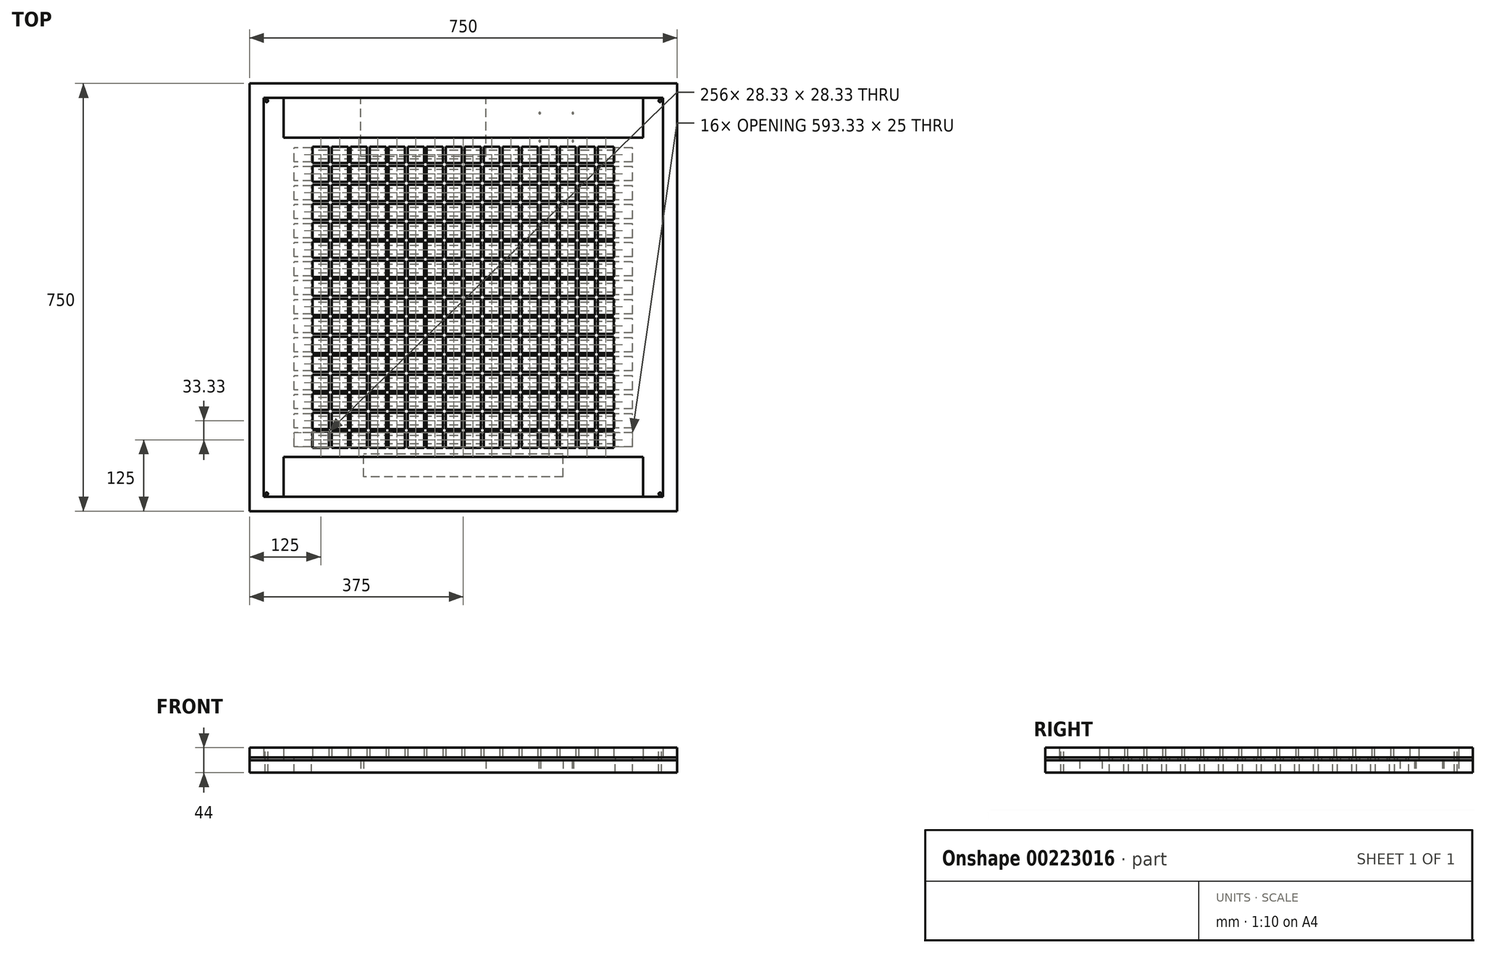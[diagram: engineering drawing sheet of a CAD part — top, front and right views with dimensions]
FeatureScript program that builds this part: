
annotation { "Feature Type Name" : "Feature", "Feature Type Description" : "" }
export const myFeature = defineFeature(function(context is Context, id is Id, definition is map)
    precondition{}
    {
        {
            var Q0;
            Q0=qCreatedBy(makeId("Top.planeOp"),FACE);
            var sketch = newSketch(context, id + "F0", { "sketchPlane" : qUnion([Q0])});
            skLineSegment(sketch, "E0.bottom", {"start": v(375, 375) * mm, "end": v(-375, 375) * mm});
            skLineSegment(sketch, "E0.top", {"start": v(375, -375) * mm, "end": v(-375, -375) * mm});
            skLineSegment(sketch, "E0.left", {"start": v(375, 375) * mm, "end": v(375, -375) * mm});
            skLineSegment(sketch, "E0.right", {"start": v(-375, 375) * mm, "end": v(-375, -375) * mm});
            skPoint(sketch, "E0.middle", {"position": v(0, 0) * mm});
            skLineSegment(sketch, "E1", {"start": v(0, 0) * mm, "end": v(0, 250) * mm});
            skLineSegment(sketch, "E2.bottom", {"start": v(266.67, 257.5) * mm, "end": v(-266.67, 257.5) * mm});
            skLineSegment(sketch, "E2.top", {"start": v(266.67, 242.5) * mm, "end": v(-266.67, 242.5) * mm});
            skLineSegment(sketch, "E2.left", {"start": v(266.67, 257.5) * mm, "end": v(266.67, 242.5) * mm});
            skLineSegment(sketch, "E2.right", {"start": v(-266.67, 257.5) * mm, "end": v(-266.67, 242.5) * mm});
            skPoint(sketch, "E2.middle", {"position": v(0, 250) * mm});
            skLineSegment(sketch, "E3.0.1.0", {"start": v(266.67, 224.17) * mm, "end": v(-266.67, 224.17) * mm});
            skLineSegment(sketch, "E3.0.1.1", {"start": v(266.67, 209.17) * mm, "end": v(-266.67, 209.17) * mm});
            skLineSegment(sketch, "E3.0.1.2", {"start": v(266.67, 224.17) * mm, "end": v(266.67, 209.17) * mm});
            skLineSegment(sketch, "E3.0.1.3", {"start": v(-266.67, 224.17) * mm, "end": v(-266.67, 209.17) * mm});
            skLineSegment(sketch, "E3.direction1", {"start": v(-266.67, 257.5) * mm, "end": v(-241.67, 257.5) * mm, "construction": true});
            skLineSegment(sketch, "E3.direction2", {"start": v(-266.67, 257.5) * mm, "end": v(-266.67, 224.17) * mm, "construction": true});
            skLineSegment(sketch, "E4.0.0.2", {"start": v(266.67, 190.83) * mm, "end": v(-266.67, 190.83) * mm});
            skLineSegment(sketch, "E4.3.0.2", {"start": v(266.67, 175.83) * mm, "end": v(-266.67, 175.83) * mm});
            skLineSegment(sketch, "E4.6.0.2", {"start": v(266.67, 190.83) * mm, "end": v(266.67, 175.83) * mm});
            skLineSegment(sketch, "E4.9.0.2", {"start": v(-266.67, 190.83) * mm, "end": v(-266.67, 175.83) * mm});
            skLineSegment(sketch, "E4.0.0.3", {"start": v(266.67, 157.5) * mm, "end": v(-266.67, 157.5) * mm});
            skLineSegment(sketch, "E4.3.0.3", {"start": v(266.67, 142.5) * mm, "end": v(-266.67, 142.5) * mm});
            skLineSegment(sketch, "E4.6.0.3", {"start": v(266.67, 157.5) * mm, "end": v(266.67, 142.5) * mm});
            skLineSegment(sketch, "E4.9.0.3", {"start": v(-266.67, 157.5) * mm, "end": v(-266.67, 142.5) * mm});
            skLineSegment(sketch, "E4.0.0.4", {"start": v(266.67, 124.17) * mm, "end": v(-266.67, 124.17) * mm});
            skLineSegment(sketch, "E4.3.0.4", {"start": v(266.67, 109.17) * mm, "end": v(-266.67, 109.17) * mm});
            skLineSegment(sketch, "E4.6.0.4", {"start": v(266.67, 124.17) * mm, "end": v(266.67, 109.17) * mm});
            skLineSegment(sketch, "E4.9.0.4", {"start": v(-266.67, 124.17) * mm, "end": v(-266.67, 109.17) * mm});
            skLineSegment(sketch, "E4.0.0.5", {"start": v(266.67, 90.83) * mm, "end": v(-266.67, 90.83) * mm});
            skLineSegment(sketch, "E4.3.0.5", {"start": v(266.67, 75.83) * mm, "end": v(-266.67, 75.83) * mm});
            skLineSegment(sketch, "E4.6.0.5", {"start": v(266.67, 90.83) * mm, "end": v(266.67, 75.83) * mm});
            skLineSegment(sketch, "E4.9.0.5", {"start": v(-266.67, 90.83) * mm, "end": v(-266.67, 75.83) * mm});
            skLineSegment(sketch, "E4.0.0.6", {"start": v(266.67, 57.5) * mm, "end": v(-266.67, 57.5) * mm});
            skLineSegment(sketch, "E4.3.0.6", {"start": v(266.67, 42.5) * mm, "end": v(-266.67, 42.5) * mm});
            skLineSegment(sketch, "E4.6.0.6", {"start": v(266.67, 57.5) * mm, "end": v(266.67, 42.5) * mm});
            skLineSegment(sketch, "E4.9.0.6", {"start": v(-266.67, 57.5) * mm, "end": v(-266.67, 42.5) * mm});
            skLineSegment(sketch, "E4.0.0.7", {"start": v(266.67, 24.17) * mm, "end": v(-266.67, 24.17) * mm});
            skLineSegment(sketch, "E4.3.0.7", {"start": v(266.67, 9.17) * mm, "end": v(-266.67, 9.17) * mm});
            skLineSegment(sketch, "E4.6.0.7", {"start": v(266.67, 24.17) * mm, "end": v(266.67, 9.17) * mm});
            skLineSegment(sketch, "E4.9.0.7", {"start": v(-266.67, 24.17) * mm, "end": v(-266.67, 9.17) * mm});
            skLineSegment(sketch, "E4.0.0.8", {"start": v(266.67, -9.17) * mm, "end": v(-266.67, -9.17) * mm});
            skLineSegment(sketch, "E4.3.0.8", {"start": v(266.67, -24.17) * mm, "end": v(-266.67, -24.17) * mm});
            skLineSegment(sketch, "E4.6.0.8", {"start": v(266.67, -9.17) * mm, "end": v(266.67, -24.17) * mm});
            skLineSegment(sketch, "E4.9.0.8", {"start": v(-266.67, -9.17) * mm, "end": v(-266.67, -24.17) * mm});
            skLineSegment(sketch, "E4.0.0.9", {"start": v(266.67, -42.5) * mm, "end": v(-266.67, -42.5) * mm});
            skLineSegment(sketch, "E4.3.0.9", {"start": v(266.67, -57.5) * mm, "end": v(-266.67, -57.5) * mm});
            skLineSegment(sketch, "E4.6.0.9", {"start": v(266.67, -42.5) * mm, "end": v(266.67, -57.5) * mm});
            skLineSegment(sketch, "E4.9.0.9", {"start": v(-266.67, -42.5) * mm, "end": v(-266.67, -57.5) * mm});
            skLineSegment(sketch, "E4.0.0.10", {"start": v(266.67, -75.83) * mm, "end": v(-266.67, -75.83) * mm});
            skLineSegment(sketch, "E4.3.0.10", {"start": v(266.67, -90.83) * mm, "end": v(-266.67, -90.83) * mm});
            skLineSegment(sketch, "E4.6.0.10", {"start": v(266.67, -75.83) * mm, "end": v(266.67, -90.83) * mm});
            skLineSegment(sketch, "E4.9.0.10", {"start": v(-266.67, -75.83) * mm, "end": v(-266.67, -90.83) * mm});
            skLineSegment(sketch, "E4.0.0.11", {"start": v(266.67, -109.17) * mm, "end": v(-266.67, -109.17) * mm});
            skLineSegment(sketch, "E4.3.0.11", {"start": v(266.67, -124.17) * mm, "end": v(-266.67, -124.17) * mm});
            skLineSegment(sketch, "E4.6.0.11", {"start": v(266.67, -109.17) * mm, "end": v(266.67, -124.17) * mm});
            skLineSegment(sketch, "E4.9.0.11", {"start": v(-266.67, -109.17) * mm, "end": v(-266.67, -124.17) * mm});
            skLineSegment(sketch, "E4.0.0.12", {"start": v(266.67, -142.5) * mm, "end": v(-266.67, -142.5) * mm});
            skLineSegment(sketch, "E4.3.0.12", {"start": v(266.67, -157.5) * mm, "end": v(-266.67, -157.5) * mm});
            skLineSegment(sketch, "E4.6.0.12", {"start": v(266.67, -142.5) * mm, "end": v(266.67, -157.5) * mm});
            skLineSegment(sketch, "E4.9.0.12", {"start": v(-266.67, -142.5) * mm, "end": v(-266.67, -157.5) * mm});
            skLineSegment(sketch, "E4.0.0.13", {"start": v(266.67, -175.83) * mm, "end": v(-266.67, -175.83) * mm});
            skLineSegment(sketch, "E4.3.0.13", {"start": v(266.67, -190.83) * mm, "end": v(-266.67, -190.83) * mm});
            skLineSegment(sketch, "E4.6.0.13", {"start": v(266.67, -175.83) * mm, "end": v(266.67, -190.83) * mm});
            skLineSegment(sketch, "E4.9.0.13", {"start": v(-266.67, -175.83) * mm, "end": v(-266.67, -190.83) * mm});
            skLineSegment(sketch, "E4.0.0.14", {"start": v(266.67, -209.17) * mm, "end": v(-266.67, -209.17) * mm});
            skLineSegment(sketch, "E4.3.0.14", {"start": v(266.67, -224.17) * mm, "end": v(-266.67, -224.17) * mm});
            skLineSegment(sketch, "E4.6.0.14", {"start": v(266.67, -209.17) * mm, "end": v(266.67, -224.17) * mm});
            skLineSegment(sketch, "E4.9.0.14", {"start": v(-266.67, -209.17) * mm, "end": v(-266.67, -224.17) * mm});
            skLineSegment(sketch, "E4.0.0.15", {"start": v(266.67, -242.5) * mm, "end": v(-266.67, -242.5) * mm});
            skLineSegment(sketch, "E4.3.0.15", {"start": v(266.67, -257.5) * mm, "end": v(-266.67, -257.5) * mm});
            skLineSegment(sketch, "E4.6.0.15", {"start": v(266.67, -242.5) * mm, "end": v(266.67, -257.5) * mm});
            skLineSegment(sketch, "E4.9.0.15", {"start": v(-266.67, -242.5) * mm, "end": v(-266.67, -257.5) * mm});
            skSolve(sketch);
        }
        {
            assignVariable(context, id + "F1", {"name" : "D1", "anyValue" : 22 * mm});
        }
        {
            assignVariable(context, id + "F2", {"name" : "D2", "anyValue" : 5 * mm});
        }
        {
            assignVariable(context, id + "F3", {"name" : "D3", "anyValue" : 22 * mm});
        }
        {
            var Q0;
            Q0=makeQuery(id+"F0.imprint","IMPRINT",FACE,{"disambiguationData":[TD([[makeQuery(id+"F0.imprint","IMPRINT",EDGE,{"derivedFrom":sQuery(id+"F0.wireOp",EDGE,"E0.bottom")}),1.0]])]});
            extrude(context, id + "F4", {"entities" : qUnion([Q0]), "depth" : getVariable(context, 'D2')});
        }
        {
            var Q0;
            Q0=qCreatedBy(makeId("Top.planeOp"),FACE);
            var sketch = newSketch(context, id + "F5", { "sketchPlane" : qUnion([Q0])});
            skLineSegment(sketch, "E5.bottom", {"start": v(375, 375) * mm, "end": v(-375, 375) * mm});
            skLineSegment(sketch, "E5.top", {"start": v(375, -375) * mm, "end": v(-375, -375) * mm});
            skLineSegment(sketch, "E5.left", {"start": v(375, 375) * mm, "end": v(375, -375) * mm});
            skLineSegment(sketch, "E5.right", {"start": v(-375, 375) * mm, "end": v(-375, -375) * mm});
            skPoint(sketch, "E5.middle", {"position": v(0, 0) * mm});
            skLineSegment(sketch, "E6", {"start": v(-375, 309.93) * mm, "end": v(375, 309.93) * mm, "construction": true});
            skLineSegment(sketch, "E7", {"start": v(-129.25, 375) * mm, "end": v(-129.25, 309.93) * mm, "construction": true});
            skLineSegment(sketch, "E8", {"start": v(106.9, 375) * mm, "end": v(106.9, 309.93) * mm, "construction": true});
            skSolve(sketch);
        }
        {
            var Q0;
            Q0 = qSketchRegion(id + "F5", true);
            extrude(context, id + "F6", {"entities" : qUnion([Q0]), "oppositeDirection" : true, "depth" : getVariable(context, 'D1')});
        }
        {
            var Q0;
            Q0=qCreatedBy(makeId("Top.planeOp"),FACE);
            var sketch = newSketch(context, id + "F7", { "sketchPlane" : qUnion([Q0])});
            skLineSegment(sketch, "E9.bottom", {"start": v(375, 375) * mm, "end": v(-375, 375) * mm});
            skLineSegment(sketch, "E9.top", {"start": v(375, -375) * mm, "end": v(-375, -375) * mm});
            skLineSegment(sketch, "E9.left", {"start": v(375, 375) * mm, "end": v(375, -375) * mm});
            skLineSegment(sketch, "E9.right", {"start": v(-375, 375) * mm, "end": v(-375, -375) * mm});
            skPoint(sketch, "E9.middle", {"position": v(0, 0) * mm});
            skLineSegment(sketch, "E10.bottom", {"start": v(0, 0) * mm, "end": v(-250, 0) * mm, "construction": true});
            skLineSegment(sketch, "E10.top", {"start": v(0, -250) * mm, "end": v(-250, -250) * mm, "construction": true});
            skLineSegment(sketch, "E10.left", {"start": v(0, 0) * mm, "end": v(0, -250) * mm, "construction": true});
            skLineSegment(sketch, "E10.right", {"start": v(-250, 0) * mm, "end": v(-250, -250) * mm, "construction": true});
            skLineSegment(sketch, "E11.bottom", {"start": v(-235.83, -235.83) * mm, "end": v(-264.17, -235.83) * mm});
            skLineSegment(sketch, "E11.top", {"start": v(-235.83, -264.17) * mm, "end": v(-264.17, -264.17) * mm});
            skLineSegment(sketch, "E11.left", {"start": v(-235.83, -235.83) * mm, "end": v(-235.83, -264.17) * mm});
            skLineSegment(sketch, "E11.right", {"start": v(-264.17, -235.83) * mm, "end": v(-264.17, -264.17) * mm});
            skPoint(sketch, "E11.middle", {"position": v(-250, -250) * mm});
            skLineSegment(sketch, "E12.0.1.0", {"start": v(-235.83, -202.5) * mm, "end": v(-264.17, -202.5) * mm});
            skLineSegment(sketch, "E12.0.1.1", {"start": v(-264.17, -202.5) * mm, "end": v(-264.17, -230.84) * mm});
            skLineSegment(sketch, "E12.0.1.2", {"start": v(-235.83, -230.84) * mm, "end": v(-264.17, -230.84) * mm});
            skLineSegment(sketch, "E12.0.1.3", {"start": v(-235.83, -202.5) * mm, "end": v(-235.83, -230.84) * mm});
            skLineSegment(sketch, "E12.0.2.0", {"start": v(-235.83, -169.17) * mm, "end": v(-264.17, -169.17) * mm});
            skLineSegment(sketch, "E12.0.2.1", {"start": v(-264.17, -169.17) * mm, "end": v(-264.17, -197.5) * mm});
            skLineSegment(sketch, "E12.0.2.2", {"start": v(-235.83, -197.5) * mm, "end": v(-264.17, -197.5) * mm});
            skLineSegment(sketch, "E12.0.2.3", {"start": v(-235.83, -169.17) * mm, "end": v(-235.83, -197.5) * mm});
            skLineSegment(sketch, "E12.0.3.0", {"start": v(-235.83, -135.84) * mm, "end": v(-264.17, -135.84) * mm});
            skLineSegment(sketch, "E12.0.3.1", {"start": v(-264.17, -135.84) * mm, "end": v(-264.17, -164.18) * mm});
            skLineSegment(sketch, "E12.0.3.2", {"start": v(-235.83, -164.18) * mm, "end": v(-264.17, -164.18) * mm});
            skLineSegment(sketch, "E12.0.3.3", {"start": v(-235.83, -135.84) * mm, "end": v(-235.83, -164.18) * mm});
            skLineSegment(sketch, "E12.0.4.0", {"start": v(-235.83, -102.51) * mm, "end": v(-264.17, -102.51) * mm});
            skLineSegment(sketch, "E12.0.4.1", {"start": v(-264.17, -102.51) * mm, "end": v(-264.17, -130.85) * mm});
            skLineSegment(sketch, "E12.0.4.2", {"start": v(-235.83, -130.85) * mm, "end": v(-264.17, -130.85) * mm});
            skLineSegment(sketch, "E12.0.4.3", {"start": v(-235.83, -102.51) * mm, "end": v(-235.83, -130.85) * mm});
            skLineSegment(sketch, "E12.0.5.0", {"start": v(-235.83, -69.18) * mm, "end": v(-264.17, -69.18) * mm});
            skLineSegment(sketch, "E12.0.5.1", {"start": v(-264.17, -69.18) * mm, "end": v(-264.17, -97.52) * mm});
            skLineSegment(sketch, "E12.0.5.2", {"start": v(-235.83, -97.52) * mm, "end": v(-264.17, -97.52) * mm});
            skLineSegment(sketch, "E12.0.5.3", {"start": v(-235.83, -69.18) * mm, "end": v(-235.83, -97.52) * mm});
            skLineSegment(sketch, "E12.0.6.0", {"start": v(-235.83, -35.85) * mm, "end": v(-264.17, -35.85) * mm});
            skLineSegment(sketch, "E12.0.6.1", {"start": v(-264.17, -35.85) * mm, "end": v(-264.17, -64.19) * mm});
            skLineSegment(sketch, "E12.0.6.2", {"start": v(-235.83, -64.19) * mm, "end": v(-264.17, -64.19) * mm});
            skLineSegment(sketch, "E12.0.6.3", {"start": v(-235.83, -35.85) * mm, "end": v(-235.83, -64.19) * mm});
            skLineSegment(sketch, "E12.0.7.0", {"start": v(-235.83, -2.52) * mm, "end": v(-264.17, -2.52) * mm});
            skLineSegment(sketch, "E12.0.7.1", {"start": v(-264.17, -2.52) * mm, "end": v(-264.17, -30.86) * mm});
            skLineSegment(sketch, "E12.0.7.2", {"start": v(-235.83, -30.86) * mm, "end": v(-264.17, -30.86) * mm});
            skLineSegment(sketch, "E12.0.7.3", {"start": v(-235.83, -2.52) * mm, "end": v(-235.83, -30.86) * mm});
            skLineSegment(sketch, "E12.0.8.0", {"start": v(-235.83, 30.8) * mm, "end": v(-264.17, 30.8) * mm});
            skLineSegment(sketch, "E12.0.8.1", {"start": v(-264.17, 30.8) * mm, "end": v(-264.17, 2.47) * mm});
            skLineSegment(sketch, "E12.0.8.2", {"start": v(-235.83, 2.47) * mm, "end": v(-264.17, 2.47) * mm});
            skLineSegment(sketch, "E12.0.8.3", {"start": v(-235.83, 30.8) * mm, "end": v(-235.83, 2.47) * mm});
            skLineSegment(sketch, "E12.0.9.0", {"start": v(-235.83, 64.14) * mm, "end": v(-264.17, 64.14) * mm});
            skLineSegment(sketch, "E12.0.9.1", {"start": v(-264.17, 64.14) * mm, "end": v(-264.17, 35.8) * mm});
            skLineSegment(sketch, "E12.0.9.2", {"start": v(-235.83, 35.8) * mm, "end": v(-264.17, 35.8) * mm});
            skLineSegment(sketch, "E12.0.9.3", {"start": v(-235.83, 64.14) * mm, "end": v(-235.83, 35.8) * mm});
            skLineSegment(sketch, "E12.0.10.0", {"start": v(-235.83, 97.47) * mm, "end": v(-264.17, 97.47) * mm});
            skLineSegment(sketch, "E12.0.10.1", {"start": v(-264.17, 97.47) * mm, "end": v(-264.17, 69.13) * mm});
            skLineSegment(sketch, "E12.0.10.2", {"start": v(-235.83, 69.13) * mm, "end": v(-264.17, 69.13) * mm});
            skLineSegment(sketch, "E12.0.10.3", {"start": v(-235.83, 97.47) * mm, "end": v(-235.83, 69.13) * mm});
            skLineSegment(sketch, "E12.0.11.0", {"start": v(-235.83, 130.8) * mm, "end": v(-264.17, 130.8) * mm});
            skLineSegment(sketch, "E12.0.11.1", {"start": v(-264.17, 130.8) * mm, "end": v(-264.17, 102.46) * mm});
            skLineSegment(sketch, "E12.0.11.2", {"start": v(-235.83, 102.46) * mm, "end": v(-264.17, 102.46) * mm});
            skLineSegment(sketch, "E12.0.11.3", {"start": v(-235.83, 130.8) * mm, "end": v(-235.83, 102.46) * mm});
            skLineSegment(sketch, "E12.0.12.0", {"start": v(-235.83, 164.13) * mm, "end": v(-264.17, 164.13) * mm});
            skLineSegment(sketch, "E12.0.12.1", {"start": v(-264.17, 164.13) * mm, "end": v(-264.17, 135.8) * mm});
            skLineSegment(sketch, "E12.0.12.2", {"start": v(-235.83, 135.8) * mm, "end": v(-264.17, 135.8) * mm});
            skLineSegment(sketch, "E12.0.12.3", {"start": v(-235.83, 164.13) * mm, "end": v(-235.83, 135.8) * mm});
            skLineSegment(sketch, "E12.0.13.0", {"start": v(-235.83, 197.46) * mm, "end": v(-264.17, 197.46) * mm});
            skLineSegment(sketch, "E12.0.13.1", {"start": v(-264.17, 197.46) * mm, "end": v(-264.17, 169.12) * mm});
            skLineSegment(sketch, "E12.0.13.2", {"start": v(-235.83, 169.12) * mm, "end": v(-264.17, 169.12) * mm});
            skLineSegment(sketch, "E12.0.13.3", {"start": v(-235.83, 197.46) * mm, "end": v(-235.83, 169.12) * mm});
            skLineSegment(sketch, "E12.0.14.0", {"start": v(-235.83, 230.79) * mm, "end": v(-264.17, 230.79) * mm});
            skLineSegment(sketch, "E12.0.14.1", {"start": v(-264.17, 230.79) * mm, "end": v(-264.17, 202.45) * mm});
            skLineSegment(sketch, "E12.0.14.2", {"start": v(-235.83, 202.45) * mm, "end": v(-264.17, 202.45) * mm});
            skLineSegment(sketch, "E12.0.14.3", {"start": v(-235.83, 230.79) * mm, "end": v(-235.83, 202.45) * mm});
            skLineSegment(sketch, "E12.0.15.0", {"start": v(-235.83, 264.12) * mm, "end": v(-264.17, 264.12) * mm});
            skLineSegment(sketch, "E12.0.15.1", {"start": v(-264.17, 264.12) * mm, "end": v(-264.17, 235.78) * mm});
            skLineSegment(sketch, "E12.0.15.2", {"start": v(-235.83, 235.78) * mm, "end": v(-264.17, 235.78) * mm});
            skLineSegment(sketch, "E12.0.15.3", {"start": v(-235.83, 264.12) * mm, "end": v(-235.83, 235.78) * mm});
            skLineSegment(sketch, "E12.1.0.0", {"start": v(-202.5, -235.83) * mm, "end": v(-230.84, -235.83) * mm});
            skLineSegment(sketch, "E12.1.0.1", {"start": v(-230.84, -235.83) * mm, "end": v(-230.84, -264.17) * mm});
            skLineSegment(sketch, "E12.1.0.2", {"start": v(-202.5, -264.17) * mm, "end": v(-230.84, -264.17) * mm});
            skLineSegment(sketch, "E12.1.0.3", {"start": v(-202.5, -235.83) * mm, "end": v(-202.5, -264.17) * mm});
            skLineSegment(sketch, "E12.1.1.0", {"start": v(-202.5, -202.5) * mm, "end": v(-230.84, -202.5) * mm});
            skLineSegment(sketch, "E12.1.1.1", {"start": v(-230.84, -202.5) * mm, "end": v(-230.84, -230.84) * mm});
            skLineSegment(sketch, "E12.1.1.2", {"start": v(-202.5, -230.84) * mm, "end": v(-230.84, -230.84) * mm});
            skLineSegment(sketch, "E12.1.1.3", {"start": v(-202.5, -202.5) * mm, "end": v(-202.5, -230.84) * mm});
            skLineSegment(sketch, "E12.1.2.0", {"start": v(-202.5, -169.17) * mm, "end": v(-230.84, -169.17) * mm});
            skLineSegment(sketch, "E12.1.2.1", {"start": v(-230.84, -169.17) * mm, "end": v(-230.84, -197.5) * mm});
            skLineSegment(sketch, "E12.1.2.2", {"start": v(-202.5, -197.5) * mm, "end": v(-230.84, -197.5) * mm});
            skLineSegment(sketch, "E12.1.2.3", {"start": v(-202.5, -169.17) * mm, "end": v(-202.5, -197.5) * mm});
            skLineSegment(sketch, "E12.1.3.0", {"start": v(-202.5, -135.84) * mm, "end": v(-230.84, -135.84) * mm});
            skLineSegment(sketch, "E12.1.3.1", {"start": v(-230.84, -135.84) * mm, "end": v(-230.84, -164.18) * mm});
            skLineSegment(sketch, "E12.1.3.2", {"start": v(-202.5, -164.18) * mm, "end": v(-230.84, -164.18) * mm});
            skLineSegment(sketch, "E12.1.3.3", {"start": v(-202.5, -135.84) * mm, "end": v(-202.5, -164.18) * mm});
            skLineSegment(sketch, "E12.1.4.0", {"start": v(-202.5, -102.51) * mm, "end": v(-230.84, -102.51) * mm});
            skLineSegment(sketch, "E12.1.4.1", {"start": v(-230.84, -102.51) * mm, "end": v(-230.84, -130.85) * mm});
            skLineSegment(sketch, "E12.1.4.2", {"start": v(-202.5, -130.85) * mm, "end": v(-230.84, -130.85) * mm});
            skLineSegment(sketch, "E12.1.4.3", {"start": v(-202.5, -102.51) * mm, "end": v(-202.5, -130.85) * mm});
            skLineSegment(sketch, "E12.1.5.0", {"start": v(-202.5, -69.18) * mm, "end": v(-230.84, -69.18) * mm});
            skLineSegment(sketch, "E12.1.5.1", {"start": v(-230.84, -69.18) * mm, "end": v(-230.84, -97.52) * mm});
            skLineSegment(sketch, "E12.1.5.2", {"start": v(-202.5, -97.52) * mm, "end": v(-230.84, -97.52) * mm});
            skLineSegment(sketch, "E12.1.5.3", {"start": v(-202.5, -69.18) * mm, "end": v(-202.5, -97.52) * mm});
            skLineSegment(sketch, "E12.1.6.0", {"start": v(-202.5, -35.85) * mm, "end": v(-230.84, -35.85) * mm});
            skLineSegment(sketch, "E12.1.6.1", {"start": v(-230.84, -35.85) * mm, "end": v(-230.84, -64.19) * mm});
            skLineSegment(sketch, "E12.1.6.2", {"start": v(-202.5, -64.19) * mm, "end": v(-230.84, -64.19) * mm});
            skLineSegment(sketch, "E12.1.6.3", {"start": v(-202.5, -35.85) * mm, "end": v(-202.5, -64.19) * mm});
            skLineSegment(sketch, "E12.1.7.0", {"start": v(-202.5, -2.52) * mm, "end": v(-230.84, -2.52) * mm});
            skLineSegment(sketch, "E12.1.7.1", {"start": v(-230.84, -2.52) * mm, "end": v(-230.84, -30.86) * mm});
            skLineSegment(sketch, "E12.1.7.2", {"start": v(-202.5, -30.86) * mm, "end": v(-230.84, -30.86) * mm});
            skLineSegment(sketch, "E12.1.7.3", {"start": v(-202.5, -2.52) * mm, "end": v(-202.5, -30.86) * mm});
            skLineSegment(sketch, "E12.1.8.0", {"start": v(-202.5, 30.8) * mm, "end": v(-230.84, 30.8) * mm});
            skLineSegment(sketch, "E12.1.8.1", {"start": v(-230.84, 30.8) * mm, "end": v(-230.84, 2.47) * mm});
            skLineSegment(sketch, "E12.1.8.2", {"start": v(-202.5, 2.47) * mm, "end": v(-230.84, 2.47) * mm});
            skLineSegment(sketch, "E12.1.8.3", {"start": v(-202.5, 30.8) * mm, "end": v(-202.5, 2.47) * mm});
            skLineSegment(sketch, "E12.1.9.0", {"start": v(-202.5, 64.14) * mm, "end": v(-230.84, 64.14) * mm});
            skLineSegment(sketch, "E12.1.9.1", {"start": v(-230.84, 64.14) * mm, "end": v(-230.84, 35.8) * mm});
            skLineSegment(sketch, "E12.1.9.2", {"start": v(-202.5, 35.8) * mm, "end": v(-230.84, 35.8) * mm});
            skLineSegment(sketch, "E12.1.9.3", {"start": v(-202.5, 64.14) * mm, "end": v(-202.5, 35.8) * mm});
            skLineSegment(sketch, "E12.1.10.0", {"start": v(-202.5, 97.47) * mm, "end": v(-230.84, 97.47) * mm});
            skLineSegment(sketch, "E12.1.10.1", {"start": v(-230.84, 97.47) * mm, "end": v(-230.84, 69.13) * mm});
            skLineSegment(sketch, "E12.1.10.2", {"start": v(-202.5, 69.13) * mm, "end": v(-230.84, 69.13) * mm});
            skLineSegment(sketch, "E12.1.10.3", {"start": v(-202.5, 97.47) * mm, "end": v(-202.5, 69.13) * mm});
            skLineSegment(sketch, "E12.1.11.0", {"start": v(-202.5, 130.8) * mm, "end": v(-230.84, 130.8) * mm});
            skLineSegment(sketch, "E12.1.11.1", {"start": v(-230.84, 130.8) * mm, "end": v(-230.84, 102.46) * mm});
            skLineSegment(sketch, "E12.1.11.2", {"start": v(-202.5, 102.46) * mm, "end": v(-230.84, 102.46) * mm});
            skLineSegment(sketch, "E12.1.11.3", {"start": v(-202.5, 130.8) * mm, "end": v(-202.5, 102.46) * mm});
            skLineSegment(sketch, "E12.1.12.0", {"start": v(-202.5, 164.13) * mm, "end": v(-230.84, 164.13) * mm});
            skLineSegment(sketch, "E12.1.12.1", {"start": v(-230.84, 164.13) * mm, "end": v(-230.84, 135.8) * mm});
            skLineSegment(sketch, "E12.1.12.2", {"start": v(-202.5, 135.8) * mm, "end": v(-230.84, 135.8) * mm});
            skLineSegment(sketch, "E12.1.12.3", {"start": v(-202.5, 164.13) * mm, "end": v(-202.5, 135.8) * mm});
            skLineSegment(sketch, "E12.1.13.0", {"start": v(-202.5, 197.46) * mm, "end": v(-230.84, 197.46) * mm});
            skLineSegment(sketch, "E12.1.13.1", {"start": v(-230.84, 197.46) * mm, "end": v(-230.84, 169.12) * mm});
            skLineSegment(sketch, "E12.1.13.2", {"start": v(-202.5, 169.12) * mm, "end": v(-230.84, 169.12) * mm});
            skLineSegment(sketch, "E12.1.13.3", {"start": v(-202.5, 197.46) * mm, "end": v(-202.5, 169.12) * mm});
            skLineSegment(sketch, "E12.1.14.0", {"start": v(-202.5, 230.79) * mm, "end": v(-230.84, 230.79) * mm});
            skLineSegment(sketch, "E12.1.14.1", {"start": v(-230.84, 230.79) * mm, "end": v(-230.84, 202.45) * mm});
            skLineSegment(sketch, "E12.1.14.2", {"start": v(-202.5, 202.45) * mm, "end": v(-230.84, 202.45) * mm});
            skLineSegment(sketch, "E12.1.14.3", {"start": v(-202.5, 230.79) * mm, "end": v(-202.5, 202.45) * mm});
            skLineSegment(sketch, "E12.1.15.0", {"start": v(-202.5, 264.12) * mm, "end": v(-230.84, 264.12) * mm});
            skLineSegment(sketch, "E12.1.15.1", {"start": v(-230.84, 264.12) * mm, "end": v(-230.84, 235.78) * mm});
            skLineSegment(sketch, "E12.1.15.2", {"start": v(-202.5, 235.78) * mm, "end": v(-230.84, 235.78) * mm});
            skLineSegment(sketch, "E12.1.15.3", {"start": v(-202.5, 264.12) * mm, "end": v(-202.5, 235.78) * mm});
            skLineSegment(sketch, "E12.2.0.0", {"start": v(-169.17, -235.83) * mm, "end": v(-197.5, -235.83) * mm});
            skLineSegment(sketch, "E12.2.0.1", {"start": v(-197.5, -235.83) * mm, "end": v(-197.5, -264.17) * mm});
            skLineSegment(sketch, "E12.2.0.2", {"start": v(-169.17, -264.17) * mm, "end": v(-197.5, -264.17) * mm});
            skLineSegment(sketch, "E12.2.0.3", {"start": v(-169.17, -235.83) * mm, "end": v(-169.17, -264.17) * mm});
            skLineSegment(sketch, "E12.2.1.0", {"start": v(-169.17, -202.5) * mm, "end": v(-197.5, -202.5) * mm});
            skLineSegment(sketch, "E12.2.1.1", {"start": v(-197.5, -202.5) * mm, "end": v(-197.5, -230.84) * mm});
            skLineSegment(sketch, "E12.2.1.2", {"start": v(-169.17, -230.84) * mm, "end": v(-197.5, -230.84) * mm});
            skLineSegment(sketch, "E12.2.1.3", {"start": v(-169.17, -202.5) * mm, "end": v(-169.17, -230.84) * mm});
            skLineSegment(sketch, "E12.2.2.0", {"start": v(-169.17, -169.17) * mm, "end": v(-197.5, -169.17) * mm});
            skLineSegment(sketch, "E12.2.2.1", {"start": v(-197.5, -169.17) * mm, "end": v(-197.5, -197.5) * mm});
            skLineSegment(sketch, "E12.2.2.2", {"start": v(-169.17, -197.5) * mm, "end": v(-197.5, -197.5) * mm});
            skLineSegment(sketch, "E12.2.2.3", {"start": v(-169.17, -169.17) * mm, "end": v(-169.17, -197.5) * mm});
            skLineSegment(sketch, "E12.2.3.0", {"start": v(-169.17, -135.84) * mm, "end": v(-197.5, -135.84) * mm});
            skLineSegment(sketch, "E12.2.3.1", {"start": v(-197.5, -135.84) * mm, "end": v(-197.5, -164.18) * mm});
            skLineSegment(sketch, "E12.2.3.2", {"start": v(-169.17, -164.18) * mm, "end": v(-197.5, -164.18) * mm});
            skLineSegment(sketch, "E12.2.3.3", {"start": v(-169.17, -135.84) * mm, "end": v(-169.17, -164.18) * mm});
            skLineSegment(sketch, "E12.2.4.0", {"start": v(-169.17, -102.51) * mm, "end": v(-197.5, -102.51) * mm});
            skLineSegment(sketch, "E12.2.4.1", {"start": v(-197.5, -102.51) * mm, "end": v(-197.5, -130.85) * mm});
            skLineSegment(sketch, "E12.2.4.2", {"start": v(-169.17, -130.85) * mm, "end": v(-197.5, -130.85) * mm});
            skLineSegment(sketch, "E12.2.4.3", {"start": v(-169.17, -102.51) * mm, "end": v(-169.17, -130.85) * mm});
            skLineSegment(sketch, "E12.2.5.0", {"start": v(-169.17, -69.18) * mm, "end": v(-197.5, -69.18) * mm});
            skLineSegment(sketch, "E12.2.5.1", {"start": v(-197.5, -69.18) * mm, "end": v(-197.5, -97.52) * mm});
            skLineSegment(sketch, "E12.2.5.2", {"start": v(-169.17, -97.52) * mm, "end": v(-197.5, -97.52) * mm});
            skLineSegment(sketch, "E12.2.5.3", {"start": v(-169.17, -69.18) * mm, "end": v(-169.17, -97.52) * mm});
            skLineSegment(sketch, "E12.2.6.0", {"start": v(-169.17, -35.85) * mm, "end": v(-197.5, -35.85) * mm});
            skLineSegment(sketch, "E12.2.6.1", {"start": v(-197.5, -35.85) * mm, "end": v(-197.5, -64.19) * mm});
            skLineSegment(sketch, "E12.2.6.2", {"start": v(-169.17, -64.19) * mm, "end": v(-197.5, -64.19) * mm});
            skLineSegment(sketch, "E12.2.6.3", {"start": v(-169.17, -35.85) * mm, "end": v(-169.17, -64.19) * mm});
            skLineSegment(sketch, "E12.2.7.0", {"start": v(-169.17, -2.52) * mm, "end": v(-197.5, -2.52) * mm});
            skLineSegment(sketch, "E12.2.7.1", {"start": v(-197.5, -2.52) * mm, "end": v(-197.5, -30.86) * mm});
            skLineSegment(sketch, "E12.2.7.2", {"start": v(-169.17, -30.86) * mm, "end": v(-197.5, -30.86) * mm});
            skLineSegment(sketch, "E12.2.7.3", {"start": v(-169.17, -2.52) * mm, "end": v(-169.17, -30.86) * mm});
            skLineSegment(sketch, "E12.2.8.0", {"start": v(-169.17, 30.8) * mm, "end": v(-197.5, 30.8) * mm});
            skLineSegment(sketch, "E12.2.8.1", {"start": v(-197.5, 30.8) * mm, "end": v(-197.5, 2.47) * mm});
            skLineSegment(sketch, "E12.2.8.2", {"start": v(-169.17, 2.47) * mm, "end": v(-197.5, 2.47) * mm});
            skLineSegment(sketch, "E12.2.8.3", {"start": v(-169.17, 30.8) * mm, "end": v(-169.17, 2.47) * mm});
            skLineSegment(sketch, "E12.2.9.0", {"start": v(-169.17, 64.14) * mm, "end": v(-197.5, 64.14) * mm});
            skLineSegment(sketch, "E12.2.9.1", {"start": v(-197.5, 64.14) * mm, "end": v(-197.5, 35.8) * mm});
            skLineSegment(sketch, "E12.2.9.2", {"start": v(-169.17, 35.8) * mm, "end": v(-197.5, 35.8) * mm});
            skLineSegment(sketch, "E12.2.9.3", {"start": v(-169.17, 64.14) * mm, "end": v(-169.17, 35.8) * mm});
            skLineSegment(sketch, "E12.2.10.0", {"start": v(-169.17, 97.47) * mm, "end": v(-197.5, 97.47) * mm});
            skLineSegment(sketch, "E12.2.10.1", {"start": v(-197.5, 97.47) * mm, "end": v(-197.5, 69.13) * mm});
            skLineSegment(sketch, "E12.2.10.2", {"start": v(-169.17, 69.13) * mm, "end": v(-197.5, 69.13) * mm});
            skLineSegment(sketch, "E12.2.10.3", {"start": v(-169.17, 97.47) * mm, "end": v(-169.17, 69.13) * mm});
            skLineSegment(sketch, "E12.2.11.0", {"start": v(-169.17, 130.8) * mm, "end": v(-197.5, 130.8) * mm});
            skLineSegment(sketch, "E12.2.11.1", {"start": v(-197.5, 130.8) * mm, "end": v(-197.5, 102.46) * mm});
            skLineSegment(sketch, "E12.2.11.2", {"start": v(-169.17, 102.46) * mm, "end": v(-197.5, 102.46) * mm});
            skLineSegment(sketch, "E12.2.11.3", {"start": v(-169.17, 130.8) * mm, "end": v(-169.17, 102.46) * mm});
            skLineSegment(sketch, "E12.2.12.0", {"start": v(-169.17, 164.13) * mm, "end": v(-197.5, 164.13) * mm});
            skLineSegment(sketch, "E12.2.12.1", {"start": v(-197.5, 164.13) * mm, "end": v(-197.5, 135.8) * mm});
            skLineSegment(sketch, "E12.2.12.2", {"start": v(-169.17, 135.8) * mm, "end": v(-197.5, 135.8) * mm});
            skLineSegment(sketch, "E12.2.12.3", {"start": v(-169.17, 164.13) * mm, "end": v(-169.17, 135.8) * mm});
            skLineSegment(sketch, "E12.2.13.0", {"start": v(-169.17, 197.46) * mm, "end": v(-197.5, 197.46) * mm});
            skLineSegment(sketch, "E12.2.13.1", {"start": v(-197.5, 197.46) * mm, "end": v(-197.5, 169.12) * mm});
            skLineSegment(sketch, "E12.2.13.2", {"start": v(-169.17, 169.12) * mm, "end": v(-197.5, 169.12) * mm});
            skLineSegment(sketch, "E12.2.13.3", {"start": v(-169.17, 197.46) * mm, "end": v(-169.17, 169.12) * mm});
            skLineSegment(sketch, "E12.2.14.0", {"start": v(-169.17, 230.79) * mm, "end": v(-197.5, 230.79) * mm});
            skLineSegment(sketch, "E12.2.14.1", {"start": v(-197.5, 230.79) * mm, "end": v(-197.5, 202.45) * mm});
            skLineSegment(sketch, "E12.2.14.2", {"start": v(-169.17, 202.45) * mm, "end": v(-197.5, 202.45) * mm});
            skLineSegment(sketch, "E12.2.14.3", {"start": v(-169.17, 230.79) * mm, "end": v(-169.17, 202.45) * mm});
            skLineSegment(sketch, "E12.2.15.0", {"start": v(-169.17, 264.12) * mm, "end": v(-197.5, 264.12) * mm});
            skLineSegment(sketch, "E12.2.15.1", {"start": v(-197.5, 264.12) * mm, "end": v(-197.5, 235.78) * mm});
            skLineSegment(sketch, "E12.2.15.2", {"start": v(-169.17, 235.78) * mm, "end": v(-197.5, 235.78) * mm});
            skLineSegment(sketch, "E12.2.15.3", {"start": v(-169.17, 264.12) * mm, "end": v(-169.17, 235.78) * mm});
            skLineSegment(sketch, "E12.3.0.0", {"start": v(-135.84, -235.83) * mm, "end": v(-164.18, -235.83) * mm});
            skLineSegment(sketch, "E12.3.0.1", {"start": v(-164.18, -235.83) * mm, "end": v(-164.18, -264.17) * mm});
            skLineSegment(sketch, "E12.3.0.2", {"start": v(-135.84, -264.17) * mm, "end": v(-164.18, -264.17) * mm});
            skLineSegment(sketch, "E12.3.0.3", {"start": v(-135.84, -235.83) * mm, "end": v(-135.84, -264.17) * mm});
            skLineSegment(sketch, "E12.3.1.0", {"start": v(-135.84, -202.5) * mm, "end": v(-164.18, -202.5) * mm});
            skLineSegment(sketch, "E12.3.1.1", {"start": v(-164.18, -202.5) * mm, "end": v(-164.18, -230.84) * mm});
            skLineSegment(sketch, "E12.3.1.2", {"start": v(-135.84, -230.84) * mm, "end": v(-164.18, -230.84) * mm});
            skLineSegment(sketch, "E12.3.1.3", {"start": v(-135.84, -202.5) * mm, "end": v(-135.84, -230.84) * mm});
            skLineSegment(sketch, "E12.3.2.0", {"start": v(-135.84, -169.17) * mm, "end": v(-164.18, -169.17) * mm});
            skLineSegment(sketch, "E12.3.2.1", {"start": v(-164.18, -169.17) * mm, "end": v(-164.18, -197.5) * mm});
            skLineSegment(sketch, "E12.3.2.2", {"start": v(-135.84, -197.5) * mm, "end": v(-164.18, -197.5) * mm});
            skLineSegment(sketch, "E12.3.2.3", {"start": v(-135.84, -169.17) * mm, "end": v(-135.84, -197.5) * mm});
            skLineSegment(sketch, "E12.3.3.0", {"start": v(-135.84, -135.84) * mm, "end": v(-164.18, -135.84) * mm});
            skLineSegment(sketch, "E12.3.3.1", {"start": v(-164.18, -135.84) * mm, "end": v(-164.18, -164.18) * mm});
            skLineSegment(sketch, "E12.3.3.2", {"start": v(-135.84, -164.18) * mm, "end": v(-164.18, -164.18) * mm});
            skLineSegment(sketch, "E12.3.3.3", {"start": v(-135.84, -135.84) * mm, "end": v(-135.84, -164.18) * mm});
            skLineSegment(sketch, "E12.3.4.0", {"start": v(-135.84, -102.51) * mm, "end": v(-164.18, -102.51) * mm});
            skLineSegment(sketch, "E12.3.4.1", {"start": v(-164.18, -102.51) * mm, "end": v(-164.18, -130.85) * mm});
            skLineSegment(sketch, "E12.3.4.2", {"start": v(-135.84, -130.85) * mm, "end": v(-164.18, -130.85) * mm});
            skLineSegment(sketch, "E12.3.4.3", {"start": v(-135.84, -102.51) * mm, "end": v(-135.84, -130.85) * mm});
            skLineSegment(sketch, "E12.3.5.0", {"start": v(-135.84, -69.18) * mm, "end": v(-164.18, -69.18) * mm});
            skLineSegment(sketch, "E12.3.5.1", {"start": v(-164.18, -69.18) * mm, "end": v(-164.18, -97.52) * mm});
            skLineSegment(sketch, "E12.3.5.2", {"start": v(-135.84, -97.52) * mm, "end": v(-164.18, -97.52) * mm});
            skLineSegment(sketch, "E12.3.5.3", {"start": v(-135.84, -69.18) * mm, "end": v(-135.84, -97.52) * mm});
            skLineSegment(sketch, "E12.3.6.0", {"start": v(-135.84, -35.85) * mm, "end": v(-164.18, -35.85) * mm});
            skLineSegment(sketch, "E12.3.6.1", {"start": v(-164.18, -35.85) * mm, "end": v(-164.18, -64.19) * mm});
            skLineSegment(sketch, "E12.3.6.2", {"start": v(-135.84, -64.19) * mm, "end": v(-164.18, -64.19) * mm});
            skLineSegment(sketch, "E12.3.6.3", {"start": v(-135.84, -35.85) * mm, "end": v(-135.84, -64.19) * mm});
            skLineSegment(sketch, "E12.3.7.0", {"start": v(-135.84, -2.52) * mm, "end": v(-164.18, -2.52) * mm});
            skLineSegment(sketch, "E12.3.7.1", {"start": v(-164.18, -2.52) * mm, "end": v(-164.18, -30.86) * mm});
            skLineSegment(sketch, "E12.3.7.2", {"start": v(-135.84, -30.86) * mm, "end": v(-164.18, -30.86) * mm});
            skLineSegment(sketch, "E12.3.7.3", {"start": v(-135.84, -2.52) * mm, "end": v(-135.84, -30.86) * mm});
            skLineSegment(sketch, "E12.3.8.0", {"start": v(-135.84, 30.8) * mm, "end": v(-164.18, 30.8) * mm});
            skLineSegment(sketch, "E12.3.8.1", {"start": v(-164.18, 30.8) * mm, "end": v(-164.18, 2.47) * mm});
            skLineSegment(sketch, "E12.3.8.2", {"start": v(-135.84, 2.47) * mm, "end": v(-164.18, 2.47) * mm});
            skLineSegment(sketch, "E12.3.8.3", {"start": v(-135.84, 30.8) * mm, "end": v(-135.84, 2.47) * mm});
            skLineSegment(sketch, "E12.3.9.0", {"start": v(-135.84, 64.14) * mm, "end": v(-164.18, 64.14) * mm});
            skLineSegment(sketch, "E12.3.9.1", {"start": v(-164.18, 64.14) * mm, "end": v(-164.18, 35.8) * mm});
            skLineSegment(sketch, "E12.3.9.2", {"start": v(-135.84, 35.8) * mm, "end": v(-164.18, 35.8) * mm});
            skLineSegment(sketch, "E12.3.9.3", {"start": v(-135.84, 64.14) * mm, "end": v(-135.84, 35.8) * mm});
            skLineSegment(sketch, "E12.3.10.0", {"start": v(-135.84, 97.47) * mm, "end": v(-164.18, 97.47) * mm});
            skLineSegment(sketch, "E12.3.10.1", {"start": v(-164.18, 97.47) * mm, "end": v(-164.18, 69.13) * mm});
            skLineSegment(sketch, "E12.3.10.2", {"start": v(-135.84, 69.13) * mm, "end": v(-164.18, 69.13) * mm});
            skLineSegment(sketch, "E12.3.10.3", {"start": v(-135.84, 97.47) * mm, "end": v(-135.84, 69.13) * mm});
            skLineSegment(sketch, "E12.3.11.0", {"start": v(-135.84, 130.8) * mm, "end": v(-164.18, 130.8) * mm});
            skLineSegment(sketch, "E12.3.11.1", {"start": v(-164.18, 130.8) * mm, "end": v(-164.18, 102.46) * mm});
            skLineSegment(sketch, "E12.3.11.2", {"start": v(-135.84, 102.46) * mm, "end": v(-164.18, 102.46) * mm});
            skLineSegment(sketch, "E12.3.11.3", {"start": v(-135.84, 130.8) * mm, "end": v(-135.84, 102.46) * mm});
            skLineSegment(sketch, "E12.3.12.0", {"start": v(-135.84, 164.13) * mm, "end": v(-164.18, 164.13) * mm});
            skLineSegment(sketch, "E12.3.12.1", {"start": v(-164.18, 164.13) * mm, "end": v(-164.18, 135.8) * mm});
            skLineSegment(sketch, "E12.3.12.2", {"start": v(-135.84, 135.8) * mm, "end": v(-164.18, 135.8) * mm});
            skLineSegment(sketch, "E12.3.12.3", {"start": v(-135.84, 164.13) * mm, "end": v(-135.84, 135.8) * mm});
            skLineSegment(sketch, "E12.3.13.0", {"start": v(-135.84, 197.46) * mm, "end": v(-164.18, 197.46) * mm});
            skLineSegment(sketch, "E12.3.13.1", {"start": v(-164.18, 197.46) * mm, "end": v(-164.18, 169.12) * mm});
            skLineSegment(sketch, "E12.3.13.2", {"start": v(-135.84, 169.12) * mm, "end": v(-164.18, 169.12) * mm});
            skLineSegment(sketch, "E12.3.13.3", {"start": v(-135.84, 197.46) * mm, "end": v(-135.84, 169.12) * mm});
            skLineSegment(sketch, "E12.3.14.0", {"start": v(-135.84, 230.79) * mm, "end": v(-164.18, 230.79) * mm});
            skLineSegment(sketch, "E12.3.14.1", {"start": v(-164.18, 230.79) * mm, "end": v(-164.18, 202.45) * mm});
            skLineSegment(sketch, "E12.3.14.2", {"start": v(-135.84, 202.45) * mm, "end": v(-164.18, 202.45) * mm});
            skLineSegment(sketch, "E12.3.14.3", {"start": v(-135.84, 230.79) * mm, "end": v(-135.84, 202.45) * mm});
            skLineSegment(sketch, "E12.3.15.0", {"start": v(-135.84, 264.12) * mm, "end": v(-164.18, 264.12) * mm});
            skLineSegment(sketch, "E12.3.15.1", {"start": v(-164.18, 264.12) * mm, "end": v(-164.18, 235.78) * mm});
            skLineSegment(sketch, "E12.3.15.2", {"start": v(-135.84, 235.78) * mm, "end": v(-164.18, 235.78) * mm});
            skLineSegment(sketch, "E12.3.15.3", {"start": v(-135.84, 264.12) * mm, "end": v(-135.84, 235.78) * mm});
            skLineSegment(sketch, "E12.4.0.0", {"start": v(-102.51, -235.83) * mm, "end": v(-130.85, -235.83) * mm});
            skLineSegment(sketch, "E12.4.0.1", {"start": v(-130.85, -235.83) * mm, "end": v(-130.85, -264.17) * mm});
            skLineSegment(sketch, "E12.4.0.2", {"start": v(-102.51, -264.17) * mm, "end": v(-130.85, -264.17) * mm});
            skLineSegment(sketch, "E12.4.0.3", {"start": v(-102.51, -235.83) * mm, "end": v(-102.51, -264.17) * mm});
            skLineSegment(sketch, "E12.4.1.0", {"start": v(-102.51, -202.5) * mm, "end": v(-130.85, -202.5) * mm});
            skLineSegment(sketch, "E12.4.1.1", {"start": v(-130.85, -202.5) * mm, "end": v(-130.85, -230.84) * mm});
            skLineSegment(sketch, "E12.4.1.2", {"start": v(-102.51, -230.84) * mm, "end": v(-130.85, -230.84) * mm});
            skLineSegment(sketch, "E12.4.1.3", {"start": v(-102.51, -202.5) * mm, "end": v(-102.51, -230.84) * mm});
            skLineSegment(sketch, "E12.4.2.0", {"start": v(-102.51, -169.17) * mm, "end": v(-130.85, -169.17) * mm});
            skLineSegment(sketch, "E12.4.2.1", {"start": v(-130.85, -169.17) * mm, "end": v(-130.85, -197.5) * mm});
            skLineSegment(sketch, "E12.4.2.2", {"start": v(-102.51, -197.5) * mm, "end": v(-130.85, -197.5) * mm});
            skLineSegment(sketch, "E12.4.2.3", {"start": v(-102.51, -169.17) * mm, "end": v(-102.51, -197.5) * mm});
            skLineSegment(sketch, "E12.4.3.0", {"start": v(-102.51, -135.84) * mm, "end": v(-130.85, -135.84) * mm});
            skLineSegment(sketch, "E12.4.3.1", {"start": v(-130.85, -135.84) * mm, "end": v(-130.85, -164.18) * mm});
            skLineSegment(sketch, "E12.4.3.2", {"start": v(-102.51, -164.18) * mm, "end": v(-130.85, -164.18) * mm});
            skLineSegment(sketch, "E12.4.3.3", {"start": v(-102.51, -135.84) * mm, "end": v(-102.51, -164.18) * mm});
            skLineSegment(sketch, "E12.4.4.0", {"start": v(-102.51, -102.51) * mm, "end": v(-130.85, -102.51) * mm});
            skLineSegment(sketch, "E12.4.4.1", {"start": v(-130.85, -102.51) * mm, "end": v(-130.85, -130.85) * mm});
            skLineSegment(sketch, "E12.4.4.2", {"start": v(-102.51, -130.85) * mm, "end": v(-130.85, -130.85) * mm});
            skLineSegment(sketch, "E12.4.4.3", {"start": v(-102.51, -102.51) * mm, "end": v(-102.51, -130.85) * mm});
            skLineSegment(sketch, "E12.4.5.0", {"start": v(-102.51, -69.18) * mm, "end": v(-130.85, -69.18) * mm});
            skLineSegment(sketch, "E12.4.5.1", {"start": v(-130.85, -69.18) * mm, "end": v(-130.85, -97.52) * mm});
            skLineSegment(sketch, "E12.4.5.2", {"start": v(-102.51, -97.52) * mm, "end": v(-130.85, -97.52) * mm});
            skLineSegment(sketch, "E12.4.5.3", {"start": v(-102.51, -69.18) * mm, "end": v(-102.51, -97.52) * mm});
            skLineSegment(sketch, "E12.4.6.0", {"start": v(-102.51, -35.85) * mm, "end": v(-130.85, -35.85) * mm});
            skLineSegment(sketch, "E12.4.6.1", {"start": v(-130.85, -35.85) * mm, "end": v(-130.85, -64.19) * mm});
            skLineSegment(sketch, "E12.4.6.2", {"start": v(-102.51, -64.19) * mm, "end": v(-130.85, -64.19) * mm});
            skLineSegment(sketch, "E12.4.6.3", {"start": v(-102.51, -35.85) * mm, "end": v(-102.51, -64.19) * mm});
            skLineSegment(sketch, "E12.4.7.0", {"start": v(-102.51, -2.52) * mm, "end": v(-130.85, -2.52) * mm});
            skLineSegment(sketch, "E12.4.7.1", {"start": v(-130.85, -2.52) * mm, "end": v(-130.85, -30.86) * mm});
            skLineSegment(sketch, "E12.4.7.2", {"start": v(-102.51, -30.86) * mm, "end": v(-130.85, -30.86) * mm});
            skLineSegment(sketch, "E12.4.7.3", {"start": v(-102.51, -2.52) * mm, "end": v(-102.51, -30.86) * mm});
            skLineSegment(sketch, "E12.4.8.0", {"start": v(-102.51, 30.8) * mm, "end": v(-130.85, 30.8) * mm});
            skLineSegment(sketch, "E12.4.8.1", {"start": v(-130.85, 30.8) * mm, "end": v(-130.85, 2.47) * mm});
            skLineSegment(sketch, "E12.4.8.2", {"start": v(-102.51, 2.47) * mm, "end": v(-130.85, 2.47) * mm});
            skLineSegment(sketch, "E12.4.8.3", {"start": v(-102.51, 30.8) * mm, "end": v(-102.51, 2.47) * mm});
            skLineSegment(sketch, "E12.4.9.0", {"start": v(-102.51, 64.14) * mm, "end": v(-130.85, 64.14) * mm});
            skLineSegment(sketch, "E12.4.9.1", {"start": v(-130.85, 64.14) * mm, "end": v(-130.85, 35.8) * mm});
            skLineSegment(sketch, "E12.4.9.2", {"start": v(-102.51, 35.8) * mm, "end": v(-130.85, 35.8) * mm});
            skLineSegment(sketch, "E12.4.9.3", {"start": v(-102.51, 64.14) * mm, "end": v(-102.51, 35.8) * mm});
            skLineSegment(sketch, "E12.4.10.0", {"start": v(-102.51, 97.47) * mm, "end": v(-130.85, 97.47) * mm});
            skLineSegment(sketch, "E12.4.10.1", {"start": v(-130.85, 97.47) * mm, "end": v(-130.85, 69.13) * mm});
            skLineSegment(sketch, "E12.4.10.2", {"start": v(-102.51, 69.13) * mm, "end": v(-130.85, 69.13) * mm});
            skLineSegment(sketch, "E12.4.10.3", {"start": v(-102.51, 97.47) * mm, "end": v(-102.51, 69.13) * mm});
            skLineSegment(sketch, "E12.4.11.0", {"start": v(-102.51, 130.8) * mm, "end": v(-130.85, 130.8) * mm});
            skLineSegment(sketch, "E12.4.11.1", {"start": v(-130.85, 130.8) * mm, "end": v(-130.85, 102.46) * mm});
            skLineSegment(sketch, "E12.4.11.2", {"start": v(-102.51, 102.46) * mm, "end": v(-130.85, 102.46) * mm});
            skLineSegment(sketch, "E12.4.11.3", {"start": v(-102.51, 130.8) * mm, "end": v(-102.51, 102.46) * mm});
            skLineSegment(sketch, "E12.4.12.0", {"start": v(-102.51, 164.13) * mm, "end": v(-130.85, 164.13) * mm});
            skLineSegment(sketch, "E12.4.12.1", {"start": v(-130.85, 164.13) * mm, "end": v(-130.85, 135.8) * mm});
            skLineSegment(sketch, "E12.4.12.2", {"start": v(-102.51, 135.8) * mm, "end": v(-130.85, 135.8) * mm});
            skLineSegment(sketch, "E12.4.12.3", {"start": v(-102.51, 164.13) * mm, "end": v(-102.51, 135.8) * mm});
            skLineSegment(sketch, "E12.4.13.0", {"start": v(-102.51, 197.46) * mm, "end": v(-130.85, 197.46) * mm});
            skLineSegment(sketch, "E12.4.13.1", {"start": v(-130.85, 197.46) * mm, "end": v(-130.85, 169.12) * mm});
            skLineSegment(sketch, "E12.4.13.2", {"start": v(-102.51, 169.12) * mm, "end": v(-130.85, 169.12) * mm});
            skLineSegment(sketch, "E12.4.13.3", {"start": v(-102.51, 197.46) * mm, "end": v(-102.51, 169.12) * mm});
            skLineSegment(sketch, "E12.4.14.0", {"start": v(-102.51, 230.79) * mm, "end": v(-130.85, 230.79) * mm});
            skLineSegment(sketch, "E12.4.14.1", {"start": v(-130.85, 230.79) * mm, "end": v(-130.85, 202.45) * mm});
            skLineSegment(sketch, "E12.4.14.2", {"start": v(-102.51, 202.45) * mm, "end": v(-130.85, 202.45) * mm});
            skLineSegment(sketch, "E12.4.14.3", {"start": v(-102.51, 230.79) * mm, "end": v(-102.51, 202.45) * mm});
            skLineSegment(sketch, "E12.4.15.0", {"start": v(-102.51, 264.12) * mm, "end": v(-130.85, 264.12) * mm});
            skLineSegment(sketch, "E12.4.15.1", {"start": v(-130.85, 264.12) * mm, "end": v(-130.85, 235.78) * mm});
            skLineSegment(sketch, "E12.4.15.2", {"start": v(-102.51, 235.78) * mm, "end": v(-130.85, 235.78) * mm});
            skLineSegment(sketch, "E12.4.15.3", {"start": v(-102.51, 264.12) * mm, "end": v(-102.51, 235.78) * mm});
            skLineSegment(sketch, "E12.5.0.0", {"start": v(-69.18, -235.83) * mm, "end": v(-97.52, -235.83) * mm});
            skLineSegment(sketch, "E12.5.0.1", {"start": v(-97.52, -235.83) * mm, "end": v(-97.52, -264.17) * mm});
            skLineSegment(sketch, "E12.5.0.2", {"start": v(-69.18, -264.17) * mm, "end": v(-97.52, -264.17) * mm});
            skLineSegment(sketch, "E12.5.0.3", {"start": v(-69.18, -235.83) * mm, "end": v(-69.18, -264.17) * mm});
            skLineSegment(sketch, "E12.5.1.0", {"start": v(-69.18, -202.5) * mm, "end": v(-97.52, -202.5) * mm});
            skLineSegment(sketch, "E12.5.1.1", {"start": v(-97.52, -202.5) * mm, "end": v(-97.52, -230.84) * mm});
            skLineSegment(sketch, "E12.5.1.2", {"start": v(-69.18, -230.84) * mm, "end": v(-97.52, -230.84) * mm});
            skLineSegment(sketch, "E12.5.1.3", {"start": v(-69.18, -202.5) * mm, "end": v(-69.18, -230.84) * mm});
            skLineSegment(sketch, "E12.5.2.0", {"start": v(-69.18, -169.17) * mm, "end": v(-97.52, -169.17) * mm});
            skLineSegment(sketch, "E12.5.2.1", {"start": v(-97.52, -169.17) * mm, "end": v(-97.52, -197.5) * mm});
            skLineSegment(sketch, "E12.5.2.2", {"start": v(-69.18, -197.5) * mm, "end": v(-97.52, -197.5) * mm});
            skLineSegment(sketch, "E12.5.2.3", {"start": v(-69.18, -169.17) * mm, "end": v(-69.18, -197.5) * mm});
            skLineSegment(sketch, "E12.5.3.0", {"start": v(-69.18, -135.84) * mm, "end": v(-97.52, -135.84) * mm});
            skLineSegment(sketch, "E12.5.3.1", {"start": v(-97.52, -135.84) * mm, "end": v(-97.52, -164.18) * mm});
            skLineSegment(sketch, "E12.5.3.2", {"start": v(-69.18, -164.18) * mm, "end": v(-97.52, -164.18) * mm});
            skLineSegment(sketch, "E12.5.3.3", {"start": v(-69.18, -135.84) * mm, "end": v(-69.18, -164.18) * mm});
            skLineSegment(sketch, "E12.5.4.0", {"start": v(-69.18, -102.51) * mm, "end": v(-97.52, -102.51) * mm});
            skLineSegment(sketch, "E12.5.4.1", {"start": v(-97.52, -102.51) * mm, "end": v(-97.52, -130.85) * mm});
            skLineSegment(sketch, "E12.5.4.2", {"start": v(-69.18, -130.85) * mm, "end": v(-97.52, -130.85) * mm});
            skLineSegment(sketch, "E12.5.4.3", {"start": v(-69.18, -102.51) * mm, "end": v(-69.18, -130.85) * mm});
            skLineSegment(sketch, "E12.5.5.0", {"start": v(-69.18, -69.18) * mm, "end": v(-97.52, -69.18) * mm});
            skLineSegment(sketch, "E12.5.5.1", {"start": v(-97.52, -69.18) * mm, "end": v(-97.52, -97.52) * mm});
            skLineSegment(sketch, "E12.5.5.2", {"start": v(-69.18, -97.52) * mm, "end": v(-97.52, -97.52) * mm});
            skLineSegment(sketch, "E12.5.5.3", {"start": v(-69.18, -69.18) * mm, "end": v(-69.18, -97.52) * mm});
            skLineSegment(sketch, "E12.5.6.0", {"start": v(-69.18, -35.85) * mm, "end": v(-97.52, -35.85) * mm});
            skLineSegment(sketch, "E12.5.6.1", {"start": v(-97.52, -35.85) * mm, "end": v(-97.52, -64.19) * mm});
            skLineSegment(sketch, "E12.5.6.2", {"start": v(-69.18, -64.19) * mm, "end": v(-97.52, -64.19) * mm});
            skLineSegment(sketch, "E12.5.6.3", {"start": v(-69.18, -35.85) * mm, "end": v(-69.18, -64.19) * mm});
            skLineSegment(sketch, "E12.5.7.0", {"start": v(-69.18, -2.52) * mm, "end": v(-97.52, -2.52) * mm});
            skLineSegment(sketch, "E12.5.7.1", {"start": v(-97.52, -2.52) * mm, "end": v(-97.52, -30.86) * mm});
            skLineSegment(sketch, "E12.5.7.2", {"start": v(-69.18, -30.86) * mm, "end": v(-97.52, -30.86) * mm});
            skLineSegment(sketch, "E12.5.7.3", {"start": v(-69.18, -2.52) * mm, "end": v(-69.18, -30.86) * mm});
            skLineSegment(sketch, "E12.5.8.0", {"start": v(-69.18, 30.8) * mm, "end": v(-97.52, 30.8) * mm});
            skLineSegment(sketch, "E12.5.8.1", {"start": v(-97.52, 30.8) * mm, "end": v(-97.52, 2.47) * mm});
            skLineSegment(sketch, "E12.5.8.2", {"start": v(-69.18, 2.47) * mm, "end": v(-97.52, 2.47) * mm});
            skLineSegment(sketch, "E12.5.8.3", {"start": v(-69.18, 30.8) * mm, "end": v(-69.18, 2.47) * mm});
            skLineSegment(sketch, "E12.5.9.0", {"start": v(-69.18, 64.14) * mm, "end": v(-97.52, 64.14) * mm});
            skLineSegment(sketch, "E12.5.9.1", {"start": v(-97.52, 64.14) * mm, "end": v(-97.52, 35.8) * mm});
            skLineSegment(sketch, "E12.5.9.2", {"start": v(-69.18, 35.8) * mm, "end": v(-97.52, 35.8) * mm});
            skLineSegment(sketch, "E12.5.9.3", {"start": v(-69.18, 64.14) * mm, "end": v(-69.18, 35.8) * mm});
            skLineSegment(sketch, "E12.5.10.0", {"start": v(-69.18, 97.47) * mm, "end": v(-97.52, 97.47) * mm});
            skLineSegment(sketch, "E12.5.10.1", {"start": v(-97.52, 97.47) * mm, "end": v(-97.52, 69.13) * mm});
            skLineSegment(sketch, "E12.5.10.2", {"start": v(-69.18, 69.13) * mm, "end": v(-97.52, 69.13) * mm});
            skLineSegment(sketch, "E12.5.10.3", {"start": v(-69.18, 97.47) * mm, "end": v(-69.18, 69.13) * mm});
            skLineSegment(sketch, "E12.5.11.0", {"start": v(-69.18, 130.8) * mm, "end": v(-97.52, 130.8) * mm});
            skLineSegment(sketch, "E12.5.11.1", {"start": v(-97.52, 130.8) * mm, "end": v(-97.52, 102.46) * mm});
            skLineSegment(sketch, "E12.5.11.2", {"start": v(-69.18, 102.46) * mm, "end": v(-97.52, 102.46) * mm});
            skLineSegment(sketch, "E12.5.11.3", {"start": v(-69.18, 130.8) * mm, "end": v(-69.18, 102.46) * mm});
            skLineSegment(sketch, "E12.5.12.0", {"start": v(-69.18, 164.13) * mm, "end": v(-97.52, 164.13) * mm});
            skLineSegment(sketch, "E12.5.12.1", {"start": v(-97.52, 164.13) * mm, "end": v(-97.52, 135.8) * mm});
            skLineSegment(sketch, "E12.5.12.2", {"start": v(-69.18, 135.8) * mm, "end": v(-97.52, 135.8) * mm});
            skLineSegment(sketch, "E12.5.12.3", {"start": v(-69.18, 164.13) * mm, "end": v(-69.18, 135.8) * mm});
            skLineSegment(sketch, "E12.5.13.0", {"start": v(-69.18, 197.46) * mm, "end": v(-97.52, 197.46) * mm});
            skLineSegment(sketch, "E12.5.13.1", {"start": v(-97.52, 197.46) * mm, "end": v(-97.52, 169.12) * mm});
            skLineSegment(sketch, "E12.5.13.2", {"start": v(-69.18, 169.12) * mm, "end": v(-97.52, 169.12) * mm});
            skLineSegment(sketch, "E12.5.13.3", {"start": v(-69.18, 197.46) * mm, "end": v(-69.18, 169.12) * mm});
            skLineSegment(sketch, "E12.5.14.0", {"start": v(-69.18, 230.79) * mm, "end": v(-97.52, 230.79) * mm});
            skLineSegment(sketch, "E12.5.14.1", {"start": v(-97.52, 230.79) * mm, "end": v(-97.52, 202.45) * mm});
            skLineSegment(sketch, "E12.5.14.2", {"start": v(-69.18, 202.45) * mm, "end": v(-97.52, 202.45) * mm});
            skLineSegment(sketch, "E12.5.14.3", {"start": v(-69.18, 230.79) * mm, "end": v(-69.18, 202.45) * mm});
            skLineSegment(sketch, "E12.5.15.0", {"start": v(-69.18, 264.12) * mm, "end": v(-97.52, 264.12) * mm});
            skLineSegment(sketch, "E12.5.15.1", {"start": v(-97.52, 264.12) * mm, "end": v(-97.52, 235.78) * mm});
            skLineSegment(sketch, "E12.5.15.2", {"start": v(-69.18, 235.78) * mm, "end": v(-97.52, 235.78) * mm});
            skLineSegment(sketch, "E12.5.15.3", {"start": v(-69.18, 264.12) * mm, "end": v(-69.18, 235.78) * mm});
            skLineSegment(sketch, "E12.6.0.0", {"start": v(-35.85, -235.83) * mm, "end": v(-64.19, -235.83) * mm});
            skLineSegment(sketch, "E12.6.0.1", {"start": v(-64.19, -235.83) * mm, "end": v(-64.19, -264.17) * mm});
            skLineSegment(sketch, "E12.6.0.2", {"start": v(-35.85, -264.17) * mm, "end": v(-64.19, -264.17) * mm});
            skLineSegment(sketch, "E12.6.0.3", {"start": v(-35.85, -235.83) * mm, "end": v(-35.85, -264.17) * mm});
            skLineSegment(sketch, "E12.6.1.0", {"start": v(-35.85, -202.5) * mm, "end": v(-64.19, -202.5) * mm});
            skLineSegment(sketch, "E12.6.1.1", {"start": v(-64.19, -202.5) * mm, "end": v(-64.19, -230.84) * mm});
            skLineSegment(sketch, "E12.6.1.2", {"start": v(-35.85, -230.84) * mm, "end": v(-64.19, -230.84) * mm});
            skLineSegment(sketch, "E12.6.1.3", {"start": v(-35.85, -202.5) * mm, "end": v(-35.85, -230.84) * mm});
            skLineSegment(sketch, "E12.6.2.0", {"start": v(-35.85, -169.17) * mm, "end": v(-64.19, -169.17) * mm});
            skLineSegment(sketch, "E12.6.2.1", {"start": v(-64.19, -169.17) * mm, "end": v(-64.19, -197.5) * mm});
            skLineSegment(sketch, "E12.6.2.2", {"start": v(-35.85, -197.5) * mm, "end": v(-64.19, -197.5) * mm});
            skLineSegment(sketch, "E12.6.2.3", {"start": v(-35.85, -169.17) * mm, "end": v(-35.85, -197.5) * mm});
            skLineSegment(sketch, "E12.6.3.0", {"start": v(-35.85, -135.84) * mm, "end": v(-64.19, -135.84) * mm});
            skLineSegment(sketch, "E12.6.3.1", {"start": v(-64.19, -135.84) * mm, "end": v(-64.19, -164.18) * mm});
            skLineSegment(sketch, "E12.6.3.2", {"start": v(-35.85, -164.18) * mm, "end": v(-64.19, -164.18) * mm});
            skLineSegment(sketch, "E12.6.3.3", {"start": v(-35.85, -135.84) * mm, "end": v(-35.85, -164.18) * mm});
            skLineSegment(sketch, "E12.6.4.0", {"start": v(-35.85, -102.51) * mm, "end": v(-64.19, -102.51) * mm});
            skLineSegment(sketch, "E12.6.4.1", {"start": v(-64.19, -102.51) * mm, "end": v(-64.19, -130.85) * mm});
            skLineSegment(sketch, "E12.6.4.2", {"start": v(-35.85, -130.85) * mm, "end": v(-64.19, -130.85) * mm});
            skLineSegment(sketch, "E12.6.4.3", {"start": v(-35.85, -102.51) * mm, "end": v(-35.85, -130.85) * mm});
            skLineSegment(sketch, "E12.6.5.0", {"start": v(-35.85, -69.18) * mm, "end": v(-64.19, -69.18) * mm});
            skLineSegment(sketch, "E12.6.5.1", {"start": v(-64.19, -69.18) * mm, "end": v(-64.19, -97.52) * mm});
            skLineSegment(sketch, "E12.6.5.2", {"start": v(-35.85, -97.52) * mm, "end": v(-64.19, -97.52) * mm});
            skLineSegment(sketch, "E12.6.5.3", {"start": v(-35.85, -69.18) * mm, "end": v(-35.85, -97.52) * mm});
            skLineSegment(sketch, "E12.6.6.0", {"start": v(-35.85, -35.85) * mm, "end": v(-64.19, -35.85) * mm});
            skLineSegment(sketch, "E12.6.6.1", {"start": v(-64.19, -35.85) * mm, "end": v(-64.19, -64.19) * mm});
            skLineSegment(sketch, "E12.6.6.2", {"start": v(-35.85, -64.19) * mm, "end": v(-64.19, -64.19) * mm});
            skLineSegment(sketch, "E12.6.6.3", {"start": v(-35.85, -35.85) * mm, "end": v(-35.85, -64.19) * mm});
            skLineSegment(sketch, "E12.6.7.0", {"start": v(-35.85, -2.52) * mm, "end": v(-64.19, -2.52) * mm});
            skLineSegment(sketch, "E12.6.7.1", {"start": v(-64.19, -2.52) * mm, "end": v(-64.19, -30.86) * mm});
            skLineSegment(sketch, "E12.6.7.2", {"start": v(-35.85, -30.86) * mm, "end": v(-64.19, -30.86) * mm});
            skLineSegment(sketch, "E12.6.7.3", {"start": v(-35.85, -2.52) * mm, "end": v(-35.85, -30.86) * mm});
            skLineSegment(sketch, "E12.6.8.0", {"start": v(-35.85, 30.8) * mm, "end": v(-64.19, 30.8) * mm});
            skLineSegment(sketch, "E12.6.8.1", {"start": v(-64.19, 30.8) * mm, "end": v(-64.19, 2.47) * mm});
            skLineSegment(sketch, "E12.6.8.2", {"start": v(-35.85, 2.47) * mm, "end": v(-64.19, 2.47) * mm});
            skLineSegment(sketch, "E12.6.8.3", {"start": v(-35.85, 30.8) * mm, "end": v(-35.85, 2.47) * mm});
            skLineSegment(sketch, "E12.6.9.0", {"start": v(-35.85, 64.14) * mm, "end": v(-64.19, 64.14) * mm});
            skLineSegment(sketch, "E12.6.9.1", {"start": v(-64.19, 64.14) * mm, "end": v(-64.19, 35.8) * mm});
            skLineSegment(sketch, "E12.6.9.2", {"start": v(-35.85, 35.8) * mm, "end": v(-64.19, 35.8) * mm});
            skLineSegment(sketch, "E12.6.9.3", {"start": v(-35.85, 64.14) * mm, "end": v(-35.85, 35.8) * mm});
            skLineSegment(sketch, "E12.6.10.0", {"start": v(-35.85, 97.47) * mm, "end": v(-64.19, 97.47) * mm});
            skLineSegment(sketch, "E12.6.10.1", {"start": v(-64.19, 97.47) * mm, "end": v(-64.19, 69.13) * mm});
            skLineSegment(sketch, "E12.6.10.2", {"start": v(-35.85, 69.13) * mm, "end": v(-64.19, 69.13) * mm});
            skLineSegment(sketch, "E12.6.10.3", {"start": v(-35.85, 97.47) * mm, "end": v(-35.85, 69.13) * mm});
            skLineSegment(sketch, "E12.6.11.0", {"start": v(-35.85, 130.8) * mm, "end": v(-64.19, 130.8) * mm});
            skLineSegment(sketch, "E12.6.11.1", {"start": v(-64.19, 130.8) * mm, "end": v(-64.19, 102.46) * mm});
            skLineSegment(sketch, "E12.6.11.2", {"start": v(-35.85, 102.46) * mm, "end": v(-64.19, 102.46) * mm});
            skLineSegment(sketch, "E12.6.11.3", {"start": v(-35.85, 130.8) * mm, "end": v(-35.85, 102.46) * mm});
            skLineSegment(sketch, "E12.6.12.0", {"start": v(-35.85, 164.13) * mm, "end": v(-64.19, 164.13) * mm});
            skLineSegment(sketch, "E12.6.12.1", {"start": v(-64.19, 164.13) * mm, "end": v(-64.19, 135.8) * mm});
            skLineSegment(sketch, "E12.6.12.2", {"start": v(-35.85, 135.8) * mm, "end": v(-64.19, 135.8) * mm});
            skLineSegment(sketch, "E12.6.12.3", {"start": v(-35.85, 164.13) * mm, "end": v(-35.85, 135.8) * mm});
            skLineSegment(sketch, "E12.6.13.0", {"start": v(-35.85, 197.46) * mm, "end": v(-64.19, 197.46) * mm});
            skLineSegment(sketch, "E12.6.13.1", {"start": v(-64.19, 197.46) * mm, "end": v(-64.19, 169.12) * mm});
            skLineSegment(sketch, "E12.6.13.2", {"start": v(-35.85, 169.12) * mm, "end": v(-64.19, 169.12) * mm});
            skLineSegment(sketch, "E12.6.13.3", {"start": v(-35.85, 197.46) * mm, "end": v(-35.85, 169.12) * mm});
            skLineSegment(sketch, "E12.6.14.0", {"start": v(-35.85, 230.79) * mm, "end": v(-64.19, 230.79) * mm});
            skLineSegment(sketch, "E12.6.14.1", {"start": v(-64.19, 230.79) * mm, "end": v(-64.19, 202.45) * mm});
            skLineSegment(sketch, "E12.6.14.2", {"start": v(-35.85, 202.45) * mm, "end": v(-64.19, 202.45) * mm});
            skLineSegment(sketch, "E12.6.14.3", {"start": v(-35.85, 230.79) * mm, "end": v(-35.85, 202.45) * mm});
            skLineSegment(sketch, "E12.6.15.0", {"start": v(-35.85, 264.12) * mm, "end": v(-64.19, 264.12) * mm});
            skLineSegment(sketch, "E12.6.15.1", {"start": v(-64.19, 264.12) * mm, "end": v(-64.19, 235.78) * mm});
            skLineSegment(sketch, "E12.6.15.2", {"start": v(-35.85, 235.78) * mm, "end": v(-64.19, 235.78) * mm});
            skLineSegment(sketch, "E12.6.15.3", {"start": v(-35.85, 264.12) * mm, "end": v(-35.85, 235.78) * mm});
            skLineSegment(sketch, "E12.7.0.0", {"start": v(-2.52, -235.83) * mm, "end": v(-30.86, -235.83) * mm});
            skLineSegment(sketch, "E12.7.0.1", {"start": v(-30.86, -235.83) * mm, "end": v(-30.86, -264.17) * mm});
            skLineSegment(sketch, "E12.7.0.2", {"start": v(-2.52, -264.17) * mm, "end": v(-30.86, -264.17) * mm});
            skLineSegment(sketch, "E12.7.0.3", {"start": v(-2.52, -235.83) * mm, "end": v(-2.52, -264.17) * mm});
            skLineSegment(sketch, "E12.7.1.0", {"start": v(-2.52, -202.5) * mm, "end": v(-30.86, -202.5) * mm});
            skLineSegment(sketch, "E12.7.1.1", {"start": v(-30.86, -202.5) * mm, "end": v(-30.86, -230.84) * mm});
            skLineSegment(sketch, "E12.7.1.2", {"start": v(-2.52, -230.84) * mm, "end": v(-30.86, -230.84) * mm});
            skLineSegment(sketch, "E12.7.1.3", {"start": v(-2.52, -202.5) * mm, "end": v(-2.52, -230.84) * mm});
            skLineSegment(sketch, "E12.7.2.0", {"start": v(-2.52, -169.17) * mm, "end": v(-30.86, -169.17) * mm});
            skLineSegment(sketch, "E12.7.2.1", {"start": v(-30.86, -169.17) * mm, "end": v(-30.86, -197.5) * mm});
            skLineSegment(sketch, "E12.7.2.2", {"start": v(-2.52, -197.5) * mm, "end": v(-30.86, -197.5) * mm});
            skLineSegment(sketch, "E12.7.2.3", {"start": v(-2.52, -169.17) * mm, "end": v(-2.52, -197.5) * mm});
            skLineSegment(sketch, "E12.7.3.0", {"start": v(-2.52, -135.84) * mm, "end": v(-30.86, -135.84) * mm});
            skLineSegment(sketch, "E12.7.3.1", {"start": v(-30.86, -135.84) * mm, "end": v(-30.86, -164.18) * mm});
            skLineSegment(sketch, "E12.7.3.2", {"start": v(-2.52, -164.18) * mm, "end": v(-30.86, -164.18) * mm});
            skLineSegment(sketch, "E12.7.3.3", {"start": v(-2.52, -135.84) * mm, "end": v(-2.52, -164.18) * mm});
            skLineSegment(sketch, "E12.7.4.0", {"start": v(-2.52, -102.51) * mm, "end": v(-30.86, -102.51) * mm});
            skLineSegment(sketch, "E12.7.4.1", {"start": v(-30.86, -102.51) * mm, "end": v(-30.86, -130.85) * mm});
            skLineSegment(sketch, "E12.7.4.2", {"start": v(-2.52, -130.85) * mm, "end": v(-30.86, -130.85) * mm});
            skLineSegment(sketch, "E12.7.4.3", {"start": v(-2.52, -102.51) * mm, "end": v(-2.52, -130.85) * mm});
            skLineSegment(sketch, "E12.7.5.0", {"start": v(-2.52, -69.18) * mm, "end": v(-30.86, -69.18) * mm});
            skLineSegment(sketch, "E12.7.5.1", {"start": v(-30.86, -69.18) * mm, "end": v(-30.86, -97.52) * mm});
            skLineSegment(sketch, "E12.7.5.2", {"start": v(-2.52, -97.52) * mm, "end": v(-30.86, -97.52) * mm});
            skLineSegment(sketch, "E12.7.5.3", {"start": v(-2.52, -69.18) * mm, "end": v(-2.52, -97.52) * mm});
            skLineSegment(sketch, "E12.7.6.0", {"start": v(-2.52, -35.85) * mm, "end": v(-30.86, -35.85) * mm});
            skLineSegment(sketch, "E12.7.6.1", {"start": v(-30.86, -35.85) * mm, "end": v(-30.86, -64.19) * mm});
            skLineSegment(sketch, "E12.7.6.2", {"start": v(-2.52, -64.19) * mm, "end": v(-30.86, -64.19) * mm});
            skLineSegment(sketch, "E12.7.6.3", {"start": v(-2.52, -35.85) * mm, "end": v(-2.52, -64.19) * mm});
            skLineSegment(sketch, "E12.7.7.0", {"start": v(-2.52, -2.52) * mm, "end": v(-30.86, -2.52) * mm});
            skLineSegment(sketch, "E12.7.7.1", {"start": v(-30.86, -2.52) * mm, "end": v(-30.86, -30.86) * mm});
            skLineSegment(sketch, "E12.7.7.2", {"start": v(-2.52, -30.86) * mm, "end": v(-30.86, -30.86) * mm});
            skLineSegment(sketch, "E12.7.7.3", {"start": v(-2.52, -2.52) * mm, "end": v(-2.52, -30.86) * mm});
            skLineSegment(sketch, "E12.7.8.0", {"start": v(-2.52, 30.8) * mm, "end": v(-30.86, 30.8) * mm});
            skLineSegment(sketch, "E12.7.8.1", {"start": v(-30.86, 30.8) * mm, "end": v(-30.86, 2.47) * mm});
            skLineSegment(sketch, "E12.7.8.2", {"start": v(-2.52, 2.47) * mm, "end": v(-30.86, 2.47) * mm});
            skLineSegment(sketch, "E12.7.8.3", {"start": v(-2.52, 30.8) * mm, "end": v(-2.52, 2.47) * mm});
            skLineSegment(sketch, "E12.7.9.0", {"start": v(-2.52, 64.14) * mm, "end": v(-30.86, 64.14) * mm});
            skLineSegment(sketch, "E12.7.9.1", {"start": v(-30.86, 64.14) * mm, "end": v(-30.86, 35.8) * mm});
            skLineSegment(sketch, "E12.7.9.2", {"start": v(-2.52, 35.8) * mm, "end": v(-30.86, 35.8) * mm});
            skLineSegment(sketch, "E12.7.9.3", {"start": v(-2.52, 64.14) * mm, "end": v(-2.52, 35.8) * mm});
            skLineSegment(sketch, "E12.7.10.0", {"start": v(-2.52, 97.47) * mm, "end": v(-30.86, 97.47) * mm});
            skLineSegment(sketch, "E12.7.10.1", {"start": v(-30.86, 97.47) * mm, "end": v(-30.86, 69.13) * mm});
            skLineSegment(sketch, "E12.7.10.2", {"start": v(-2.52, 69.13) * mm, "end": v(-30.86, 69.13) * mm});
            skLineSegment(sketch, "E12.7.10.3", {"start": v(-2.52, 97.47) * mm, "end": v(-2.52, 69.13) * mm});
            skLineSegment(sketch, "E12.7.11.0", {"start": v(-2.52, 130.8) * mm, "end": v(-30.86, 130.8) * mm});
            skLineSegment(sketch, "E12.7.11.1", {"start": v(-30.86, 130.8) * mm, "end": v(-30.86, 102.46) * mm});
            skLineSegment(sketch, "E12.7.11.2", {"start": v(-2.52, 102.46) * mm, "end": v(-30.86, 102.46) * mm});
            skLineSegment(sketch, "E12.7.11.3", {"start": v(-2.52, 130.8) * mm, "end": v(-2.52, 102.46) * mm});
            skLineSegment(sketch, "E12.7.12.0", {"start": v(-2.52, 164.13) * mm, "end": v(-30.86, 164.13) * mm});
            skLineSegment(sketch, "E12.7.12.1", {"start": v(-30.86, 164.13) * mm, "end": v(-30.86, 135.8) * mm});
            skLineSegment(sketch, "E12.7.12.2", {"start": v(-2.52, 135.8) * mm, "end": v(-30.86, 135.8) * mm});
            skLineSegment(sketch, "E12.7.12.3", {"start": v(-2.52, 164.13) * mm, "end": v(-2.52, 135.8) * mm});
            skLineSegment(sketch, "E12.7.13.0", {"start": v(-2.52, 197.46) * mm, "end": v(-30.86, 197.46) * mm});
            skLineSegment(sketch, "E12.7.13.1", {"start": v(-30.86, 197.46) * mm, "end": v(-30.86, 169.12) * mm});
            skLineSegment(sketch, "E12.7.13.2", {"start": v(-2.52, 169.12) * mm, "end": v(-30.86, 169.12) * mm});
            skLineSegment(sketch, "E12.7.13.3", {"start": v(-2.52, 197.46) * mm, "end": v(-2.52, 169.12) * mm});
            skLineSegment(sketch, "E12.7.14.0", {"start": v(-2.52, 230.79) * mm, "end": v(-30.86, 230.79) * mm});
            skLineSegment(sketch, "E12.7.14.1", {"start": v(-30.86, 230.79) * mm, "end": v(-30.86, 202.45) * mm});
            skLineSegment(sketch, "E12.7.14.2", {"start": v(-2.52, 202.45) * mm, "end": v(-30.86, 202.45) * mm});
            skLineSegment(sketch, "E12.7.14.3", {"start": v(-2.52, 230.79) * mm, "end": v(-2.52, 202.45) * mm});
            skLineSegment(sketch, "E12.7.15.0", {"start": v(-2.52, 264.12) * mm, "end": v(-30.86, 264.12) * mm});
            skLineSegment(sketch, "E12.7.15.1", {"start": v(-30.86, 264.12) * mm, "end": v(-30.86, 235.78) * mm});
            skLineSegment(sketch, "E12.7.15.2", {"start": v(-2.52, 235.78) * mm, "end": v(-30.86, 235.78) * mm});
            skLineSegment(sketch, "E12.7.15.3", {"start": v(-2.52, 264.12) * mm, "end": v(-2.52, 235.78) * mm});
            skLineSegment(sketch, "E12.8.0.0", {"start": v(30.8, -235.83) * mm, "end": v(2.47, -235.83) * mm});
            skLineSegment(sketch, "E12.8.0.1", {"start": v(2.47, -235.83) * mm, "end": v(2.47, -264.17) * mm});
            skLineSegment(sketch, "E12.8.0.2", {"start": v(30.8, -264.17) * mm, "end": v(2.47, -264.17) * mm});
            skLineSegment(sketch, "E12.8.0.3", {"start": v(30.8, -235.83) * mm, "end": v(30.8, -264.17) * mm});
            skLineSegment(sketch, "E12.8.1.0", {"start": v(30.8, -202.5) * mm, "end": v(2.47, -202.5) * mm});
            skLineSegment(sketch, "E12.8.1.1", {"start": v(2.47, -202.5) * mm, "end": v(2.47, -230.84) * mm});
            skLineSegment(sketch, "E12.8.1.2", {"start": v(30.8, -230.84) * mm, "end": v(2.47, -230.84) * mm});
            skLineSegment(sketch, "E12.8.1.3", {"start": v(30.8, -202.5) * mm, "end": v(30.8, -230.84) * mm});
            skLineSegment(sketch, "E12.8.2.0", {"start": v(30.8, -169.17) * mm, "end": v(2.47, -169.17) * mm});
            skLineSegment(sketch, "E12.8.2.1", {"start": v(2.47, -169.17) * mm, "end": v(2.47, -197.5) * mm});
            skLineSegment(sketch, "E12.8.2.2", {"start": v(30.8, -197.5) * mm, "end": v(2.47, -197.5) * mm});
            skLineSegment(sketch, "E12.8.2.3", {"start": v(30.8, -169.17) * mm, "end": v(30.8, -197.5) * mm});
            skLineSegment(sketch, "E12.8.3.0", {"start": v(30.8, -135.84) * mm, "end": v(2.47, -135.84) * mm});
            skLineSegment(sketch, "E12.8.3.1", {"start": v(2.47, -135.84) * mm, "end": v(2.47, -164.18) * mm});
            skLineSegment(sketch, "E12.8.3.2", {"start": v(30.8, -164.18) * mm, "end": v(2.47, -164.18) * mm});
            skLineSegment(sketch, "E12.8.3.3", {"start": v(30.8, -135.84) * mm, "end": v(30.8, -164.18) * mm});
            skLineSegment(sketch, "E12.8.4.0", {"start": v(30.8, -102.51) * mm, "end": v(2.47, -102.51) * mm});
            skLineSegment(sketch, "E12.8.4.1", {"start": v(2.47, -102.51) * mm, "end": v(2.47, -130.85) * mm});
            skLineSegment(sketch, "E12.8.4.2", {"start": v(30.8, -130.85) * mm, "end": v(2.47, -130.85) * mm});
            skLineSegment(sketch, "E12.8.4.3", {"start": v(30.8, -102.51) * mm, "end": v(30.8, -130.85) * mm});
            skLineSegment(sketch, "E12.8.5.0", {"start": v(30.8, -69.18) * mm, "end": v(2.47, -69.18) * mm});
            skLineSegment(sketch, "E12.8.5.1", {"start": v(2.47, -69.18) * mm, "end": v(2.47, -97.52) * mm});
            skLineSegment(sketch, "E12.8.5.2", {"start": v(30.8, -97.52) * mm, "end": v(2.47, -97.52) * mm});
            skLineSegment(sketch, "E12.8.5.3", {"start": v(30.8, -69.18) * mm, "end": v(30.8, -97.52) * mm});
            skLineSegment(sketch, "E12.8.6.0", {"start": v(30.8, -35.85) * mm, "end": v(2.47, -35.85) * mm});
            skLineSegment(sketch, "E12.8.6.1", {"start": v(2.47, -35.85) * mm, "end": v(2.47, -64.19) * mm});
            skLineSegment(sketch, "E12.8.6.2", {"start": v(30.8, -64.19) * mm, "end": v(2.47, -64.19) * mm});
            skLineSegment(sketch, "E12.8.6.3", {"start": v(30.8, -35.85) * mm, "end": v(30.8, -64.19) * mm});
            skLineSegment(sketch, "E12.8.7.0", {"start": v(30.8, -2.52) * mm, "end": v(2.47, -2.52) * mm});
            skLineSegment(sketch, "E12.8.7.1", {"start": v(2.47, -2.52) * mm, "end": v(2.47, -30.86) * mm});
            skLineSegment(sketch, "E12.8.7.2", {"start": v(30.8, -30.86) * mm, "end": v(2.47, -30.86) * mm});
            skLineSegment(sketch, "E12.8.7.3", {"start": v(30.8, -2.52) * mm, "end": v(30.8, -30.86) * mm});
            skLineSegment(sketch, "E12.8.8.0", {"start": v(30.8, 30.8) * mm, "end": v(2.47, 30.8) * mm});
            skLineSegment(sketch, "E12.8.8.1", {"start": v(2.47, 30.8) * mm, "end": v(2.47, 2.47) * mm});
            skLineSegment(sketch, "E12.8.8.2", {"start": v(30.8, 2.47) * mm, "end": v(2.47, 2.47) * mm});
            skLineSegment(sketch, "E12.8.8.3", {"start": v(30.8, 30.8) * mm, "end": v(30.8, 2.47) * mm});
            skLineSegment(sketch, "E12.8.9.0", {"start": v(30.8, 64.14) * mm, "end": v(2.47, 64.14) * mm});
            skLineSegment(sketch, "E12.8.9.1", {"start": v(2.47, 64.14) * mm, "end": v(2.47, 35.8) * mm});
            skLineSegment(sketch, "E12.8.9.2", {"start": v(30.8, 35.8) * mm, "end": v(2.47, 35.8) * mm});
            skLineSegment(sketch, "E12.8.9.3", {"start": v(30.8, 64.14) * mm, "end": v(30.8, 35.8) * mm});
            skLineSegment(sketch, "E12.8.10.0", {"start": v(30.8, 97.47) * mm, "end": v(2.47, 97.47) * mm});
            skLineSegment(sketch, "E12.8.10.1", {"start": v(2.47, 97.47) * mm, "end": v(2.47, 69.13) * mm});
            skLineSegment(sketch, "E12.8.10.2", {"start": v(30.8, 69.13) * mm, "end": v(2.47, 69.13) * mm});
            skLineSegment(sketch, "E12.8.10.3", {"start": v(30.8, 97.47) * mm, "end": v(30.8, 69.13) * mm});
            skLineSegment(sketch, "E12.8.11.0", {"start": v(30.8, 130.8) * mm, "end": v(2.47, 130.8) * mm});
            skLineSegment(sketch, "E12.8.11.1", {"start": v(2.47, 130.8) * mm, "end": v(2.47, 102.46) * mm});
            skLineSegment(sketch, "E12.8.11.2", {"start": v(30.8, 102.46) * mm, "end": v(2.47, 102.46) * mm});
            skLineSegment(sketch, "E12.8.11.3", {"start": v(30.8, 130.8) * mm, "end": v(30.8, 102.46) * mm});
            skLineSegment(sketch, "E12.8.12.0", {"start": v(30.8, 164.13) * mm, "end": v(2.47, 164.13) * mm});
            skLineSegment(sketch, "E12.8.12.1", {"start": v(2.47, 164.13) * mm, "end": v(2.47, 135.8) * mm});
            skLineSegment(sketch, "E12.8.12.2", {"start": v(30.8, 135.8) * mm, "end": v(2.47, 135.8) * mm});
            skLineSegment(sketch, "E12.8.12.3", {"start": v(30.8, 164.13) * mm, "end": v(30.8, 135.8) * mm});
            skLineSegment(sketch, "E12.8.13.0", {"start": v(30.8, 197.46) * mm, "end": v(2.47, 197.46) * mm});
            skLineSegment(sketch, "E12.8.13.1", {"start": v(2.47, 197.46) * mm, "end": v(2.47, 169.12) * mm});
            skLineSegment(sketch, "E12.8.13.2", {"start": v(30.8, 169.12) * mm, "end": v(2.47, 169.12) * mm});
            skLineSegment(sketch, "E12.8.13.3", {"start": v(30.8, 197.46) * mm, "end": v(30.8, 169.12) * mm});
            skLineSegment(sketch, "E12.8.14.0", {"start": v(30.8, 230.79) * mm, "end": v(2.47, 230.79) * mm});
            skLineSegment(sketch, "E12.8.14.1", {"start": v(2.47, 230.79) * mm, "end": v(2.47, 202.45) * mm});
            skLineSegment(sketch, "E12.8.14.2", {"start": v(30.8, 202.45) * mm, "end": v(2.47, 202.45) * mm});
            skLineSegment(sketch, "E12.8.14.3", {"start": v(30.8, 230.79) * mm, "end": v(30.8, 202.45) * mm});
            skLineSegment(sketch, "E12.8.15.0", {"start": v(30.8, 264.12) * mm, "end": v(2.47, 264.12) * mm});
            skLineSegment(sketch, "E12.8.15.1", {"start": v(2.47, 264.12) * mm, "end": v(2.47, 235.78) * mm});
            skLineSegment(sketch, "E12.8.15.2", {"start": v(30.8, 235.78) * mm, "end": v(2.47, 235.78) * mm});
            skLineSegment(sketch, "E12.8.15.3", {"start": v(30.8, 264.12) * mm, "end": v(30.8, 235.78) * mm});
            skLineSegment(sketch, "E12.9.0.0", {"start": v(64.14, -235.83) * mm, "end": v(35.8, -235.83) * mm});
            skLineSegment(sketch, "E12.9.0.1", {"start": v(35.8, -235.83) * mm, "end": v(35.8, -264.17) * mm});
            skLineSegment(sketch, "E12.9.0.2", {"start": v(64.14, -264.17) * mm, "end": v(35.8, -264.17) * mm});
            skLineSegment(sketch, "E12.9.0.3", {"start": v(64.14, -235.83) * mm, "end": v(64.14, -264.17) * mm});
            skLineSegment(sketch, "E12.9.1.0", {"start": v(64.14, -202.5) * mm, "end": v(35.8, -202.5) * mm});
            skLineSegment(sketch, "E12.9.1.1", {"start": v(35.8, -202.5) * mm, "end": v(35.8, -230.84) * mm});
            skLineSegment(sketch, "E12.9.1.2", {"start": v(64.14, -230.84) * mm, "end": v(35.8, -230.84) * mm});
            skLineSegment(sketch, "E12.9.1.3", {"start": v(64.14, -202.5) * mm, "end": v(64.14, -230.84) * mm});
            skLineSegment(sketch, "E12.9.2.0", {"start": v(64.14, -169.17) * mm, "end": v(35.8, -169.17) * mm});
            skLineSegment(sketch, "E12.9.2.1", {"start": v(35.8, -169.17) * mm, "end": v(35.8, -197.5) * mm});
            skLineSegment(sketch, "E12.9.2.2", {"start": v(64.14, -197.5) * mm, "end": v(35.8, -197.5) * mm});
            skLineSegment(sketch, "E12.9.2.3", {"start": v(64.14, -169.17) * mm, "end": v(64.14, -197.5) * mm});
            skLineSegment(sketch, "E12.9.3.0", {"start": v(64.14, -135.84) * mm, "end": v(35.8, -135.84) * mm});
            skLineSegment(sketch, "E12.9.3.1", {"start": v(35.8, -135.84) * mm, "end": v(35.8, -164.18) * mm});
            skLineSegment(sketch, "E12.9.3.2", {"start": v(64.14, -164.18) * mm, "end": v(35.8, -164.18) * mm});
            skLineSegment(sketch, "E12.9.3.3", {"start": v(64.14, -135.84) * mm, "end": v(64.14, -164.18) * mm});
            skLineSegment(sketch, "E12.9.4.0", {"start": v(64.14, -102.51) * mm, "end": v(35.8, -102.51) * mm});
            skLineSegment(sketch, "E12.9.4.1", {"start": v(35.8, -102.51) * mm, "end": v(35.8, -130.85) * mm});
            skLineSegment(sketch, "E12.9.4.2", {"start": v(64.14, -130.85) * mm, "end": v(35.8, -130.85) * mm});
            skLineSegment(sketch, "E12.9.4.3", {"start": v(64.14, -102.51) * mm, "end": v(64.14, -130.85) * mm});
            skLineSegment(sketch, "E12.9.5.0", {"start": v(64.14, -69.18) * mm, "end": v(35.8, -69.18) * mm});
            skLineSegment(sketch, "E12.9.5.1", {"start": v(35.8, -69.18) * mm, "end": v(35.8, -97.52) * mm});
            skLineSegment(sketch, "E12.9.5.2", {"start": v(64.14, -97.52) * mm, "end": v(35.8, -97.52) * mm});
            skLineSegment(sketch, "E12.9.5.3", {"start": v(64.14, -69.18) * mm, "end": v(64.14, -97.52) * mm});
            skLineSegment(sketch, "E12.9.6.0", {"start": v(64.14, -35.85) * mm, "end": v(35.8, -35.85) * mm});
            skLineSegment(sketch, "E12.9.6.1", {"start": v(35.8, -35.85) * mm, "end": v(35.8, -64.19) * mm});
            skLineSegment(sketch, "E12.9.6.2", {"start": v(64.14, -64.19) * mm, "end": v(35.8, -64.19) * mm});
            skLineSegment(sketch, "E12.9.6.3", {"start": v(64.14, -35.85) * mm, "end": v(64.14, -64.19) * mm});
            skLineSegment(sketch, "E12.9.7.0", {"start": v(64.14, -2.52) * mm, "end": v(35.8, -2.52) * mm});
            skLineSegment(sketch, "E12.9.7.1", {"start": v(35.8, -2.52) * mm, "end": v(35.8, -30.86) * mm});
            skLineSegment(sketch, "E12.9.7.2", {"start": v(64.14, -30.86) * mm, "end": v(35.8, -30.86) * mm});
            skLineSegment(sketch, "E12.9.7.3", {"start": v(64.14, -2.52) * mm, "end": v(64.14, -30.86) * mm});
            skLineSegment(sketch, "E12.9.8.0", {"start": v(64.14, 30.8) * mm, "end": v(35.8, 30.8) * mm});
            skLineSegment(sketch, "E12.9.8.1", {"start": v(35.8, 30.8) * mm, "end": v(35.8, 2.47) * mm});
            skLineSegment(sketch, "E12.9.8.2", {"start": v(64.14, 2.47) * mm, "end": v(35.8, 2.47) * mm});
            skLineSegment(sketch, "E12.9.8.3", {"start": v(64.14, 30.8) * mm, "end": v(64.14, 2.47) * mm});
            skLineSegment(sketch, "E12.9.9.0", {"start": v(64.14, 64.14) * mm, "end": v(35.8, 64.14) * mm});
            skLineSegment(sketch, "E12.9.9.1", {"start": v(35.8, 64.14) * mm, "end": v(35.8, 35.8) * mm});
            skLineSegment(sketch, "E12.9.9.2", {"start": v(64.14, 35.8) * mm, "end": v(35.8, 35.8) * mm});
            skLineSegment(sketch, "E12.9.9.3", {"start": v(64.14, 64.14) * mm, "end": v(64.14, 35.8) * mm});
            skLineSegment(sketch, "E12.9.10.0", {"start": v(64.14, 97.47) * mm, "end": v(35.8, 97.47) * mm});
            skLineSegment(sketch, "E12.9.10.1", {"start": v(35.8, 97.47) * mm, "end": v(35.8, 69.13) * mm});
            skLineSegment(sketch, "E12.9.10.2", {"start": v(64.14, 69.13) * mm, "end": v(35.8, 69.13) * mm});
            skLineSegment(sketch, "E12.9.10.3", {"start": v(64.14, 97.47) * mm, "end": v(64.14, 69.13) * mm});
            skLineSegment(sketch, "E12.9.11.0", {"start": v(64.14, 130.8) * mm, "end": v(35.8, 130.8) * mm});
            skLineSegment(sketch, "E12.9.11.1", {"start": v(35.8, 130.8) * mm, "end": v(35.8, 102.46) * mm});
            skLineSegment(sketch, "E12.9.11.2", {"start": v(64.14, 102.46) * mm, "end": v(35.8, 102.46) * mm});
            skLineSegment(sketch, "E12.9.11.3", {"start": v(64.14, 130.8) * mm, "end": v(64.14, 102.46) * mm});
            skLineSegment(sketch, "E12.9.12.0", {"start": v(64.14, 164.13) * mm, "end": v(35.8, 164.13) * mm});
            skLineSegment(sketch, "E12.9.12.1", {"start": v(35.8, 164.13) * mm, "end": v(35.8, 135.8) * mm});
            skLineSegment(sketch, "E12.9.12.2", {"start": v(64.14, 135.8) * mm, "end": v(35.8, 135.8) * mm});
            skLineSegment(sketch, "E12.9.12.3", {"start": v(64.14, 164.13) * mm, "end": v(64.14, 135.8) * mm});
            skLineSegment(sketch, "E12.9.13.0", {"start": v(64.14, 197.46) * mm, "end": v(35.8, 197.46) * mm});
            skLineSegment(sketch, "E12.9.13.1", {"start": v(35.8, 197.46) * mm, "end": v(35.8, 169.12) * mm});
            skLineSegment(sketch, "E12.9.13.2", {"start": v(64.14, 169.12) * mm, "end": v(35.8, 169.12) * mm});
            skLineSegment(sketch, "E12.9.13.3", {"start": v(64.14, 197.46) * mm, "end": v(64.14, 169.12) * mm});
            skLineSegment(sketch, "E12.9.14.0", {"start": v(64.14, 230.79) * mm, "end": v(35.8, 230.79) * mm});
            skLineSegment(sketch, "E12.9.14.1", {"start": v(35.8, 230.79) * mm, "end": v(35.8, 202.45) * mm});
            skLineSegment(sketch, "E12.9.14.2", {"start": v(64.14, 202.45) * mm, "end": v(35.8, 202.45) * mm});
            skLineSegment(sketch, "E12.9.14.3", {"start": v(64.14, 230.79) * mm, "end": v(64.14, 202.45) * mm});
            skLineSegment(sketch, "E12.9.15.0", {"start": v(64.14, 264.12) * mm, "end": v(35.8, 264.12) * mm});
            skLineSegment(sketch, "E12.9.15.1", {"start": v(35.8, 264.12) * mm, "end": v(35.8, 235.78) * mm});
            skLineSegment(sketch, "E12.9.15.2", {"start": v(64.14, 235.78) * mm, "end": v(35.8, 235.78) * mm});
            skLineSegment(sketch, "E12.9.15.3", {"start": v(64.14, 264.12) * mm, "end": v(64.14, 235.78) * mm});
            skLineSegment(sketch, "E12.10.0.0", {"start": v(97.47, -235.83) * mm, "end": v(69.13, -235.83) * mm});
            skLineSegment(sketch, "E12.10.0.1", {"start": v(69.13, -235.83) * mm, "end": v(69.13, -264.17) * mm});
            skLineSegment(sketch, "E12.10.0.2", {"start": v(97.47, -264.17) * mm, "end": v(69.13, -264.17) * mm});
            skLineSegment(sketch, "E12.10.0.3", {"start": v(97.47, -235.83) * mm, "end": v(97.47, -264.17) * mm});
            skLineSegment(sketch, "E12.10.1.0", {"start": v(97.47, -202.5) * mm, "end": v(69.13, -202.5) * mm});
            skLineSegment(sketch, "E12.10.1.1", {"start": v(69.13, -202.5) * mm, "end": v(69.13, -230.84) * mm});
            skLineSegment(sketch, "E12.10.1.2", {"start": v(97.47, -230.84) * mm, "end": v(69.13, -230.84) * mm});
            skLineSegment(sketch, "E12.10.1.3", {"start": v(97.47, -202.5) * mm, "end": v(97.47, -230.84) * mm});
            skLineSegment(sketch, "E12.10.2.0", {"start": v(97.47, -169.17) * mm, "end": v(69.13, -169.17) * mm});
            skLineSegment(sketch, "E12.10.2.1", {"start": v(69.13, -169.17) * mm, "end": v(69.13, -197.5) * mm});
            skLineSegment(sketch, "E12.10.2.2", {"start": v(97.47, -197.5) * mm, "end": v(69.13, -197.5) * mm});
            skLineSegment(sketch, "E12.10.2.3", {"start": v(97.47, -169.17) * mm, "end": v(97.47, -197.5) * mm});
            skLineSegment(sketch, "E12.10.3.0", {"start": v(97.47, -135.84) * mm, "end": v(69.13, -135.84) * mm});
            skLineSegment(sketch, "E12.10.3.1", {"start": v(69.13, -135.84) * mm, "end": v(69.13, -164.18) * mm});
            skLineSegment(sketch, "E12.10.3.2", {"start": v(97.47, -164.18) * mm, "end": v(69.13, -164.18) * mm});
            skLineSegment(sketch, "E12.10.3.3", {"start": v(97.47, -135.84) * mm, "end": v(97.47, -164.18) * mm});
            skLineSegment(sketch, "E12.10.4.0", {"start": v(97.47, -102.51) * mm, "end": v(69.13, -102.51) * mm});
            skLineSegment(sketch, "E12.10.4.1", {"start": v(69.13, -102.51) * mm, "end": v(69.13, -130.85) * mm});
            skLineSegment(sketch, "E12.10.4.2", {"start": v(97.47, -130.85) * mm, "end": v(69.13, -130.85) * mm});
            skLineSegment(sketch, "E12.10.4.3", {"start": v(97.47, -102.51) * mm, "end": v(97.47, -130.85) * mm});
            skLineSegment(sketch, "E12.10.5.0", {"start": v(97.47, -69.18) * mm, "end": v(69.13, -69.18) * mm});
            skLineSegment(sketch, "E12.10.5.1", {"start": v(69.13, -69.18) * mm, "end": v(69.13, -97.52) * mm});
            skLineSegment(sketch, "E12.10.5.2", {"start": v(97.47, -97.52) * mm, "end": v(69.13, -97.52) * mm});
            skLineSegment(sketch, "E12.10.5.3", {"start": v(97.47, -69.18) * mm, "end": v(97.47, -97.52) * mm});
            skLineSegment(sketch, "E12.10.6.0", {"start": v(97.47, -35.85) * mm, "end": v(69.13, -35.85) * mm});
            skLineSegment(sketch, "E12.10.6.1", {"start": v(69.13, -35.85) * mm, "end": v(69.13, -64.19) * mm});
            skLineSegment(sketch, "E12.10.6.2", {"start": v(97.47, -64.19) * mm, "end": v(69.13, -64.19) * mm});
            skLineSegment(sketch, "E12.10.6.3", {"start": v(97.47, -35.85) * mm, "end": v(97.47, -64.19) * mm});
            skLineSegment(sketch, "E12.10.7.0", {"start": v(97.47, -2.52) * mm, "end": v(69.13, -2.52) * mm});
            skLineSegment(sketch, "E12.10.7.1", {"start": v(69.13, -2.52) * mm, "end": v(69.13, -30.86) * mm});
            skLineSegment(sketch, "E12.10.7.2", {"start": v(97.47, -30.86) * mm, "end": v(69.13, -30.86) * mm});
            skLineSegment(sketch, "E12.10.7.3", {"start": v(97.47, -2.52) * mm, "end": v(97.47, -30.86) * mm});
            skLineSegment(sketch, "E12.10.8.0", {"start": v(97.47, 30.8) * mm, "end": v(69.13, 30.8) * mm});
            skLineSegment(sketch, "E12.10.8.1", {"start": v(69.13, 30.8) * mm, "end": v(69.13, 2.47) * mm});
            skLineSegment(sketch, "E12.10.8.2", {"start": v(97.47, 2.47) * mm, "end": v(69.13, 2.47) * mm});
            skLineSegment(sketch, "E12.10.8.3", {"start": v(97.47, 30.8) * mm, "end": v(97.47, 2.47) * mm});
            skLineSegment(sketch, "E12.10.9.0", {"start": v(97.47, 64.14) * mm, "end": v(69.13, 64.14) * mm});
            skLineSegment(sketch, "E12.10.9.1", {"start": v(69.13, 64.14) * mm, "end": v(69.13, 35.8) * mm});
            skLineSegment(sketch, "E12.10.9.2", {"start": v(97.47, 35.8) * mm, "end": v(69.13, 35.8) * mm});
            skLineSegment(sketch, "E12.10.9.3", {"start": v(97.47, 64.14) * mm, "end": v(97.47, 35.8) * mm});
            skLineSegment(sketch, "E12.10.10.0", {"start": v(97.47, 97.47) * mm, "end": v(69.13, 97.47) * mm});
            skLineSegment(sketch, "E12.10.10.1", {"start": v(69.13, 97.47) * mm, "end": v(69.13, 69.13) * mm});
            skLineSegment(sketch, "E12.10.10.2", {"start": v(97.47, 69.13) * mm, "end": v(69.13, 69.13) * mm});
            skLineSegment(sketch, "E12.10.10.3", {"start": v(97.47, 97.47) * mm, "end": v(97.47, 69.13) * mm});
            skLineSegment(sketch, "E12.10.11.0", {"start": v(97.47, 130.8) * mm, "end": v(69.13, 130.8) * mm});
            skLineSegment(sketch, "E12.10.11.1", {"start": v(69.13, 130.8) * mm, "end": v(69.13, 102.46) * mm});
            skLineSegment(sketch, "E12.10.11.2", {"start": v(97.47, 102.46) * mm, "end": v(69.13, 102.46) * mm});
            skLineSegment(sketch, "E12.10.11.3", {"start": v(97.47, 130.8) * mm, "end": v(97.47, 102.46) * mm});
            skLineSegment(sketch, "E12.10.12.0", {"start": v(97.47, 164.13) * mm, "end": v(69.13, 164.13) * mm});
            skLineSegment(sketch, "E12.10.12.1", {"start": v(69.13, 164.13) * mm, "end": v(69.13, 135.8) * mm});
            skLineSegment(sketch, "E12.10.12.2", {"start": v(97.47, 135.8) * mm, "end": v(69.13, 135.8) * mm});
            skLineSegment(sketch, "E12.10.12.3", {"start": v(97.47, 164.13) * mm, "end": v(97.47, 135.8) * mm});
            skLineSegment(sketch, "E12.10.13.0", {"start": v(97.47, 197.46) * mm, "end": v(69.13, 197.46) * mm});
            skLineSegment(sketch, "E12.10.13.1", {"start": v(69.13, 197.46) * mm, "end": v(69.13, 169.12) * mm});
            skLineSegment(sketch, "E12.10.13.2", {"start": v(97.47, 169.12) * mm, "end": v(69.13, 169.12) * mm});
            skLineSegment(sketch, "E12.10.13.3", {"start": v(97.47, 197.46) * mm, "end": v(97.47, 169.12) * mm});
            skLineSegment(sketch, "E12.10.14.0", {"start": v(97.47, 230.79) * mm, "end": v(69.13, 230.79) * mm});
            skLineSegment(sketch, "E12.10.14.1", {"start": v(69.13, 230.79) * mm, "end": v(69.13, 202.45) * mm});
            skLineSegment(sketch, "E12.10.14.2", {"start": v(97.47, 202.45) * mm, "end": v(69.13, 202.45) * mm});
            skLineSegment(sketch, "E12.10.14.3", {"start": v(97.47, 230.79) * mm, "end": v(97.47, 202.45) * mm});
            skLineSegment(sketch, "E12.10.15.0", {"start": v(97.47, 264.12) * mm, "end": v(69.13, 264.12) * mm});
            skLineSegment(sketch, "E12.10.15.1", {"start": v(69.13, 264.12) * mm, "end": v(69.13, 235.78) * mm});
            skLineSegment(sketch, "E12.10.15.2", {"start": v(97.47, 235.78) * mm, "end": v(69.13, 235.78) * mm});
            skLineSegment(sketch, "E12.10.15.3", {"start": v(97.47, 264.12) * mm, "end": v(97.47, 235.78) * mm});
            skLineSegment(sketch, "E12.11.0.0", {"start": v(130.8, -235.83) * mm, "end": v(102.46, -235.83) * mm});
            skLineSegment(sketch, "E12.11.0.1", {"start": v(102.46, -235.83) * mm, "end": v(102.46, -264.17) * mm});
            skLineSegment(sketch, "E12.11.0.2", {"start": v(130.8, -264.17) * mm, "end": v(102.46, -264.17) * mm});
            skLineSegment(sketch, "E12.11.0.3", {"start": v(130.8, -235.83) * mm, "end": v(130.8, -264.17) * mm});
            skLineSegment(sketch, "E12.11.1.0", {"start": v(130.8, -202.5) * mm, "end": v(102.46, -202.5) * mm});
            skLineSegment(sketch, "E12.11.1.1", {"start": v(102.46, -202.5) * mm, "end": v(102.46, -230.84) * mm});
            skLineSegment(sketch, "E12.11.1.2", {"start": v(130.8, -230.84) * mm, "end": v(102.46, -230.84) * mm});
            skLineSegment(sketch, "E12.11.1.3", {"start": v(130.8, -202.5) * mm, "end": v(130.8, -230.84) * mm});
            skLineSegment(sketch, "E12.11.2.0", {"start": v(130.8, -169.17) * mm, "end": v(102.46, -169.17) * mm});
            skLineSegment(sketch, "E12.11.2.1", {"start": v(102.46, -169.17) * mm, "end": v(102.46, -197.5) * mm});
            skLineSegment(sketch, "E12.11.2.2", {"start": v(130.8, -197.5) * mm, "end": v(102.46, -197.5) * mm});
            skLineSegment(sketch, "E12.11.2.3", {"start": v(130.8, -169.17) * mm, "end": v(130.8, -197.5) * mm});
            skLineSegment(sketch, "E12.11.3.0", {"start": v(130.8, -135.84) * mm, "end": v(102.46, -135.84) * mm});
            skLineSegment(sketch, "E12.11.3.1", {"start": v(102.46, -135.84) * mm, "end": v(102.46, -164.18) * mm});
            skLineSegment(sketch, "E12.11.3.2", {"start": v(130.8, -164.18) * mm, "end": v(102.46, -164.18) * mm});
            skLineSegment(sketch, "E12.11.3.3", {"start": v(130.8, -135.84) * mm, "end": v(130.8, -164.18) * mm});
            skLineSegment(sketch, "E12.11.4.0", {"start": v(130.8, -102.51) * mm, "end": v(102.46, -102.51) * mm});
            skLineSegment(sketch, "E12.11.4.1", {"start": v(102.46, -102.51) * mm, "end": v(102.46, -130.85) * mm});
            skLineSegment(sketch, "E12.11.4.2", {"start": v(130.8, -130.85) * mm, "end": v(102.46, -130.85) * mm});
            skLineSegment(sketch, "E12.11.4.3", {"start": v(130.8, -102.51) * mm, "end": v(130.8, -130.85) * mm});
            skLineSegment(sketch, "E12.11.5.0", {"start": v(130.8, -69.18) * mm, "end": v(102.46, -69.18) * mm});
            skLineSegment(sketch, "E12.11.5.1", {"start": v(102.46, -69.18) * mm, "end": v(102.46, -97.52) * mm});
            skLineSegment(sketch, "E12.11.5.2", {"start": v(130.8, -97.52) * mm, "end": v(102.46, -97.52) * mm});
            skLineSegment(sketch, "E12.11.5.3", {"start": v(130.8, -69.18) * mm, "end": v(130.8, -97.52) * mm});
            skLineSegment(sketch, "E12.11.6.0", {"start": v(130.8, -35.85) * mm, "end": v(102.46, -35.85) * mm});
            skLineSegment(sketch, "E12.11.6.1", {"start": v(102.46, -35.85) * mm, "end": v(102.46, -64.19) * mm});
            skLineSegment(sketch, "E12.11.6.2", {"start": v(130.8, -64.19) * mm, "end": v(102.46, -64.19) * mm});
            skLineSegment(sketch, "E12.11.6.3", {"start": v(130.8, -35.85) * mm, "end": v(130.8, -64.19) * mm});
            skLineSegment(sketch, "E12.11.7.0", {"start": v(130.8, -2.52) * mm, "end": v(102.46, -2.52) * mm});
            skLineSegment(sketch, "E12.11.7.1", {"start": v(102.46, -2.52) * mm, "end": v(102.46, -30.86) * mm});
            skLineSegment(sketch, "E12.11.7.2", {"start": v(130.8, -30.86) * mm, "end": v(102.46, -30.86) * mm});
            skLineSegment(sketch, "E12.11.7.3", {"start": v(130.8, -2.52) * mm, "end": v(130.8, -30.86) * mm});
            skLineSegment(sketch, "E12.11.8.0", {"start": v(130.8, 30.8) * mm, "end": v(102.46, 30.8) * mm});
            skLineSegment(sketch, "E12.11.8.1", {"start": v(102.46, 30.8) * mm, "end": v(102.46, 2.47) * mm});
            skLineSegment(sketch, "E12.11.8.2", {"start": v(130.8, 2.47) * mm, "end": v(102.46, 2.47) * mm});
            skLineSegment(sketch, "E12.11.8.3", {"start": v(130.8, 30.8) * mm, "end": v(130.8, 2.47) * mm});
            skLineSegment(sketch, "E12.11.9.0", {"start": v(130.8, 64.14) * mm, "end": v(102.46, 64.14) * mm});
            skLineSegment(sketch, "E12.11.9.1", {"start": v(102.46, 64.14) * mm, "end": v(102.46, 35.8) * mm});
            skLineSegment(sketch, "E12.11.9.2", {"start": v(130.8, 35.8) * mm, "end": v(102.46, 35.8) * mm});
            skLineSegment(sketch, "E12.11.9.3", {"start": v(130.8, 64.14) * mm, "end": v(130.8, 35.8) * mm});
            skLineSegment(sketch, "E12.11.10.0", {"start": v(130.8, 97.47) * mm, "end": v(102.46, 97.47) * mm});
            skLineSegment(sketch, "E12.11.10.1", {"start": v(102.46, 97.47) * mm, "end": v(102.46, 69.13) * mm});
            skLineSegment(sketch, "E12.11.10.2", {"start": v(130.8, 69.13) * mm, "end": v(102.46, 69.13) * mm});
            skLineSegment(sketch, "E12.11.10.3", {"start": v(130.8, 97.47) * mm, "end": v(130.8, 69.13) * mm});
            skLineSegment(sketch, "E12.11.11.0", {"start": v(130.8, 130.8) * mm, "end": v(102.46, 130.8) * mm});
            skLineSegment(sketch, "E12.11.11.1", {"start": v(102.46, 130.8) * mm, "end": v(102.46, 102.46) * mm});
            skLineSegment(sketch, "E12.11.11.2", {"start": v(130.8, 102.46) * mm, "end": v(102.46, 102.46) * mm});
            skLineSegment(sketch, "E12.11.11.3", {"start": v(130.8, 130.8) * mm, "end": v(130.8, 102.46) * mm});
            skLineSegment(sketch, "E12.11.12.0", {"start": v(130.8, 164.13) * mm, "end": v(102.46, 164.13) * mm});
            skLineSegment(sketch, "E12.11.12.1", {"start": v(102.46, 164.13) * mm, "end": v(102.46, 135.8) * mm});
            skLineSegment(sketch, "E12.11.12.2", {"start": v(130.8, 135.8) * mm, "end": v(102.46, 135.8) * mm});
            skLineSegment(sketch, "E12.11.12.3", {"start": v(130.8, 164.13) * mm, "end": v(130.8, 135.8) * mm});
            skLineSegment(sketch, "E12.11.13.0", {"start": v(130.8, 197.46) * mm, "end": v(102.46, 197.46) * mm});
            skLineSegment(sketch, "E12.11.13.1", {"start": v(102.46, 197.46) * mm, "end": v(102.46, 169.12) * mm});
            skLineSegment(sketch, "E12.11.13.2", {"start": v(130.8, 169.12) * mm, "end": v(102.46, 169.12) * mm});
            skLineSegment(sketch, "E12.11.13.3", {"start": v(130.8, 197.46) * mm, "end": v(130.8, 169.12) * mm});
            skLineSegment(sketch, "E12.11.14.0", {"start": v(130.8, 230.79) * mm, "end": v(102.46, 230.79) * mm});
            skLineSegment(sketch, "E12.11.14.1", {"start": v(102.46, 230.79) * mm, "end": v(102.46, 202.45) * mm});
            skLineSegment(sketch, "E12.11.14.2", {"start": v(130.8, 202.45) * mm, "end": v(102.46, 202.45) * mm});
            skLineSegment(sketch, "E12.11.14.3", {"start": v(130.8, 230.79) * mm, "end": v(130.8, 202.45) * mm});
            skLineSegment(sketch, "E12.11.15.0", {"start": v(130.8, 264.12) * mm, "end": v(102.46, 264.12) * mm});
            skLineSegment(sketch, "E12.11.15.1", {"start": v(102.46, 264.12) * mm, "end": v(102.46, 235.78) * mm});
            skLineSegment(sketch, "E12.11.15.2", {"start": v(130.8, 235.78) * mm, "end": v(102.46, 235.78) * mm});
            skLineSegment(sketch, "E12.11.15.3", {"start": v(130.8, 264.12) * mm, "end": v(130.8, 235.78) * mm});
            skLineSegment(sketch, "E12.12.0.0", {"start": v(164.13, -235.83) * mm, "end": v(135.8, -235.83) * mm});
            skLineSegment(sketch, "E12.12.0.1", {"start": v(135.8, -235.83) * mm, "end": v(135.8, -264.17) * mm});
            skLineSegment(sketch, "E12.12.0.2", {"start": v(164.13, -264.17) * mm, "end": v(135.8, -264.17) * mm});
            skLineSegment(sketch, "E12.12.0.3", {"start": v(164.13, -235.83) * mm, "end": v(164.13, -264.17) * mm});
            skLineSegment(sketch, "E12.12.1.0", {"start": v(164.13, -202.5) * mm, "end": v(135.8, -202.5) * mm});
            skLineSegment(sketch, "E12.12.1.1", {"start": v(135.8, -202.5) * mm, "end": v(135.8, -230.84) * mm});
            skLineSegment(sketch, "E12.12.1.2", {"start": v(164.13, -230.84) * mm, "end": v(135.8, -230.84) * mm});
            skLineSegment(sketch, "E12.12.1.3", {"start": v(164.13, -202.5) * mm, "end": v(164.13, -230.84) * mm});
            skLineSegment(sketch, "E12.12.2.0", {"start": v(164.13, -169.17) * mm, "end": v(135.8, -169.17) * mm});
            skLineSegment(sketch, "E12.12.2.1", {"start": v(135.8, -169.17) * mm, "end": v(135.8, -197.5) * mm});
            skLineSegment(sketch, "E12.12.2.2", {"start": v(164.13, -197.5) * mm, "end": v(135.8, -197.5) * mm});
            skLineSegment(sketch, "E12.12.2.3", {"start": v(164.13, -169.17) * mm, "end": v(164.13, -197.5) * mm});
            skLineSegment(sketch, "E12.12.3.0", {"start": v(164.13, -135.84) * mm, "end": v(135.8, -135.84) * mm});
            skLineSegment(sketch, "E12.12.3.1", {"start": v(135.8, -135.84) * mm, "end": v(135.8, -164.18) * mm});
            skLineSegment(sketch, "E12.12.3.2", {"start": v(164.13, -164.18) * mm, "end": v(135.8, -164.18) * mm});
            skLineSegment(sketch, "E12.12.3.3", {"start": v(164.13, -135.84) * mm, "end": v(164.13, -164.18) * mm});
            skLineSegment(sketch, "E12.12.4.0", {"start": v(164.13, -102.51) * mm, "end": v(135.8, -102.51) * mm});
            skLineSegment(sketch, "E12.12.4.1", {"start": v(135.8, -102.51) * mm, "end": v(135.8, -130.85) * mm});
            skLineSegment(sketch, "E12.12.4.2", {"start": v(164.13, -130.85) * mm, "end": v(135.8, -130.85) * mm});
            skLineSegment(sketch, "E12.12.4.3", {"start": v(164.13, -102.51) * mm, "end": v(164.13, -130.85) * mm});
            skLineSegment(sketch, "E12.12.5.0", {"start": v(164.13, -69.18) * mm, "end": v(135.8, -69.18) * mm});
            skLineSegment(sketch, "E12.12.5.1", {"start": v(135.8, -69.18) * mm, "end": v(135.8, -97.52) * mm});
            skLineSegment(sketch, "E12.12.5.2", {"start": v(164.13, -97.52) * mm, "end": v(135.8, -97.52) * mm});
            skLineSegment(sketch, "E12.12.5.3", {"start": v(164.13, -69.18) * mm, "end": v(164.13, -97.52) * mm});
            skLineSegment(sketch, "E12.12.6.0", {"start": v(164.13, -35.85) * mm, "end": v(135.8, -35.85) * mm});
            skLineSegment(sketch, "E12.12.6.1", {"start": v(135.8, -35.85) * mm, "end": v(135.8, -64.19) * mm});
            skLineSegment(sketch, "E12.12.6.2", {"start": v(164.13, -64.19) * mm, "end": v(135.8, -64.19) * mm});
            skLineSegment(sketch, "E12.12.6.3", {"start": v(164.13, -35.85) * mm, "end": v(164.13, -64.19) * mm});
            skLineSegment(sketch, "E12.12.7.0", {"start": v(164.13, -2.52) * mm, "end": v(135.8, -2.52) * mm});
            skLineSegment(sketch, "E12.12.7.1", {"start": v(135.8, -2.52) * mm, "end": v(135.8, -30.86) * mm});
            skLineSegment(sketch, "E12.12.7.2", {"start": v(164.13, -30.86) * mm, "end": v(135.8, -30.86) * mm});
            skLineSegment(sketch, "E12.12.7.3", {"start": v(164.13, -2.52) * mm, "end": v(164.13, -30.86) * mm});
            skLineSegment(sketch, "E12.12.8.0", {"start": v(164.13, 30.8) * mm, "end": v(135.8, 30.8) * mm});
            skLineSegment(sketch, "E12.12.8.1", {"start": v(135.8, 30.8) * mm, "end": v(135.8, 2.47) * mm});
            skLineSegment(sketch, "E12.12.8.2", {"start": v(164.13, 2.47) * mm, "end": v(135.8, 2.47) * mm});
            skLineSegment(sketch, "E12.12.8.3", {"start": v(164.13, 30.8) * mm, "end": v(164.13, 2.47) * mm});
            skLineSegment(sketch, "E12.12.9.0", {"start": v(164.13, 64.14) * mm, "end": v(135.8, 64.14) * mm});
            skLineSegment(sketch, "E12.12.9.1", {"start": v(135.8, 64.14) * mm, "end": v(135.8, 35.8) * mm});
            skLineSegment(sketch, "E12.12.9.2", {"start": v(164.13, 35.8) * mm, "end": v(135.8, 35.8) * mm});
            skLineSegment(sketch, "E12.12.9.3", {"start": v(164.13, 64.14) * mm, "end": v(164.13, 35.8) * mm});
            skLineSegment(sketch, "E12.12.10.0", {"start": v(164.13, 97.47) * mm, "end": v(135.8, 97.47) * mm});
            skLineSegment(sketch, "E12.12.10.1", {"start": v(135.8, 97.47) * mm, "end": v(135.8, 69.13) * mm});
            skLineSegment(sketch, "E12.12.10.2", {"start": v(164.13, 69.13) * mm, "end": v(135.8, 69.13) * mm});
            skLineSegment(sketch, "E12.12.10.3", {"start": v(164.13, 97.47) * mm, "end": v(164.13, 69.13) * mm});
            skLineSegment(sketch, "E12.12.11.0", {"start": v(164.13, 130.8) * mm, "end": v(135.8, 130.8) * mm});
            skLineSegment(sketch, "E12.12.11.1", {"start": v(135.8, 130.8) * mm, "end": v(135.8, 102.46) * mm});
            skLineSegment(sketch, "E12.12.11.2", {"start": v(164.13, 102.46) * mm, "end": v(135.8, 102.46) * mm});
            skLineSegment(sketch, "E12.12.11.3", {"start": v(164.13, 130.8) * mm, "end": v(164.13, 102.46) * mm});
            skLineSegment(sketch, "E12.12.12.0", {"start": v(164.13, 164.13) * mm, "end": v(135.8, 164.13) * mm});
            skLineSegment(sketch, "E12.12.12.1", {"start": v(135.8, 164.13) * mm, "end": v(135.8, 135.8) * mm});
            skLineSegment(sketch, "E12.12.12.2", {"start": v(164.13, 135.8) * mm, "end": v(135.8, 135.8) * mm});
            skLineSegment(sketch, "E12.12.12.3", {"start": v(164.13, 164.13) * mm, "end": v(164.13, 135.8) * mm});
            skLineSegment(sketch, "E12.12.13.0", {"start": v(164.13, 197.46) * mm, "end": v(135.8, 197.46) * mm});
            skLineSegment(sketch, "E12.12.13.1", {"start": v(135.8, 197.46) * mm, "end": v(135.8, 169.12) * mm});
            skLineSegment(sketch, "E12.12.13.2", {"start": v(164.13, 169.12) * mm, "end": v(135.8, 169.12) * mm});
            skLineSegment(sketch, "E12.12.13.3", {"start": v(164.13, 197.46) * mm, "end": v(164.13, 169.12) * mm});
            skLineSegment(sketch, "E12.12.14.0", {"start": v(164.13, 230.79) * mm, "end": v(135.8, 230.79) * mm});
            skLineSegment(sketch, "E12.12.14.1", {"start": v(135.8, 230.79) * mm, "end": v(135.8, 202.45) * mm});
            skLineSegment(sketch, "E12.12.14.2", {"start": v(164.13, 202.45) * mm, "end": v(135.8, 202.45) * mm});
            skLineSegment(sketch, "E12.12.14.3", {"start": v(164.13, 230.79) * mm, "end": v(164.13, 202.45) * mm});
            skLineSegment(sketch, "E12.12.15.0", {"start": v(164.13, 264.12) * mm, "end": v(135.8, 264.12) * mm});
            skLineSegment(sketch, "E12.12.15.1", {"start": v(135.8, 264.12) * mm, "end": v(135.8, 235.78) * mm});
            skLineSegment(sketch, "E12.12.15.2", {"start": v(164.13, 235.78) * mm, "end": v(135.8, 235.78) * mm});
            skLineSegment(sketch, "E12.12.15.3", {"start": v(164.13, 264.12) * mm, "end": v(164.13, 235.78) * mm});
            skLineSegment(sketch, "E12.13.0.0", {"start": v(197.46, -235.83) * mm, "end": v(169.12, -235.83) * mm});
            skLineSegment(sketch, "E12.13.0.1", {"start": v(169.12, -235.83) * mm, "end": v(169.12, -264.17) * mm});
            skLineSegment(sketch, "E12.13.0.2", {"start": v(197.46, -264.17) * mm, "end": v(169.12, -264.17) * mm});
            skLineSegment(sketch, "E12.13.0.3", {"start": v(197.46, -235.83) * mm, "end": v(197.46, -264.17) * mm});
            skLineSegment(sketch, "E12.13.1.0", {"start": v(197.46, -202.5) * mm, "end": v(169.12, -202.5) * mm});
            skLineSegment(sketch, "E12.13.1.1", {"start": v(169.12, -202.5) * mm, "end": v(169.12, -230.84) * mm});
            skLineSegment(sketch, "E12.13.1.2", {"start": v(197.46, -230.84) * mm, "end": v(169.12, -230.84) * mm});
            skLineSegment(sketch, "E12.13.1.3", {"start": v(197.46, -202.5) * mm, "end": v(197.46, -230.84) * mm});
            skLineSegment(sketch, "E12.13.2.0", {"start": v(197.46, -169.17) * mm, "end": v(169.12, -169.17) * mm});
            skLineSegment(sketch, "E12.13.2.1", {"start": v(169.12, -169.17) * mm, "end": v(169.12, -197.5) * mm});
            skLineSegment(sketch, "E12.13.2.2", {"start": v(197.46, -197.5) * mm, "end": v(169.12, -197.5) * mm});
            skLineSegment(sketch, "E12.13.2.3", {"start": v(197.46, -169.17) * mm, "end": v(197.46, -197.5) * mm});
            skLineSegment(sketch, "E12.13.3.0", {"start": v(197.46, -135.84) * mm, "end": v(169.12, -135.84) * mm});
            skLineSegment(sketch, "E12.13.3.1", {"start": v(169.12, -135.84) * mm, "end": v(169.12, -164.18) * mm});
            skLineSegment(sketch, "E12.13.3.2", {"start": v(197.46, -164.18) * mm, "end": v(169.12, -164.18) * mm});
            skLineSegment(sketch, "E12.13.3.3", {"start": v(197.46, -135.84) * mm, "end": v(197.46, -164.18) * mm});
            skLineSegment(sketch, "E12.13.4.0", {"start": v(197.46, -102.51) * mm, "end": v(169.12, -102.51) * mm});
            skLineSegment(sketch, "E12.13.4.1", {"start": v(169.12, -102.51) * mm, "end": v(169.12, -130.85) * mm});
            skLineSegment(sketch, "E12.13.4.2", {"start": v(197.46, -130.85) * mm, "end": v(169.12, -130.85) * mm});
            skLineSegment(sketch, "E12.13.4.3", {"start": v(197.46, -102.51) * mm, "end": v(197.46, -130.85) * mm});
            skLineSegment(sketch, "E12.13.5.0", {"start": v(197.46, -69.18) * mm, "end": v(169.12, -69.18) * mm});
            skLineSegment(sketch, "E12.13.5.1", {"start": v(169.12, -69.18) * mm, "end": v(169.12, -97.52) * mm});
            skLineSegment(sketch, "E12.13.5.2", {"start": v(197.46, -97.52) * mm, "end": v(169.12, -97.52) * mm});
            skLineSegment(sketch, "E12.13.5.3", {"start": v(197.46, -69.18) * mm, "end": v(197.46, -97.52) * mm});
            skLineSegment(sketch, "E12.13.6.0", {"start": v(197.46, -35.85) * mm, "end": v(169.12, -35.85) * mm});
            skLineSegment(sketch, "E12.13.6.1", {"start": v(169.12, -35.85) * mm, "end": v(169.12, -64.19) * mm});
            skLineSegment(sketch, "E12.13.6.2", {"start": v(197.46, -64.19) * mm, "end": v(169.12, -64.19) * mm});
            skLineSegment(sketch, "E12.13.6.3", {"start": v(197.46, -35.85) * mm, "end": v(197.46, -64.19) * mm});
            skLineSegment(sketch, "E12.13.7.0", {"start": v(197.46, -2.52) * mm, "end": v(169.12, -2.52) * mm});
            skLineSegment(sketch, "E12.13.7.1", {"start": v(169.12, -2.52) * mm, "end": v(169.12, -30.86) * mm});
            skLineSegment(sketch, "E12.13.7.2", {"start": v(197.46, -30.86) * mm, "end": v(169.12, -30.86) * mm});
            skLineSegment(sketch, "E12.13.7.3", {"start": v(197.46, -2.52) * mm, "end": v(197.46, -30.86) * mm});
            skLineSegment(sketch, "E12.13.8.0", {"start": v(197.46, 30.8) * mm, "end": v(169.12, 30.8) * mm});
            skLineSegment(sketch, "E12.13.8.1", {"start": v(169.12, 30.8) * mm, "end": v(169.12, 2.47) * mm});
            skLineSegment(sketch, "E12.13.8.2", {"start": v(197.46, 2.47) * mm, "end": v(169.12, 2.47) * mm});
            skLineSegment(sketch, "E12.13.8.3", {"start": v(197.46, 30.8) * mm, "end": v(197.46, 2.47) * mm});
            skLineSegment(sketch, "E12.13.9.0", {"start": v(197.46, 64.14) * mm, "end": v(169.12, 64.14) * mm});
            skLineSegment(sketch, "E12.13.9.1", {"start": v(169.12, 64.14) * mm, "end": v(169.12, 35.8) * mm});
            skLineSegment(sketch, "E12.13.9.2", {"start": v(197.46, 35.8) * mm, "end": v(169.12, 35.8) * mm});
            skLineSegment(sketch, "E12.13.9.3", {"start": v(197.46, 64.14) * mm, "end": v(197.46, 35.8) * mm});
            skLineSegment(sketch, "E12.13.10.0", {"start": v(197.46, 97.47) * mm, "end": v(169.12, 97.47) * mm});
            skLineSegment(sketch, "E12.13.10.1", {"start": v(169.12, 97.47) * mm, "end": v(169.12, 69.13) * mm});
            skLineSegment(sketch, "E12.13.10.2", {"start": v(197.46, 69.13) * mm, "end": v(169.12, 69.13) * mm});
            skLineSegment(sketch, "E12.13.10.3", {"start": v(197.46, 97.47) * mm, "end": v(197.46, 69.13) * mm});
            skLineSegment(sketch, "E12.13.11.0", {"start": v(197.46, 130.8) * mm, "end": v(169.12, 130.8) * mm});
            skLineSegment(sketch, "E12.13.11.1", {"start": v(169.12, 130.8) * mm, "end": v(169.12, 102.46) * mm});
            skLineSegment(sketch, "E12.13.11.2", {"start": v(197.46, 102.46) * mm, "end": v(169.12, 102.46) * mm});
            skLineSegment(sketch, "E12.13.11.3", {"start": v(197.46, 130.8) * mm, "end": v(197.46, 102.46) * mm});
            skLineSegment(sketch, "E12.13.12.0", {"start": v(197.46, 164.13) * mm, "end": v(169.12, 164.13) * mm});
            skLineSegment(sketch, "E12.13.12.1", {"start": v(169.12, 164.13) * mm, "end": v(169.12, 135.8) * mm});
            skLineSegment(sketch, "E12.13.12.2", {"start": v(197.46, 135.8) * mm, "end": v(169.12, 135.8) * mm});
            skLineSegment(sketch, "E12.13.12.3", {"start": v(197.46, 164.13) * mm, "end": v(197.46, 135.8) * mm});
            skLineSegment(sketch, "E12.13.13.0", {"start": v(197.46, 197.46) * mm, "end": v(169.12, 197.46) * mm});
            skLineSegment(sketch, "E12.13.13.1", {"start": v(169.12, 197.46) * mm, "end": v(169.12, 169.12) * mm});
            skLineSegment(sketch, "E12.13.13.2", {"start": v(197.46, 169.12) * mm, "end": v(169.12, 169.12) * mm});
            skLineSegment(sketch, "E12.13.13.3", {"start": v(197.46, 197.46) * mm, "end": v(197.46, 169.12) * mm});
            skLineSegment(sketch, "E12.13.14.0", {"start": v(197.46, 230.79) * mm, "end": v(169.12, 230.79) * mm});
            skLineSegment(sketch, "E12.13.14.1", {"start": v(169.12, 230.79) * mm, "end": v(169.12, 202.45) * mm});
            skLineSegment(sketch, "E12.13.14.2", {"start": v(197.46, 202.45) * mm, "end": v(169.12, 202.45) * mm});
            skLineSegment(sketch, "E12.13.14.3", {"start": v(197.46, 230.79) * mm, "end": v(197.46, 202.45) * mm});
            skLineSegment(sketch, "E12.13.15.0", {"start": v(197.46, 264.12) * mm, "end": v(169.12, 264.12) * mm});
            skLineSegment(sketch, "E12.13.15.1", {"start": v(169.12, 264.12) * mm, "end": v(169.12, 235.78) * mm});
            skLineSegment(sketch, "E12.13.15.2", {"start": v(197.46, 235.78) * mm, "end": v(169.12, 235.78) * mm});
            skLineSegment(sketch, "E12.13.15.3", {"start": v(197.46, 264.12) * mm, "end": v(197.46, 235.78) * mm});
            skLineSegment(sketch, "E12.14.0.0", {"start": v(230.79, -235.83) * mm, "end": v(202.45, -235.83) * mm});
            skLineSegment(sketch, "E12.14.0.1", {"start": v(202.45, -235.83) * mm, "end": v(202.45, -264.17) * mm});
            skLineSegment(sketch, "E12.14.0.2", {"start": v(230.79, -264.17) * mm, "end": v(202.45, -264.17) * mm});
            skLineSegment(sketch, "E12.14.0.3", {"start": v(230.79, -235.83) * mm, "end": v(230.79, -264.17) * mm});
            skLineSegment(sketch, "E12.14.1.0", {"start": v(230.79, -202.5) * mm, "end": v(202.45, -202.5) * mm});
            skLineSegment(sketch, "E12.14.1.1", {"start": v(202.45, -202.5) * mm, "end": v(202.45, -230.84) * mm});
            skLineSegment(sketch, "E12.14.1.2", {"start": v(230.79, -230.84) * mm, "end": v(202.45, -230.84) * mm});
            skLineSegment(sketch, "E12.14.1.3", {"start": v(230.79, -202.5) * mm, "end": v(230.79, -230.84) * mm});
            skLineSegment(sketch, "E12.14.2.0", {"start": v(230.79, -169.17) * mm, "end": v(202.45, -169.17) * mm});
            skLineSegment(sketch, "E12.14.2.1", {"start": v(202.45, -169.17) * mm, "end": v(202.45, -197.5) * mm});
            skLineSegment(sketch, "E12.14.2.2", {"start": v(230.79, -197.5) * mm, "end": v(202.45, -197.5) * mm});
            skLineSegment(sketch, "E12.14.2.3", {"start": v(230.79, -169.17) * mm, "end": v(230.79, -197.5) * mm});
            skLineSegment(sketch, "E12.14.3.0", {"start": v(230.79, -135.84) * mm, "end": v(202.45, -135.84) * mm});
            skLineSegment(sketch, "E12.14.3.1", {"start": v(202.45, -135.84) * mm, "end": v(202.45, -164.18) * mm});
            skLineSegment(sketch, "E12.14.3.2", {"start": v(230.79, -164.18) * mm, "end": v(202.45, -164.18) * mm});
            skLineSegment(sketch, "E12.14.3.3", {"start": v(230.79, -135.84) * mm, "end": v(230.79, -164.18) * mm});
            skLineSegment(sketch, "E12.14.4.0", {"start": v(230.79, -102.51) * mm, "end": v(202.45, -102.51) * mm});
            skLineSegment(sketch, "E12.14.4.1", {"start": v(202.45, -102.51) * mm, "end": v(202.45, -130.85) * mm});
            skLineSegment(sketch, "E12.14.4.2", {"start": v(230.79, -130.85) * mm, "end": v(202.45, -130.85) * mm});
            skLineSegment(sketch, "E12.14.4.3", {"start": v(230.79, -102.51) * mm, "end": v(230.79, -130.85) * mm});
            skLineSegment(sketch, "E12.14.5.0", {"start": v(230.79, -69.18) * mm, "end": v(202.45, -69.18) * mm});
            skLineSegment(sketch, "E12.14.5.1", {"start": v(202.45, -69.18) * mm, "end": v(202.45, -97.52) * mm});
            skLineSegment(sketch, "E12.14.5.2", {"start": v(230.79, -97.52) * mm, "end": v(202.45, -97.52) * mm});
            skLineSegment(sketch, "E12.14.5.3", {"start": v(230.79, -69.18) * mm, "end": v(230.79, -97.52) * mm});
            skLineSegment(sketch, "E12.14.6.0", {"start": v(230.79, -35.85) * mm, "end": v(202.45, -35.85) * mm});
            skLineSegment(sketch, "E12.14.6.1", {"start": v(202.45, -35.85) * mm, "end": v(202.45, -64.19) * mm});
            skLineSegment(sketch, "E12.14.6.2", {"start": v(230.79, -64.19) * mm, "end": v(202.45, -64.19) * mm});
            skLineSegment(sketch, "E12.14.6.3", {"start": v(230.79, -35.85) * mm, "end": v(230.79, -64.19) * mm});
            skLineSegment(sketch, "E12.14.7.0", {"start": v(230.79, -2.52) * mm, "end": v(202.45, -2.52) * mm});
            skLineSegment(sketch, "E12.14.7.1", {"start": v(202.45, -2.52) * mm, "end": v(202.45, -30.86) * mm});
            skLineSegment(sketch, "E12.14.7.2", {"start": v(230.79, -30.86) * mm, "end": v(202.45, -30.86) * mm});
            skLineSegment(sketch, "E12.14.7.3", {"start": v(230.79, -2.52) * mm, "end": v(230.79, -30.86) * mm});
            skLineSegment(sketch, "E12.14.8.0", {"start": v(230.79, 30.8) * mm, "end": v(202.45, 30.8) * mm});
            skLineSegment(sketch, "E12.14.8.1", {"start": v(202.45, 30.8) * mm, "end": v(202.45, 2.47) * mm});
            skLineSegment(sketch, "E12.14.8.2", {"start": v(230.79, 2.47) * mm, "end": v(202.45, 2.47) * mm});
            skLineSegment(sketch, "E12.14.8.3", {"start": v(230.79, 30.8) * mm, "end": v(230.79, 2.47) * mm});
            skLineSegment(sketch, "E12.14.9.0", {"start": v(230.79, 64.14) * mm, "end": v(202.45, 64.14) * mm});
            skLineSegment(sketch, "E12.14.9.1", {"start": v(202.45, 64.14) * mm, "end": v(202.45, 35.8) * mm});
            skLineSegment(sketch, "E12.14.9.2", {"start": v(230.79, 35.8) * mm, "end": v(202.45, 35.8) * mm});
            skLineSegment(sketch, "E12.14.9.3", {"start": v(230.79, 64.14) * mm, "end": v(230.79, 35.8) * mm});
            skLineSegment(sketch, "E12.14.10.0", {"start": v(230.79, 97.47) * mm, "end": v(202.45, 97.47) * mm});
            skLineSegment(sketch, "E12.14.10.1", {"start": v(202.45, 97.47) * mm, "end": v(202.45, 69.13) * mm});
            skLineSegment(sketch, "E12.14.10.2", {"start": v(230.79, 69.13) * mm, "end": v(202.45, 69.13) * mm});
            skLineSegment(sketch, "E12.14.10.3", {"start": v(230.79, 97.47) * mm, "end": v(230.79, 69.13) * mm});
            skLineSegment(sketch, "E12.14.11.0", {"start": v(230.79, 130.8) * mm, "end": v(202.45, 130.8) * mm});
            skLineSegment(sketch, "E12.14.11.1", {"start": v(202.45, 130.8) * mm, "end": v(202.45, 102.46) * mm});
            skLineSegment(sketch, "E12.14.11.2", {"start": v(230.79, 102.46) * mm, "end": v(202.45, 102.46) * mm});
            skLineSegment(sketch, "E12.14.11.3", {"start": v(230.79, 130.8) * mm, "end": v(230.79, 102.46) * mm});
            skLineSegment(sketch, "E12.14.12.0", {"start": v(230.79, 164.13) * mm, "end": v(202.45, 164.13) * mm});
            skLineSegment(sketch, "E12.14.12.1", {"start": v(202.45, 164.13) * mm, "end": v(202.45, 135.8) * mm});
            skLineSegment(sketch, "E12.14.12.2", {"start": v(230.79, 135.8) * mm, "end": v(202.45, 135.8) * mm});
            skLineSegment(sketch, "E12.14.12.3", {"start": v(230.79, 164.13) * mm, "end": v(230.79, 135.8) * mm});
            skLineSegment(sketch, "E12.14.13.0", {"start": v(230.79, 197.46) * mm, "end": v(202.45, 197.46) * mm});
            skLineSegment(sketch, "E12.14.13.1", {"start": v(202.45, 197.46) * mm, "end": v(202.45, 169.12) * mm});
            skLineSegment(sketch, "E12.14.13.2", {"start": v(230.79, 169.12) * mm, "end": v(202.45, 169.12) * mm});
            skLineSegment(sketch, "E12.14.13.3", {"start": v(230.79, 197.46) * mm, "end": v(230.79, 169.12) * mm});
            skLineSegment(sketch, "E12.14.14.0", {"start": v(230.79, 230.79) * mm, "end": v(202.45, 230.79) * mm});
            skLineSegment(sketch, "E12.14.14.1", {"start": v(202.45, 230.79) * mm, "end": v(202.45, 202.45) * mm});
            skLineSegment(sketch, "E12.14.14.2", {"start": v(230.79, 202.45) * mm, "end": v(202.45, 202.45) * mm});
            skLineSegment(sketch, "E12.14.14.3", {"start": v(230.79, 230.79) * mm, "end": v(230.79, 202.45) * mm});
            skLineSegment(sketch, "E12.14.15.0", {"start": v(230.79, 264.12) * mm, "end": v(202.45, 264.12) * mm});
            skLineSegment(sketch, "E12.14.15.1", {"start": v(202.45, 264.12) * mm, "end": v(202.45, 235.78) * mm});
            skLineSegment(sketch, "E12.14.15.2", {"start": v(230.79, 235.78) * mm, "end": v(202.45, 235.78) * mm});
            skLineSegment(sketch, "E12.14.15.3", {"start": v(230.79, 264.12) * mm, "end": v(230.79, 235.78) * mm});
            skLineSegment(sketch, "E12.15.0.0", {"start": v(264.12, -235.83) * mm, "end": v(235.78, -235.83) * mm});
            skLineSegment(sketch, "E12.15.0.1", {"start": v(235.78, -235.83) * mm, "end": v(235.78, -264.17) * mm});
            skLineSegment(sketch, "E12.15.0.2", {"start": v(264.12, -264.17) * mm, "end": v(235.78, -264.17) * mm});
            skLineSegment(sketch, "E12.15.0.3", {"start": v(264.12, -235.83) * mm, "end": v(264.12, -264.17) * mm});
            skLineSegment(sketch, "E12.15.1.0", {"start": v(264.12, -202.5) * mm, "end": v(235.78, -202.5) * mm});
            skLineSegment(sketch, "E12.15.1.1", {"start": v(235.78, -202.5) * mm, "end": v(235.78, -230.84) * mm});
            skLineSegment(sketch, "E12.15.1.2", {"start": v(264.12, -230.84) * mm, "end": v(235.78, -230.84) * mm});
            skLineSegment(sketch, "E12.15.1.3", {"start": v(264.12, -202.5) * mm, "end": v(264.12, -230.84) * mm});
            skLineSegment(sketch, "E12.15.2.0", {"start": v(264.12, -169.17) * mm, "end": v(235.78, -169.17) * mm});
            skLineSegment(sketch, "E12.15.2.1", {"start": v(235.78, -169.17) * mm, "end": v(235.78, -197.5) * mm});
            skLineSegment(sketch, "E12.15.2.2", {"start": v(264.12, -197.5) * mm, "end": v(235.78, -197.5) * mm});
            skLineSegment(sketch, "E12.15.2.3", {"start": v(264.12, -169.17) * mm, "end": v(264.12, -197.5) * mm});
            skLineSegment(sketch, "E12.15.3.0", {"start": v(264.12, -135.84) * mm, "end": v(235.78, -135.84) * mm});
            skLineSegment(sketch, "E12.15.3.1", {"start": v(235.78, -135.84) * mm, "end": v(235.78, -164.18) * mm});
            skLineSegment(sketch, "E12.15.3.2", {"start": v(264.12, -164.18) * mm, "end": v(235.78, -164.18) * mm});
            skLineSegment(sketch, "E12.15.3.3", {"start": v(264.12, -135.84) * mm, "end": v(264.12, -164.18) * mm});
            skLineSegment(sketch, "E12.15.4.0", {"start": v(264.12, -102.51) * mm, "end": v(235.78, -102.51) * mm});
            skLineSegment(sketch, "E12.15.4.1", {"start": v(235.78, -102.51) * mm, "end": v(235.78, -130.85) * mm});
            skLineSegment(sketch, "E12.15.4.2", {"start": v(264.12, -130.85) * mm, "end": v(235.78, -130.85) * mm});
            skLineSegment(sketch, "E12.15.4.3", {"start": v(264.12, -102.51) * mm, "end": v(264.12, -130.85) * mm});
            skLineSegment(sketch, "E12.15.5.0", {"start": v(264.12, -69.18) * mm, "end": v(235.78, -69.18) * mm});
            skLineSegment(sketch, "E12.15.5.1", {"start": v(235.78, -69.18) * mm, "end": v(235.78, -97.52) * mm});
            skLineSegment(sketch, "E12.15.5.2", {"start": v(264.12, -97.52) * mm, "end": v(235.78, -97.52) * mm});
            skLineSegment(sketch, "E12.15.5.3", {"start": v(264.12, -69.18) * mm, "end": v(264.12, -97.52) * mm});
            skLineSegment(sketch, "E12.15.6.0", {"start": v(264.12, -35.85) * mm, "end": v(235.78, -35.85) * mm});
            skLineSegment(sketch, "E12.15.6.1", {"start": v(235.78, -35.85) * mm, "end": v(235.78, -64.19) * mm});
            skLineSegment(sketch, "E12.15.6.2", {"start": v(264.12, -64.19) * mm, "end": v(235.78, -64.19) * mm});
            skLineSegment(sketch, "E12.15.6.3", {"start": v(264.12, -35.85) * mm, "end": v(264.12, -64.19) * mm});
            skLineSegment(sketch, "E12.15.7.0", {"start": v(264.12, -2.52) * mm, "end": v(235.78, -2.52) * mm});
            skLineSegment(sketch, "E12.15.7.1", {"start": v(235.78, -2.52) * mm, "end": v(235.78, -30.86) * mm});
            skLineSegment(sketch, "E12.15.7.2", {"start": v(264.12, -30.86) * mm, "end": v(235.78, -30.86) * mm});
            skLineSegment(sketch, "E12.15.7.3", {"start": v(264.12, -2.52) * mm, "end": v(264.12, -30.86) * mm});
            skLineSegment(sketch, "E12.15.8.0", {"start": v(264.12, 30.8) * mm, "end": v(235.78, 30.8) * mm});
            skLineSegment(sketch, "E12.15.8.1", {"start": v(235.78, 30.8) * mm, "end": v(235.78, 2.47) * mm});
            skLineSegment(sketch, "E12.15.8.2", {"start": v(264.12, 2.47) * mm, "end": v(235.78, 2.47) * mm});
            skLineSegment(sketch, "E12.15.8.3", {"start": v(264.12, 30.8) * mm, "end": v(264.12, 2.47) * mm});
            skLineSegment(sketch, "E12.15.9.0", {"start": v(264.12, 64.14) * mm, "end": v(235.78, 64.14) * mm});
            skLineSegment(sketch, "E12.15.9.1", {"start": v(235.78, 64.14) * mm, "end": v(235.78, 35.8) * mm});
            skLineSegment(sketch, "E12.15.9.2", {"start": v(264.12, 35.8) * mm, "end": v(235.78, 35.8) * mm});
            skLineSegment(sketch, "E12.15.9.3", {"start": v(264.12, 64.14) * mm, "end": v(264.12, 35.8) * mm});
            skLineSegment(sketch, "E12.15.10.0", {"start": v(264.12, 97.47) * mm, "end": v(235.78, 97.47) * mm});
            skLineSegment(sketch, "E12.15.10.1", {"start": v(235.78, 97.47) * mm, "end": v(235.78, 69.13) * mm});
            skLineSegment(sketch, "E12.15.10.2", {"start": v(264.12, 69.13) * mm, "end": v(235.78, 69.13) * mm});
            skLineSegment(sketch, "E12.15.10.3", {"start": v(264.12, 97.47) * mm, "end": v(264.12, 69.13) * mm});
            skLineSegment(sketch, "E12.15.11.0", {"start": v(264.12, 130.8) * mm, "end": v(235.78, 130.8) * mm});
            skLineSegment(sketch, "E12.15.11.1", {"start": v(235.78, 130.8) * mm, "end": v(235.78, 102.46) * mm});
            skLineSegment(sketch, "E12.15.11.2", {"start": v(264.12, 102.46) * mm, "end": v(235.78, 102.46) * mm});
            skLineSegment(sketch, "E12.15.11.3", {"start": v(264.12, 130.8) * mm, "end": v(264.12, 102.46) * mm});
            skLineSegment(sketch, "E12.15.12.0", {"start": v(264.12, 164.13) * mm, "end": v(235.78, 164.13) * mm});
            skLineSegment(sketch, "E12.15.12.1", {"start": v(235.78, 164.13) * mm, "end": v(235.78, 135.8) * mm});
            skLineSegment(sketch, "E12.15.12.2", {"start": v(264.12, 135.8) * mm, "end": v(235.78, 135.8) * mm});
            skLineSegment(sketch, "E12.15.12.3", {"start": v(264.12, 164.13) * mm, "end": v(264.12, 135.8) * mm});
            skLineSegment(sketch, "E12.15.13.0", {"start": v(264.12, 197.46) * mm, "end": v(235.78, 197.46) * mm});
            skLineSegment(sketch, "E12.15.13.1", {"start": v(235.78, 197.46) * mm, "end": v(235.78, 169.12) * mm});
            skLineSegment(sketch, "E12.15.13.2", {"start": v(264.12, 169.12) * mm, "end": v(235.78, 169.12) * mm});
            skLineSegment(sketch, "E12.15.13.3", {"start": v(264.12, 197.46) * mm, "end": v(264.12, 169.12) * mm});
            skLineSegment(sketch, "E12.15.14.0", {"start": v(264.12, 230.79) * mm, "end": v(235.78, 230.79) * mm});
            skLineSegment(sketch, "E12.15.14.1", {"start": v(235.78, 230.79) * mm, "end": v(235.78, 202.45) * mm});
            skLineSegment(sketch, "E12.15.14.2", {"start": v(264.12, 202.45) * mm, "end": v(235.78, 202.45) * mm});
            skLineSegment(sketch, "E12.15.14.3", {"start": v(264.12, 230.79) * mm, "end": v(264.12, 202.45) * mm});
            skLineSegment(sketch, "E12.15.15.0", {"start": v(264.12, 264.12) * mm, "end": v(235.78, 264.12) * mm});
            skLineSegment(sketch, "E12.15.15.1", {"start": v(235.78, 264.12) * mm, "end": v(235.78, 235.78) * mm});
            skLineSegment(sketch, "E12.15.15.2", {"start": v(264.12, 235.78) * mm, "end": v(235.78, 235.78) * mm});
            skLineSegment(sketch, "E12.15.15.3", {"start": v(264.12, 264.12) * mm, "end": v(264.12, 235.78) * mm});
            skLineSegment(sketch, "E12.direction1", {"start": v(-264.17, -235.83) * mm, "end": v(-230.84, -235.83) * mm, "construction": true});
            skLineSegment(sketch, "E12.direction2", {"start": v(-264.17, -235.83) * mm, "end": v(-264.17, -202.5) * mm, "construction": true});
            skSolve(sketch);
        }
        {
            var Q0;
            Q0 = qSketchRegion(id + "F7", true);
            extrude(context, id + "F8", {"entities" : qUnion([Q0]), "depth" : getVariable(context, 'D3')});
        }
        {
            var Q0;
            Q0=makeQuery(id+"F5.imprint","IMPRINT",FACE,{"disambiguationData":[TD([[makeQuery(id+"F5.imprint","IMPRINT",EDGE,{"derivedFrom":sQuery(id+"F5.wireOp",EDGE,"E5.bottom")}),1.0]])]});
            var sketch = newSketch(context, id + "F9", { "sketchPlane" : qUnion([Q0])});
            skLineSegment(sketch, "E13", {"start": v(-404.4, 0) * mm, "end": v(414.1, 0) * mm, "construction": true});
            skLineSegment(sketch, "E14", {"start": v(0, 325.81) * mm, "end": v(0, -333.76) * mm, "construction": true});
            skLineSegment(sketch, "E15.bottom", {"start": v(-180, 350) * mm, "end": v(40, 350) * mm});
            skLineSegment(sketch, "E15.top", {"start": v(-180, 247) * mm, "end": v(40, 247) * mm});
            skLineSegment(sketch, "E15.left", {"start": v(-180, 350) * mm, "end": v(-180, 247) * mm});
            skLineSegment(sketch, "E15.right", {"start": v(40, 350) * mm, "end": v(40, 247) * mm});
            skCircle(sketch, "E16", {"center": v(133.97, 274) * mm, "radius": 1.37 * mm});
            skCircle(sketch, "E17.0.1.0", {"center": v(133.97, 323) * mm, "radius": 1.37 * mm});
            skCircle(sketch, "E17.1.0.0", {"center": v(191.97, 274) * mm, "radius": 1.37 * mm});
            skCircle(sketch, "E17.1.1.0", {"center": v(191.97, 323) * mm, "radius": 1.37 * mm});
            skLineSegment(sketch, "E17.direction1", {"start": v(133.97, 274) * mm, "end": v(191.97, 274) * mm, "construction": true});
            skLineSegment(sketch, "E17.direction2", {"start": v(133.97, 274) * mm, "end": v(133.97, 323) * mm, "construction": true});
            skPoint(sketch, "E18", {"position": v(133.97, 298.5) * mm});
            skLineSegment(sketch, "E19.bottom", {"start": v(-175, -275) * mm, "end": v(175, -275) * mm});
            skLineSegment(sketch, "E19.top", {"start": v(-175, -315) * mm, "end": v(175, -315) * mm});
            skLineSegment(sketch, "E19.left", {"start": v(-175, -275) * mm, "end": v(-175, -315) * mm});
            skLineSegment(sketch, "E19.right", {"start": v(175, -275) * mm, "end": v(175, -315) * mm});
            skSolve(sketch);
        }
        {
            var Q0;
            Q0 = qSketchRegion(id + "F9", true);
            extrude(context, id + "F10", {"entities" : qUnion([Q0]), "endBound" : BoundingType.SYMMETRIC, "depth" : 100 * mm, "offsetDistance" : 25 * mm});
        }
        {
            var Q0;
            Q0=makeQuery(id+"F10.opExtrude","SWEPT_BODY",BODY,{"disambiguationData":[OSD([sQuery(id+"F9.wireOp",EDGE,"uxuEBIeV-0xVb-TPub-oXEo-MvxfBFeGTrLM.bottom"),sQuery(id+"F9.wireOp",EDGE,"uxuEBIeV-0xVb-TPub-oXEo-MvxfBFeGTrLM.top"),sQuery(id+"F9.wireOp",EDGE,"uxuEBIeV-0xVb-TPub-oXEo-MvxfBFeGTrLM.left"),sQuery(id+"F9.wireOp",EDGE,"uxuEBIeV-0xVb-TPub-oXEo-MvxfBFeGTrLM.right")])]});
            var Q1;
            Q1=makeQuery(id+"F10.opExtrude","SWEPT_BODY",BODY,{"disambiguationData":[OSD([sQuery(id+"F9.wireOp",EDGE,"e7507a01-ba6c-4bb6-a28b-4927f63d707e0.MirrorCS"),sQuery(id+"F9.wireOp",EDGE,"56642bb9-9ec8-4155-a1c9-89c43985ba1c0.MirrorCS"),sQuery(id+"F9.wireOp",EDGE,"c723e08c-2ddf-4861-af5f-36fcd062a6b60.MirrorCS"),sQuery(id+"F9.wireOp",EDGE,"c0e9a162-dabb-429c-a051-153cd77148f50.MirrorCS")])]});
            var Q2;
            Q2=makeQuery(id+"F10.opExtrude","SWEPT_BODY",BODY,{"disambiguationData":[OSD([sQuery(id+"F9.wireOp",EDGE,"E15.bottom"),sQuery(id+"F9.wireOp",EDGE,"E15.top"),sQuery(id+"F9.wireOp",EDGE,"E15.left"),sQuery(id+"F9.wireOp",EDGE,"E15.right")])]});
            var Q3;
            Q3=makeQuery(id+"F10.opExtrude","SWEPT_BODY",BODY,{"disambiguationData":[OSD([sQuery(id+"F9.wireOp",EDGE,"E17.0.1.0")])]});
            var Q4;
            Q4=makeQuery(id+"F10.opExtrude","SWEPT_BODY",BODY,{"disambiguationData":[OSD([sQuery(id+"F9.wireOp",EDGE,"E17.1.1.0")])]});
            var Q5;
            Q5=makeQuery(id+"F10.opExtrude","SWEPT_BODY",BODY,{"disambiguationData":[OSD([sQuery(id+"F9.wireOp",EDGE,"E17.1.0.0")])]});
            var Q6;
            Q6=makeQuery(id+"F10.opExtrude","SWEPT_BODY",BODY,{"disambiguationData":[OSD([sQuery(id+"F9.wireOp",EDGE,"E16")])]});
            var Q7;
            Q7=makeQuery(id+"F10.opExtrude","SWEPT_BODY",BODY,{"disambiguationData":[OSD([sQuery(id+"F9.wireOp",EDGE,"E19.bottom"),sQuery(id+"F9.wireOp",EDGE,"E19.top"),sQuery(id+"F9.wireOp",EDGE,"E19.left"),sQuery(id+"F9.wireOp",EDGE,"E19.right")])]});
            var Q8;
            Q8=makeQuery(id+"F6.opExtrude","SWEPT_BODY",BODY,{"disambiguationData":[OSD([sQuery(id+"F5.wireOp",EDGE,"E5.bottom"),sQuery(id+"F5.wireOp",EDGE,"E5.top"),sQuery(id+"F5.wireOp",EDGE,"E5.left"),sQuery(id+"F5.wireOp",EDGE,"E5.right")])]});
            booleanBodies(context, id + "F11", {"operationType" : BooleanOperationType.SUBTRACTION, "tools" : qUnion([Q0, Q1, Q2, Q3, Q4, Q5, Q6, Q7]), "targets" : qUnion([Q8])});
        }
        {
            var Q0;
            Q0=qCreatedBy(makeId("Top.planeOp"),FACE);
            var sketch = newSketch(context, id + "F12", { "sketchPlane" : qUnion([Q0])});
            skLineSegment(sketch, "E20.bottom", {"start": v(375, 375) * mm, "end": v(-375, 375) * mm});
            skLineSegment(sketch, "E20.top", {"start": v(375, -375) * mm, "end": v(-375, -375) * mm});
            skLineSegment(sketch, "E20.left", {"start": v(375, 375) * mm, "end": v(375, -375) * mm});
            skLineSegment(sketch, "E20.right", {"start": v(-375, 375) * mm, "end": v(-375, -375) * mm});
            skPoint(sketch, "E20.middle", {"position": v(0, 0) * mm});
            skLineSegment(sketch, "E21", {"start": v(0, 0) * mm, "end": v(0, 250) * mm, "construction": true});
            skLineSegment(sketch, "E22.bottom", {"start": v(266.67, 257.5) * mm, "end": v(-266.67, 257.5) * mm, "construction": true});
            skLineSegment(sketch, "E22.top", {"start": v(266.67, 242.5) * mm, "end": v(-266.67, 242.5) * mm, "construction": true});
            skLineSegment(sketch, "E22.left", {"start": v(266.67, 257.5) * mm, "end": v(266.67, 242.5) * mm, "construction": true});
            skLineSegment(sketch, "E22.right", {"start": v(-266.67, 257.5) * mm, "end": v(-266.67, 242.5) * mm, "construction": true});
            skPoint(sketch, "E22.middle", {"position": v(0, 250) * mm});
            skLineSegment(sketch, "E23.0.1.0", {"start": v(266.67, 224.17) * mm, "end": v(-266.67, 224.17) * mm, "construction": true});
            skLineSegment(sketch, "E23.0.1.1", {"start": v(266.67, 209.17) * mm, "end": v(-266.67, 209.17) * mm, "construction": true});
            skLineSegment(sketch, "E23.0.1.2", {"start": v(266.67, 224.17) * mm, "end": v(266.67, 209.17) * mm, "construction": true});
            skLineSegment(sketch, "E23.0.1.3", {"start": v(-266.67, 224.17) * mm, "end": v(-266.67, 209.17) * mm, "construction": true});
            skLineSegment(sketch, "E23.direction1", {"start": v(-266.67, 257.5) * mm, "end": v(-241.67, 257.5) * mm, "construction": true});
            skLineSegment(sketch, "E23.direction2", {"start": v(-266.67, 257.5) * mm, "end": v(-266.67, 224.17) * mm, "construction": true});
            skLineSegment(sketch, "E24.0.0.2", {"start": v(266.67, 190.83) * mm, "end": v(-266.67, 190.83) * mm, "construction": true});
            skLineSegment(sketch, "E24.3.0.2", {"start": v(266.67, 175.83) * mm, "end": v(-266.67, 175.83) * mm, "construction": true});
            skLineSegment(sketch, "E24.6.0.2", {"start": v(266.67, 190.83) * mm, "end": v(266.67, 175.83) * mm, "construction": true});
            skLineSegment(sketch, "E24.9.0.2", {"start": v(-266.67, 190.83) * mm, "end": v(-266.67, 175.83) * mm, "construction": true});
            skLineSegment(sketch, "E24.0.0.3", {"start": v(266.67, 157.5) * mm, "end": v(-266.67, 157.5) * mm, "construction": true});
            skLineSegment(sketch, "E24.3.0.3", {"start": v(266.67, 142.5) * mm, "end": v(-266.67, 142.5) * mm, "construction": true});
            skLineSegment(sketch, "E24.6.0.3", {"start": v(266.67, 157.5) * mm, "end": v(266.67, 142.5) * mm, "construction": true});
            skLineSegment(sketch, "E24.9.0.3", {"start": v(-266.67, 157.5) * mm, "end": v(-266.67, 142.5) * mm, "construction": true});
            skLineSegment(sketch, "E24.0.0.4", {"start": v(266.67, 124.17) * mm, "end": v(-266.67, 124.17) * mm, "construction": true});
            skLineSegment(sketch, "E24.3.0.4", {"start": v(266.67, 109.17) * mm, "end": v(-266.67, 109.17) * mm, "construction": true});
            skLineSegment(sketch, "E24.6.0.4", {"start": v(266.67, 124.17) * mm, "end": v(266.67, 109.17) * mm, "construction": true});
            skLineSegment(sketch, "E24.9.0.4", {"start": v(-266.67, 124.17) * mm, "end": v(-266.67, 109.17) * mm, "construction": true});
            skLineSegment(sketch, "E24.0.0.5", {"start": v(266.67, 90.83) * mm, "end": v(-266.67, 90.83) * mm, "construction": true});
            skLineSegment(sketch, "E24.3.0.5", {"start": v(266.67, 75.83) * mm, "end": v(-266.67, 75.83) * mm, "construction": true});
            skLineSegment(sketch, "E24.6.0.5", {"start": v(266.67, 90.83) * mm, "end": v(266.67, 75.83) * mm, "construction": true});
            skLineSegment(sketch, "E24.9.0.5", {"start": v(-266.67, 90.83) * mm, "end": v(-266.67, 75.83) * mm, "construction": true});
            skLineSegment(sketch, "E24.0.0.6", {"start": v(266.67, 57.5) * mm, "end": v(-266.67, 57.5) * mm, "construction": true});
            skLineSegment(sketch, "E24.3.0.6", {"start": v(266.67, 42.5) * mm, "end": v(-266.67, 42.5) * mm, "construction": true});
            skLineSegment(sketch, "E24.6.0.6", {"start": v(266.67, 57.5) * mm, "end": v(266.67, 42.5) * mm, "construction": true});
            skLineSegment(sketch, "E24.9.0.6", {"start": v(-266.67, 57.5) * mm, "end": v(-266.67, 42.5) * mm, "construction": true});
            skLineSegment(sketch, "E24.0.0.7", {"start": v(266.67, 24.17) * mm, "end": v(-266.67, 24.17) * mm, "construction": true});
            skLineSegment(sketch, "E24.3.0.7", {"start": v(266.67, 9.17) * mm, "end": v(-266.67, 9.17) * mm, "construction": true});
            skLineSegment(sketch, "E24.6.0.7", {"start": v(266.67, 24.17) * mm, "end": v(266.67, 9.17) * mm, "construction": true});
            skLineSegment(sketch, "E24.9.0.7", {"start": v(-266.67, 24.17) * mm, "end": v(-266.67, 9.17) * mm, "construction": true});
            skLineSegment(sketch, "E24.0.0.8", {"start": v(266.67, -9.17) * mm, "end": v(-266.67, -9.17) * mm, "construction": true});
            skLineSegment(sketch, "E24.3.0.8", {"start": v(266.67, -24.17) * mm, "end": v(-266.67, -24.17) * mm, "construction": true});
            skLineSegment(sketch, "E24.6.0.8", {"start": v(266.67, -9.17) * mm, "end": v(266.67, -24.17) * mm, "construction": true});
            skLineSegment(sketch, "E24.9.0.8", {"start": v(-266.67, -9.17) * mm, "end": v(-266.67, -24.17) * mm, "construction": true});
            skLineSegment(sketch, "E24.0.0.9", {"start": v(266.67, -42.5) * mm, "end": v(-266.67, -42.5) * mm, "construction": true});
            skLineSegment(sketch, "E24.3.0.9", {"start": v(266.67, -57.5) * mm, "end": v(-266.67, -57.5) * mm, "construction": true});
            skLineSegment(sketch, "E24.6.0.9", {"start": v(266.67, -42.5) * mm, "end": v(266.67, -57.5) * mm, "construction": true});
            skLineSegment(sketch, "E24.9.0.9", {"start": v(-266.67, -42.5) * mm, "end": v(-266.67, -57.5) * mm, "construction": true});
            skLineSegment(sketch, "E24.0.0.10", {"start": v(266.67, -75.83) * mm, "end": v(-266.67, -75.83) * mm, "construction": true});
            skLineSegment(sketch, "E24.3.0.10", {"start": v(266.67, -90.83) * mm, "end": v(-266.67, -90.83) * mm, "construction": true});
            skLineSegment(sketch, "E24.6.0.10", {"start": v(266.67, -75.83) * mm, "end": v(266.67, -90.83) * mm, "construction": true});
            skLineSegment(sketch, "E24.9.0.10", {"start": v(-266.67, -75.83) * mm, "end": v(-266.67, -90.83) * mm, "construction": true});
            skLineSegment(sketch, "E24.0.0.11", {"start": v(266.67, -109.17) * mm, "end": v(-266.67, -109.17) * mm, "construction": true});
            skLineSegment(sketch, "E24.3.0.11", {"start": v(266.67, -124.17) * mm, "end": v(-266.67, -124.17) * mm, "construction": true});
            skLineSegment(sketch, "E24.6.0.11", {"start": v(266.67, -109.17) * mm, "end": v(266.67, -124.17) * mm, "construction": true});
            skLineSegment(sketch, "E24.9.0.11", {"start": v(-266.67, -109.17) * mm, "end": v(-266.67, -124.17) * mm, "construction": true});
            skLineSegment(sketch, "E24.0.0.12", {"start": v(266.67, -142.5) * mm, "end": v(-266.67, -142.5) * mm, "construction": true});
            skLineSegment(sketch, "E24.3.0.12", {"start": v(266.67, -157.5) * mm, "end": v(-266.67, -157.5) * mm, "construction": true});
            skLineSegment(sketch, "E24.6.0.12", {"start": v(266.67, -142.5) * mm, "end": v(266.67, -157.5) * mm, "construction": true});
            skLineSegment(sketch, "E24.9.0.12", {"start": v(-266.67, -142.5) * mm, "end": v(-266.67, -157.5) * mm, "construction": true});
            skLineSegment(sketch, "E24.0.0.13", {"start": v(266.67, -175.83) * mm, "end": v(-266.67, -175.83) * mm, "construction": true});
            skLineSegment(sketch, "E24.3.0.13", {"start": v(266.67, -190.83) * mm, "end": v(-266.67, -190.83) * mm, "construction": true});
            skLineSegment(sketch, "E24.6.0.13", {"start": v(266.67, -175.83) * mm, "end": v(266.67, -190.83) * mm, "construction": true});
            skLineSegment(sketch, "E24.9.0.13", {"start": v(-266.67, -175.83) * mm, "end": v(-266.67, -190.83) * mm, "construction": true});
            skLineSegment(sketch, "E24.0.0.14", {"start": v(266.67, -209.17) * mm, "end": v(-266.67, -209.17) * mm, "construction": true});
            skLineSegment(sketch, "E24.3.0.14", {"start": v(266.67, -224.17) * mm, "end": v(-266.67, -224.17) * mm, "construction": true});
            skLineSegment(sketch, "E24.6.0.14", {"start": v(266.67, -209.17) * mm, "end": v(266.67, -224.17) * mm, "construction": true});
            skLineSegment(sketch, "E24.9.0.14", {"start": v(-266.67, -209.17) * mm, "end": v(-266.67, -224.17) * mm, "construction": true});
            skLineSegment(sketch, "E24.0.0.15", {"start": v(266.67, -242.5) * mm, "end": v(-266.67, -242.5) * mm, "construction": true});
            skLineSegment(sketch, "E24.3.0.15", {"start": v(266.67, -257.5) * mm, "end": v(-266.67, -257.5) * mm, "construction": true});
            skLineSegment(sketch, "E24.6.0.15", {"start": v(266.67, -242.5) * mm, "end": v(266.67, -257.5) * mm, "construction": true});
            skLineSegment(sketch, "E24.9.0.15", {"start": v(-266.67, -242.5) * mm, "end": v(-266.67, -257.5) * mm, "construction": true});
            skSolve(sketch);
        }
        {
            var Q0;
            Q0 = qSketchRegion(id + "F12", true);
            extrude(context, id + "F13", {"entities" : qUnion([Q0]), "depth" : getVariable(context, 'D3'), "offsetDistance" : 25 * mm});
        }
        {
            var Q0;
            Q0=qCreatedBy(makeId("Top.planeOp"),FACE);
            var sketch = newSketch(context, id + "F14", { "sketchPlane" : qUnion([Q0])});
            skLineSegment(sketch, "E25.bottom", {"start": v(375, 375) * mm, "end": v(-375, 375) * mm});
            skLineSegment(sketch, "E25.top", {"start": v(375, -375) * mm, "end": v(-375, -375) * mm});
            skLineSegment(sketch, "E25.left", {"start": v(375, 375) * mm, "end": v(375, -375) * mm});
            skLineSegment(sketch, "E25.right", {"start": v(-375, 375) * mm, "end": v(-375, -375) * mm});
            skPoint(sketch, "E25.middle", {"position": v(0, 0) * mm});
            skLineSegment(sketch, "E26.bottom", {"start": v(350, 350) * mm, "end": v(-350, 350) * mm});
            skLineSegment(sketch, "E26.top", {"start": v(350, -350) * mm, "end": v(-350, -350) * mm});
            skLineSegment(sketch, "E26.left", {"start": v(350, 350) * mm, "end": v(350, -350) * mm});
            skLineSegment(sketch, "E26.right", {"start": v(-350, 350) * mm, "end": v(-350, -350) * mm});
            skSolve(sketch);
        }
        {
            var Q0;
            Q0 = qSketchRegion(id + "F14", true);
            extrude(context, id + "F15", {"entities" : qUnion([Q0]), "depth" : getVariable(context, 'D3'), "offsetDistance" : 25 * mm});
        }
        {
            var Q0;
            Q0=makeQuery(id+"F6.opExtrude","CAP_FACE",FACE,{"disambiguationData":[OSD([sQuery(id+"F5.wireOp",EDGE,"E5.bottom"),sQuery(id+"F5.wireOp",EDGE,"E5.top"),sQuery(id+"F5.wireOp",EDGE,"E5.left"),sQuery(id+"F5.wireOp",EDGE,"E5.right")])],"isStart":true});
            var sketch = newSketch(context, id + "F16", { "sketchPlane" : qUnion([Q0])});
            skLineSegment(sketch, "E27.bottom", {"start": v(-266.67, -262.5) * mm, "end": v(-296.67, -262.5) * mm});
            skLineSegment(sketch, "E27.top", {"start": v(-266.67, -237.5) * mm, "end": v(-296.67, -237.5) * mm});
            skLineSegment(sketch, "E27.left", {"start": v(-266.67, -262.5) * mm, "end": v(-266.67, -237.5) * mm});
            skLineSegment(sketch, "E27.right", {"start": v(-296.67, -262.5) * mm, "end": v(-296.67, -237.5) * mm});
            skPoint(sketch, "E27.middle", {"position": v(-281.67, -250) * mm});
            skLineSegment(sketch, "E28.0.1.0", {"start": v(-266.67, -204.17) * mm, "end": v(-296.67, -204.17) * mm});
            skLineSegment(sketch, "E28.0.1.1", {"start": v(-266.67, -229.17) * mm, "end": v(-266.67, -204.17) * mm});
            skLineSegment(sketch, "E28.0.1.2", {"start": v(-266.67, -229.17) * mm, "end": v(-296.67, -229.17) * mm});
            skLineSegment(sketch, "E28.0.1.3", {"start": v(-296.67, -229.17) * mm, "end": v(-296.67, -204.17) * mm});
            skLineSegment(sketch, "E28.0.2.0", {"start": v(-266.67, -170.83) * mm, "end": v(-296.67, -170.83) * mm});
            skLineSegment(sketch, "E28.0.2.1", {"start": v(-266.67, -195.83) * mm, "end": v(-266.67, -170.83) * mm});
            skLineSegment(sketch, "E28.0.2.2", {"start": v(-266.67, -195.83) * mm, "end": v(-296.67, -195.83) * mm});
            skLineSegment(sketch, "E28.0.2.3", {"start": v(-296.67, -195.83) * mm, "end": v(-296.67, -170.83) * mm});
            skLineSegment(sketch, "E28.0.3.0", {"start": v(-266.67, -137.5) * mm, "end": v(-296.67, -137.5) * mm});
            skLineSegment(sketch, "E28.0.3.1", {"start": v(-266.67, -162.5) * mm, "end": v(-266.67, -137.5) * mm});
            skLineSegment(sketch, "E28.0.3.2", {"start": v(-266.67, -162.5) * mm, "end": v(-296.67, -162.5) * mm});
            skLineSegment(sketch, "E28.0.3.3", {"start": v(-296.67, -162.5) * mm, "end": v(-296.67, -137.5) * mm});
            skLineSegment(sketch, "E28.0.4.0", {"start": v(-266.67, -104.17) * mm, "end": v(-296.67, -104.17) * mm});
            skLineSegment(sketch, "E28.0.4.1", {"start": v(-266.67, -129.17) * mm, "end": v(-266.67, -104.17) * mm});
            skLineSegment(sketch, "E28.0.4.2", {"start": v(-266.67, -129.17) * mm, "end": v(-296.67, -129.17) * mm});
            skLineSegment(sketch, "E28.0.4.3", {"start": v(-296.67, -129.17) * mm, "end": v(-296.67, -104.17) * mm});
            skLineSegment(sketch, "E28.0.5.0", {"start": v(-266.67, -70.83) * mm, "end": v(-296.67, -70.83) * mm});
            skLineSegment(sketch, "E28.0.5.1", {"start": v(-266.67, -95.83) * mm, "end": v(-266.67, -70.83) * mm});
            skLineSegment(sketch, "E28.0.5.2", {"start": v(-266.67, -95.83) * mm, "end": v(-296.67, -95.83) * mm});
            skLineSegment(sketch, "E28.0.5.3", {"start": v(-296.67, -95.83) * mm, "end": v(-296.67, -70.83) * mm});
            skLineSegment(sketch, "E28.0.6.0", {"start": v(-266.67, -37.5) * mm, "end": v(-296.67, -37.5) * mm});
            skLineSegment(sketch, "E28.0.6.1", {"start": v(-266.67, -62.5) * mm, "end": v(-266.67, -37.5) * mm});
            skLineSegment(sketch, "E28.0.6.2", {"start": v(-266.67, -62.5) * mm, "end": v(-296.67, -62.5) * mm});
            skLineSegment(sketch, "E28.0.6.3", {"start": v(-296.67, -62.5) * mm, "end": v(-296.67, -37.5) * mm});
            skLineSegment(sketch, "E28.0.7.0", {"start": v(-266.67, -4.17) * mm, "end": v(-296.67, -4.17) * mm});
            skLineSegment(sketch, "E28.0.7.1", {"start": v(-266.67, -29.17) * mm, "end": v(-266.67, -4.17) * mm});
            skLineSegment(sketch, "E28.0.7.2", {"start": v(-266.67, -29.17) * mm, "end": v(-296.67, -29.17) * mm});
            skLineSegment(sketch, "E28.0.7.3", {"start": v(-296.67, -29.17) * mm, "end": v(-296.67, -4.17) * mm});
            skLineSegment(sketch, "E28.0.8.0", {"start": v(-266.67, 29.17) * mm, "end": v(-296.67, 29.17) * mm});
            skLineSegment(sketch, "E28.0.8.1", {"start": v(-266.67, 4.17) * mm, "end": v(-266.67, 29.17) * mm});
            skLineSegment(sketch, "E28.0.8.2", {"start": v(-266.67, 4.17) * mm, "end": v(-296.67, 4.17) * mm});
            skLineSegment(sketch, "E28.0.8.3", {"start": v(-296.67, 4.17) * mm, "end": v(-296.67, 29.17) * mm});
            skLineSegment(sketch, "E28.0.9.0", {"start": v(-266.67, 62.5) * mm, "end": v(-296.67, 62.5) * mm});
            skLineSegment(sketch, "E28.0.9.1", {"start": v(-266.67, 37.5) * mm, "end": v(-266.67, 62.5) * mm});
            skLineSegment(sketch, "E28.0.9.2", {"start": v(-266.67, 37.5) * mm, "end": v(-296.67, 37.5) * mm});
            skLineSegment(sketch, "E28.0.9.3", {"start": v(-296.67, 37.5) * mm, "end": v(-296.67, 62.5) * mm});
            skLineSegment(sketch, "E28.0.10.0", {"start": v(-266.67, 95.83) * mm, "end": v(-296.67, 95.83) * mm});
            skLineSegment(sketch, "E28.0.10.1", {"start": v(-266.67, 70.83) * mm, "end": v(-266.67, 95.83) * mm});
            skLineSegment(sketch, "E28.0.10.2", {"start": v(-266.67, 70.83) * mm, "end": v(-296.67, 70.83) * mm});
            skLineSegment(sketch, "E28.0.10.3", {"start": v(-296.67, 70.83) * mm, "end": v(-296.67, 95.83) * mm});
            skLineSegment(sketch, "E28.0.11.0", {"start": v(-266.67, 129.17) * mm, "end": v(-296.67, 129.17) * mm});
            skLineSegment(sketch, "E28.0.11.1", {"start": v(-266.67, 104.17) * mm, "end": v(-266.67, 129.17) * mm});
            skLineSegment(sketch, "E28.0.11.2", {"start": v(-266.67, 104.17) * mm, "end": v(-296.67, 104.17) * mm});
            skLineSegment(sketch, "E28.0.11.3", {"start": v(-296.67, 104.17) * mm, "end": v(-296.67, 129.17) * mm});
            skLineSegment(sketch, "E28.0.12.0", {"start": v(-266.67, 162.5) * mm, "end": v(-296.67, 162.5) * mm});
            skLineSegment(sketch, "E28.0.12.1", {"start": v(-266.67, 137.5) * mm, "end": v(-266.67, 162.5) * mm});
            skLineSegment(sketch, "E28.0.12.2", {"start": v(-266.67, 137.5) * mm, "end": v(-296.67, 137.5) * mm});
            skLineSegment(sketch, "E28.0.12.3", {"start": v(-296.67, 137.5) * mm, "end": v(-296.67, 162.5) * mm});
            skLineSegment(sketch, "E28.0.13.0", {"start": v(-266.67, 195.83) * mm, "end": v(-296.67, 195.83) * mm});
            skLineSegment(sketch, "E28.0.13.1", {"start": v(-266.67, 170.83) * mm, "end": v(-266.67, 195.83) * mm});
            skLineSegment(sketch, "E28.0.13.2", {"start": v(-266.67, 170.83) * mm, "end": v(-296.67, 170.83) * mm});
            skLineSegment(sketch, "E28.0.13.3", {"start": v(-296.67, 170.83) * mm, "end": v(-296.67, 195.83) * mm});
            skLineSegment(sketch, "E28.0.14.0", {"start": v(-266.67, 229.17) * mm, "end": v(-296.67, 229.17) * mm});
            skLineSegment(sketch, "E28.0.14.1", {"start": v(-266.67, 204.17) * mm, "end": v(-266.67, 229.17) * mm});
            skLineSegment(sketch, "E28.0.14.2", {"start": v(-266.67, 204.17) * mm, "end": v(-296.67, 204.17) * mm});
            skLineSegment(sketch, "E28.0.14.3", {"start": v(-296.67, 204.17) * mm, "end": v(-296.67, 229.17) * mm});
            skLineSegment(sketch, "E28.0.15.0", {"start": v(-266.67, 262.5) * mm, "end": v(-296.67, 262.5) * mm});
            skLineSegment(sketch, "E28.0.15.1", {"start": v(-266.67, 237.5) * mm, "end": v(-266.67, 262.5) * mm});
            skLineSegment(sketch, "E28.0.15.2", {"start": v(-266.67, 237.5) * mm, "end": v(-296.67, 237.5) * mm});
            skLineSegment(sketch, "E28.0.15.3", {"start": v(-296.67, 237.5) * mm, "end": v(-296.67, 262.5) * mm});
            skLineSegment(sketch, "E28.1.0.0", {"start": v(296.67, -237.5) * mm, "end": v(266.67, -237.5) * mm});
            skLineSegment(sketch, "E28.1.0.1", {"start": v(296.67, -262.5) * mm, "end": v(296.67, -237.5) * mm});
            skLineSegment(sketch, "E28.1.0.2", {"start": v(296.67, -262.5) * mm, "end": v(266.67, -262.5) * mm});
            skLineSegment(sketch, "E28.1.0.3", {"start": v(266.67, -262.5) * mm, "end": v(266.67, -237.5) * mm});
            skLineSegment(sketch, "E28.1.1.0", {"start": v(296.67, -204.17) * mm, "end": v(266.67, -204.17) * mm});
            skLineSegment(sketch, "E28.1.1.1", {"start": v(296.67, -229.17) * mm, "end": v(296.67, -204.17) * mm});
            skLineSegment(sketch, "E28.1.1.2", {"start": v(296.67, -229.17) * mm, "end": v(266.67, -229.17) * mm});
            skLineSegment(sketch, "E28.1.1.3", {"start": v(266.67, -229.17) * mm, "end": v(266.67, -204.17) * mm});
            skLineSegment(sketch, "E28.1.2.0", {"start": v(296.67, -170.83) * mm, "end": v(266.67, -170.83) * mm});
            skLineSegment(sketch, "E28.1.2.1", {"start": v(296.67, -195.83) * mm, "end": v(296.67, -170.83) * mm});
            skLineSegment(sketch, "E28.1.2.2", {"start": v(296.67, -195.83) * mm, "end": v(266.67, -195.83) * mm});
            skLineSegment(sketch, "E28.1.2.3", {"start": v(266.67, -195.83) * mm, "end": v(266.67, -170.83) * mm});
            skLineSegment(sketch, "E28.1.3.0", {"start": v(296.67, -137.5) * mm, "end": v(266.67, -137.5) * mm});
            skLineSegment(sketch, "E28.1.3.1", {"start": v(296.67, -162.5) * mm, "end": v(296.67, -137.5) * mm});
            skLineSegment(sketch, "E28.1.3.2", {"start": v(296.67, -162.5) * mm, "end": v(266.67, -162.5) * mm});
            skLineSegment(sketch, "E28.1.3.3", {"start": v(266.67, -162.5) * mm, "end": v(266.67, -137.5) * mm});
            skLineSegment(sketch, "E28.1.4.0", {"start": v(296.67, -104.17) * mm, "end": v(266.67, -104.17) * mm});
            skLineSegment(sketch, "E28.1.4.1", {"start": v(296.67, -129.17) * mm, "end": v(296.67, -104.17) * mm});
            skLineSegment(sketch, "E28.1.4.2", {"start": v(296.67, -129.17) * mm, "end": v(266.67, -129.17) * mm});
            skLineSegment(sketch, "E28.1.4.3", {"start": v(266.67, -129.17) * mm, "end": v(266.67, -104.17) * mm});
            skLineSegment(sketch, "E28.1.5.0", {"start": v(296.67, -70.83) * mm, "end": v(266.67, -70.83) * mm});
            skLineSegment(sketch, "E28.1.5.1", {"start": v(296.67, -95.83) * mm, "end": v(296.67, -70.83) * mm});
            skLineSegment(sketch, "E28.1.5.2", {"start": v(296.67, -95.83) * mm, "end": v(266.67, -95.83) * mm});
            skLineSegment(sketch, "E28.1.5.3", {"start": v(266.67, -95.83) * mm, "end": v(266.67, -70.83) * mm});
            skLineSegment(sketch, "E28.1.6.0", {"start": v(296.67, -37.5) * mm, "end": v(266.67, -37.5) * mm});
            skLineSegment(sketch, "E28.1.6.1", {"start": v(296.67, -62.5) * mm, "end": v(296.67, -37.5) * mm});
            skLineSegment(sketch, "E28.1.6.2", {"start": v(296.67, -62.5) * mm, "end": v(266.67, -62.5) * mm});
            skLineSegment(sketch, "E28.1.6.3", {"start": v(266.67, -62.5) * mm, "end": v(266.67, -37.5) * mm});
            skLineSegment(sketch, "E28.1.7.0", {"start": v(296.67, -4.17) * mm, "end": v(266.67, -4.17) * mm});
            skLineSegment(sketch, "E28.1.7.1", {"start": v(296.67, -29.17) * mm, "end": v(296.67, -4.17) * mm});
            skLineSegment(sketch, "E28.1.7.2", {"start": v(296.67, -29.17) * mm, "end": v(266.67, -29.17) * mm});
            skLineSegment(sketch, "E28.1.7.3", {"start": v(266.67, -29.17) * mm, "end": v(266.67, -4.17) * mm});
            skLineSegment(sketch, "E28.1.8.0", {"start": v(296.67, 29.17) * mm, "end": v(266.67, 29.17) * mm});
            skLineSegment(sketch, "E28.1.8.1", {"start": v(296.67, 4.17) * mm, "end": v(296.67, 29.17) * mm});
            skLineSegment(sketch, "E28.1.8.2", {"start": v(296.67, 4.17) * mm, "end": v(266.67, 4.17) * mm});
            skLineSegment(sketch, "E28.1.8.3", {"start": v(266.67, 4.17) * mm, "end": v(266.67, 29.17) * mm});
            skLineSegment(sketch, "E28.1.9.0", {"start": v(296.67, 62.5) * mm, "end": v(266.67, 62.5) * mm});
            skLineSegment(sketch, "E28.1.9.1", {"start": v(296.67, 37.5) * mm, "end": v(296.67, 62.5) * mm});
            skLineSegment(sketch, "E28.1.9.2", {"start": v(296.67, 37.5) * mm, "end": v(266.67, 37.5) * mm});
            skLineSegment(sketch, "E28.1.9.3", {"start": v(266.67, 37.5) * mm, "end": v(266.67, 62.5) * mm});
            skLineSegment(sketch, "E28.1.10.0", {"start": v(296.67, 95.83) * mm, "end": v(266.67, 95.83) * mm});
            skLineSegment(sketch, "E28.1.10.1", {"start": v(296.67, 70.83) * mm, "end": v(296.67, 95.83) * mm});
            skLineSegment(sketch, "E28.1.10.2", {"start": v(296.67, 70.83) * mm, "end": v(266.67, 70.83) * mm});
            skLineSegment(sketch, "E28.1.10.3", {"start": v(266.67, 70.83) * mm, "end": v(266.67, 95.83) * mm});
            skLineSegment(sketch, "E28.1.11.0", {"start": v(296.67, 129.17) * mm, "end": v(266.67, 129.17) * mm});
            skLineSegment(sketch, "E28.1.11.1", {"start": v(296.67, 104.17) * mm, "end": v(296.67, 129.17) * mm});
            skLineSegment(sketch, "E28.1.11.2", {"start": v(296.67, 104.17) * mm, "end": v(266.67, 104.17) * mm});
            skLineSegment(sketch, "E28.1.11.3", {"start": v(266.67, 104.17) * mm, "end": v(266.67, 129.17) * mm});
            skLineSegment(sketch, "E28.1.12.0", {"start": v(296.67, 162.5) * mm, "end": v(266.67, 162.5) * mm});
            skLineSegment(sketch, "E28.1.12.1", {"start": v(296.67, 137.5) * mm, "end": v(296.67, 162.5) * mm});
            skLineSegment(sketch, "E28.1.12.2", {"start": v(296.67, 137.5) * mm, "end": v(266.67, 137.5) * mm});
            skLineSegment(sketch, "E28.1.12.3", {"start": v(266.67, 137.5) * mm, "end": v(266.67, 162.5) * mm});
            skLineSegment(sketch, "E28.1.13.0", {"start": v(296.67, 195.83) * mm, "end": v(266.67, 195.83) * mm});
            skLineSegment(sketch, "E28.1.13.1", {"start": v(296.67, 170.83) * mm, "end": v(296.67, 195.83) * mm});
            skLineSegment(sketch, "E28.1.13.2", {"start": v(296.67, 170.83) * mm, "end": v(266.67, 170.83) * mm});
            skLineSegment(sketch, "E28.1.13.3", {"start": v(266.67, 170.83) * mm, "end": v(266.67, 195.83) * mm});
            skLineSegment(sketch, "E28.1.14.0", {"start": v(296.67, 229.17) * mm, "end": v(266.67, 229.17) * mm});
            skLineSegment(sketch, "E28.1.14.1", {"start": v(296.67, 204.17) * mm, "end": v(296.67, 229.17) * mm});
            skLineSegment(sketch, "E28.1.14.2", {"start": v(296.67, 204.17) * mm, "end": v(266.67, 204.17) * mm});
            skLineSegment(sketch, "E28.1.14.3", {"start": v(266.67, 204.17) * mm, "end": v(266.67, 229.17) * mm});
            skLineSegment(sketch, "E28.1.15.0", {"start": v(296.67, 262.5) * mm, "end": v(266.67, 262.5) * mm});
            skLineSegment(sketch, "E28.1.15.1", {"start": v(296.67, 237.5) * mm, "end": v(296.67, 262.5) * mm});
            skLineSegment(sketch, "E28.1.15.2", {"start": v(296.67, 237.5) * mm, "end": v(266.67, 237.5) * mm});
            skLineSegment(sketch, "E28.1.15.3", {"start": v(266.67, 237.5) * mm, "end": v(266.67, 262.5) * mm});
            skLineSegment(sketch, "E28.direction1", {"start": v(-296.67, -237.5) * mm, "end": v(266.67, -237.5) * mm, "construction": true});
            skLineSegment(sketch, "E28.direction2", {"start": v(-296.67, -237.5) * mm, "end": v(-296.67, -204.17) * mm, "construction": true});
            skSolve(sketch);
        }
        {
            var Q0;
            Q0 = qSketchRegion(id + "F16", true);
            var Q1;
            Q1 = qSketchRegion(id + "F16", true);
            var Q2;
            Q2 = qSketchRegion(id + "F16", true);
            var Q3;
            Q3 = qSketchRegion(id + "F16", true);
            var Q4;
            Q4 = qSketchRegion(id + "F16", true);
            var Q5;
            Q5 = qSketchRegion(id + "F16", true);
            var Q6;
            Q6 = qSketchRegion(id + "F16", true);
            var Q7;
            Q7 = qSketchRegion(id + "F16", true);
            var Q8;
            Q8 = qSketchRegion(id + "F16", true);
            var Q9;
            Q9 = qSketchRegion(id + "F16", true);
            var Q10;
            Q10 = qSketchRegion(id + "F16", true);
            var Q11;
            Q11 = qSketchRegion(id + "F16", true);
            extrude(context, id + "F17", {"entities" : qUnion([Q0, Q1, Q2, Q3, Q4, Q5, Q6, Q7, Q8, Q9, Q10, Q11]), "endBound" : BoundingType.SYMMETRIC, "oppositeDirection" : true, "depth" : 100 * mm, "offsetDistance" : 25 * mm});
        }
        {
            var Q0;
            Q0=makeQuery(id+"F17.opExtrude","SWEPT_BODY",BODY,{"disambiguationData":[OSD([sQuery(id+"F16.wireOp",EDGE,"E27.bottom"),sQuery(id+"F16.wireOp",EDGE,"E27.top"),sQuery(id+"F16.wireOp",EDGE,"E27.left"),sQuery(id+"F16.wireOp",EDGE,"E27.right")])]});
            var Q1;
            Q1=makeQuery(id+"F17.opExtrude","SWEPT_BODY",BODY,{"disambiguationData":[OSD([sQuery(id+"F16.wireOp",EDGE,"E28.0.3.0"),sQuery(id+"F16.wireOp",EDGE,"E28.0.3.1"),sQuery(id+"F16.wireOp",EDGE,"E28.0.3.2"),sQuery(id+"F16.wireOp",EDGE,"E28.0.3.3")])]});
            var Q2;
            Q2=makeQuery(id+"F17.opExtrude","SWEPT_BODY",BODY,{"disambiguationData":[OSD([sQuery(id+"F16.wireOp",EDGE,"E28.0.4.0"),sQuery(id+"F16.wireOp",EDGE,"E28.0.4.1"),sQuery(id+"F16.wireOp",EDGE,"E28.0.4.2"),sQuery(id+"F16.wireOp",EDGE,"E28.0.4.3")])]});
            var Q3;
            Q3=makeQuery(id+"F17.opExtrude","SWEPT_BODY",BODY,{"disambiguationData":[OSD([sQuery(id+"F16.wireOp",EDGE,"E28.0.5.0"),sQuery(id+"F16.wireOp",EDGE,"E28.0.5.1"),sQuery(id+"F16.wireOp",EDGE,"E28.0.5.2"),sQuery(id+"F16.wireOp",EDGE,"E28.0.5.3")])]});
            var Q4;
            Q4=makeQuery(id+"F17.opExtrude","SWEPT_BODY",BODY,{"disambiguationData":[OSD([sQuery(id+"F16.wireOp",EDGE,"E28.0.6.0"),sQuery(id+"F16.wireOp",EDGE,"E28.0.6.1"),sQuery(id+"F16.wireOp",EDGE,"E28.0.6.2"),sQuery(id+"F16.wireOp",EDGE,"E28.0.6.3")])]});
            var Q5;
            Q5=makeQuery(id+"F17.opExtrude","SWEPT_BODY",BODY,{"disambiguationData":[OSD([sQuery(id+"F16.wireOp",EDGE,"E28.0.8.0"),sQuery(id+"F16.wireOp",EDGE,"E28.0.8.1"),sQuery(id+"F16.wireOp",EDGE,"E28.0.8.2"),sQuery(id+"F16.wireOp",EDGE,"E28.0.8.3")])]});
            var Q6;
            Q6=makeQuery(id+"F17.opExtrude","SWEPT_BODY",BODY,{"disambiguationData":[OSD([sQuery(id+"F16.wireOp",EDGE,"E28.0.11.0"),sQuery(id+"F16.wireOp",EDGE,"E28.0.11.1"),sQuery(id+"F16.wireOp",EDGE,"E28.0.11.2"),sQuery(id+"F16.wireOp",EDGE,"E28.0.11.3")])]});
            var Q7;
            Q7=makeQuery(id+"F17.opExtrude","SWEPT_BODY",BODY,{"disambiguationData":[OSD([sQuery(id+"F16.wireOp",EDGE,"E28.0.9.0"),sQuery(id+"F16.wireOp",EDGE,"E28.0.9.1"),sQuery(id+"F16.wireOp",EDGE,"E28.0.9.2"),sQuery(id+"F16.wireOp",EDGE,"E28.0.9.3")])]});
            var Q8;
            Q8=makeQuery(id+"F17.opExtrude","SWEPT_BODY",BODY,{"disambiguationData":[OSD([sQuery(id+"F16.wireOp",EDGE,"E28.0.12.0"),sQuery(id+"F16.wireOp",EDGE,"E28.0.12.1"),sQuery(id+"F16.wireOp",EDGE,"E28.0.12.2"),sQuery(id+"F16.wireOp",EDGE,"E28.0.12.3")])]});
            var Q9;
            Q9=makeQuery(id+"F17.opExtrude","SWEPT_BODY",BODY,{"disambiguationData":[OSD([sQuery(id+"F16.wireOp",EDGE,"E28.0.1.0"),sQuery(id+"F16.wireOp",EDGE,"E28.0.1.1"),sQuery(id+"F16.wireOp",EDGE,"E28.0.1.2"),sQuery(id+"F16.wireOp",EDGE,"E28.0.1.3")])]});
            var Q10;
            Q10=makeQuery(id+"F17.opExtrude","SWEPT_BODY",BODY,{"disambiguationData":[OSD([sQuery(id+"F16.wireOp",EDGE,"E28.0.14.0"),sQuery(id+"F16.wireOp",EDGE,"E28.0.14.1"),sQuery(id+"F16.wireOp",EDGE,"E28.0.14.2"),sQuery(id+"F16.wireOp",EDGE,"E28.0.14.3")])]});
            var Q11;
            Q11=makeQuery(id+"F17.opExtrude","SWEPT_BODY",BODY,{"disambiguationData":[OSD([sQuery(id+"F16.wireOp",EDGE,"E28.0.10.0"),sQuery(id+"F16.wireOp",EDGE,"E28.0.10.1"),sQuery(id+"F16.wireOp",EDGE,"E28.0.10.2"),sQuery(id+"F16.wireOp",EDGE,"E28.0.10.3")])]});
            var Q12;
            Q12=makeQuery(id+"F17.opExtrude","SWEPT_BODY",BODY,{"disambiguationData":[OSD([sQuery(id+"F16.wireOp",EDGE,"E28.0.7.0"),sQuery(id+"F16.wireOp",EDGE,"E28.0.7.1"),sQuery(id+"F16.wireOp",EDGE,"E28.0.7.2"),sQuery(id+"F16.wireOp",EDGE,"E28.0.7.3")])]});
            var Q13;
            Q13=makeQuery(id+"F17.opExtrude","SWEPT_BODY",BODY,{"disambiguationData":[OSD([sQuery(id+"F16.wireOp",EDGE,"E28.0.2.0"),sQuery(id+"F16.wireOp",EDGE,"E28.0.2.1"),sQuery(id+"F16.wireOp",EDGE,"E28.0.2.2"),sQuery(id+"F16.wireOp",EDGE,"E28.0.2.3")])]});
            var Q14;
            Q14=makeQuery(id+"F17.opExtrude","SWEPT_BODY",BODY,{"disambiguationData":[OSD([sQuery(id+"F16.wireOp",EDGE,"E28.0.13.0"),sQuery(id+"F16.wireOp",EDGE,"E28.0.13.1"),sQuery(id+"F16.wireOp",EDGE,"E28.0.13.2"),sQuery(id+"F16.wireOp",EDGE,"E28.0.13.3")])]});
            var Q15;
            Q15=makeQuery(id+"F17.opExtrude","SWEPT_BODY",BODY,{"disambiguationData":[OSD([sQuery(id+"F16.wireOp",EDGE,"E28.0.15.0"),sQuery(id+"F16.wireOp",EDGE,"E28.0.15.1"),sQuery(id+"F16.wireOp",EDGE,"E28.0.15.2"),sQuery(id+"F16.wireOp",EDGE,"E28.0.15.3")])]});
            var Q16;
            Q16=makeQuery(id+"F17.opExtrude","SWEPT_BODY",BODY,{"disambiguationData":[OSD([sQuery(id+"F16.wireOp",EDGE,"E28.1.9.0"),sQuery(id+"F16.wireOp",EDGE,"E28.1.9.1"),sQuery(id+"F16.wireOp",EDGE,"E28.1.9.2"),sQuery(id+"F16.wireOp",EDGE,"E28.1.9.3")])]});
            var Q17;
            Q17=makeQuery(id+"F17.opExtrude","SWEPT_BODY",BODY,{"disambiguationData":[OSD([sQuery(id+"F16.wireOp",EDGE,"E28.1.1.0"),sQuery(id+"F16.wireOp",EDGE,"E28.1.1.1"),sQuery(id+"F16.wireOp",EDGE,"E28.1.1.2"),sQuery(id+"F16.wireOp",EDGE,"E28.1.1.3")])]});
            var Q18;
            Q18=makeQuery(id+"F17.opExtrude","SWEPT_BODY",BODY,{"disambiguationData":[OSD([sQuery(id+"F16.wireOp",EDGE,"E28.1.11.0"),sQuery(id+"F16.wireOp",EDGE,"E28.1.11.1"),sQuery(id+"F16.wireOp",EDGE,"E28.1.11.2"),sQuery(id+"F16.wireOp",EDGE,"E28.1.11.3")])]});
            var Q19;
            Q19=makeQuery(id+"F17.opExtrude","SWEPT_BODY",BODY,{"disambiguationData":[OSD([sQuery(id+"F16.wireOp",EDGE,"E28.1.12.0"),sQuery(id+"F16.wireOp",EDGE,"E28.1.12.1"),sQuery(id+"F16.wireOp",EDGE,"E28.1.12.2"),sQuery(id+"F16.wireOp",EDGE,"E28.1.12.3")])]});
            var Q20;
            Q20=makeQuery(id+"F17.opExtrude","SWEPT_BODY",BODY,{"disambiguationData":[OSD([sQuery(id+"F16.wireOp",EDGE,"E28.1.14.0"),sQuery(id+"F16.wireOp",EDGE,"E28.1.14.1"),sQuery(id+"F16.wireOp",EDGE,"E28.1.14.2"),sQuery(id+"F16.wireOp",EDGE,"E28.1.14.3")])]});
            var Q21;
            Q21=makeQuery(id+"F17.opExtrude","SWEPT_BODY",BODY,{"disambiguationData":[OSD([sQuery(id+"F16.wireOp",EDGE,"E28.1.13.0"),sQuery(id+"F16.wireOp",EDGE,"E28.1.13.1"),sQuery(id+"F16.wireOp",EDGE,"E28.1.13.2"),sQuery(id+"F16.wireOp",EDGE,"E28.1.13.3")])]});
            var Q22;
            Q22=makeQuery(id+"F17.opExtrude","SWEPT_BODY",BODY,{"disambiguationData":[OSD([sQuery(id+"F16.wireOp",EDGE,"E28.1.2.0"),sQuery(id+"F16.wireOp",EDGE,"E28.1.2.1"),sQuery(id+"F16.wireOp",EDGE,"E28.1.2.2"),sQuery(id+"F16.wireOp",EDGE,"E28.1.2.3")])]});
            var Q23;
            Q23=makeQuery(id+"F17.opExtrude","SWEPT_BODY",BODY,{"disambiguationData":[OSD([sQuery(id+"F16.wireOp",EDGE,"E28.1.10.0"),sQuery(id+"F16.wireOp",EDGE,"E28.1.10.1"),sQuery(id+"F16.wireOp",EDGE,"E28.1.10.2"),sQuery(id+"F16.wireOp",EDGE,"E28.1.10.3")])]});
            var Q24;
            Q24=makeQuery(id+"F17.opExtrude","SWEPT_BODY",BODY,{"disambiguationData":[OSD([sQuery(id+"F16.wireOp",EDGE,"E28.1.15.0"),sQuery(id+"F16.wireOp",EDGE,"E28.1.15.1"),sQuery(id+"F16.wireOp",EDGE,"E28.1.15.2"),sQuery(id+"F16.wireOp",EDGE,"E28.1.15.3")])]});
            var Q25;
            Q25=makeQuery(id+"F17.opExtrude","SWEPT_BODY",BODY,{"disambiguationData":[OSD([sQuery(id+"F16.wireOp",EDGE,"E28.1.6.0"),sQuery(id+"F16.wireOp",EDGE,"E28.1.6.1"),sQuery(id+"F16.wireOp",EDGE,"E28.1.6.2"),sQuery(id+"F16.wireOp",EDGE,"E28.1.6.3")])]});
            var Q26;
            Q26=makeQuery(id+"F17.opExtrude","SWEPT_BODY",BODY,{"disambiguationData":[OSD([sQuery(id+"F16.wireOp",EDGE,"E28.1.4.0"),sQuery(id+"F16.wireOp",EDGE,"E28.1.4.1"),sQuery(id+"F16.wireOp",EDGE,"E28.1.4.2"),sQuery(id+"F16.wireOp",EDGE,"E28.1.4.3")])]});
            var Q27;
            Q27=makeQuery(id+"F17.opExtrude","SWEPT_BODY",BODY,{"disambiguationData":[OSD([sQuery(id+"F16.wireOp",EDGE,"E28.1.7.0"),sQuery(id+"F16.wireOp",EDGE,"E28.1.7.1"),sQuery(id+"F16.wireOp",EDGE,"E28.1.7.2"),sQuery(id+"F16.wireOp",EDGE,"E28.1.7.3")])]});
            var Q28;
            Q28=makeQuery(id+"F17.opExtrude","SWEPT_BODY",BODY,{"disambiguationData":[OSD([sQuery(id+"F16.wireOp",EDGE,"E28.1.5.0"),sQuery(id+"F16.wireOp",EDGE,"E28.1.5.1"),sQuery(id+"F16.wireOp",EDGE,"E28.1.5.2"),sQuery(id+"F16.wireOp",EDGE,"E28.1.5.3")])]});
            var Q29;
            Q29=makeQuery(id+"F17.opExtrude","SWEPT_BODY",BODY,{"disambiguationData":[OSD([sQuery(id+"F16.wireOp",EDGE,"E28.1.3.0"),sQuery(id+"F16.wireOp",EDGE,"E28.1.3.1"),sQuery(id+"F16.wireOp",EDGE,"E28.1.3.2"),sQuery(id+"F16.wireOp",EDGE,"E28.1.3.3")])]});
            var Q30;
            Q30=makeQuery(id+"F17.opExtrude","SWEPT_BODY",BODY,{"disambiguationData":[OSD([sQuery(id+"F16.wireOp",EDGE,"E28.1.8.0"),sQuery(id+"F16.wireOp",EDGE,"E28.1.8.1"),sQuery(id+"F16.wireOp",EDGE,"E28.1.8.2"),sQuery(id+"F16.wireOp",EDGE,"E28.1.8.3")])]});
            var Q31;
            Q31=makeQuery(id+"F17.opExtrude","SWEPT_BODY",BODY,{"disambiguationData":[OSD([sQuery(id+"F16.wireOp",EDGE,"E28.1.0.0"),sQuery(id+"F16.wireOp",EDGE,"E28.1.0.1"),sQuery(id+"F16.wireOp",EDGE,"E28.1.0.2"),sQuery(id+"F16.wireOp",EDGE,"E28.1.0.3")])]});
            var Q32;
            Q32=makeQuery(id+"F4.opExtrude","SWEPT_BODY",BODY,{"disambiguationData":[OSD([sQuery(id+"F0.wireOp",EDGE,"E0.bottom"),sQuery(id+"F0.wireOp",EDGE,"E0.top"),sQuery(id+"F0.wireOp",EDGE,"E0.left"),sQuery(id+"F0.wireOp",EDGE,"E0.right"),sQuery(id+"F0.wireOp",EDGE,"E2.bottom"),sQuery(id+"F0.wireOp",EDGE,"E2.top"),sQuery(id+"F0.wireOp",EDGE,"E2.left"),sQuery(id+"F0.wireOp",EDGE,"E2.right"),sQuery(id+"F0.wireOp",EDGE,"E3.0.1.0"),sQuery(id+"F0.wireOp",EDGE,"E3.0.1.1"),sQuery(id+"F0.wireOp",EDGE,"E3.0.1.2"),sQuery(id+"F0.wireOp",EDGE,"E3.0.1.3"),sQuery(id+"F0.wireOp",EDGE,"E4.0.0.2"),sQuery(id+"F0.wireOp",EDGE,"E4.3.0.2"),sQuery(id+"F0.wireOp",EDGE,"E4.6.0.2"),sQuery(id+"F0.wireOp",EDGE,"E4.9.0.2"),sQuery(id+"F0.wireOp",EDGE,"E4.0.0.3"),sQuery(id+"F0.wireOp",EDGE,"E4.3.0.3"),sQuery(id+"F0.wireOp",EDGE,"E4.6.0.3"),sQuery(id+"F0.wireOp",EDGE,"E4.9.0.3"),sQuery(id+"F0.wireOp",EDGE,"E4.0.0.4"),sQuery(id+"F0.wireOp",EDGE,"E4.3.0.4"),sQuery(id+"F0.wireOp",EDGE,"E4.6.0.4"),sQuery(id+"F0.wireOp",EDGE,"E4.9.0.4"),sQuery(id+"F0.wireOp",EDGE,"E4.0.0.5"),sQuery(id+"F0.wireOp",EDGE,"E4.3.0.5"),sQuery(id+"F0.wireOp",EDGE,"E4.6.0.5"),sQuery(id+"F0.wireOp",EDGE,"E4.9.0.5"),sQuery(id+"F0.wireOp",EDGE,"E4.0.0.6"),sQuery(id+"F0.wireOp",EDGE,"E4.3.0.6"),sQuery(id+"F0.wireOp",EDGE,"E4.6.0.6"),sQuery(id+"F0.wireOp",EDGE,"E4.9.0.6"),sQuery(id+"F0.wireOp",EDGE,"E4.0.0.7"),sQuery(id+"F0.wireOp",EDGE,"E4.3.0.7"),sQuery(id+"F0.wireOp",EDGE,"E4.6.0.7"),sQuery(id+"F0.wireOp",EDGE,"E4.9.0.7"),sQuery(id+"F0.wireOp",EDGE,"E4.0.0.8"),sQuery(id+"F0.wireOp",EDGE,"E4.3.0.8"),sQuery(id+"F0.wireOp",EDGE,"E4.6.0.8"),sQuery(id+"F0.wireOp",EDGE,"E4.9.0.8"),sQuery(id+"F0.wireOp",EDGE,"E4.0.0.9"),sQuery(id+"F0.wireOp",EDGE,"E4.3.0.9"),sQuery(id+"F0.wireOp",EDGE,"E4.6.0.9"),sQuery(id+"F0.wireOp",EDGE,"E4.9.0.9"),sQuery(id+"F0.wireOp",EDGE,"E4.0.0.10"),sQuery(id+"F0.wireOp",EDGE,"E4.3.0.10"),sQuery(id+"F0.wireOp",EDGE,"E4.6.0.10"),sQuery(id+"F0.wireOp",EDGE,"E4.9.0.10"),sQuery(id+"F0.wireOp",EDGE,"E4.0.0.11"),sQuery(id+"F0.wireOp",EDGE,"E4.3.0.11"),sQuery(id+"F0.wireOp",EDGE,"E4.6.0.11"),sQuery(id+"F0.wireOp",EDGE,"E4.9.0.11"),sQuery(id+"F0.wireOp",EDGE,"E4.0.0.12"),sQuery(id+"F0.wireOp",EDGE,"E4.3.0.12"),sQuery(id+"F0.wireOp",EDGE,"E4.6.0.12"),sQuery(id+"F0.wireOp",EDGE,"E4.9.0.12"),sQuery(id+"F0.wireOp",EDGE,"E4.0.0.13"),sQuery(id+"F0.wireOp",EDGE,"E4.3.0.13"),sQuery(id+"F0.wireOp",EDGE,"E4.6.0.13"),sQuery(id+"F0.wireOp",EDGE,"E4.9.0.13"),sQuery(id+"F0.wireOp",EDGE,"E4.0.0.14"),sQuery(id+"F0.wireOp",EDGE,"E4.3.0.14"),sQuery(id+"F0.wireOp",EDGE,"E4.6.0.14"),sQuery(id+"F0.wireOp",EDGE,"E4.9.0.14"),sQuery(id+"F0.wireOp",EDGE,"E4.0.0.15"),sQuery(id+"F0.wireOp",EDGE,"E4.3.0.15"),sQuery(id+"F0.wireOp",EDGE,"E4.6.0.15"),sQuery(id+"F0.wireOp",EDGE,"E4.9.0.15")])]});
            var Q33;
            Q33=makeQuery(id+"F6.opExtrude","SWEPT_BODY",BODY,{"disambiguationData":[OSD([sQuery(id+"F5.wireOp",EDGE,"E5.bottom"),sQuery(id+"F5.wireOp",EDGE,"E5.top"),sQuery(id+"F5.wireOp",EDGE,"E5.left"),sQuery(id+"F5.wireOp",EDGE,"E5.right")])]});
            var Q34;
            Q34=makeQuery(id+"F4.opExtrude","SWEPT_BODY",BODY,{"disambiguationData":[OSD([sQuery(id+"F0.wireOp",EDGE,"E0.bottom"),sQuery(id+"F0.wireOp",EDGE,"E0.top"),sQuery(id+"F0.wireOp",EDGE,"E0.left"),sQuery(id+"F0.wireOp",EDGE,"E0.right"),sQuery(id+"F0.wireOp",EDGE,"E2.bottom"),sQuery(id+"F0.wireOp",EDGE,"E2.top"),sQuery(id+"F0.wireOp",EDGE,"E2.left"),sQuery(id+"F0.wireOp",EDGE,"E2.right"),sQuery(id+"F0.wireOp",EDGE,"E3.0.1.0"),sQuery(id+"F0.wireOp",EDGE,"E3.0.1.1"),sQuery(id+"F0.wireOp",EDGE,"E3.0.1.2"),sQuery(id+"F0.wireOp",EDGE,"E3.0.1.3"),sQuery(id+"F0.wireOp",EDGE,"E4.0.0.2"),sQuery(id+"F0.wireOp",EDGE,"E4.3.0.2"),sQuery(id+"F0.wireOp",EDGE,"E4.6.0.2"),sQuery(id+"F0.wireOp",EDGE,"E4.9.0.2"),sQuery(id+"F0.wireOp",EDGE,"E4.0.0.3"),sQuery(id+"F0.wireOp",EDGE,"E4.3.0.3"),sQuery(id+"F0.wireOp",EDGE,"E4.6.0.3"),sQuery(id+"F0.wireOp",EDGE,"E4.9.0.3"),sQuery(id+"F0.wireOp",EDGE,"E4.0.0.4"),sQuery(id+"F0.wireOp",EDGE,"E4.3.0.4"),sQuery(id+"F0.wireOp",EDGE,"E4.6.0.4"),sQuery(id+"F0.wireOp",EDGE,"E4.9.0.4"),sQuery(id+"F0.wireOp",EDGE,"E4.0.0.5"),sQuery(id+"F0.wireOp",EDGE,"E4.3.0.5"),sQuery(id+"F0.wireOp",EDGE,"E4.6.0.5"),sQuery(id+"F0.wireOp",EDGE,"E4.9.0.5"),sQuery(id+"F0.wireOp",EDGE,"E4.0.0.6"),sQuery(id+"F0.wireOp",EDGE,"E4.3.0.6"),sQuery(id+"F0.wireOp",EDGE,"E4.6.0.6"),sQuery(id+"F0.wireOp",EDGE,"E4.9.0.6"),sQuery(id+"F0.wireOp",EDGE,"E4.0.0.7"),sQuery(id+"F0.wireOp",EDGE,"E4.3.0.7"),sQuery(id+"F0.wireOp",EDGE,"E4.6.0.7"),sQuery(id+"F0.wireOp",EDGE,"E4.9.0.7"),sQuery(id+"F0.wireOp",EDGE,"E4.0.0.8"),sQuery(id+"F0.wireOp",EDGE,"E4.3.0.8"),sQuery(id+"F0.wireOp",EDGE,"E4.6.0.8"),sQuery(id+"F0.wireOp",EDGE,"E4.9.0.8"),sQuery(id+"F0.wireOp",EDGE,"E4.0.0.9"),sQuery(id+"F0.wireOp",EDGE,"E4.3.0.9"),sQuery(id+"F0.wireOp",EDGE,"E4.6.0.9"),sQuery(id+"F0.wireOp",EDGE,"E4.9.0.9"),sQuery(id+"F0.wireOp",EDGE,"E4.0.0.10"),sQuery(id+"F0.wireOp",EDGE,"E4.3.0.10"),sQuery(id+"F0.wireOp",EDGE,"E4.6.0.10"),sQuery(id+"F0.wireOp",EDGE,"E4.9.0.10"),sQuery(id+"F0.wireOp",EDGE,"E4.0.0.11"),sQuery(id+"F0.wireOp",EDGE,"E4.3.0.11"),sQuery(id+"F0.wireOp",EDGE,"E4.6.0.11"),sQuery(id+"F0.wireOp",EDGE,"E4.9.0.11"),sQuery(id+"F0.wireOp",EDGE,"E4.0.0.12"),sQuery(id+"F0.wireOp",EDGE,"E4.3.0.12"),sQuery(id+"F0.wireOp",EDGE,"E4.6.0.12"),sQuery(id+"F0.wireOp",EDGE,"E4.9.0.12"),sQuery(id+"F0.wireOp",EDGE,"E4.0.0.13"),sQuery(id+"F0.wireOp",EDGE,"E4.3.0.13"),sQuery(id+"F0.wireOp",EDGE,"E4.6.0.13"),sQuery(id+"F0.wireOp",EDGE,"E4.9.0.13"),sQuery(id+"F0.wireOp",EDGE,"E4.0.0.14"),sQuery(id+"F0.wireOp",EDGE,"E4.3.0.14"),sQuery(id+"F0.wireOp",EDGE,"E4.6.0.14"),sQuery(id+"F0.wireOp",EDGE,"E4.9.0.14"),sQuery(id+"F0.wireOp",EDGE,"E4.0.0.15"),sQuery(id+"F0.wireOp",EDGE,"E4.3.0.15"),sQuery(id+"F0.wireOp",EDGE,"E4.6.0.15"),sQuery(id+"F0.wireOp",EDGE,"E4.9.0.15")])]});
            var Q35;
            Q35=makeQuery(id+"F6.opExtrude","SWEPT_BODY",BODY,{"disambiguationData":[OSD([sQuery(id+"F5.wireOp",EDGE,"E5.bottom"),sQuery(id+"F5.wireOp",EDGE,"E5.top"),sQuery(id+"F5.wireOp",EDGE,"E5.left"),sQuery(id+"F5.wireOp",EDGE,"E5.right")])]});
            booleanBodies(context, id + "F18", {"operationType" : BooleanOperationType.SUBTRACTION, "tools" : qUnion([Q0, Q1, Q2, Q3, Q4, Q5, Q6, Q7, Q8, Q9, Q10, Q11, Q12, Q13, Q14, Q15, Q16, Q17, Q18, Q19, Q20, Q21, Q22, Q23, Q24, Q25, Q26, Q27, Q28, Q29, Q30, Q31]), "targets" : qUnion([Q32, Q33, Q34, Q35])});
        }
        {
            var Q0;
            Q0=makeQuery(id+"F8.opExtrude","CAP_FACE",FACE,{"disambiguationData":[OSD([sQuery(id+"F7.wireOp",EDGE,"E9.bottom"),sQuery(id+"F7.wireOp",EDGE,"E9.top"),sQuery(id+"F7.wireOp",EDGE,"E9.left"),sQuery(id+"F7.wireOp",EDGE,"E9.right"),sQuery(id+"F7.wireOp",EDGE,"E11.bottom"),sQuery(id+"F7.wireOp",EDGE,"E11.top"),sQuery(id+"F7.wireOp",EDGE,"E11.left"),sQuery(id+"F7.wireOp",EDGE,"E11.right"),sQuery(id+"F7.wireOp",EDGE,"E12.0.1.0"),sQuery(id+"F7.wireOp",EDGE,"E12.0.1.1"),sQuery(id+"F7.wireOp",EDGE,"E12.0.1.2"),sQuery(id+"F7.wireOp",EDGE,"E12.0.1.3"),sQuery(id+"F7.wireOp",EDGE,"E12.0.2.0"),sQuery(id+"F7.wireOp",EDGE,"E12.0.2.1"),sQuery(id+"F7.wireOp",EDGE,"E12.0.2.2"),sQuery(id+"F7.wireOp",EDGE,"E12.0.2.3"),sQuery(id+"F7.wireOp",EDGE,"E12.0.3.0"),sQuery(id+"F7.wireOp",EDGE,"E12.0.3.1"),sQuery(id+"F7.wireOp",EDGE,"E12.0.3.2"),sQuery(id+"F7.wireOp",EDGE,"E12.0.3.3"),sQuery(id+"F7.wireOp",EDGE,"E12.0.4.0"),sQuery(id+"F7.wireOp",EDGE,"E12.0.4.1"),sQuery(id+"F7.wireOp",EDGE,"E12.0.4.2"),sQuery(id+"F7.wireOp",EDGE,"E12.0.4.3"),sQuery(id+"F7.wireOp",EDGE,"E12.0.5.0"),sQuery(id+"F7.wireOp",EDGE,"E12.0.5.1"),sQuery(id+"F7.wireOp",EDGE,"E12.0.5.2"),sQuery(id+"F7.wireOp",EDGE,"E12.0.5.3"),sQuery(id+"F7.wireOp",EDGE,"E12.0.6.0"),sQuery(id+"F7.wireOp",EDGE,"E12.0.6.1"),sQuery(id+"F7.wireOp",EDGE,"E12.0.6.2"),sQuery(id+"F7.wireOp",EDGE,"E12.0.6.3"),sQuery(id+"F7.wireOp",EDGE,"E12.0.7.0"),sQuery(id+"F7.wireOp",EDGE,"E12.0.7.1"),sQuery(id+"F7.wireOp",EDGE,"E12.0.7.2"),sQuery(id+"F7.wireOp",EDGE,"E12.0.7.3"),sQuery(id+"F7.wireOp",EDGE,"E12.0.8.0"),sQuery(id+"F7.wireOp",EDGE,"E12.0.8.1"),sQuery(id+"F7.wireOp",EDGE,"E12.0.8.2"),sQuery(id+"F7.wireOp",EDGE,"E12.0.8.3"),sQuery(id+"F7.wireOp",EDGE,"E12.0.9.0"),sQuery(id+"F7.wireOp",EDGE,"E12.0.9.1"),sQuery(id+"F7.wireOp",EDGE,"E12.0.9.2"),sQuery(id+"F7.wireOp",EDGE,"E12.0.9.3"),sQuery(id+"F7.wireOp",EDGE,"E12.0.10.0"),sQuery(id+"F7.wireOp",EDGE,"E12.0.10.1"),sQuery(id+"F7.wireOp",EDGE,"E12.0.10.2"),sQuery(id+"F7.wireOp",EDGE,"E12.0.10.3"),sQuery(id+"F7.wireOp",EDGE,"E12.0.11.0"),sQuery(id+"F7.wireOp",EDGE,"E12.0.11.1"),sQuery(id+"F7.wireOp",EDGE,"E12.0.11.2"),sQuery(id+"F7.wireOp",EDGE,"E12.0.11.3"),sQuery(id+"F7.wireOp",EDGE,"E12.0.12.0"),sQuery(id+"F7.wireOp",EDGE,"E12.0.12.1"),sQuery(id+"F7.wireOp",EDGE,"E12.0.12.2"),sQuery(id+"F7.wireOp",EDGE,"E12.0.12.3"),sQuery(id+"F7.wireOp",EDGE,"E12.0.13.0"),sQuery(id+"F7.wireOp",EDGE,"E12.0.13.1"),sQuery(id+"F7.wireOp",EDGE,"E12.0.13.2"),sQuery(id+"F7.wireOp",EDGE,"E12.0.13.3"),sQuery(id+"F7.wireOp",EDGE,"E12.0.14.0"),sQuery(id+"F7.wireOp",EDGE,"E12.0.14.1"),sQuery(id+"F7.wireOp",EDGE,"E12.0.14.2"),sQuery(id+"F7.wireOp",EDGE,"E12.0.14.3"),sQuery(id+"F7.wireOp",EDGE,"E12.0.15.0"),sQuery(id+"F7.wireOp",EDGE,"E12.0.15.1"),sQuery(id+"F7.wireOp",EDGE,"E12.0.15.2"),sQuery(id+"F7.wireOp",EDGE,"E12.0.15.3"),sQuery(id+"F7.wireOp",EDGE,"E12.1.0.0"),sQuery(id+"F7.wireOp",EDGE,"E12.1.0.1"),sQuery(id+"F7.wireOp",EDGE,"E12.1.0.2"),sQuery(id+"F7.wireOp",EDGE,"E12.1.0.3"),sQuery(id+"F7.wireOp",EDGE,"E12.1.1.0"),sQuery(id+"F7.wireOp",EDGE,"E12.1.1.1"),sQuery(id+"F7.wireOp",EDGE,"E12.1.1.2"),sQuery(id+"F7.wireOp",EDGE,"E12.1.1.3"),sQuery(id+"F7.wireOp",EDGE,"E12.1.2.0"),sQuery(id+"F7.wireOp",EDGE,"E12.1.2.1"),sQuery(id+"F7.wireOp",EDGE,"E12.1.2.2"),sQuery(id+"F7.wireOp",EDGE,"E12.1.2.3"),sQuery(id+"F7.wireOp",EDGE,"E12.1.3.0"),sQuery(id+"F7.wireOp",EDGE,"E12.1.3.1"),sQuery(id+"F7.wireOp",EDGE,"E12.1.3.2"),sQuery(id+"F7.wireOp",EDGE,"E12.1.3.3"),sQuery(id+"F7.wireOp",EDGE,"E12.1.4.0"),sQuery(id+"F7.wireOp",EDGE,"E12.1.4.1"),sQuery(id+"F7.wireOp",EDGE,"E12.1.4.2"),sQuery(id+"F7.wireOp",EDGE,"E12.1.4.3"),sQuery(id+"F7.wireOp",EDGE,"E12.1.5.0"),sQuery(id+"F7.wireOp",EDGE,"E12.1.5.1"),sQuery(id+"F7.wireOp",EDGE,"E12.1.5.2"),sQuery(id+"F7.wireOp",EDGE,"E12.1.5.3"),sQuery(id+"F7.wireOp",EDGE,"E12.1.6.0"),sQuery(id+"F7.wireOp",EDGE,"E12.1.6.1"),sQuery(id+"F7.wireOp",EDGE,"E12.1.6.2"),sQuery(id+"F7.wireOp",EDGE,"E12.1.6.3"),sQuery(id+"F7.wireOp",EDGE,"E12.1.7.0"),sQuery(id+"F7.wireOp",EDGE,"E12.1.7.1"),sQuery(id+"F7.wireOp",EDGE,"E12.1.7.2"),sQuery(id+"F7.wireOp",EDGE,"E12.1.7.3"),sQuery(id+"F7.wireOp",EDGE,"E12.1.8.0"),sQuery(id+"F7.wireOp",EDGE,"E12.1.8.1"),sQuery(id+"F7.wireOp",EDGE,"E12.1.8.2"),sQuery(id+"F7.wireOp",EDGE,"E12.1.8.3"),sQuery(id+"F7.wireOp",EDGE,"E12.1.9.0"),sQuery(id+"F7.wireOp",EDGE,"E12.1.9.1"),sQuery(id+"F7.wireOp",EDGE,"E12.1.9.2"),sQuery(id+"F7.wireOp",EDGE,"E12.1.9.3"),sQuery(id+"F7.wireOp",EDGE,"E12.1.10.0"),sQuery(id+"F7.wireOp",EDGE,"E12.1.10.1"),sQuery(id+"F7.wireOp",EDGE,"E12.1.10.2"),sQuery(id+"F7.wireOp",EDGE,"E12.1.10.3"),sQuery(id+"F7.wireOp",EDGE,"E12.1.11.0"),sQuery(id+"F7.wireOp",EDGE,"E12.1.11.1"),sQuery(id+"F7.wireOp",EDGE,"E12.1.11.2"),sQuery(id+"F7.wireOp",EDGE,"E12.1.11.3"),sQuery(id+"F7.wireOp",EDGE,"E12.1.12.0"),sQuery(id+"F7.wireOp",EDGE,"E12.1.12.1"),sQuery(id+"F7.wireOp",EDGE,"E12.1.12.2"),sQuery(id+"F7.wireOp",EDGE,"E12.1.12.3"),sQuery(id+"F7.wireOp",EDGE,"E12.1.13.0"),sQuery(id+"F7.wireOp",EDGE,"E12.1.13.1"),sQuery(id+"F7.wireOp",EDGE,"E12.1.13.2"),sQuery(id+"F7.wireOp",EDGE,"E12.1.13.3"),sQuery(id+"F7.wireOp",EDGE,"E12.1.14.0"),sQuery(id+"F7.wireOp",EDGE,"E12.1.14.1"),sQuery(id+"F7.wireOp",EDGE,"E12.1.14.2"),sQuery(id+"F7.wireOp",EDGE,"E12.1.14.3"),sQuery(id+"F7.wireOp",EDGE,"E12.1.15.0"),sQuery(id+"F7.wireOp",EDGE,"E12.1.15.1"),sQuery(id+"F7.wireOp",EDGE,"E12.1.15.2"),sQuery(id+"F7.wireOp",EDGE,"E12.1.15.3"),sQuery(id+"F7.wireOp",EDGE,"E12.2.0.0"),sQuery(id+"F7.wireOp",EDGE,"E12.2.0.1"),sQuery(id+"F7.wireOp",EDGE,"E12.2.0.2"),sQuery(id+"F7.wireOp",EDGE,"E12.2.0.3"),sQuery(id+"F7.wireOp",EDGE,"E12.2.1.0"),sQuery(id+"F7.wireOp",EDGE,"E12.2.1.1"),sQuery(id+"F7.wireOp",EDGE,"E12.2.1.2"),sQuery(id+"F7.wireOp",EDGE,"E12.2.1.3"),sQuery(id+"F7.wireOp",EDGE,"E12.2.2.0"),sQuery(id+"F7.wireOp",EDGE,"E12.2.2.1"),sQuery(id+"F7.wireOp",EDGE,"E12.2.2.2"),sQuery(id+"F7.wireOp",EDGE,"E12.2.2.3"),sQuery(id+"F7.wireOp",EDGE,"E12.2.3.0"),sQuery(id+"F7.wireOp",EDGE,"E12.2.3.1"),sQuery(id+"F7.wireOp",EDGE,"E12.2.3.2"),sQuery(id+"F7.wireOp",EDGE,"E12.2.3.3"),sQuery(id+"F7.wireOp",EDGE,"E12.2.4.0"),sQuery(id+"F7.wireOp",EDGE,"E12.2.4.1"),sQuery(id+"F7.wireOp",EDGE,"E12.2.4.2"),sQuery(id+"F7.wireOp",EDGE,"E12.2.4.3"),sQuery(id+"F7.wireOp",EDGE,"E12.2.5.0"),sQuery(id+"F7.wireOp",EDGE,"E12.2.5.1"),sQuery(id+"F7.wireOp",EDGE,"E12.2.5.2"),sQuery(id+"F7.wireOp",EDGE,"E12.2.5.3"),sQuery(id+"F7.wireOp",EDGE,"E12.2.6.0"),sQuery(id+"F7.wireOp",EDGE,"E12.2.6.1"),sQuery(id+"F7.wireOp",EDGE,"E12.2.6.2"),sQuery(id+"F7.wireOp",EDGE,"E12.2.6.3"),sQuery(id+"F7.wireOp",EDGE,"E12.2.7.0"),sQuery(id+"F7.wireOp",EDGE,"E12.2.7.1"),sQuery(id+"F7.wireOp",EDGE,"E12.2.7.2"),sQuery(id+"F7.wireOp",EDGE,"E12.2.7.3"),sQuery(id+"F7.wireOp",EDGE,"E12.2.8.0"),sQuery(id+"F7.wireOp",EDGE,"E12.2.8.1"),sQuery(id+"F7.wireOp",EDGE,"E12.2.8.2"),sQuery(id+"F7.wireOp",EDGE,"E12.2.8.3"),sQuery(id+"F7.wireOp",EDGE,"E12.2.9.0"),sQuery(id+"F7.wireOp",EDGE,"E12.2.9.1"),sQuery(id+"F7.wireOp",EDGE,"E12.2.9.2"),sQuery(id+"F7.wireOp",EDGE,"E12.2.9.3"),sQuery(id+"F7.wireOp",EDGE,"E12.2.10.0"),sQuery(id+"F7.wireOp",EDGE,"E12.2.10.1"),sQuery(id+"F7.wireOp",EDGE,"E12.2.10.2"),sQuery(id+"F7.wireOp",EDGE,"E12.2.10.3"),sQuery(id+"F7.wireOp",EDGE,"E12.2.11.0"),sQuery(id+"F7.wireOp",EDGE,"E12.2.11.1"),sQuery(id+"F7.wireOp",EDGE,"E12.2.11.2"),sQuery(id+"F7.wireOp",EDGE,"E12.2.11.3"),sQuery(id+"F7.wireOp",EDGE,"E12.2.12.0"),sQuery(id+"F7.wireOp",EDGE,"E12.2.12.1"),sQuery(id+"F7.wireOp",EDGE,"E12.2.12.2"),sQuery(id+"F7.wireOp",EDGE,"E12.2.12.3"),sQuery(id+"F7.wireOp",EDGE,"E12.2.13.0"),sQuery(id+"F7.wireOp",EDGE,"E12.2.13.1"),sQuery(id+"F7.wireOp",EDGE,"E12.2.13.2"),sQuery(id+"F7.wireOp",EDGE,"E12.2.13.3"),sQuery(id+"F7.wireOp",EDGE,"E12.2.14.0"),sQuery(id+"F7.wireOp",EDGE,"E12.2.14.1"),sQuery(id+"F7.wireOp",EDGE,"E12.2.14.2"),sQuery(id+"F7.wireOp",EDGE,"E12.2.14.3"),sQuery(id+"F7.wireOp",EDGE,"E12.2.15.0"),sQuery(id+"F7.wireOp",EDGE,"E12.2.15.1"),sQuery(id+"F7.wireOp",EDGE,"E12.2.15.2"),sQuery(id+"F7.wireOp",EDGE,"E12.2.15.3"),sQuery(id+"F7.wireOp",EDGE,"E12.3.0.0"),sQuery(id+"F7.wireOp",EDGE,"E12.3.0.1"),sQuery(id+"F7.wireOp",EDGE,"E12.3.0.2"),sQuery(id+"F7.wireOp",EDGE,"E12.3.0.3"),sQuery(id+"F7.wireOp",EDGE,"E12.3.1.0"),sQuery(id+"F7.wireOp",EDGE,"E12.3.1.1"),sQuery(id+"F7.wireOp",EDGE,"E12.3.1.2"),sQuery(id+"F7.wireOp",EDGE,"E12.3.1.3"),sQuery(id+"F7.wireOp",EDGE,"E12.3.2.0"),sQuery(id+"F7.wireOp",EDGE,"E12.3.2.1"),sQuery(id+"F7.wireOp",EDGE,"E12.3.2.2"),sQuery(id+"F7.wireOp",EDGE,"E12.3.2.3"),sQuery(id+"F7.wireOp",EDGE,"E12.3.3.0"),sQuery(id+"F7.wireOp",EDGE,"E12.3.3.1"),sQuery(id+"F7.wireOp",EDGE,"E12.3.3.2"),sQuery(id+"F7.wireOp",EDGE,"E12.3.3.3"),sQuery(id+"F7.wireOp",EDGE,"E12.3.4.0"),sQuery(id+"F7.wireOp",EDGE,"E12.3.4.1"),sQuery(id+"F7.wireOp",EDGE,"E12.3.4.2"),sQuery(id+"F7.wireOp",EDGE,"E12.3.4.3"),sQuery(id+"F7.wireOp",EDGE,"E12.3.5.0"),sQuery(id+"F7.wireOp",EDGE,"E12.3.5.1"),sQuery(id+"F7.wireOp",EDGE,"E12.3.5.2"),sQuery(id+"F7.wireOp",EDGE,"E12.3.5.3"),sQuery(id+"F7.wireOp",EDGE,"E12.3.6.0"),sQuery(id+"F7.wireOp",EDGE,"E12.3.6.1"),sQuery(id+"F7.wireOp",EDGE,"E12.3.6.2"),sQuery(id+"F7.wireOp",EDGE,"E12.3.6.3"),sQuery(id+"F7.wireOp",EDGE,"E12.3.7.0"),sQuery(id+"F7.wireOp",EDGE,"E12.3.7.1"),sQuery(id+"F7.wireOp",EDGE,"E12.3.7.2"),sQuery(id+"F7.wireOp",EDGE,"E12.3.7.3"),sQuery(id+"F7.wireOp",EDGE,"E12.3.8.0"),sQuery(id+"F7.wireOp",EDGE,"E12.3.8.1"),sQuery(id+"F7.wireOp",EDGE,"E12.3.8.2"),sQuery(id+"F7.wireOp",EDGE,"E12.3.8.3"),sQuery(id+"F7.wireOp",EDGE,"E12.3.9.0"),sQuery(id+"F7.wireOp",EDGE,"E12.3.9.1"),sQuery(id+"F7.wireOp",EDGE,"E12.3.9.2"),sQuery(id+"F7.wireOp",EDGE,"E12.3.9.3"),sQuery(id+"F7.wireOp",EDGE,"E12.3.10.0"),sQuery(id+"F7.wireOp",EDGE,"E12.3.10.1"),sQuery(id+"F7.wireOp",EDGE,"E12.3.10.2"),sQuery(id+"F7.wireOp",EDGE,"E12.3.10.3"),sQuery(id+"F7.wireOp",EDGE,"E12.3.11.0"),sQuery(id+"F7.wireOp",EDGE,"E12.3.11.1"),sQuery(id+"F7.wireOp",EDGE,"E12.3.11.2"),sQuery(id+"F7.wireOp",EDGE,"E12.3.11.3"),sQuery(id+"F7.wireOp",EDGE,"E12.3.12.0"),sQuery(id+"F7.wireOp",EDGE,"E12.3.12.1"),sQuery(id+"F7.wireOp",EDGE,"E12.3.12.2"),sQuery(id+"F7.wireOp",EDGE,"E12.3.12.3"),sQuery(id+"F7.wireOp",EDGE,"E12.3.13.0"),sQuery(id+"F7.wireOp",EDGE,"E12.3.13.1"),sQuery(id+"F7.wireOp",EDGE,"E12.3.13.2"),sQuery(id+"F7.wireOp",EDGE,"E12.3.13.3"),sQuery(id+"F7.wireOp",EDGE,"E12.3.14.0"),sQuery(id+"F7.wireOp",EDGE,"E12.3.14.1"),sQuery(id+"F7.wireOp",EDGE,"E12.3.14.2"),sQuery(id+"F7.wireOp",EDGE,"E12.3.14.3"),sQuery(id+"F7.wireOp",EDGE,"E12.3.15.0"),sQuery(id+"F7.wireOp",EDGE,"E12.3.15.1"),sQuery(id+"F7.wireOp",EDGE,"E12.3.15.2"),sQuery(id+"F7.wireOp",EDGE,"E12.3.15.3"),sQuery(id+"F7.wireOp",EDGE,"E12.4.0.0"),sQuery(id+"F7.wireOp",EDGE,"E12.4.0.1"),sQuery(id+"F7.wireOp",EDGE,"E12.4.0.2"),sQuery(id+"F7.wireOp",EDGE,"E12.4.0.3"),sQuery(id+"F7.wireOp",EDGE,"E12.4.1.0"),sQuery(id+"F7.wireOp",EDGE,"E12.4.1.1"),sQuery(id+"F7.wireOp",EDGE,"E12.4.1.2"),sQuery(id+"F7.wireOp",EDGE,"E12.4.1.3"),sQuery(id+"F7.wireOp",EDGE,"E12.4.2.0"),sQuery(id+"F7.wireOp",EDGE,"E12.4.2.1"),sQuery(id+"F7.wireOp",EDGE,"E12.4.2.2"),sQuery(id+"F7.wireOp",EDGE,"E12.4.2.3"),sQuery(id+"F7.wireOp",EDGE,"E12.4.3.0"),sQuery(id+"F7.wireOp",EDGE,"E12.4.3.1"),sQuery(id+"F7.wireOp",EDGE,"E12.4.3.2"),sQuery(id+"F7.wireOp",EDGE,"E12.4.3.3"),sQuery(id+"F7.wireOp",EDGE,"E12.4.4.0"),sQuery(id+"F7.wireOp",EDGE,"E12.4.4.1"),sQuery(id+"F7.wireOp",EDGE,"E12.4.4.2"),sQuery(id+"F7.wireOp",EDGE,"E12.4.4.3"),sQuery(id+"F7.wireOp",EDGE,"E12.4.5.0"),sQuery(id+"F7.wireOp",EDGE,"E12.4.5.1"),sQuery(id+"F7.wireOp",EDGE,"E12.4.5.2"),sQuery(id+"F7.wireOp",EDGE,"E12.4.5.3"),sQuery(id+"F7.wireOp",EDGE,"E12.4.6.0"),sQuery(id+"F7.wireOp",EDGE,"E12.4.6.1"),sQuery(id+"F7.wireOp",EDGE,"E12.4.6.2"),sQuery(id+"F7.wireOp",EDGE,"E12.4.6.3"),sQuery(id+"F7.wireOp",EDGE,"E12.4.7.0"),sQuery(id+"F7.wireOp",EDGE,"E12.4.7.1"),sQuery(id+"F7.wireOp",EDGE,"E12.4.7.2"),sQuery(id+"F7.wireOp",EDGE,"E12.4.7.3"),sQuery(id+"F7.wireOp",EDGE,"E12.4.8.0"),sQuery(id+"F7.wireOp",EDGE,"E12.4.8.1"),sQuery(id+"F7.wireOp",EDGE,"E12.4.8.2"),sQuery(id+"F7.wireOp",EDGE,"E12.4.8.3"),sQuery(id+"F7.wireOp",EDGE,"E12.4.9.0"),sQuery(id+"F7.wireOp",EDGE,"E12.4.9.1"),sQuery(id+"F7.wireOp",EDGE,"E12.4.9.2"),sQuery(id+"F7.wireOp",EDGE,"E12.4.9.3"),sQuery(id+"F7.wireOp",EDGE,"E12.4.10.0"),sQuery(id+"F7.wireOp",EDGE,"E12.4.10.1"),sQuery(id+"F7.wireOp",EDGE,"E12.4.10.2"),sQuery(id+"F7.wireOp",EDGE,"E12.4.10.3"),sQuery(id+"F7.wireOp",EDGE,"E12.4.11.0"),sQuery(id+"F7.wireOp",EDGE,"E12.4.11.1"),sQuery(id+"F7.wireOp",EDGE,"E12.4.11.2"),sQuery(id+"F7.wireOp",EDGE,"E12.4.11.3"),sQuery(id+"F7.wireOp",EDGE,"E12.4.12.0"),sQuery(id+"F7.wireOp",EDGE,"E12.4.12.1"),sQuery(id+"F7.wireOp",EDGE,"E12.4.12.2"),sQuery(id+"F7.wireOp",EDGE,"E12.4.12.3"),sQuery(id+"F7.wireOp",EDGE,"E12.4.13.0"),sQuery(id+"F7.wireOp",EDGE,"E12.4.13.1"),sQuery(id+"F7.wireOp",EDGE,"E12.4.13.2"),sQuery(id+"F7.wireOp",EDGE,"E12.4.13.3"),sQuery(id+"F7.wireOp",EDGE,"E12.4.14.0"),sQuery(id+"F7.wireOp",EDGE,"E12.4.14.1"),sQuery(id+"F7.wireOp",EDGE,"E12.4.14.2"),sQuery(id+"F7.wireOp",EDGE,"E12.4.14.3"),sQuery(id+"F7.wireOp",EDGE,"E12.4.15.0"),sQuery(id+"F7.wireOp",EDGE,"E12.4.15.1"),sQuery(id+"F7.wireOp",EDGE,"E12.4.15.2"),sQuery(id+"F7.wireOp",EDGE,"E12.4.15.3"),sQuery(id+"F7.wireOp",EDGE,"E12.5.0.0"),sQuery(id+"F7.wireOp",EDGE,"E12.5.0.1"),sQuery(id+"F7.wireOp",EDGE,"E12.5.0.2"),sQuery(id+"F7.wireOp",EDGE,"E12.5.0.3"),sQuery(id+"F7.wireOp",EDGE,"E12.5.1.0"),sQuery(id+"F7.wireOp",EDGE,"E12.5.1.1"),sQuery(id+"F7.wireOp",EDGE,"E12.5.1.2"),sQuery(id+"F7.wireOp",EDGE,"E12.5.1.3"),sQuery(id+"F7.wireOp",EDGE,"E12.5.2.0"),sQuery(id+"F7.wireOp",EDGE,"E12.5.2.1"),sQuery(id+"F7.wireOp",EDGE,"E12.5.2.2"),sQuery(id+"F7.wireOp",EDGE,"E12.5.2.3"),sQuery(id+"F7.wireOp",EDGE,"E12.5.3.0"),sQuery(id+"F7.wireOp",EDGE,"E12.5.3.1"),sQuery(id+"F7.wireOp",EDGE,"E12.5.3.2"),sQuery(id+"F7.wireOp",EDGE,"E12.5.3.3"),sQuery(id+"F7.wireOp",EDGE,"E12.5.4.0"),sQuery(id+"F7.wireOp",EDGE,"E12.5.4.1"),sQuery(id+"F7.wireOp",EDGE,"E12.5.4.2"),sQuery(id+"F7.wireOp",EDGE,"E12.5.4.3"),sQuery(id+"F7.wireOp",EDGE,"E12.5.5.0"),sQuery(id+"F7.wireOp",EDGE,"E12.5.5.1"),sQuery(id+"F7.wireOp",EDGE,"E12.5.5.2"),sQuery(id+"F7.wireOp",EDGE,"E12.5.5.3"),sQuery(id+"F7.wireOp",EDGE,"E12.5.6.0"),sQuery(id+"F7.wireOp",EDGE,"E12.5.6.1"),sQuery(id+"F7.wireOp",EDGE,"E12.5.6.2"),sQuery(id+"F7.wireOp",EDGE,"E12.5.6.3"),sQuery(id+"F7.wireOp",EDGE,"E12.5.7.0"),sQuery(id+"F7.wireOp",EDGE,"E12.5.7.1"),sQuery(id+"F7.wireOp",EDGE,"E12.5.7.2"),sQuery(id+"F7.wireOp",EDGE,"E12.5.7.3"),sQuery(id+"F7.wireOp",EDGE,"E12.5.8.0"),sQuery(id+"F7.wireOp",EDGE,"E12.5.8.1"),sQuery(id+"F7.wireOp",EDGE,"E12.5.8.2"),sQuery(id+"F7.wireOp",EDGE,"E12.5.8.3"),sQuery(id+"F7.wireOp",EDGE,"E12.5.9.0"),sQuery(id+"F7.wireOp",EDGE,"E12.5.9.1"),sQuery(id+"F7.wireOp",EDGE,"E12.5.9.2"),sQuery(id+"F7.wireOp",EDGE,"E12.5.9.3"),sQuery(id+"F7.wireOp",EDGE,"E12.5.10.0"),sQuery(id+"F7.wireOp",EDGE,"E12.5.10.1"),sQuery(id+"F7.wireOp",EDGE,"E12.5.10.2"),sQuery(id+"F7.wireOp",EDGE,"E12.5.10.3"),sQuery(id+"F7.wireOp",EDGE,"E12.5.11.0"),sQuery(id+"F7.wireOp",EDGE,"E12.5.11.1"),sQuery(id+"F7.wireOp",EDGE,"E12.5.11.2"),sQuery(id+"F7.wireOp",EDGE,"E12.5.11.3"),sQuery(id+"F7.wireOp",EDGE,"E12.5.12.0"),sQuery(id+"F7.wireOp",EDGE,"E12.5.12.1"),sQuery(id+"F7.wireOp",EDGE,"E12.5.12.2"),sQuery(id+"F7.wireOp",EDGE,"E12.5.12.3"),sQuery(id+"F7.wireOp",EDGE,"E12.5.13.0"),sQuery(id+"F7.wireOp",EDGE,"E12.5.13.1"),sQuery(id+"F7.wireOp",EDGE,"E12.5.13.2"),sQuery(id+"F7.wireOp",EDGE,"E12.5.13.3"),sQuery(id+"F7.wireOp",EDGE,"E12.5.14.0"),sQuery(id+"F7.wireOp",EDGE,"E12.5.14.1"),sQuery(id+"F7.wireOp",EDGE,"E12.5.14.2"),sQuery(id+"F7.wireOp",EDGE,"E12.5.14.3"),sQuery(id+"F7.wireOp",EDGE,"E12.5.15.0"),sQuery(id+"F7.wireOp",EDGE,"E12.5.15.1"),sQuery(id+"F7.wireOp",EDGE,"E12.5.15.2"),sQuery(id+"F7.wireOp",EDGE,"E12.5.15.3"),sQuery(id+"F7.wireOp",EDGE,"E12.6.0.0"),sQuery(id+"F7.wireOp",EDGE,"E12.6.0.1"),sQuery(id+"F7.wireOp",EDGE,"E12.6.0.2"),sQuery(id+"F7.wireOp",EDGE,"E12.6.0.3"),sQuery(id+"F7.wireOp",EDGE,"E12.6.1.0"),sQuery(id+"F7.wireOp",EDGE,"E12.6.1.1"),sQuery(id+"F7.wireOp",EDGE,"E12.6.1.2"),sQuery(id+"F7.wireOp",EDGE,"E12.6.1.3"),sQuery(id+"F7.wireOp",EDGE,"E12.6.2.0"),sQuery(id+"F7.wireOp",EDGE,"E12.6.2.1"),sQuery(id+"F7.wireOp",EDGE,"E12.6.2.2"),sQuery(id+"F7.wireOp",EDGE,"E12.6.2.3"),sQuery(id+"F7.wireOp",EDGE,"E12.6.3.0"),sQuery(id+"F7.wireOp",EDGE,"E12.6.3.1"),sQuery(id+"F7.wireOp",EDGE,"E12.6.3.2"),sQuery(id+"F7.wireOp",EDGE,"E12.6.3.3"),sQuery(id+"F7.wireOp",EDGE,"E12.6.4.0"),sQuery(id+"F7.wireOp",EDGE,"E12.6.4.1"),sQuery(id+"F7.wireOp",EDGE,"E12.6.4.2"),sQuery(id+"F7.wireOp",EDGE,"E12.6.4.3"),sQuery(id+"F7.wireOp",EDGE,"E12.6.5.0"),sQuery(id+"F7.wireOp",EDGE,"E12.6.5.1"),sQuery(id+"F7.wireOp",EDGE,"E12.6.5.2"),sQuery(id+"F7.wireOp",EDGE,"E12.6.5.3"),sQuery(id+"F7.wireOp",EDGE,"E12.6.6.0"),sQuery(id+"F7.wireOp",EDGE,"E12.6.6.1"),sQuery(id+"F7.wireOp",EDGE,"E12.6.6.2"),sQuery(id+"F7.wireOp",EDGE,"E12.6.6.3"),sQuery(id+"F7.wireOp",EDGE,"E12.6.7.0"),sQuery(id+"F7.wireOp",EDGE,"E12.6.7.1"),sQuery(id+"F7.wireOp",EDGE,"E12.6.7.2"),sQuery(id+"F7.wireOp",EDGE,"E12.6.7.3"),sQuery(id+"F7.wireOp",EDGE,"E12.6.8.0"),sQuery(id+"F7.wireOp",EDGE,"E12.6.8.1"),sQuery(id+"F7.wireOp",EDGE,"E12.6.8.2"),sQuery(id+"F7.wireOp",EDGE,"E12.6.8.3"),sQuery(id+"F7.wireOp",EDGE,"E12.6.9.0"),sQuery(id+"F7.wireOp",EDGE,"E12.6.9.1"),sQuery(id+"F7.wireOp",EDGE,"E12.6.9.2"),sQuery(id+"F7.wireOp",EDGE,"E12.6.9.3"),sQuery(id+"F7.wireOp",EDGE,"E12.6.10.0"),sQuery(id+"F7.wireOp",EDGE,"E12.6.10.1"),sQuery(id+"F7.wireOp",EDGE,"E12.6.10.2"),sQuery(id+"F7.wireOp",EDGE,"E12.6.10.3"),sQuery(id+"F7.wireOp",EDGE,"E12.6.11.0"),sQuery(id+"F7.wireOp",EDGE,"E12.6.11.1"),sQuery(id+"F7.wireOp",EDGE,"E12.6.11.2"),sQuery(id+"F7.wireOp",EDGE,"E12.6.11.3"),sQuery(id+"F7.wireOp",EDGE,"E12.6.12.0"),sQuery(id+"F7.wireOp",EDGE,"E12.6.12.1"),sQuery(id+"F7.wireOp",EDGE,"E12.6.12.2"),sQuery(id+"F7.wireOp",EDGE,"E12.6.12.3"),sQuery(id+"F7.wireOp",EDGE,"E12.6.13.0"),sQuery(id+"F7.wireOp",EDGE,"E12.6.13.1"),sQuery(id+"F7.wireOp",EDGE,"E12.6.13.2"),sQuery(id+"F7.wireOp",EDGE,"E12.6.13.3"),sQuery(id+"F7.wireOp",EDGE,"E12.6.14.0"),sQuery(id+"F7.wireOp",EDGE,"E12.6.14.1"),sQuery(id+"F7.wireOp",EDGE,"E12.6.14.2"),sQuery(id+"F7.wireOp",EDGE,"E12.6.14.3"),sQuery(id+"F7.wireOp",EDGE,"E12.6.15.0"),sQuery(id+"F7.wireOp",EDGE,"E12.6.15.1"),sQuery(id+"F7.wireOp",EDGE,"E12.6.15.2"),sQuery(id+"F7.wireOp",EDGE,"E12.6.15.3"),sQuery(id+"F7.wireOp",EDGE,"E12.7.0.0"),sQuery(id+"F7.wireOp",EDGE,"E12.7.0.1"),sQuery(id+"F7.wireOp",EDGE,"E12.7.0.2"),sQuery(id+"F7.wireOp",EDGE,"E12.7.0.3"),sQuery(id+"F7.wireOp",EDGE,"E12.7.1.0"),sQuery(id+"F7.wireOp",EDGE,"E12.7.1.1"),sQuery(id+"F7.wireOp",EDGE,"E12.7.1.2"),sQuery(id+"F7.wireOp",EDGE,"E12.7.1.3"),sQuery(id+"F7.wireOp",EDGE,"E12.7.2.0"),sQuery(id+"F7.wireOp",EDGE,"E12.7.2.1"),sQuery(id+"F7.wireOp",EDGE,"E12.7.2.2"),sQuery(id+"F7.wireOp",EDGE,"E12.7.2.3"),sQuery(id+"F7.wireOp",EDGE,"E12.7.3.0"),sQuery(id+"F7.wireOp",EDGE,"E12.7.3.1"),sQuery(id+"F7.wireOp",EDGE,"E12.7.3.2"),sQuery(id+"F7.wireOp",EDGE,"E12.7.3.3"),sQuery(id+"F7.wireOp",EDGE,"E12.7.4.0"),sQuery(id+"F7.wireOp",EDGE,"E12.7.4.1"),sQuery(id+"F7.wireOp",EDGE,"E12.7.4.2"),sQuery(id+"F7.wireOp",EDGE,"E12.7.4.3"),sQuery(id+"F7.wireOp",EDGE,"E12.7.5.0"),sQuery(id+"F7.wireOp",EDGE,"E12.7.5.1"),sQuery(id+"F7.wireOp",EDGE,"E12.7.5.2"),sQuery(id+"F7.wireOp",EDGE,"E12.7.5.3"),sQuery(id+"F7.wireOp",EDGE,"E12.7.6.0"),sQuery(id+"F7.wireOp",EDGE,"E12.7.6.1"),sQuery(id+"F7.wireOp",EDGE,"E12.7.6.2"),sQuery(id+"F7.wireOp",EDGE,"E12.7.6.3"),sQuery(id+"F7.wireOp",EDGE,"E12.7.7.0"),sQuery(id+"F7.wireOp",EDGE,"E12.7.7.1"),sQuery(id+"F7.wireOp",EDGE,"E12.7.7.2"),sQuery(id+"F7.wireOp",EDGE,"E12.7.7.3"),sQuery(id+"F7.wireOp",EDGE,"E12.7.8.0"),sQuery(id+"F7.wireOp",EDGE,"E12.7.8.1"),sQuery(id+"F7.wireOp",EDGE,"E12.7.8.2"),sQuery(id+"F7.wireOp",EDGE,"E12.7.8.3"),sQuery(id+"F7.wireOp",EDGE,"E12.7.9.0"),sQuery(id+"F7.wireOp",EDGE,"E12.7.9.1"),sQuery(id+"F7.wireOp",EDGE,"E12.7.9.2"),sQuery(id+"F7.wireOp",EDGE,"E12.7.9.3"),sQuery(id+"F7.wireOp",EDGE,"E12.7.10.0"),sQuery(id+"F7.wireOp",EDGE,"E12.7.10.1"),sQuery(id+"F7.wireOp",EDGE,"E12.7.10.2"),sQuery(id+"F7.wireOp",EDGE,"E12.7.10.3"),sQuery(id+"F7.wireOp",EDGE,"E12.7.11.0"),sQuery(id+"F7.wireOp",EDGE,"E12.7.11.1"),sQuery(id+"F7.wireOp",EDGE,"E12.7.11.2"),sQuery(id+"F7.wireOp",EDGE,"E12.7.11.3"),sQuery(id+"F7.wireOp",EDGE,"E12.7.12.0"),sQuery(id+"F7.wireOp",EDGE,"E12.7.12.1"),sQuery(id+"F7.wireOp",EDGE,"E12.7.12.2"),sQuery(id+"F7.wireOp",EDGE,"E12.7.12.3"),sQuery(id+"F7.wireOp",EDGE,"E12.7.13.0"),sQuery(id+"F7.wireOp",EDGE,"E12.7.13.1"),sQuery(id+"F7.wireOp",EDGE,"E12.7.13.2"),sQuery(id+"F7.wireOp",EDGE,"E12.7.13.3"),sQuery(id+"F7.wireOp",EDGE,"E12.7.14.0"),sQuery(id+"F7.wireOp",EDGE,"E12.7.14.1"),sQuery(id+"F7.wireOp",EDGE,"E12.7.14.2"),sQuery(id+"F7.wireOp",EDGE,"E12.7.14.3"),sQuery(id+"F7.wireOp",EDGE,"E12.7.15.0"),sQuery(id+"F7.wireOp",EDGE,"E12.7.15.1"),sQuery(id+"F7.wireOp",EDGE,"E12.7.15.2"),sQuery(id+"F7.wireOp",EDGE,"E12.7.15.3"),sQuery(id+"F7.wireOp",EDGE,"E12.8.0.0"),sQuery(id+"F7.wireOp",EDGE,"E12.8.0.1"),sQuery(id+"F7.wireOp",EDGE,"E12.8.0.2"),sQuery(id+"F7.wireOp",EDGE,"E12.8.0.3"),sQuery(id+"F7.wireOp",EDGE,"E12.8.1.0"),sQuery(id+"F7.wireOp",EDGE,"E12.8.1.1"),sQuery(id+"F7.wireOp",EDGE,"E12.8.1.2"),sQuery(id+"F7.wireOp",EDGE,"E12.8.1.3"),sQuery(id+"F7.wireOp",EDGE,"E12.8.2.0"),sQuery(id+"F7.wireOp",EDGE,"E12.8.2.1"),sQuery(id+"F7.wireOp",EDGE,"E12.8.2.2"),sQuery(id+"F7.wireOp",EDGE,"E12.8.2.3"),sQuery(id+"F7.wireOp",EDGE,"E12.8.3.0"),sQuery(id+"F7.wireOp",EDGE,"E12.8.3.1"),sQuery(id+"F7.wireOp",EDGE,"E12.8.3.2"),sQuery(id+"F7.wireOp",EDGE,"E12.8.3.3"),sQuery(id+"F7.wireOp",EDGE,"E12.8.4.0"),sQuery(id+"F7.wireOp",EDGE,"E12.8.4.1"),sQuery(id+"F7.wireOp",EDGE,"E12.8.4.2"),sQuery(id+"F7.wireOp",EDGE,"E12.8.4.3"),sQuery(id+"F7.wireOp",EDGE,"E12.8.5.0"),sQuery(id+"F7.wireOp",EDGE,"E12.8.5.1"),sQuery(id+"F7.wireOp",EDGE,"E12.8.5.2"),sQuery(id+"F7.wireOp",EDGE,"E12.8.5.3"),sQuery(id+"F7.wireOp",EDGE,"E12.8.6.0"),sQuery(id+"F7.wireOp",EDGE,"E12.8.6.1"),sQuery(id+"F7.wireOp",EDGE,"E12.8.6.2"),sQuery(id+"F7.wireOp",EDGE,"E12.8.6.3"),sQuery(id+"F7.wireOp",EDGE,"E12.8.7.0"),sQuery(id+"F7.wireOp",EDGE,"E12.8.7.1"),sQuery(id+"F7.wireOp",EDGE,"E12.8.7.2"),sQuery(id+"F7.wireOp",EDGE,"E12.8.7.3"),sQuery(id+"F7.wireOp",EDGE,"E12.8.8.0"),sQuery(id+"F7.wireOp",EDGE,"E12.8.8.1"),sQuery(id+"F7.wireOp",EDGE,"E12.8.8.2"),sQuery(id+"F7.wireOp",EDGE,"E12.8.8.3"),sQuery(id+"F7.wireOp",EDGE,"E12.8.9.0"),sQuery(id+"F7.wireOp",EDGE,"E12.8.9.1"),sQuery(id+"F7.wireOp",EDGE,"E12.8.9.2"),sQuery(id+"F7.wireOp",EDGE,"E12.8.9.3"),sQuery(id+"F7.wireOp",EDGE,"E12.8.10.0"),sQuery(id+"F7.wireOp",EDGE,"E12.8.10.1"),sQuery(id+"F7.wireOp",EDGE,"E12.8.10.2"),sQuery(id+"F7.wireOp",EDGE,"E12.8.10.3"),sQuery(id+"F7.wireOp",EDGE,"E12.8.11.0"),sQuery(id+"F7.wireOp",EDGE,"E12.8.11.1"),sQuery(id+"F7.wireOp",EDGE,"E12.8.11.2"),sQuery(id+"F7.wireOp",EDGE,"E12.8.11.3"),sQuery(id+"F7.wireOp",EDGE,"E12.8.12.0"),sQuery(id+"F7.wireOp",EDGE,"E12.8.12.1"),sQuery(id+"F7.wireOp",EDGE,"E12.8.12.2"),sQuery(id+"F7.wireOp",EDGE,"E12.8.12.3"),sQuery(id+"F7.wireOp",EDGE,"E12.8.13.0"),sQuery(id+"F7.wireOp",EDGE,"E12.8.13.1"),sQuery(id+"F7.wireOp",EDGE,"E12.8.13.2"),sQuery(id+"F7.wireOp",EDGE,"E12.8.13.3"),sQuery(id+"F7.wireOp",EDGE,"E12.8.14.0"),sQuery(id+"F7.wireOp",EDGE,"E12.8.14.1"),sQuery(id+"F7.wireOp",EDGE,"E12.8.14.2"),sQuery(id+"F7.wireOp",EDGE,"E12.8.14.3"),sQuery(id+"F7.wireOp",EDGE,"E12.8.15.0"),sQuery(id+"F7.wireOp",EDGE,"E12.8.15.1"),sQuery(id+"F7.wireOp",EDGE,"E12.8.15.2"),sQuery(id+"F7.wireOp",EDGE,"E12.8.15.3"),sQuery(id+"F7.wireOp",EDGE,"E12.9.0.0"),sQuery(id+"F7.wireOp",EDGE,"E12.9.0.1"),sQuery(id+"F7.wireOp",EDGE,"E12.9.0.2"),sQuery(id+"F7.wireOp",EDGE,"E12.9.0.3"),sQuery(id+"F7.wireOp",EDGE,"E12.9.1.0"),sQuery(id+"F7.wireOp",EDGE,"E12.9.1.1"),sQuery(id+"F7.wireOp",EDGE,"E12.9.1.2"),sQuery(id+"F7.wireOp",EDGE,"E12.9.1.3"),sQuery(id+"F7.wireOp",EDGE,"E12.9.2.0"),sQuery(id+"F7.wireOp",EDGE,"E12.9.2.1"),sQuery(id+"F7.wireOp",EDGE,"E12.9.2.2"),sQuery(id+"F7.wireOp",EDGE,"E12.9.2.3"),sQuery(id+"F7.wireOp",EDGE,"E12.9.3.0"),sQuery(id+"F7.wireOp",EDGE,"E12.9.3.1"),sQuery(id+"F7.wireOp",EDGE,"E12.9.3.2"),sQuery(id+"F7.wireOp",EDGE,"E12.9.3.3"),sQuery(id+"F7.wireOp",EDGE,"E12.9.4.0"),sQuery(id+"F7.wireOp",EDGE,"E12.9.4.1"),sQuery(id+"F7.wireOp",EDGE,"E12.9.4.2"),sQuery(id+"F7.wireOp",EDGE,"E12.9.4.3"),sQuery(id+"F7.wireOp",EDGE,"E12.9.5.0"),sQuery(id+"F7.wireOp",EDGE,"E12.9.5.1"),sQuery(id+"F7.wireOp",EDGE,"E12.9.5.2"),sQuery(id+"F7.wireOp",EDGE,"E12.9.5.3"),sQuery(id+"F7.wireOp",EDGE,"E12.9.6.0"),sQuery(id+"F7.wireOp",EDGE,"E12.9.6.1"),sQuery(id+"F7.wireOp",EDGE,"E12.9.6.2"),sQuery(id+"F7.wireOp",EDGE,"E12.9.6.3"),sQuery(id+"F7.wireOp",EDGE,"E12.9.7.0"),sQuery(id+"F7.wireOp",EDGE,"E12.9.7.1"),sQuery(id+"F7.wireOp",EDGE,"E12.9.7.2"),sQuery(id+"F7.wireOp",EDGE,"E12.9.7.3"),sQuery(id+"F7.wireOp",EDGE,"E12.9.8.0"),sQuery(id+"F7.wireOp",EDGE,"E12.9.8.1"),sQuery(id+"F7.wireOp",EDGE,"E12.9.8.2"),sQuery(id+"F7.wireOp",EDGE,"E12.9.8.3"),sQuery(id+"F7.wireOp",EDGE,"E12.9.9.0"),sQuery(id+"F7.wireOp",EDGE,"E12.9.9.1"),sQuery(id+"F7.wireOp",EDGE,"E12.9.9.2"),sQuery(id+"F7.wireOp",EDGE,"E12.9.9.3"),sQuery(id+"F7.wireOp",EDGE,"E12.9.10.0"),sQuery(id+"F7.wireOp",EDGE,"E12.9.10.1"),sQuery(id+"F7.wireOp",EDGE,"E12.9.10.2"),sQuery(id+"F7.wireOp",EDGE,"E12.9.10.3"),sQuery(id+"F7.wireOp",EDGE,"E12.9.11.0"),sQuery(id+"F7.wireOp",EDGE,"E12.9.11.1"),sQuery(id+"F7.wireOp",EDGE,"E12.9.11.2"),sQuery(id+"F7.wireOp",EDGE,"E12.9.11.3"),sQuery(id+"F7.wireOp",EDGE,"E12.9.12.0"),sQuery(id+"F7.wireOp",EDGE,"E12.9.12.1"),sQuery(id+"F7.wireOp",EDGE,"E12.9.12.2"),sQuery(id+"F7.wireOp",EDGE,"E12.9.12.3"),sQuery(id+"F7.wireOp",EDGE,"E12.9.13.0"),sQuery(id+"F7.wireOp",EDGE,"E12.9.13.1"),sQuery(id+"F7.wireOp",EDGE,"E12.9.13.2"),sQuery(id+"F7.wireOp",EDGE,"E12.9.13.3"),sQuery(id+"F7.wireOp",EDGE,"E12.9.14.0"),sQuery(id+"F7.wireOp",EDGE,"E12.9.14.1"),sQuery(id+"F7.wireOp",EDGE,"E12.9.14.2"),sQuery(id+"F7.wireOp",EDGE,"E12.9.14.3"),sQuery(id+"F7.wireOp",EDGE,"E12.9.15.0"),sQuery(id+"F7.wireOp",EDGE,"E12.9.15.1"),sQuery(id+"F7.wireOp",EDGE,"E12.9.15.2"),sQuery(id+"F7.wireOp",EDGE,"E12.9.15.3"),sQuery(id+"F7.wireOp",EDGE,"E12.10.0.0"),sQuery(id+"F7.wireOp",EDGE,"E12.10.0.1"),sQuery(id+"F7.wireOp",EDGE,"E12.10.0.2"),sQuery(id+"F7.wireOp",EDGE,"E12.10.0.3"),sQuery(id+"F7.wireOp",EDGE,"E12.10.1.0"),sQuery(id+"F7.wireOp",EDGE,"E12.10.1.1"),sQuery(id+"F7.wireOp",EDGE,"E12.10.1.2"),sQuery(id+"F7.wireOp",EDGE,"E12.10.1.3"),sQuery(id+"F7.wireOp",EDGE,"E12.10.2.0"),sQuery(id+"F7.wireOp",EDGE,"E12.10.2.1"),sQuery(id+"F7.wireOp",EDGE,"E12.10.2.2"),sQuery(id+"F7.wireOp",EDGE,"E12.10.2.3"),sQuery(id+"F7.wireOp",EDGE,"E12.10.3.0"),sQuery(id+"F7.wireOp",EDGE,"E12.10.3.1"),sQuery(id+"F7.wireOp",EDGE,"E12.10.3.2"),sQuery(id+"F7.wireOp",EDGE,"E12.10.3.3"),sQuery(id+"F7.wireOp",EDGE,"E12.10.4.0"),sQuery(id+"F7.wireOp",EDGE,"E12.10.4.1"),sQuery(id+"F7.wireOp",EDGE,"E12.10.4.2"),sQuery(id+"F7.wireOp",EDGE,"E12.10.4.3"),sQuery(id+"F7.wireOp",EDGE,"E12.10.5.0"),sQuery(id+"F7.wireOp",EDGE,"E12.10.5.1"),sQuery(id+"F7.wireOp",EDGE,"E12.10.5.2"),sQuery(id+"F7.wireOp",EDGE,"E12.10.5.3"),sQuery(id+"F7.wireOp",EDGE,"E12.10.6.0"),sQuery(id+"F7.wireOp",EDGE,"E12.10.6.1"),sQuery(id+"F7.wireOp",EDGE,"E12.10.6.2"),sQuery(id+"F7.wireOp",EDGE,"E12.10.6.3"),sQuery(id+"F7.wireOp",EDGE,"E12.10.7.0"),sQuery(id+"F7.wireOp",EDGE,"E12.10.7.1"),sQuery(id+"F7.wireOp",EDGE,"E12.10.7.2"),sQuery(id+"F7.wireOp",EDGE,"E12.10.7.3"),sQuery(id+"F7.wireOp",EDGE,"E12.10.8.0"),sQuery(id+"F7.wireOp",EDGE,"E12.10.8.1"),sQuery(id+"F7.wireOp",EDGE,"E12.10.8.2"),sQuery(id+"F7.wireOp",EDGE,"E12.10.8.3"),sQuery(id+"F7.wireOp",EDGE,"E12.10.9.0"),sQuery(id+"F7.wireOp",EDGE,"E12.10.9.1"),sQuery(id+"F7.wireOp",EDGE,"E12.10.9.2"),sQuery(id+"F7.wireOp",EDGE,"E12.10.9.3"),sQuery(id+"F7.wireOp",EDGE,"E12.10.10.0"),sQuery(id+"F7.wireOp",EDGE,"E12.10.10.1"),sQuery(id+"F7.wireOp",EDGE,"E12.10.10.2"),sQuery(id+"F7.wireOp",EDGE,"E12.10.10.3"),sQuery(id+"F7.wireOp",EDGE,"E12.10.11.0"),sQuery(id+"F7.wireOp",EDGE,"E12.10.11.1"),sQuery(id+"F7.wireOp",EDGE,"E12.10.11.2"),sQuery(id+"F7.wireOp",EDGE,"E12.10.11.3"),sQuery(id+"F7.wireOp",EDGE,"E12.10.12.0"),sQuery(id+"F7.wireOp",EDGE,"E12.10.12.1"),sQuery(id+"F7.wireOp",EDGE,"E12.10.12.2"),sQuery(id+"F7.wireOp",EDGE,"E12.10.12.3"),sQuery(id+"F7.wireOp",EDGE,"E12.10.13.0"),sQuery(id+"F7.wireOp",EDGE,"E12.10.13.1"),sQuery(id+"F7.wireOp",EDGE,"E12.10.13.2"),sQuery(id+"F7.wireOp",EDGE,"E12.10.13.3"),sQuery(id+"F7.wireOp",EDGE,"E12.10.14.0"),sQuery(id+"F7.wireOp",EDGE,"E12.10.14.1"),sQuery(id+"F7.wireOp",EDGE,"E12.10.14.2"),sQuery(id+"F7.wireOp",EDGE,"E12.10.14.3"),sQuery(id+"F7.wireOp",EDGE,"E12.10.15.0"),sQuery(id+"F7.wireOp",EDGE,"E12.10.15.1"),sQuery(id+"F7.wireOp",EDGE,"E12.10.15.2"),sQuery(id+"F7.wireOp",EDGE,"E12.10.15.3"),sQuery(id+"F7.wireOp",EDGE,"E12.11.0.0"),sQuery(id+"F7.wireOp",EDGE,"E12.11.0.1"),sQuery(id+"F7.wireOp",EDGE,"E12.11.0.2"),sQuery(id+"F7.wireOp",EDGE,"E12.11.0.3"),sQuery(id+"F7.wireOp",EDGE,"E12.11.1.0"),sQuery(id+"F7.wireOp",EDGE,"E12.11.1.1"),sQuery(id+"F7.wireOp",EDGE,"E12.11.1.2"),sQuery(id+"F7.wireOp",EDGE,"E12.11.1.3"),sQuery(id+"F7.wireOp",EDGE,"E12.11.2.0"),sQuery(id+"F7.wireOp",EDGE,"E12.11.2.1"),sQuery(id+"F7.wireOp",EDGE,"E12.11.2.2"),sQuery(id+"F7.wireOp",EDGE,"E12.11.2.3"),sQuery(id+"F7.wireOp",EDGE,"E12.11.3.0"),sQuery(id+"F7.wireOp",EDGE,"E12.11.3.1"),sQuery(id+"F7.wireOp",EDGE,"E12.11.3.2"),sQuery(id+"F7.wireOp",EDGE,"E12.11.3.3"),sQuery(id+"F7.wireOp",EDGE,"E12.11.4.0"),sQuery(id+"F7.wireOp",EDGE,"E12.11.4.1"),sQuery(id+"F7.wireOp",EDGE,"E12.11.4.2"),sQuery(id+"F7.wireOp",EDGE,"E12.11.4.3"),sQuery(id+"F7.wireOp",EDGE,"E12.11.5.0"),sQuery(id+"F7.wireOp",EDGE,"E12.11.5.1"),sQuery(id+"F7.wireOp",EDGE,"E12.11.5.2"),sQuery(id+"F7.wireOp",EDGE,"E12.11.5.3"),sQuery(id+"F7.wireOp",EDGE,"E12.11.6.0"),sQuery(id+"F7.wireOp",EDGE,"E12.11.6.1"),sQuery(id+"F7.wireOp",EDGE,"E12.11.6.2"),sQuery(id+"F7.wireOp",EDGE,"E12.11.6.3"),sQuery(id+"F7.wireOp",EDGE,"E12.11.7.0"),sQuery(id+"F7.wireOp",EDGE,"E12.11.7.1"),sQuery(id+"F7.wireOp",EDGE,"E12.11.7.2"),sQuery(id+"F7.wireOp",EDGE,"E12.11.7.3"),sQuery(id+"F7.wireOp",EDGE,"E12.11.8.0"),sQuery(id+"F7.wireOp",EDGE,"E12.11.8.1"),sQuery(id+"F7.wireOp",EDGE,"E12.11.8.2"),sQuery(id+"F7.wireOp",EDGE,"E12.11.8.3"),sQuery(id+"F7.wireOp",EDGE,"E12.11.9.0"),sQuery(id+"F7.wireOp",EDGE,"E12.11.9.1"),sQuery(id+"F7.wireOp",EDGE,"E12.11.9.2"),sQuery(id+"F7.wireOp",EDGE,"E12.11.9.3"),sQuery(id+"F7.wireOp",EDGE,"E12.11.10.0"),sQuery(id+"F7.wireOp",EDGE,"E12.11.10.1"),sQuery(id+"F7.wireOp",EDGE,"E12.11.10.2"),sQuery(id+"F7.wireOp",EDGE,"E12.11.10.3"),sQuery(id+"F7.wireOp",EDGE,"E12.11.11.0"),sQuery(id+"F7.wireOp",EDGE,"E12.11.11.1"),sQuery(id+"F7.wireOp",EDGE,"E12.11.11.2"),sQuery(id+"F7.wireOp",EDGE,"E12.11.11.3"),sQuery(id+"F7.wireOp",EDGE,"E12.11.12.0"),sQuery(id+"F7.wireOp",EDGE,"E12.11.12.1"),sQuery(id+"F7.wireOp",EDGE,"E12.11.12.2"),sQuery(id+"F7.wireOp",EDGE,"E12.11.12.3"),sQuery(id+"F7.wireOp",EDGE,"E12.11.13.0"),sQuery(id+"F7.wireOp",EDGE,"E12.11.13.1"),sQuery(id+"F7.wireOp",EDGE,"E12.11.13.2"),sQuery(id+"F7.wireOp",EDGE,"E12.11.13.3"),sQuery(id+"F7.wireOp",EDGE,"E12.11.14.0"),sQuery(id+"F7.wireOp",EDGE,"E12.11.14.1"),sQuery(id+"F7.wireOp",EDGE,"E12.11.14.2"),sQuery(id+"F7.wireOp",EDGE,"E12.11.14.3"),sQuery(id+"F7.wireOp",EDGE,"E12.11.15.0"),sQuery(id+"F7.wireOp",EDGE,"E12.11.15.1"),sQuery(id+"F7.wireOp",EDGE,"E12.11.15.2"),sQuery(id+"F7.wireOp",EDGE,"E12.11.15.3"),sQuery(id+"F7.wireOp",EDGE,"E12.12.0.0"),sQuery(id+"F7.wireOp",EDGE,"E12.12.0.1"),sQuery(id+"F7.wireOp",EDGE,"E12.12.0.2"),sQuery(id+"F7.wireOp",EDGE,"E12.12.0.3"),sQuery(id+"F7.wireOp",EDGE,"E12.12.1.0"),sQuery(id+"F7.wireOp",EDGE,"E12.12.1.1"),sQuery(id+"F7.wireOp",EDGE,"E12.12.1.2"),sQuery(id+"F7.wireOp",EDGE,"E12.12.1.3"),sQuery(id+"F7.wireOp",EDGE,"E12.12.2.0"),sQuery(id+"F7.wireOp",EDGE,"E12.12.2.1"),sQuery(id+"F7.wireOp",EDGE,"E12.12.2.2"),sQuery(id+"F7.wireOp",EDGE,"E12.12.2.3"),sQuery(id+"F7.wireOp",EDGE,"E12.12.3.0"),sQuery(id+"F7.wireOp",EDGE,"E12.12.3.1"),sQuery(id+"F7.wireOp",EDGE,"E12.12.3.2"),sQuery(id+"F7.wireOp",EDGE,"E12.12.3.3"),sQuery(id+"F7.wireOp",EDGE,"E12.12.4.0"),sQuery(id+"F7.wireOp",EDGE,"E12.12.4.1"),sQuery(id+"F7.wireOp",EDGE,"E12.12.4.2"),sQuery(id+"F7.wireOp",EDGE,"E12.12.4.3"),sQuery(id+"F7.wireOp",EDGE,"E12.12.5.0"),sQuery(id+"F7.wireOp",EDGE,"E12.12.5.1"),sQuery(id+"F7.wireOp",EDGE,"E12.12.5.2"),sQuery(id+"F7.wireOp",EDGE,"E12.12.5.3"),sQuery(id+"F7.wireOp",EDGE,"E12.12.6.0"),sQuery(id+"F7.wireOp",EDGE,"E12.12.6.1"),sQuery(id+"F7.wireOp",EDGE,"E12.12.6.2"),sQuery(id+"F7.wireOp",EDGE,"E12.12.6.3"),sQuery(id+"F7.wireOp",EDGE,"E12.12.7.0"),sQuery(id+"F7.wireOp",EDGE,"E12.12.7.1"),sQuery(id+"F7.wireOp",EDGE,"E12.12.7.2"),sQuery(id+"F7.wireOp",EDGE,"E12.12.7.3"),sQuery(id+"F7.wireOp",EDGE,"E12.12.8.0"),sQuery(id+"F7.wireOp",EDGE,"E12.12.8.1"),sQuery(id+"F7.wireOp",EDGE,"E12.12.8.2"),sQuery(id+"F7.wireOp",EDGE,"E12.12.8.3"),sQuery(id+"F7.wireOp",EDGE,"E12.12.9.0"),sQuery(id+"F7.wireOp",EDGE,"E12.12.9.1"),sQuery(id+"F7.wireOp",EDGE,"E12.12.9.2"),sQuery(id+"F7.wireOp",EDGE,"E12.12.9.3"),sQuery(id+"F7.wireOp",EDGE,"E12.12.10.0"),sQuery(id+"F7.wireOp",EDGE,"E12.12.10.1"),sQuery(id+"F7.wireOp",EDGE,"E12.12.10.2"),sQuery(id+"F7.wireOp",EDGE,"E12.12.10.3"),sQuery(id+"F7.wireOp",EDGE,"E12.12.11.0"),sQuery(id+"F7.wireOp",EDGE,"E12.12.11.1"),sQuery(id+"F7.wireOp",EDGE,"E12.12.11.2"),sQuery(id+"F7.wireOp",EDGE,"E12.12.11.3"),sQuery(id+"F7.wireOp",EDGE,"E12.12.12.0"),sQuery(id+"F7.wireOp",EDGE,"E12.12.12.1"),sQuery(id+"F7.wireOp",EDGE,"E12.12.12.2"),sQuery(id+"F7.wireOp",EDGE,"E12.12.12.3"),sQuery(id+"F7.wireOp",EDGE,"E12.12.13.0"),sQuery(id+"F7.wireOp",EDGE,"E12.12.13.1"),sQuery(id+"F7.wireOp",EDGE,"E12.12.13.2"),sQuery(id+"F7.wireOp",EDGE,"E12.12.13.3"),sQuery(id+"F7.wireOp",EDGE,"E12.12.14.0"),sQuery(id+"F7.wireOp",EDGE,"E12.12.14.1"),sQuery(id+"F7.wireOp",EDGE,"E12.12.14.2"),sQuery(id+"F7.wireOp",EDGE,"E12.12.14.3"),sQuery(id+"F7.wireOp",EDGE,"E12.12.15.0"),sQuery(id+"F7.wireOp",EDGE,"E12.12.15.1"),sQuery(id+"F7.wireOp",EDGE,"E12.12.15.2"),sQuery(id+"F7.wireOp",EDGE,"E12.12.15.3"),sQuery(id+"F7.wireOp",EDGE,"E12.13.0.0"),sQuery(id+"F7.wireOp",EDGE,"E12.13.0.1"),sQuery(id+"F7.wireOp",EDGE,"E12.13.0.2"),sQuery(id+"F7.wireOp",EDGE,"E12.13.0.3"),sQuery(id+"F7.wireOp",EDGE,"E12.13.1.0"),sQuery(id+"F7.wireOp",EDGE,"E12.13.1.1"),sQuery(id+"F7.wireOp",EDGE,"E12.13.1.2"),sQuery(id+"F7.wireOp",EDGE,"E12.13.1.3"),sQuery(id+"F7.wireOp",EDGE,"E12.13.2.0"),sQuery(id+"F7.wireOp",EDGE,"E12.13.2.1"),sQuery(id+"F7.wireOp",EDGE,"E12.13.2.2"),sQuery(id+"F7.wireOp",EDGE,"E12.13.2.3"),sQuery(id+"F7.wireOp",EDGE,"E12.13.3.0"),sQuery(id+"F7.wireOp",EDGE,"E12.13.3.1"),sQuery(id+"F7.wireOp",EDGE,"E12.13.3.2"),sQuery(id+"F7.wireOp",EDGE,"E12.13.3.3"),sQuery(id+"F7.wireOp",EDGE,"E12.13.4.0"),sQuery(id+"F7.wireOp",EDGE,"E12.13.4.1"),sQuery(id+"F7.wireOp",EDGE,"E12.13.4.2"),sQuery(id+"F7.wireOp",EDGE,"E12.13.4.3"),sQuery(id+"F7.wireOp",EDGE,"E12.13.5.0"),sQuery(id+"F7.wireOp",EDGE,"E12.13.5.1"),sQuery(id+"F7.wireOp",EDGE,"E12.13.5.2"),sQuery(id+"F7.wireOp",EDGE,"E12.13.5.3"),sQuery(id+"F7.wireOp",EDGE,"E12.13.6.0"),sQuery(id+"F7.wireOp",EDGE,"E12.13.6.1"),sQuery(id+"F7.wireOp",EDGE,"E12.13.6.2"),sQuery(id+"F7.wireOp",EDGE,"E12.13.6.3"),sQuery(id+"F7.wireOp",EDGE,"E12.13.7.0"),sQuery(id+"F7.wireOp",EDGE,"E12.13.7.1"),sQuery(id+"F7.wireOp",EDGE,"E12.13.7.2"),sQuery(id+"F7.wireOp",EDGE,"E12.13.7.3"),sQuery(id+"F7.wireOp",EDGE,"E12.13.8.0"),sQuery(id+"F7.wireOp",EDGE,"E12.13.8.1"),sQuery(id+"F7.wireOp",EDGE,"E12.13.8.2"),sQuery(id+"F7.wireOp",EDGE,"E12.13.8.3"),sQuery(id+"F7.wireOp",EDGE,"E12.13.9.0"),sQuery(id+"F7.wireOp",EDGE,"E12.13.9.1"),sQuery(id+"F7.wireOp",EDGE,"E12.13.9.2"),sQuery(id+"F7.wireOp",EDGE,"E12.13.9.3"),sQuery(id+"F7.wireOp",EDGE,"E12.13.10.0"),sQuery(id+"F7.wireOp",EDGE,"E12.13.10.1"),sQuery(id+"F7.wireOp",EDGE,"E12.13.10.2"),sQuery(id+"F7.wireOp",EDGE,"E12.13.10.3"),sQuery(id+"F7.wireOp",EDGE,"E12.13.11.0"),sQuery(id+"F7.wireOp",EDGE,"E12.13.11.1"),sQuery(id+"F7.wireOp",EDGE,"E12.13.11.2"),sQuery(id+"F7.wireOp",EDGE,"E12.13.11.3"),sQuery(id+"F7.wireOp",EDGE,"E12.13.12.0"),sQuery(id+"F7.wireOp",EDGE,"E12.13.12.1"),sQuery(id+"F7.wireOp",EDGE,"E12.13.12.2"),sQuery(id+"F7.wireOp",EDGE,"E12.13.12.3"),sQuery(id+"F7.wireOp",EDGE,"E12.13.13.0"),sQuery(id+"F7.wireOp",EDGE,"E12.13.13.1"),sQuery(id+"F7.wireOp",EDGE,"E12.13.13.2"),sQuery(id+"F7.wireOp",EDGE,"E12.13.13.3"),sQuery(id+"F7.wireOp",EDGE,"E12.13.14.0"),sQuery(id+"F7.wireOp",EDGE,"E12.13.14.1"),sQuery(id+"F7.wireOp",EDGE,"E12.13.14.2"),sQuery(id+"F7.wireOp",EDGE,"E12.13.14.3"),sQuery(id+"F7.wireOp",EDGE,"E12.13.15.0"),sQuery(id+"F7.wireOp",EDGE,"E12.13.15.1"),sQuery(id+"F7.wireOp",EDGE,"E12.13.15.2"),sQuery(id+"F7.wireOp",EDGE,"E12.13.15.3"),sQuery(id+"F7.wireOp",EDGE,"E12.14.0.0"),sQuery(id+"F7.wireOp",EDGE,"E12.14.0.1"),sQuery(id+"F7.wireOp",EDGE,"E12.14.0.2"),sQuery(id+"F7.wireOp",EDGE,"E12.14.0.3"),sQuery(id+"F7.wireOp",EDGE,"E12.14.1.0"),sQuery(id+"F7.wireOp",EDGE,"E12.14.1.1"),sQuery(id+"F7.wireOp",EDGE,"E12.14.1.2"),sQuery(id+"F7.wireOp",EDGE,"E12.14.1.3"),sQuery(id+"F7.wireOp",EDGE,"E12.14.2.0"),sQuery(id+"F7.wireOp",EDGE,"E12.14.2.1"),sQuery(id+"F7.wireOp",EDGE,"E12.14.2.2"),sQuery(id+"F7.wireOp",EDGE,"E12.14.2.3"),sQuery(id+"F7.wireOp",EDGE,"E12.14.3.0"),sQuery(id+"F7.wireOp",EDGE,"E12.14.3.1"),sQuery(id+"F7.wireOp",EDGE,"E12.14.3.2"),sQuery(id+"F7.wireOp",EDGE,"E12.14.3.3"),sQuery(id+"F7.wireOp",EDGE,"E12.14.4.0"),sQuery(id+"F7.wireOp",EDGE,"E12.14.4.1"),sQuery(id+"F7.wireOp",EDGE,"E12.14.4.2"),sQuery(id+"F7.wireOp",EDGE,"E12.14.4.3"),sQuery(id+"F7.wireOp",EDGE,"E12.14.5.0"),sQuery(id+"F7.wireOp",EDGE,"E12.14.5.1"),sQuery(id+"F7.wireOp",EDGE,"E12.14.5.2"),sQuery(id+"F7.wireOp",EDGE,"E12.14.5.3"),sQuery(id+"F7.wireOp",EDGE,"E12.14.6.0"),sQuery(id+"F7.wireOp",EDGE,"E12.14.6.1"),sQuery(id+"F7.wireOp",EDGE,"E12.14.6.2"),sQuery(id+"F7.wireOp",EDGE,"E12.14.6.3"),sQuery(id+"F7.wireOp",EDGE,"E12.14.7.0"),sQuery(id+"F7.wireOp",EDGE,"E12.14.7.1"),sQuery(id+"F7.wireOp",EDGE,"E12.14.7.2"),sQuery(id+"F7.wireOp",EDGE,"E12.14.7.3"),sQuery(id+"F7.wireOp",EDGE,"E12.14.8.0"),sQuery(id+"F7.wireOp",EDGE,"E12.14.8.1"),sQuery(id+"F7.wireOp",EDGE,"E12.14.8.2"),sQuery(id+"F7.wireOp",EDGE,"E12.14.8.3"),sQuery(id+"F7.wireOp",EDGE,"E12.14.9.0"),sQuery(id+"F7.wireOp",EDGE,"E12.14.9.1"),sQuery(id+"F7.wireOp",EDGE,"E12.14.9.2"),sQuery(id+"F7.wireOp",EDGE,"E12.14.9.3"),sQuery(id+"F7.wireOp",EDGE,"E12.14.10.0"),sQuery(id+"F7.wireOp",EDGE,"E12.14.10.1"),sQuery(id+"F7.wireOp",EDGE,"E12.14.10.2"),sQuery(id+"F7.wireOp",EDGE,"E12.14.10.3"),sQuery(id+"F7.wireOp",EDGE,"E12.14.11.0"),sQuery(id+"F7.wireOp",EDGE,"E12.14.11.1"),sQuery(id+"F7.wireOp",EDGE,"E12.14.11.2"),sQuery(id+"F7.wireOp",EDGE,"E12.14.11.3"),sQuery(id+"F7.wireOp",EDGE,"E12.14.12.0"),sQuery(id+"F7.wireOp",EDGE,"E12.14.12.1"),sQuery(id+"F7.wireOp",EDGE,"E12.14.12.2"),sQuery(id+"F7.wireOp",EDGE,"E12.14.12.3"),sQuery(id+"F7.wireOp",EDGE,"E12.14.13.0"),sQuery(id+"F7.wireOp",EDGE,"E12.14.13.1"),sQuery(id+"F7.wireOp",EDGE,"E12.14.13.2"),sQuery(id+"F7.wireOp",EDGE,"E12.14.13.3"),sQuery(id+"F7.wireOp",EDGE,"E12.14.14.0"),sQuery(id+"F7.wireOp",EDGE,"E12.14.14.1"),sQuery(id+"F7.wireOp",EDGE,"E12.14.14.2"),sQuery(id+"F7.wireOp",EDGE,"E12.14.14.3"),sQuery(id+"F7.wireOp",EDGE,"E12.14.15.0"),sQuery(id+"F7.wireOp",EDGE,"E12.14.15.1"),sQuery(id+"F7.wireOp",EDGE,"E12.14.15.2"),sQuery(id+"F7.wireOp",EDGE,"E12.14.15.3"),sQuery(id+"F7.wireOp",EDGE,"E12.15.0.0"),sQuery(id+"F7.wireOp",EDGE,"E12.15.0.1"),sQuery(id+"F7.wireOp",EDGE,"E12.15.0.2"),sQuery(id+"F7.wireOp",EDGE,"E12.15.0.3"),sQuery(id+"F7.wireOp",EDGE,"E12.15.1.0"),sQuery(id+"F7.wireOp",EDGE,"E12.15.1.1"),sQuery(id+"F7.wireOp",EDGE,"E12.15.1.2"),sQuery(id+"F7.wireOp",EDGE,"E12.15.1.3"),sQuery(id+"F7.wireOp",EDGE,"E12.15.2.0"),sQuery(id+"F7.wireOp",EDGE,"E12.15.2.1"),sQuery(id+"F7.wireOp",EDGE,"E12.15.2.2"),sQuery(id+"F7.wireOp",EDGE,"E12.15.2.3"),sQuery(id+"F7.wireOp",EDGE,"E12.15.3.0"),sQuery(id+"F7.wireOp",EDGE,"E12.15.3.1"),sQuery(id+"F7.wireOp",EDGE,"E12.15.3.2"),sQuery(id+"F7.wireOp",EDGE,"E12.15.3.3"),sQuery(id+"F7.wireOp",EDGE,"E12.15.4.0"),sQuery(id+"F7.wireOp",EDGE,"E12.15.4.1"),sQuery(id+"F7.wireOp",EDGE,"E12.15.4.2"),sQuery(id+"F7.wireOp",EDGE,"E12.15.4.3"),sQuery(id+"F7.wireOp",EDGE,"E12.15.5.0"),sQuery(id+"F7.wireOp",EDGE,"E12.15.5.1"),sQuery(id+"F7.wireOp",EDGE,"E12.15.5.2"),sQuery(id+"F7.wireOp",EDGE,"E12.15.5.3"),sQuery(id+"F7.wireOp",EDGE,"E12.15.6.0"),sQuery(id+"F7.wireOp",EDGE,"E12.15.6.1"),sQuery(id+"F7.wireOp",EDGE,"E12.15.6.2"),sQuery(id+"F7.wireOp",EDGE,"E12.15.6.3"),sQuery(id+"F7.wireOp",EDGE,"E12.15.7.0"),sQuery(id+"F7.wireOp",EDGE,"E12.15.7.1"),sQuery(id+"F7.wireOp",EDGE,"E12.15.7.2"),sQuery(id+"F7.wireOp",EDGE,"E12.15.7.3"),sQuery(id+"F7.wireOp",EDGE,"E12.15.8.0"),sQuery(id+"F7.wireOp",EDGE,"E12.15.8.1"),sQuery(id+"F7.wireOp",EDGE,"E12.15.8.2"),sQuery(id+"F7.wireOp",EDGE,"E12.15.8.3"),sQuery(id+"F7.wireOp",EDGE,"E12.15.9.0"),sQuery(id+"F7.wireOp",EDGE,"E12.15.9.1"),sQuery(id+"F7.wireOp",EDGE,"E12.15.9.2"),sQuery(id+"F7.wireOp",EDGE,"E12.15.9.3"),sQuery(id+"F7.wireOp",EDGE,"E12.15.10.0"),sQuery(id+"F7.wireOp",EDGE,"E12.15.10.1"),sQuery(id+"F7.wireOp",EDGE,"E12.15.10.2"),sQuery(id+"F7.wireOp",EDGE,"E12.15.10.3"),sQuery(id+"F7.wireOp",EDGE,"E12.15.11.0"),sQuery(id+"F7.wireOp",EDGE,"E12.15.11.1"),sQuery(id+"F7.wireOp",EDGE,"E12.15.11.2"),sQuery(id+"F7.wireOp",EDGE,"E12.15.11.3"),sQuery(id+"F7.wireOp",EDGE,"E12.15.12.0"),sQuery(id+"F7.wireOp",EDGE,"E12.15.12.1"),sQuery(id+"F7.wireOp",EDGE,"E12.15.12.2"),sQuery(id+"F7.wireOp",EDGE,"E12.15.12.3"),sQuery(id+"F7.wireOp",EDGE,"E12.15.13.0"),sQuery(id+"F7.wireOp",EDGE,"E12.15.13.1"),sQuery(id+"F7.wireOp",EDGE,"E12.15.13.2"),sQuery(id+"F7.wireOp",EDGE,"E12.15.13.3"),sQuery(id+"F7.wireOp",EDGE,"E12.15.14.0"),sQuery(id+"F7.wireOp",EDGE,"E12.15.14.1"),sQuery(id+"F7.wireOp",EDGE,"E12.15.14.2"),sQuery(id+"F7.wireOp",EDGE,"E12.15.14.3"),sQuery(id+"F7.wireOp",EDGE,"E12.15.15.0"),sQuery(id+"F7.wireOp",EDGE,"E12.15.15.1"),sQuery(id+"F7.wireOp",EDGE,"E12.15.15.2"),sQuery(id+"F7.wireOp",EDGE,"E12.15.15.3")])],"isStart":false});
            var sketch = newSketch(context, id + "F19", { "sketchPlane" : qUnion([Q0])});
            skLineSegment(sketch, "E29.bottom", {"start": v(-315, 350) * mm, "end": v(315, 350) * mm});
            skLineSegment(sketch, "E29.top", {"start": v(-315, 280) * mm, "end": v(315, 280) * mm});
            skLineSegment(sketch, "E29.left", {"start": v(-315, 350) * mm, "end": v(-315, 280) * mm});
            skLineSegment(sketch, "E29.right", {"start": v(315, 350) * mm, "end": v(315, 280) * mm});
            skLineSegment(sketch, "E30", {"start": v(375, 0) * mm, "end": v(-375, 0) * mm, "construction": true});
            skLineSegment(sketch, "E31.MirrorCS", {"start": v(315, -350) * mm, "end": v(315, -280) * mm});
            skLineSegment(sketch, "E32.MirrorCS", {"start": v(-315, -280) * mm, "end": v(315, -280) * mm});
            skLineSegment(sketch, "E33.MirrorCS", {"start": v(-315, -350) * mm, "end": v(315, -350) * mm});
            skLineSegment(sketch, "E34.MirrorCS", {"start": v(-315, -350) * mm, "end": v(-315, -280) * mm});
            skSolve(sketch);
        }
        {
            var Q0;
            Q0=makeQuery(id+"F19.imprint","IMPRINT",FACE,{"disambiguationData":[TD([[makeQuery(id+"F19.imprint","IMPRINT",EDGE,{"derivedFrom":sQuery(id+"F19.wireOp",EDGE,"E29.bottom")}),-1.0]])]});
            var Q1;
            Q1=makeQuery(id+"F19.imprint","IMPRINT",FACE,{"disambiguationData":[TD([[makeQuery(id+"F19.imprint","IMPRINT",EDGE,{"derivedFrom":sQuery(id+"F19.wireOp",EDGE,"E31.MirrorCS")}),1.0]])]});
            extrude(context, id + "F20", {"entities" : qUnion([Q0, Q1]), "endBound" : BoundingType.SYMMETRIC, "depth" : -50 * mm, "offsetDistance" : 25 * mm});
        }
        {
            var Q0;
            Q0=makeQuery(id+"F20.opExtrude","SWEPT_BODY",BODY,{"disambiguationData":[OSD([sQuery(id+"F19.wireOp",EDGE,"E29.bottom"),sQuery(id+"F19.wireOp",EDGE,"E29.top"),sQuery(id+"F19.wireOp",EDGE,"E29.left"),sQuery(id+"F19.wireOp",EDGE,"E29.right")])]});
            var Q1;
            Q1=makeQuery(id+"F20.opExtrude","SWEPT_BODY",BODY,{"disambiguationData":[OSD([sQuery(id+"F19.wireOp",EDGE,"E31.MirrorCS"),sQuery(id+"F19.wireOp",EDGE,"E32.MirrorCS"),sQuery(id+"F19.wireOp",EDGE,"E33.MirrorCS"),sQuery(id+"F19.wireOp",EDGE,"E34.MirrorCS")])]});
            var Q2;
            Q2=makeQuery(id+"F8.opExtrude","SWEPT_BODY",BODY,{"disambiguationData":[OSD([sQuery(id+"F7.wireOp",EDGE,"E9.bottom"),sQuery(id+"F7.wireOp",EDGE,"E9.top"),sQuery(id+"F7.wireOp",EDGE,"E9.left"),sQuery(id+"F7.wireOp",EDGE,"E9.right"),sQuery(id+"F7.wireOp",EDGE,"E11.bottom"),sQuery(id+"F7.wireOp",EDGE,"E11.top"),sQuery(id+"F7.wireOp",EDGE,"E11.left"),sQuery(id+"F7.wireOp",EDGE,"E11.right"),sQuery(id+"F7.wireOp",EDGE,"E12.0.1.0"),sQuery(id+"F7.wireOp",EDGE,"E12.0.1.1"),sQuery(id+"F7.wireOp",EDGE,"E12.0.1.2"),sQuery(id+"F7.wireOp",EDGE,"E12.0.1.3"),sQuery(id+"F7.wireOp",EDGE,"E12.0.2.0"),sQuery(id+"F7.wireOp",EDGE,"E12.0.2.1"),sQuery(id+"F7.wireOp",EDGE,"E12.0.2.2"),sQuery(id+"F7.wireOp",EDGE,"E12.0.2.3"),sQuery(id+"F7.wireOp",EDGE,"E12.0.3.0"),sQuery(id+"F7.wireOp",EDGE,"E12.0.3.1"),sQuery(id+"F7.wireOp",EDGE,"E12.0.3.2"),sQuery(id+"F7.wireOp",EDGE,"E12.0.3.3"),sQuery(id+"F7.wireOp",EDGE,"E12.0.4.0"),sQuery(id+"F7.wireOp",EDGE,"E12.0.4.1"),sQuery(id+"F7.wireOp",EDGE,"E12.0.4.2"),sQuery(id+"F7.wireOp",EDGE,"E12.0.4.3"),sQuery(id+"F7.wireOp",EDGE,"E12.0.5.0"),sQuery(id+"F7.wireOp",EDGE,"E12.0.5.1"),sQuery(id+"F7.wireOp",EDGE,"E12.0.5.2"),sQuery(id+"F7.wireOp",EDGE,"E12.0.5.3"),sQuery(id+"F7.wireOp",EDGE,"E12.0.6.0"),sQuery(id+"F7.wireOp",EDGE,"E12.0.6.1"),sQuery(id+"F7.wireOp",EDGE,"E12.0.6.2"),sQuery(id+"F7.wireOp",EDGE,"E12.0.6.3"),sQuery(id+"F7.wireOp",EDGE,"E12.0.7.0"),sQuery(id+"F7.wireOp",EDGE,"E12.0.7.1"),sQuery(id+"F7.wireOp",EDGE,"E12.0.7.2"),sQuery(id+"F7.wireOp",EDGE,"E12.0.7.3"),sQuery(id+"F7.wireOp",EDGE,"E12.0.8.0"),sQuery(id+"F7.wireOp",EDGE,"E12.0.8.1"),sQuery(id+"F7.wireOp",EDGE,"E12.0.8.2"),sQuery(id+"F7.wireOp",EDGE,"E12.0.8.3"),sQuery(id+"F7.wireOp",EDGE,"E12.0.9.0"),sQuery(id+"F7.wireOp",EDGE,"E12.0.9.1"),sQuery(id+"F7.wireOp",EDGE,"E12.0.9.2"),sQuery(id+"F7.wireOp",EDGE,"E12.0.9.3"),sQuery(id+"F7.wireOp",EDGE,"E12.0.10.0"),sQuery(id+"F7.wireOp",EDGE,"E12.0.10.1"),sQuery(id+"F7.wireOp",EDGE,"E12.0.10.2"),sQuery(id+"F7.wireOp",EDGE,"E12.0.10.3"),sQuery(id+"F7.wireOp",EDGE,"E12.0.11.0"),sQuery(id+"F7.wireOp",EDGE,"E12.0.11.1"),sQuery(id+"F7.wireOp",EDGE,"E12.0.11.2"),sQuery(id+"F7.wireOp",EDGE,"E12.0.11.3"),sQuery(id+"F7.wireOp",EDGE,"E12.0.12.0"),sQuery(id+"F7.wireOp",EDGE,"E12.0.12.1"),sQuery(id+"F7.wireOp",EDGE,"E12.0.12.2"),sQuery(id+"F7.wireOp",EDGE,"E12.0.12.3"),sQuery(id+"F7.wireOp",EDGE,"E12.0.13.0"),sQuery(id+"F7.wireOp",EDGE,"E12.0.13.1"),sQuery(id+"F7.wireOp",EDGE,"E12.0.13.2"),sQuery(id+"F7.wireOp",EDGE,"E12.0.13.3"),sQuery(id+"F7.wireOp",EDGE,"E12.0.14.0"),sQuery(id+"F7.wireOp",EDGE,"E12.0.14.1"),sQuery(id+"F7.wireOp",EDGE,"E12.0.14.2"),sQuery(id+"F7.wireOp",EDGE,"E12.0.14.3"),sQuery(id+"F7.wireOp",EDGE,"E12.0.15.0"),sQuery(id+"F7.wireOp",EDGE,"E12.0.15.1"),sQuery(id+"F7.wireOp",EDGE,"E12.0.15.2"),sQuery(id+"F7.wireOp",EDGE,"E12.0.15.3"),sQuery(id+"F7.wireOp",EDGE,"E12.1.0.0"),sQuery(id+"F7.wireOp",EDGE,"E12.1.0.1"),sQuery(id+"F7.wireOp",EDGE,"E12.1.0.2"),sQuery(id+"F7.wireOp",EDGE,"E12.1.0.3"),sQuery(id+"F7.wireOp",EDGE,"E12.1.1.0"),sQuery(id+"F7.wireOp",EDGE,"E12.1.1.1"),sQuery(id+"F7.wireOp",EDGE,"E12.1.1.2"),sQuery(id+"F7.wireOp",EDGE,"E12.1.1.3"),sQuery(id+"F7.wireOp",EDGE,"E12.1.2.0"),sQuery(id+"F7.wireOp",EDGE,"E12.1.2.1"),sQuery(id+"F7.wireOp",EDGE,"E12.1.2.2"),sQuery(id+"F7.wireOp",EDGE,"E12.1.2.3"),sQuery(id+"F7.wireOp",EDGE,"E12.1.3.0"),sQuery(id+"F7.wireOp",EDGE,"E12.1.3.1"),sQuery(id+"F7.wireOp",EDGE,"E12.1.3.2"),sQuery(id+"F7.wireOp",EDGE,"E12.1.3.3"),sQuery(id+"F7.wireOp",EDGE,"E12.1.4.0"),sQuery(id+"F7.wireOp",EDGE,"E12.1.4.1"),sQuery(id+"F7.wireOp",EDGE,"E12.1.4.2"),sQuery(id+"F7.wireOp",EDGE,"E12.1.4.3"),sQuery(id+"F7.wireOp",EDGE,"E12.1.5.0"),sQuery(id+"F7.wireOp",EDGE,"E12.1.5.1"),sQuery(id+"F7.wireOp",EDGE,"E12.1.5.2"),sQuery(id+"F7.wireOp",EDGE,"E12.1.5.3"),sQuery(id+"F7.wireOp",EDGE,"E12.1.6.0"),sQuery(id+"F7.wireOp",EDGE,"E12.1.6.1"),sQuery(id+"F7.wireOp",EDGE,"E12.1.6.2"),sQuery(id+"F7.wireOp",EDGE,"E12.1.6.3"),sQuery(id+"F7.wireOp",EDGE,"E12.1.7.0"),sQuery(id+"F7.wireOp",EDGE,"E12.1.7.1"),sQuery(id+"F7.wireOp",EDGE,"E12.1.7.2"),sQuery(id+"F7.wireOp",EDGE,"E12.1.7.3"),sQuery(id+"F7.wireOp",EDGE,"E12.1.8.0"),sQuery(id+"F7.wireOp",EDGE,"E12.1.8.1"),sQuery(id+"F7.wireOp",EDGE,"E12.1.8.2"),sQuery(id+"F7.wireOp",EDGE,"E12.1.8.3"),sQuery(id+"F7.wireOp",EDGE,"E12.1.9.0"),sQuery(id+"F7.wireOp",EDGE,"E12.1.9.1"),sQuery(id+"F7.wireOp",EDGE,"E12.1.9.2"),sQuery(id+"F7.wireOp",EDGE,"E12.1.9.3"),sQuery(id+"F7.wireOp",EDGE,"E12.1.10.0"),sQuery(id+"F7.wireOp",EDGE,"E12.1.10.1"),sQuery(id+"F7.wireOp",EDGE,"E12.1.10.2"),sQuery(id+"F7.wireOp",EDGE,"E12.1.10.3"),sQuery(id+"F7.wireOp",EDGE,"E12.1.11.0"),sQuery(id+"F7.wireOp",EDGE,"E12.1.11.1"),sQuery(id+"F7.wireOp",EDGE,"E12.1.11.2"),sQuery(id+"F7.wireOp",EDGE,"E12.1.11.3"),sQuery(id+"F7.wireOp",EDGE,"E12.1.12.0"),sQuery(id+"F7.wireOp",EDGE,"E12.1.12.1"),sQuery(id+"F7.wireOp",EDGE,"E12.1.12.2"),sQuery(id+"F7.wireOp",EDGE,"E12.1.12.3"),sQuery(id+"F7.wireOp",EDGE,"E12.1.13.0"),sQuery(id+"F7.wireOp",EDGE,"E12.1.13.1"),sQuery(id+"F7.wireOp",EDGE,"E12.1.13.2"),sQuery(id+"F7.wireOp",EDGE,"E12.1.13.3"),sQuery(id+"F7.wireOp",EDGE,"E12.1.14.0"),sQuery(id+"F7.wireOp",EDGE,"E12.1.14.1"),sQuery(id+"F7.wireOp",EDGE,"E12.1.14.2"),sQuery(id+"F7.wireOp",EDGE,"E12.1.14.3"),sQuery(id+"F7.wireOp",EDGE,"E12.1.15.0"),sQuery(id+"F7.wireOp",EDGE,"E12.1.15.1"),sQuery(id+"F7.wireOp",EDGE,"E12.1.15.2"),sQuery(id+"F7.wireOp",EDGE,"E12.1.15.3"),sQuery(id+"F7.wireOp",EDGE,"E12.2.0.0"),sQuery(id+"F7.wireOp",EDGE,"E12.2.0.1"),sQuery(id+"F7.wireOp",EDGE,"E12.2.0.2"),sQuery(id+"F7.wireOp",EDGE,"E12.2.0.3"),sQuery(id+"F7.wireOp",EDGE,"E12.2.1.0"),sQuery(id+"F7.wireOp",EDGE,"E12.2.1.1"),sQuery(id+"F7.wireOp",EDGE,"E12.2.1.2"),sQuery(id+"F7.wireOp",EDGE,"E12.2.1.3"),sQuery(id+"F7.wireOp",EDGE,"E12.2.2.0"),sQuery(id+"F7.wireOp",EDGE,"E12.2.2.1"),sQuery(id+"F7.wireOp",EDGE,"E12.2.2.2"),sQuery(id+"F7.wireOp",EDGE,"E12.2.2.3"),sQuery(id+"F7.wireOp",EDGE,"E12.2.3.0"),sQuery(id+"F7.wireOp",EDGE,"E12.2.3.1"),sQuery(id+"F7.wireOp",EDGE,"E12.2.3.2"),sQuery(id+"F7.wireOp",EDGE,"E12.2.3.3"),sQuery(id+"F7.wireOp",EDGE,"E12.2.4.0"),sQuery(id+"F7.wireOp",EDGE,"E12.2.4.1"),sQuery(id+"F7.wireOp",EDGE,"E12.2.4.2"),sQuery(id+"F7.wireOp",EDGE,"E12.2.4.3"),sQuery(id+"F7.wireOp",EDGE,"E12.2.5.0"),sQuery(id+"F7.wireOp",EDGE,"E12.2.5.1"),sQuery(id+"F7.wireOp",EDGE,"E12.2.5.2"),sQuery(id+"F7.wireOp",EDGE,"E12.2.5.3"),sQuery(id+"F7.wireOp",EDGE,"E12.2.6.0"),sQuery(id+"F7.wireOp",EDGE,"E12.2.6.1"),sQuery(id+"F7.wireOp",EDGE,"E12.2.6.2"),sQuery(id+"F7.wireOp",EDGE,"E12.2.6.3"),sQuery(id+"F7.wireOp",EDGE,"E12.2.7.0"),sQuery(id+"F7.wireOp",EDGE,"E12.2.7.1"),sQuery(id+"F7.wireOp",EDGE,"E12.2.7.2"),sQuery(id+"F7.wireOp",EDGE,"E12.2.7.3"),sQuery(id+"F7.wireOp",EDGE,"E12.2.8.0"),sQuery(id+"F7.wireOp",EDGE,"E12.2.8.1"),sQuery(id+"F7.wireOp",EDGE,"E12.2.8.2"),sQuery(id+"F7.wireOp",EDGE,"E12.2.8.3"),sQuery(id+"F7.wireOp",EDGE,"E12.2.9.0"),sQuery(id+"F7.wireOp",EDGE,"E12.2.9.1"),sQuery(id+"F7.wireOp",EDGE,"E12.2.9.2"),sQuery(id+"F7.wireOp",EDGE,"E12.2.9.3"),sQuery(id+"F7.wireOp",EDGE,"E12.2.10.0"),sQuery(id+"F7.wireOp",EDGE,"E12.2.10.1"),sQuery(id+"F7.wireOp",EDGE,"E12.2.10.2"),sQuery(id+"F7.wireOp",EDGE,"E12.2.10.3"),sQuery(id+"F7.wireOp",EDGE,"E12.2.11.0"),sQuery(id+"F7.wireOp",EDGE,"E12.2.11.1"),sQuery(id+"F7.wireOp",EDGE,"E12.2.11.2"),sQuery(id+"F7.wireOp",EDGE,"E12.2.11.3"),sQuery(id+"F7.wireOp",EDGE,"E12.2.12.0"),sQuery(id+"F7.wireOp",EDGE,"E12.2.12.1"),sQuery(id+"F7.wireOp",EDGE,"E12.2.12.2"),sQuery(id+"F7.wireOp",EDGE,"E12.2.12.3"),sQuery(id+"F7.wireOp",EDGE,"E12.2.13.0"),sQuery(id+"F7.wireOp",EDGE,"E12.2.13.1"),sQuery(id+"F7.wireOp",EDGE,"E12.2.13.2"),sQuery(id+"F7.wireOp",EDGE,"E12.2.13.3"),sQuery(id+"F7.wireOp",EDGE,"E12.2.14.0"),sQuery(id+"F7.wireOp",EDGE,"E12.2.14.1"),sQuery(id+"F7.wireOp",EDGE,"E12.2.14.2"),sQuery(id+"F7.wireOp",EDGE,"E12.2.14.3"),sQuery(id+"F7.wireOp",EDGE,"E12.2.15.0"),sQuery(id+"F7.wireOp",EDGE,"E12.2.15.1"),sQuery(id+"F7.wireOp",EDGE,"E12.2.15.2"),sQuery(id+"F7.wireOp",EDGE,"E12.2.15.3"),sQuery(id+"F7.wireOp",EDGE,"E12.3.0.0"),sQuery(id+"F7.wireOp",EDGE,"E12.3.0.1"),sQuery(id+"F7.wireOp",EDGE,"E12.3.0.2"),sQuery(id+"F7.wireOp",EDGE,"E12.3.0.3"),sQuery(id+"F7.wireOp",EDGE,"E12.3.1.0"),sQuery(id+"F7.wireOp",EDGE,"E12.3.1.1"),sQuery(id+"F7.wireOp",EDGE,"E12.3.1.2"),sQuery(id+"F7.wireOp",EDGE,"E12.3.1.3"),sQuery(id+"F7.wireOp",EDGE,"E12.3.2.0"),sQuery(id+"F7.wireOp",EDGE,"E12.3.2.1"),sQuery(id+"F7.wireOp",EDGE,"E12.3.2.2"),sQuery(id+"F7.wireOp",EDGE,"E12.3.2.3"),sQuery(id+"F7.wireOp",EDGE,"E12.3.3.0"),sQuery(id+"F7.wireOp",EDGE,"E12.3.3.1"),sQuery(id+"F7.wireOp",EDGE,"E12.3.3.2"),sQuery(id+"F7.wireOp",EDGE,"E12.3.3.3"),sQuery(id+"F7.wireOp",EDGE,"E12.3.4.0"),sQuery(id+"F7.wireOp",EDGE,"E12.3.4.1"),sQuery(id+"F7.wireOp",EDGE,"E12.3.4.2"),sQuery(id+"F7.wireOp",EDGE,"E12.3.4.3"),sQuery(id+"F7.wireOp",EDGE,"E12.3.5.0"),sQuery(id+"F7.wireOp",EDGE,"E12.3.5.1"),sQuery(id+"F7.wireOp",EDGE,"E12.3.5.2"),sQuery(id+"F7.wireOp",EDGE,"E12.3.5.3"),sQuery(id+"F7.wireOp",EDGE,"E12.3.6.0"),sQuery(id+"F7.wireOp",EDGE,"E12.3.6.1"),sQuery(id+"F7.wireOp",EDGE,"E12.3.6.2"),sQuery(id+"F7.wireOp",EDGE,"E12.3.6.3"),sQuery(id+"F7.wireOp",EDGE,"E12.3.7.0"),sQuery(id+"F7.wireOp",EDGE,"E12.3.7.1"),sQuery(id+"F7.wireOp",EDGE,"E12.3.7.2"),sQuery(id+"F7.wireOp",EDGE,"E12.3.7.3"),sQuery(id+"F7.wireOp",EDGE,"E12.3.8.0"),sQuery(id+"F7.wireOp",EDGE,"E12.3.8.1"),sQuery(id+"F7.wireOp",EDGE,"E12.3.8.2"),sQuery(id+"F7.wireOp",EDGE,"E12.3.8.3"),sQuery(id+"F7.wireOp",EDGE,"E12.3.9.0"),sQuery(id+"F7.wireOp",EDGE,"E12.3.9.1"),sQuery(id+"F7.wireOp",EDGE,"E12.3.9.2"),sQuery(id+"F7.wireOp",EDGE,"E12.3.9.3"),sQuery(id+"F7.wireOp",EDGE,"E12.3.10.0"),sQuery(id+"F7.wireOp",EDGE,"E12.3.10.1"),sQuery(id+"F7.wireOp",EDGE,"E12.3.10.2"),sQuery(id+"F7.wireOp",EDGE,"E12.3.10.3"),sQuery(id+"F7.wireOp",EDGE,"E12.3.11.0"),sQuery(id+"F7.wireOp",EDGE,"E12.3.11.1"),sQuery(id+"F7.wireOp",EDGE,"E12.3.11.2"),sQuery(id+"F7.wireOp",EDGE,"E12.3.11.3"),sQuery(id+"F7.wireOp",EDGE,"E12.3.12.0"),sQuery(id+"F7.wireOp",EDGE,"E12.3.12.1"),sQuery(id+"F7.wireOp",EDGE,"E12.3.12.2"),sQuery(id+"F7.wireOp",EDGE,"E12.3.12.3"),sQuery(id+"F7.wireOp",EDGE,"E12.3.13.0"),sQuery(id+"F7.wireOp",EDGE,"E12.3.13.1"),sQuery(id+"F7.wireOp",EDGE,"E12.3.13.2"),sQuery(id+"F7.wireOp",EDGE,"E12.3.13.3"),sQuery(id+"F7.wireOp",EDGE,"E12.3.14.0"),sQuery(id+"F7.wireOp",EDGE,"E12.3.14.1"),sQuery(id+"F7.wireOp",EDGE,"E12.3.14.2"),sQuery(id+"F7.wireOp",EDGE,"E12.3.14.3"),sQuery(id+"F7.wireOp",EDGE,"E12.3.15.0"),sQuery(id+"F7.wireOp",EDGE,"E12.3.15.1"),sQuery(id+"F7.wireOp",EDGE,"E12.3.15.2"),sQuery(id+"F7.wireOp",EDGE,"E12.3.15.3"),sQuery(id+"F7.wireOp",EDGE,"E12.4.0.0"),sQuery(id+"F7.wireOp",EDGE,"E12.4.0.1"),sQuery(id+"F7.wireOp",EDGE,"E12.4.0.2"),sQuery(id+"F7.wireOp",EDGE,"E12.4.0.3"),sQuery(id+"F7.wireOp",EDGE,"E12.4.1.0"),sQuery(id+"F7.wireOp",EDGE,"E12.4.1.1"),sQuery(id+"F7.wireOp",EDGE,"E12.4.1.2"),sQuery(id+"F7.wireOp",EDGE,"E12.4.1.3"),sQuery(id+"F7.wireOp",EDGE,"E12.4.2.0"),sQuery(id+"F7.wireOp",EDGE,"E12.4.2.1"),sQuery(id+"F7.wireOp",EDGE,"E12.4.2.2"),sQuery(id+"F7.wireOp",EDGE,"E12.4.2.3"),sQuery(id+"F7.wireOp",EDGE,"E12.4.3.0"),sQuery(id+"F7.wireOp",EDGE,"E12.4.3.1"),sQuery(id+"F7.wireOp",EDGE,"E12.4.3.2"),sQuery(id+"F7.wireOp",EDGE,"E12.4.3.3"),sQuery(id+"F7.wireOp",EDGE,"E12.4.4.0"),sQuery(id+"F7.wireOp",EDGE,"E12.4.4.1"),sQuery(id+"F7.wireOp",EDGE,"E12.4.4.2"),sQuery(id+"F7.wireOp",EDGE,"E12.4.4.3"),sQuery(id+"F7.wireOp",EDGE,"E12.4.5.0"),sQuery(id+"F7.wireOp",EDGE,"E12.4.5.1"),sQuery(id+"F7.wireOp",EDGE,"E12.4.5.2"),sQuery(id+"F7.wireOp",EDGE,"E12.4.5.3"),sQuery(id+"F7.wireOp",EDGE,"E12.4.6.0"),sQuery(id+"F7.wireOp",EDGE,"E12.4.6.1"),sQuery(id+"F7.wireOp",EDGE,"E12.4.6.2"),sQuery(id+"F7.wireOp",EDGE,"E12.4.6.3"),sQuery(id+"F7.wireOp",EDGE,"E12.4.7.0"),sQuery(id+"F7.wireOp",EDGE,"E12.4.7.1"),sQuery(id+"F7.wireOp",EDGE,"E12.4.7.2"),sQuery(id+"F7.wireOp",EDGE,"E12.4.7.3"),sQuery(id+"F7.wireOp",EDGE,"E12.4.8.0"),sQuery(id+"F7.wireOp",EDGE,"E12.4.8.1"),sQuery(id+"F7.wireOp",EDGE,"E12.4.8.2"),sQuery(id+"F7.wireOp",EDGE,"E12.4.8.3"),sQuery(id+"F7.wireOp",EDGE,"E12.4.9.0"),sQuery(id+"F7.wireOp",EDGE,"E12.4.9.1"),sQuery(id+"F7.wireOp",EDGE,"E12.4.9.2"),sQuery(id+"F7.wireOp",EDGE,"E12.4.9.3"),sQuery(id+"F7.wireOp",EDGE,"E12.4.10.0"),sQuery(id+"F7.wireOp",EDGE,"E12.4.10.1"),sQuery(id+"F7.wireOp",EDGE,"E12.4.10.2"),sQuery(id+"F7.wireOp",EDGE,"E12.4.10.3"),sQuery(id+"F7.wireOp",EDGE,"E12.4.11.0"),sQuery(id+"F7.wireOp",EDGE,"E12.4.11.1"),sQuery(id+"F7.wireOp",EDGE,"E12.4.11.2"),sQuery(id+"F7.wireOp",EDGE,"E12.4.11.3"),sQuery(id+"F7.wireOp",EDGE,"E12.4.12.0"),sQuery(id+"F7.wireOp",EDGE,"E12.4.12.1"),sQuery(id+"F7.wireOp",EDGE,"E12.4.12.2"),sQuery(id+"F7.wireOp",EDGE,"E12.4.12.3"),sQuery(id+"F7.wireOp",EDGE,"E12.4.13.0"),sQuery(id+"F7.wireOp",EDGE,"E12.4.13.1"),sQuery(id+"F7.wireOp",EDGE,"E12.4.13.2"),sQuery(id+"F7.wireOp",EDGE,"E12.4.13.3"),sQuery(id+"F7.wireOp",EDGE,"E12.4.14.0"),sQuery(id+"F7.wireOp",EDGE,"E12.4.14.1"),sQuery(id+"F7.wireOp",EDGE,"E12.4.14.2"),sQuery(id+"F7.wireOp",EDGE,"E12.4.14.3"),sQuery(id+"F7.wireOp",EDGE,"E12.4.15.0"),sQuery(id+"F7.wireOp",EDGE,"E12.4.15.1"),sQuery(id+"F7.wireOp",EDGE,"E12.4.15.2"),sQuery(id+"F7.wireOp",EDGE,"E12.4.15.3"),sQuery(id+"F7.wireOp",EDGE,"E12.5.0.0"),sQuery(id+"F7.wireOp",EDGE,"E12.5.0.1"),sQuery(id+"F7.wireOp",EDGE,"E12.5.0.2"),sQuery(id+"F7.wireOp",EDGE,"E12.5.0.3"),sQuery(id+"F7.wireOp",EDGE,"E12.5.1.0"),sQuery(id+"F7.wireOp",EDGE,"E12.5.1.1"),sQuery(id+"F7.wireOp",EDGE,"E12.5.1.2"),sQuery(id+"F7.wireOp",EDGE,"E12.5.1.3"),sQuery(id+"F7.wireOp",EDGE,"E12.5.2.0"),sQuery(id+"F7.wireOp",EDGE,"E12.5.2.1"),sQuery(id+"F7.wireOp",EDGE,"E12.5.2.2"),sQuery(id+"F7.wireOp",EDGE,"E12.5.2.3"),sQuery(id+"F7.wireOp",EDGE,"E12.5.3.0"),sQuery(id+"F7.wireOp",EDGE,"E12.5.3.1"),sQuery(id+"F7.wireOp",EDGE,"E12.5.3.2"),sQuery(id+"F7.wireOp",EDGE,"E12.5.3.3"),sQuery(id+"F7.wireOp",EDGE,"E12.5.4.0"),sQuery(id+"F7.wireOp",EDGE,"E12.5.4.1"),sQuery(id+"F7.wireOp",EDGE,"E12.5.4.2"),sQuery(id+"F7.wireOp",EDGE,"E12.5.4.3"),sQuery(id+"F7.wireOp",EDGE,"E12.5.5.0"),sQuery(id+"F7.wireOp",EDGE,"E12.5.5.1"),sQuery(id+"F7.wireOp",EDGE,"E12.5.5.2"),sQuery(id+"F7.wireOp",EDGE,"E12.5.5.3"),sQuery(id+"F7.wireOp",EDGE,"E12.5.6.0"),sQuery(id+"F7.wireOp",EDGE,"E12.5.6.1"),sQuery(id+"F7.wireOp",EDGE,"E12.5.6.2"),sQuery(id+"F7.wireOp",EDGE,"E12.5.6.3"),sQuery(id+"F7.wireOp",EDGE,"E12.5.7.0"),sQuery(id+"F7.wireOp",EDGE,"E12.5.7.1"),sQuery(id+"F7.wireOp",EDGE,"E12.5.7.2"),sQuery(id+"F7.wireOp",EDGE,"E12.5.7.3"),sQuery(id+"F7.wireOp",EDGE,"E12.5.8.0"),sQuery(id+"F7.wireOp",EDGE,"E12.5.8.1"),sQuery(id+"F7.wireOp",EDGE,"E12.5.8.2"),sQuery(id+"F7.wireOp",EDGE,"E12.5.8.3"),sQuery(id+"F7.wireOp",EDGE,"E12.5.9.0"),sQuery(id+"F7.wireOp",EDGE,"E12.5.9.1"),sQuery(id+"F7.wireOp",EDGE,"E12.5.9.2"),sQuery(id+"F7.wireOp",EDGE,"E12.5.9.3"),sQuery(id+"F7.wireOp",EDGE,"E12.5.10.0"),sQuery(id+"F7.wireOp",EDGE,"E12.5.10.1"),sQuery(id+"F7.wireOp",EDGE,"E12.5.10.2"),sQuery(id+"F7.wireOp",EDGE,"E12.5.10.3"),sQuery(id+"F7.wireOp",EDGE,"E12.5.11.0"),sQuery(id+"F7.wireOp",EDGE,"E12.5.11.1"),sQuery(id+"F7.wireOp",EDGE,"E12.5.11.2"),sQuery(id+"F7.wireOp",EDGE,"E12.5.11.3"),sQuery(id+"F7.wireOp",EDGE,"E12.5.12.0"),sQuery(id+"F7.wireOp",EDGE,"E12.5.12.1"),sQuery(id+"F7.wireOp",EDGE,"E12.5.12.2"),sQuery(id+"F7.wireOp",EDGE,"E12.5.12.3"),sQuery(id+"F7.wireOp",EDGE,"E12.5.13.0"),sQuery(id+"F7.wireOp",EDGE,"E12.5.13.1"),sQuery(id+"F7.wireOp",EDGE,"E12.5.13.2"),sQuery(id+"F7.wireOp",EDGE,"E12.5.13.3"),sQuery(id+"F7.wireOp",EDGE,"E12.5.14.0"),sQuery(id+"F7.wireOp",EDGE,"E12.5.14.1"),sQuery(id+"F7.wireOp",EDGE,"E12.5.14.2"),sQuery(id+"F7.wireOp",EDGE,"E12.5.14.3"),sQuery(id+"F7.wireOp",EDGE,"E12.5.15.0"),sQuery(id+"F7.wireOp",EDGE,"E12.5.15.1"),sQuery(id+"F7.wireOp",EDGE,"E12.5.15.2"),sQuery(id+"F7.wireOp",EDGE,"E12.5.15.3"),sQuery(id+"F7.wireOp",EDGE,"E12.6.0.0"),sQuery(id+"F7.wireOp",EDGE,"E12.6.0.1"),sQuery(id+"F7.wireOp",EDGE,"E12.6.0.2"),sQuery(id+"F7.wireOp",EDGE,"E12.6.0.3"),sQuery(id+"F7.wireOp",EDGE,"E12.6.1.0"),sQuery(id+"F7.wireOp",EDGE,"E12.6.1.1"),sQuery(id+"F7.wireOp",EDGE,"E12.6.1.2"),sQuery(id+"F7.wireOp",EDGE,"E12.6.1.3"),sQuery(id+"F7.wireOp",EDGE,"E12.6.2.0"),sQuery(id+"F7.wireOp",EDGE,"E12.6.2.1"),sQuery(id+"F7.wireOp",EDGE,"E12.6.2.2"),sQuery(id+"F7.wireOp",EDGE,"E12.6.2.3"),sQuery(id+"F7.wireOp",EDGE,"E12.6.3.0"),sQuery(id+"F7.wireOp",EDGE,"E12.6.3.1"),sQuery(id+"F7.wireOp",EDGE,"E12.6.3.2"),sQuery(id+"F7.wireOp",EDGE,"E12.6.3.3"),sQuery(id+"F7.wireOp",EDGE,"E12.6.4.0"),sQuery(id+"F7.wireOp",EDGE,"E12.6.4.1"),sQuery(id+"F7.wireOp",EDGE,"E12.6.4.2"),sQuery(id+"F7.wireOp",EDGE,"E12.6.4.3"),sQuery(id+"F7.wireOp",EDGE,"E12.6.5.0"),sQuery(id+"F7.wireOp",EDGE,"E12.6.5.1"),sQuery(id+"F7.wireOp",EDGE,"E12.6.5.2"),sQuery(id+"F7.wireOp",EDGE,"E12.6.5.3"),sQuery(id+"F7.wireOp",EDGE,"E12.6.6.0"),sQuery(id+"F7.wireOp",EDGE,"E12.6.6.1"),sQuery(id+"F7.wireOp",EDGE,"E12.6.6.2"),sQuery(id+"F7.wireOp",EDGE,"E12.6.6.3"),sQuery(id+"F7.wireOp",EDGE,"E12.6.7.0"),sQuery(id+"F7.wireOp",EDGE,"E12.6.7.1"),sQuery(id+"F7.wireOp",EDGE,"E12.6.7.2"),sQuery(id+"F7.wireOp",EDGE,"E12.6.7.3"),sQuery(id+"F7.wireOp",EDGE,"E12.6.8.0"),sQuery(id+"F7.wireOp",EDGE,"E12.6.8.1"),sQuery(id+"F7.wireOp",EDGE,"E12.6.8.2"),sQuery(id+"F7.wireOp",EDGE,"E12.6.8.3"),sQuery(id+"F7.wireOp",EDGE,"E12.6.9.0"),sQuery(id+"F7.wireOp",EDGE,"E12.6.9.1"),sQuery(id+"F7.wireOp",EDGE,"E12.6.9.2"),sQuery(id+"F7.wireOp",EDGE,"E12.6.9.3"),sQuery(id+"F7.wireOp",EDGE,"E12.6.10.0"),sQuery(id+"F7.wireOp",EDGE,"E12.6.10.1"),sQuery(id+"F7.wireOp",EDGE,"E12.6.10.2"),sQuery(id+"F7.wireOp",EDGE,"E12.6.10.3"),sQuery(id+"F7.wireOp",EDGE,"E12.6.11.0"),sQuery(id+"F7.wireOp",EDGE,"E12.6.11.1"),sQuery(id+"F7.wireOp",EDGE,"E12.6.11.2"),sQuery(id+"F7.wireOp",EDGE,"E12.6.11.3"),sQuery(id+"F7.wireOp",EDGE,"E12.6.12.0"),sQuery(id+"F7.wireOp",EDGE,"E12.6.12.1"),sQuery(id+"F7.wireOp",EDGE,"E12.6.12.2"),sQuery(id+"F7.wireOp",EDGE,"E12.6.12.3"),sQuery(id+"F7.wireOp",EDGE,"E12.6.13.0"),sQuery(id+"F7.wireOp",EDGE,"E12.6.13.1"),sQuery(id+"F7.wireOp",EDGE,"E12.6.13.2"),sQuery(id+"F7.wireOp",EDGE,"E12.6.13.3"),sQuery(id+"F7.wireOp",EDGE,"E12.6.14.0"),sQuery(id+"F7.wireOp",EDGE,"E12.6.14.1"),sQuery(id+"F7.wireOp",EDGE,"E12.6.14.2"),sQuery(id+"F7.wireOp",EDGE,"E12.6.14.3"),sQuery(id+"F7.wireOp",EDGE,"E12.6.15.0"),sQuery(id+"F7.wireOp",EDGE,"E12.6.15.1"),sQuery(id+"F7.wireOp",EDGE,"E12.6.15.2"),sQuery(id+"F7.wireOp",EDGE,"E12.6.15.3"),sQuery(id+"F7.wireOp",EDGE,"E12.7.0.0"),sQuery(id+"F7.wireOp",EDGE,"E12.7.0.1"),sQuery(id+"F7.wireOp",EDGE,"E12.7.0.2"),sQuery(id+"F7.wireOp",EDGE,"E12.7.0.3"),sQuery(id+"F7.wireOp",EDGE,"E12.7.1.0"),sQuery(id+"F7.wireOp",EDGE,"E12.7.1.1"),sQuery(id+"F7.wireOp",EDGE,"E12.7.1.2"),sQuery(id+"F7.wireOp",EDGE,"E12.7.1.3"),sQuery(id+"F7.wireOp",EDGE,"E12.7.2.0"),sQuery(id+"F7.wireOp",EDGE,"E12.7.2.1"),sQuery(id+"F7.wireOp",EDGE,"E12.7.2.2"),sQuery(id+"F7.wireOp",EDGE,"E12.7.2.3"),sQuery(id+"F7.wireOp",EDGE,"E12.7.3.0"),sQuery(id+"F7.wireOp",EDGE,"E12.7.3.1"),sQuery(id+"F7.wireOp",EDGE,"E12.7.3.2"),sQuery(id+"F7.wireOp",EDGE,"E12.7.3.3"),sQuery(id+"F7.wireOp",EDGE,"E12.7.4.0"),sQuery(id+"F7.wireOp",EDGE,"E12.7.4.1"),sQuery(id+"F7.wireOp",EDGE,"E12.7.4.2"),sQuery(id+"F7.wireOp",EDGE,"E12.7.4.3"),sQuery(id+"F7.wireOp",EDGE,"E12.7.5.0"),sQuery(id+"F7.wireOp",EDGE,"E12.7.5.1"),sQuery(id+"F7.wireOp",EDGE,"E12.7.5.2"),sQuery(id+"F7.wireOp",EDGE,"E12.7.5.3"),sQuery(id+"F7.wireOp",EDGE,"E12.7.6.0"),sQuery(id+"F7.wireOp",EDGE,"E12.7.6.1"),sQuery(id+"F7.wireOp",EDGE,"E12.7.6.2"),sQuery(id+"F7.wireOp",EDGE,"E12.7.6.3"),sQuery(id+"F7.wireOp",EDGE,"E12.7.7.0"),sQuery(id+"F7.wireOp",EDGE,"E12.7.7.1"),sQuery(id+"F7.wireOp",EDGE,"E12.7.7.2"),sQuery(id+"F7.wireOp",EDGE,"E12.7.7.3"),sQuery(id+"F7.wireOp",EDGE,"E12.7.8.0"),sQuery(id+"F7.wireOp",EDGE,"E12.7.8.1"),sQuery(id+"F7.wireOp",EDGE,"E12.7.8.2"),sQuery(id+"F7.wireOp",EDGE,"E12.7.8.3"),sQuery(id+"F7.wireOp",EDGE,"E12.7.9.0"),sQuery(id+"F7.wireOp",EDGE,"E12.7.9.1"),sQuery(id+"F7.wireOp",EDGE,"E12.7.9.2"),sQuery(id+"F7.wireOp",EDGE,"E12.7.9.3"),sQuery(id+"F7.wireOp",EDGE,"E12.7.10.0"),sQuery(id+"F7.wireOp",EDGE,"E12.7.10.1"),sQuery(id+"F7.wireOp",EDGE,"E12.7.10.2"),sQuery(id+"F7.wireOp",EDGE,"E12.7.10.3"),sQuery(id+"F7.wireOp",EDGE,"E12.7.11.0"),sQuery(id+"F7.wireOp",EDGE,"E12.7.11.1"),sQuery(id+"F7.wireOp",EDGE,"E12.7.11.2"),sQuery(id+"F7.wireOp",EDGE,"E12.7.11.3"),sQuery(id+"F7.wireOp",EDGE,"E12.7.12.0"),sQuery(id+"F7.wireOp",EDGE,"E12.7.12.1"),sQuery(id+"F7.wireOp",EDGE,"E12.7.12.2"),sQuery(id+"F7.wireOp",EDGE,"E12.7.12.3"),sQuery(id+"F7.wireOp",EDGE,"E12.7.13.0"),sQuery(id+"F7.wireOp",EDGE,"E12.7.13.1"),sQuery(id+"F7.wireOp",EDGE,"E12.7.13.2"),sQuery(id+"F7.wireOp",EDGE,"E12.7.13.3"),sQuery(id+"F7.wireOp",EDGE,"E12.7.14.0"),sQuery(id+"F7.wireOp",EDGE,"E12.7.14.1"),sQuery(id+"F7.wireOp",EDGE,"E12.7.14.2"),sQuery(id+"F7.wireOp",EDGE,"E12.7.14.3"),sQuery(id+"F7.wireOp",EDGE,"E12.7.15.0"),sQuery(id+"F7.wireOp",EDGE,"E12.7.15.1"),sQuery(id+"F7.wireOp",EDGE,"E12.7.15.2"),sQuery(id+"F7.wireOp",EDGE,"E12.7.15.3"),sQuery(id+"F7.wireOp",EDGE,"E12.8.0.0"),sQuery(id+"F7.wireOp",EDGE,"E12.8.0.1"),sQuery(id+"F7.wireOp",EDGE,"E12.8.0.2"),sQuery(id+"F7.wireOp",EDGE,"E12.8.0.3"),sQuery(id+"F7.wireOp",EDGE,"E12.8.1.0"),sQuery(id+"F7.wireOp",EDGE,"E12.8.1.1"),sQuery(id+"F7.wireOp",EDGE,"E12.8.1.2"),sQuery(id+"F7.wireOp",EDGE,"E12.8.1.3"),sQuery(id+"F7.wireOp",EDGE,"E12.8.2.0"),sQuery(id+"F7.wireOp",EDGE,"E12.8.2.1"),sQuery(id+"F7.wireOp",EDGE,"E12.8.2.2"),sQuery(id+"F7.wireOp",EDGE,"E12.8.2.3"),sQuery(id+"F7.wireOp",EDGE,"E12.8.3.0"),sQuery(id+"F7.wireOp",EDGE,"E12.8.3.1"),sQuery(id+"F7.wireOp",EDGE,"E12.8.3.2"),sQuery(id+"F7.wireOp",EDGE,"E12.8.3.3"),sQuery(id+"F7.wireOp",EDGE,"E12.8.4.0"),sQuery(id+"F7.wireOp",EDGE,"E12.8.4.1"),sQuery(id+"F7.wireOp",EDGE,"E12.8.4.2"),sQuery(id+"F7.wireOp",EDGE,"E12.8.4.3"),sQuery(id+"F7.wireOp",EDGE,"E12.8.5.0"),sQuery(id+"F7.wireOp",EDGE,"E12.8.5.1"),sQuery(id+"F7.wireOp",EDGE,"E12.8.5.2"),sQuery(id+"F7.wireOp",EDGE,"E12.8.5.3"),sQuery(id+"F7.wireOp",EDGE,"E12.8.6.0"),sQuery(id+"F7.wireOp",EDGE,"E12.8.6.1"),sQuery(id+"F7.wireOp",EDGE,"E12.8.6.2"),sQuery(id+"F7.wireOp",EDGE,"E12.8.6.3"),sQuery(id+"F7.wireOp",EDGE,"E12.8.7.0"),sQuery(id+"F7.wireOp",EDGE,"E12.8.7.1"),sQuery(id+"F7.wireOp",EDGE,"E12.8.7.2"),sQuery(id+"F7.wireOp",EDGE,"E12.8.7.3"),sQuery(id+"F7.wireOp",EDGE,"E12.8.8.0"),sQuery(id+"F7.wireOp",EDGE,"E12.8.8.1"),sQuery(id+"F7.wireOp",EDGE,"E12.8.8.2"),sQuery(id+"F7.wireOp",EDGE,"E12.8.8.3"),sQuery(id+"F7.wireOp",EDGE,"E12.8.9.0"),sQuery(id+"F7.wireOp",EDGE,"E12.8.9.1"),sQuery(id+"F7.wireOp",EDGE,"E12.8.9.2"),sQuery(id+"F7.wireOp",EDGE,"E12.8.9.3"),sQuery(id+"F7.wireOp",EDGE,"E12.8.10.0"),sQuery(id+"F7.wireOp",EDGE,"E12.8.10.1"),sQuery(id+"F7.wireOp",EDGE,"E12.8.10.2"),sQuery(id+"F7.wireOp",EDGE,"E12.8.10.3"),sQuery(id+"F7.wireOp",EDGE,"E12.8.11.0"),sQuery(id+"F7.wireOp",EDGE,"E12.8.11.1"),sQuery(id+"F7.wireOp",EDGE,"E12.8.11.2"),sQuery(id+"F7.wireOp",EDGE,"E12.8.11.3"),sQuery(id+"F7.wireOp",EDGE,"E12.8.12.0"),sQuery(id+"F7.wireOp",EDGE,"E12.8.12.1"),sQuery(id+"F7.wireOp",EDGE,"E12.8.12.2"),sQuery(id+"F7.wireOp",EDGE,"E12.8.12.3"),sQuery(id+"F7.wireOp",EDGE,"E12.8.13.0"),sQuery(id+"F7.wireOp",EDGE,"E12.8.13.1"),sQuery(id+"F7.wireOp",EDGE,"E12.8.13.2"),sQuery(id+"F7.wireOp",EDGE,"E12.8.13.3"),sQuery(id+"F7.wireOp",EDGE,"E12.8.14.0"),sQuery(id+"F7.wireOp",EDGE,"E12.8.14.1"),sQuery(id+"F7.wireOp",EDGE,"E12.8.14.2"),sQuery(id+"F7.wireOp",EDGE,"E12.8.14.3"),sQuery(id+"F7.wireOp",EDGE,"E12.8.15.0"),sQuery(id+"F7.wireOp",EDGE,"E12.8.15.1"),sQuery(id+"F7.wireOp",EDGE,"E12.8.15.2"),sQuery(id+"F7.wireOp",EDGE,"E12.8.15.3"),sQuery(id+"F7.wireOp",EDGE,"E12.9.0.0"),sQuery(id+"F7.wireOp",EDGE,"E12.9.0.1"),sQuery(id+"F7.wireOp",EDGE,"E12.9.0.2"),sQuery(id+"F7.wireOp",EDGE,"E12.9.0.3"),sQuery(id+"F7.wireOp",EDGE,"E12.9.1.0"),sQuery(id+"F7.wireOp",EDGE,"E12.9.1.1"),sQuery(id+"F7.wireOp",EDGE,"E12.9.1.2"),sQuery(id+"F7.wireOp",EDGE,"E12.9.1.3"),sQuery(id+"F7.wireOp",EDGE,"E12.9.2.0"),sQuery(id+"F7.wireOp",EDGE,"E12.9.2.1"),sQuery(id+"F7.wireOp",EDGE,"E12.9.2.2"),sQuery(id+"F7.wireOp",EDGE,"E12.9.2.3"),sQuery(id+"F7.wireOp",EDGE,"E12.9.3.0"),sQuery(id+"F7.wireOp",EDGE,"E12.9.3.1"),sQuery(id+"F7.wireOp",EDGE,"E12.9.3.2"),sQuery(id+"F7.wireOp",EDGE,"E12.9.3.3"),sQuery(id+"F7.wireOp",EDGE,"E12.9.4.0"),sQuery(id+"F7.wireOp",EDGE,"E12.9.4.1"),sQuery(id+"F7.wireOp",EDGE,"E12.9.4.2"),sQuery(id+"F7.wireOp",EDGE,"E12.9.4.3"),sQuery(id+"F7.wireOp",EDGE,"E12.9.5.0"),sQuery(id+"F7.wireOp",EDGE,"E12.9.5.1"),sQuery(id+"F7.wireOp",EDGE,"E12.9.5.2"),sQuery(id+"F7.wireOp",EDGE,"E12.9.5.3"),sQuery(id+"F7.wireOp",EDGE,"E12.9.6.0"),sQuery(id+"F7.wireOp",EDGE,"E12.9.6.1"),sQuery(id+"F7.wireOp",EDGE,"E12.9.6.2"),sQuery(id+"F7.wireOp",EDGE,"E12.9.6.3"),sQuery(id+"F7.wireOp",EDGE,"E12.9.7.0"),sQuery(id+"F7.wireOp",EDGE,"E12.9.7.1"),sQuery(id+"F7.wireOp",EDGE,"E12.9.7.2"),sQuery(id+"F7.wireOp",EDGE,"E12.9.7.3"),sQuery(id+"F7.wireOp",EDGE,"E12.9.8.0"),sQuery(id+"F7.wireOp",EDGE,"E12.9.8.1"),sQuery(id+"F7.wireOp",EDGE,"E12.9.8.2"),sQuery(id+"F7.wireOp",EDGE,"E12.9.8.3"),sQuery(id+"F7.wireOp",EDGE,"E12.9.9.0"),sQuery(id+"F7.wireOp",EDGE,"E12.9.9.1"),sQuery(id+"F7.wireOp",EDGE,"E12.9.9.2"),sQuery(id+"F7.wireOp",EDGE,"E12.9.9.3"),sQuery(id+"F7.wireOp",EDGE,"E12.9.10.0"),sQuery(id+"F7.wireOp",EDGE,"E12.9.10.1"),sQuery(id+"F7.wireOp",EDGE,"E12.9.10.2"),sQuery(id+"F7.wireOp",EDGE,"E12.9.10.3"),sQuery(id+"F7.wireOp",EDGE,"E12.9.11.0"),sQuery(id+"F7.wireOp",EDGE,"E12.9.11.1"),sQuery(id+"F7.wireOp",EDGE,"E12.9.11.2"),sQuery(id+"F7.wireOp",EDGE,"E12.9.11.3"),sQuery(id+"F7.wireOp",EDGE,"E12.9.12.0"),sQuery(id+"F7.wireOp",EDGE,"E12.9.12.1"),sQuery(id+"F7.wireOp",EDGE,"E12.9.12.2"),sQuery(id+"F7.wireOp",EDGE,"E12.9.12.3"),sQuery(id+"F7.wireOp",EDGE,"E12.9.13.0"),sQuery(id+"F7.wireOp",EDGE,"E12.9.13.1"),sQuery(id+"F7.wireOp",EDGE,"E12.9.13.2"),sQuery(id+"F7.wireOp",EDGE,"E12.9.13.3"),sQuery(id+"F7.wireOp",EDGE,"E12.9.14.0"),sQuery(id+"F7.wireOp",EDGE,"E12.9.14.1"),sQuery(id+"F7.wireOp",EDGE,"E12.9.14.2"),sQuery(id+"F7.wireOp",EDGE,"E12.9.14.3"),sQuery(id+"F7.wireOp",EDGE,"E12.9.15.0"),sQuery(id+"F7.wireOp",EDGE,"E12.9.15.1"),sQuery(id+"F7.wireOp",EDGE,"E12.9.15.2"),sQuery(id+"F7.wireOp",EDGE,"E12.9.15.3"),sQuery(id+"F7.wireOp",EDGE,"E12.10.0.0"),sQuery(id+"F7.wireOp",EDGE,"E12.10.0.1"),sQuery(id+"F7.wireOp",EDGE,"E12.10.0.2"),sQuery(id+"F7.wireOp",EDGE,"E12.10.0.3"),sQuery(id+"F7.wireOp",EDGE,"E12.10.1.0"),sQuery(id+"F7.wireOp",EDGE,"E12.10.1.1"),sQuery(id+"F7.wireOp",EDGE,"E12.10.1.2"),sQuery(id+"F7.wireOp",EDGE,"E12.10.1.3"),sQuery(id+"F7.wireOp",EDGE,"E12.10.2.0"),sQuery(id+"F7.wireOp",EDGE,"E12.10.2.1"),sQuery(id+"F7.wireOp",EDGE,"E12.10.2.2"),sQuery(id+"F7.wireOp",EDGE,"E12.10.2.3"),sQuery(id+"F7.wireOp",EDGE,"E12.10.3.0"),sQuery(id+"F7.wireOp",EDGE,"E12.10.3.1"),sQuery(id+"F7.wireOp",EDGE,"E12.10.3.2"),sQuery(id+"F7.wireOp",EDGE,"E12.10.3.3"),sQuery(id+"F7.wireOp",EDGE,"E12.10.4.0"),sQuery(id+"F7.wireOp",EDGE,"E12.10.4.1"),sQuery(id+"F7.wireOp",EDGE,"E12.10.4.2"),sQuery(id+"F7.wireOp",EDGE,"E12.10.4.3"),sQuery(id+"F7.wireOp",EDGE,"E12.10.5.0"),sQuery(id+"F7.wireOp",EDGE,"E12.10.5.1"),sQuery(id+"F7.wireOp",EDGE,"E12.10.5.2"),sQuery(id+"F7.wireOp",EDGE,"E12.10.5.3"),sQuery(id+"F7.wireOp",EDGE,"E12.10.6.0"),sQuery(id+"F7.wireOp",EDGE,"E12.10.6.1"),sQuery(id+"F7.wireOp",EDGE,"E12.10.6.2"),sQuery(id+"F7.wireOp",EDGE,"E12.10.6.3"),sQuery(id+"F7.wireOp",EDGE,"E12.10.7.0"),sQuery(id+"F7.wireOp",EDGE,"E12.10.7.1"),sQuery(id+"F7.wireOp",EDGE,"E12.10.7.2"),sQuery(id+"F7.wireOp",EDGE,"E12.10.7.3"),sQuery(id+"F7.wireOp",EDGE,"E12.10.8.0"),sQuery(id+"F7.wireOp",EDGE,"E12.10.8.1"),sQuery(id+"F7.wireOp",EDGE,"E12.10.8.2"),sQuery(id+"F7.wireOp",EDGE,"E12.10.8.3"),sQuery(id+"F7.wireOp",EDGE,"E12.10.9.0"),sQuery(id+"F7.wireOp",EDGE,"E12.10.9.1"),sQuery(id+"F7.wireOp",EDGE,"E12.10.9.2"),sQuery(id+"F7.wireOp",EDGE,"E12.10.9.3"),sQuery(id+"F7.wireOp",EDGE,"E12.10.10.0"),sQuery(id+"F7.wireOp",EDGE,"E12.10.10.1"),sQuery(id+"F7.wireOp",EDGE,"E12.10.10.2"),sQuery(id+"F7.wireOp",EDGE,"E12.10.10.3"),sQuery(id+"F7.wireOp",EDGE,"E12.10.11.0"),sQuery(id+"F7.wireOp",EDGE,"E12.10.11.1"),sQuery(id+"F7.wireOp",EDGE,"E12.10.11.2"),sQuery(id+"F7.wireOp",EDGE,"E12.10.11.3"),sQuery(id+"F7.wireOp",EDGE,"E12.10.12.0"),sQuery(id+"F7.wireOp",EDGE,"E12.10.12.1"),sQuery(id+"F7.wireOp",EDGE,"E12.10.12.2"),sQuery(id+"F7.wireOp",EDGE,"E12.10.12.3"),sQuery(id+"F7.wireOp",EDGE,"E12.10.13.0"),sQuery(id+"F7.wireOp",EDGE,"E12.10.13.1"),sQuery(id+"F7.wireOp",EDGE,"E12.10.13.2"),sQuery(id+"F7.wireOp",EDGE,"E12.10.13.3"),sQuery(id+"F7.wireOp",EDGE,"E12.10.14.0"),sQuery(id+"F7.wireOp",EDGE,"E12.10.14.1"),sQuery(id+"F7.wireOp",EDGE,"E12.10.14.2"),sQuery(id+"F7.wireOp",EDGE,"E12.10.14.3"),sQuery(id+"F7.wireOp",EDGE,"E12.10.15.0"),sQuery(id+"F7.wireOp",EDGE,"E12.10.15.1"),sQuery(id+"F7.wireOp",EDGE,"E12.10.15.2"),sQuery(id+"F7.wireOp",EDGE,"E12.10.15.3"),sQuery(id+"F7.wireOp",EDGE,"E12.11.0.0"),sQuery(id+"F7.wireOp",EDGE,"E12.11.0.1"),sQuery(id+"F7.wireOp",EDGE,"E12.11.0.2"),sQuery(id+"F7.wireOp",EDGE,"E12.11.0.3"),sQuery(id+"F7.wireOp",EDGE,"E12.11.1.0"),sQuery(id+"F7.wireOp",EDGE,"E12.11.1.1"),sQuery(id+"F7.wireOp",EDGE,"E12.11.1.2"),sQuery(id+"F7.wireOp",EDGE,"E12.11.1.3"),sQuery(id+"F7.wireOp",EDGE,"E12.11.2.0"),sQuery(id+"F7.wireOp",EDGE,"E12.11.2.1"),sQuery(id+"F7.wireOp",EDGE,"E12.11.2.2"),sQuery(id+"F7.wireOp",EDGE,"E12.11.2.3"),sQuery(id+"F7.wireOp",EDGE,"E12.11.3.0"),sQuery(id+"F7.wireOp",EDGE,"E12.11.3.1"),sQuery(id+"F7.wireOp",EDGE,"E12.11.3.2"),sQuery(id+"F7.wireOp",EDGE,"E12.11.3.3"),sQuery(id+"F7.wireOp",EDGE,"E12.11.4.0"),sQuery(id+"F7.wireOp",EDGE,"E12.11.4.1"),sQuery(id+"F7.wireOp",EDGE,"E12.11.4.2"),sQuery(id+"F7.wireOp",EDGE,"E12.11.4.3"),sQuery(id+"F7.wireOp",EDGE,"E12.11.5.0"),sQuery(id+"F7.wireOp",EDGE,"E12.11.5.1"),sQuery(id+"F7.wireOp",EDGE,"E12.11.5.2"),sQuery(id+"F7.wireOp",EDGE,"E12.11.5.3"),sQuery(id+"F7.wireOp",EDGE,"E12.11.6.0"),sQuery(id+"F7.wireOp",EDGE,"E12.11.6.1"),sQuery(id+"F7.wireOp",EDGE,"E12.11.6.2"),sQuery(id+"F7.wireOp",EDGE,"E12.11.6.3"),sQuery(id+"F7.wireOp",EDGE,"E12.11.7.0"),sQuery(id+"F7.wireOp",EDGE,"E12.11.7.1"),sQuery(id+"F7.wireOp",EDGE,"E12.11.7.2"),sQuery(id+"F7.wireOp",EDGE,"E12.11.7.3"),sQuery(id+"F7.wireOp",EDGE,"E12.11.8.0"),sQuery(id+"F7.wireOp",EDGE,"E12.11.8.1"),sQuery(id+"F7.wireOp",EDGE,"E12.11.8.2"),sQuery(id+"F7.wireOp",EDGE,"E12.11.8.3"),sQuery(id+"F7.wireOp",EDGE,"E12.11.9.0"),sQuery(id+"F7.wireOp",EDGE,"E12.11.9.1"),sQuery(id+"F7.wireOp",EDGE,"E12.11.9.2"),sQuery(id+"F7.wireOp",EDGE,"E12.11.9.3"),sQuery(id+"F7.wireOp",EDGE,"E12.11.10.0"),sQuery(id+"F7.wireOp",EDGE,"E12.11.10.1"),sQuery(id+"F7.wireOp",EDGE,"E12.11.10.2"),sQuery(id+"F7.wireOp",EDGE,"E12.11.10.3"),sQuery(id+"F7.wireOp",EDGE,"E12.11.11.0"),sQuery(id+"F7.wireOp",EDGE,"E12.11.11.1"),sQuery(id+"F7.wireOp",EDGE,"E12.11.11.2"),sQuery(id+"F7.wireOp",EDGE,"E12.11.11.3"),sQuery(id+"F7.wireOp",EDGE,"E12.11.12.0"),sQuery(id+"F7.wireOp",EDGE,"E12.11.12.1"),sQuery(id+"F7.wireOp",EDGE,"E12.11.12.2"),sQuery(id+"F7.wireOp",EDGE,"E12.11.12.3"),sQuery(id+"F7.wireOp",EDGE,"E12.11.13.0"),sQuery(id+"F7.wireOp",EDGE,"E12.11.13.1"),sQuery(id+"F7.wireOp",EDGE,"E12.11.13.2"),sQuery(id+"F7.wireOp",EDGE,"E12.11.13.3"),sQuery(id+"F7.wireOp",EDGE,"E12.11.14.0"),sQuery(id+"F7.wireOp",EDGE,"E12.11.14.1"),sQuery(id+"F7.wireOp",EDGE,"E12.11.14.2"),sQuery(id+"F7.wireOp",EDGE,"E12.11.14.3"),sQuery(id+"F7.wireOp",EDGE,"E12.11.15.0"),sQuery(id+"F7.wireOp",EDGE,"E12.11.15.1"),sQuery(id+"F7.wireOp",EDGE,"E12.11.15.2"),sQuery(id+"F7.wireOp",EDGE,"E12.11.15.3"),sQuery(id+"F7.wireOp",EDGE,"E12.12.0.0"),sQuery(id+"F7.wireOp",EDGE,"E12.12.0.1"),sQuery(id+"F7.wireOp",EDGE,"E12.12.0.2"),sQuery(id+"F7.wireOp",EDGE,"E12.12.0.3"),sQuery(id+"F7.wireOp",EDGE,"E12.12.1.0"),sQuery(id+"F7.wireOp",EDGE,"E12.12.1.1"),sQuery(id+"F7.wireOp",EDGE,"E12.12.1.2"),sQuery(id+"F7.wireOp",EDGE,"E12.12.1.3"),sQuery(id+"F7.wireOp",EDGE,"E12.12.2.0"),sQuery(id+"F7.wireOp",EDGE,"E12.12.2.1"),sQuery(id+"F7.wireOp",EDGE,"E12.12.2.2"),sQuery(id+"F7.wireOp",EDGE,"E12.12.2.3"),sQuery(id+"F7.wireOp",EDGE,"E12.12.3.0"),sQuery(id+"F7.wireOp",EDGE,"E12.12.3.1"),sQuery(id+"F7.wireOp",EDGE,"E12.12.3.2"),sQuery(id+"F7.wireOp",EDGE,"E12.12.3.3"),sQuery(id+"F7.wireOp",EDGE,"E12.12.4.0"),sQuery(id+"F7.wireOp",EDGE,"E12.12.4.1"),sQuery(id+"F7.wireOp",EDGE,"E12.12.4.2"),sQuery(id+"F7.wireOp",EDGE,"E12.12.4.3"),sQuery(id+"F7.wireOp",EDGE,"E12.12.5.0"),sQuery(id+"F7.wireOp",EDGE,"E12.12.5.1"),sQuery(id+"F7.wireOp",EDGE,"E12.12.5.2"),sQuery(id+"F7.wireOp",EDGE,"E12.12.5.3"),sQuery(id+"F7.wireOp",EDGE,"E12.12.6.0"),sQuery(id+"F7.wireOp",EDGE,"E12.12.6.1"),sQuery(id+"F7.wireOp",EDGE,"E12.12.6.2"),sQuery(id+"F7.wireOp",EDGE,"E12.12.6.3"),sQuery(id+"F7.wireOp",EDGE,"E12.12.7.0"),sQuery(id+"F7.wireOp",EDGE,"E12.12.7.1"),sQuery(id+"F7.wireOp",EDGE,"E12.12.7.2"),sQuery(id+"F7.wireOp",EDGE,"E12.12.7.3"),sQuery(id+"F7.wireOp",EDGE,"E12.12.8.0"),sQuery(id+"F7.wireOp",EDGE,"E12.12.8.1"),sQuery(id+"F7.wireOp",EDGE,"E12.12.8.2"),sQuery(id+"F7.wireOp",EDGE,"E12.12.8.3"),sQuery(id+"F7.wireOp",EDGE,"E12.12.9.0"),sQuery(id+"F7.wireOp",EDGE,"E12.12.9.1"),sQuery(id+"F7.wireOp",EDGE,"E12.12.9.2"),sQuery(id+"F7.wireOp",EDGE,"E12.12.9.3"),sQuery(id+"F7.wireOp",EDGE,"E12.12.10.0"),sQuery(id+"F7.wireOp",EDGE,"E12.12.10.1"),sQuery(id+"F7.wireOp",EDGE,"E12.12.10.2"),sQuery(id+"F7.wireOp",EDGE,"E12.12.10.3"),sQuery(id+"F7.wireOp",EDGE,"E12.12.11.0"),sQuery(id+"F7.wireOp",EDGE,"E12.12.11.1"),sQuery(id+"F7.wireOp",EDGE,"E12.12.11.2"),sQuery(id+"F7.wireOp",EDGE,"E12.12.11.3"),sQuery(id+"F7.wireOp",EDGE,"E12.12.12.0"),sQuery(id+"F7.wireOp",EDGE,"E12.12.12.1"),sQuery(id+"F7.wireOp",EDGE,"E12.12.12.2"),sQuery(id+"F7.wireOp",EDGE,"E12.12.12.3"),sQuery(id+"F7.wireOp",EDGE,"E12.12.13.0"),sQuery(id+"F7.wireOp",EDGE,"E12.12.13.1"),sQuery(id+"F7.wireOp",EDGE,"E12.12.13.2"),sQuery(id+"F7.wireOp",EDGE,"E12.12.13.3"),sQuery(id+"F7.wireOp",EDGE,"E12.12.14.0"),sQuery(id+"F7.wireOp",EDGE,"E12.12.14.1"),sQuery(id+"F7.wireOp",EDGE,"E12.12.14.2"),sQuery(id+"F7.wireOp",EDGE,"E12.12.14.3"),sQuery(id+"F7.wireOp",EDGE,"E12.12.15.0"),sQuery(id+"F7.wireOp",EDGE,"E12.12.15.1"),sQuery(id+"F7.wireOp",EDGE,"E12.12.15.2"),sQuery(id+"F7.wireOp",EDGE,"E12.12.15.3"),sQuery(id+"F7.wireOp",EDGE,"E12.13.0.0"),sQuery(id+"F7.wireOp",EDGE,"E12.13.0.1"),sQuery(id+"F7.wireOp",EDGE,"E12.13.0.2"),sQuery(id+"F7.wireOp",EDGE,"E12.13.0.3"),sQuery(id+"F7.wireOp",EDGE,"E12.13.1.0"),sQuery(id+"F7.wireOp",EDGE,"E12.13.1.1"),sQuery(id+"F7.wireOp",EDGE,"E12.13.1.2"),sQuery(id+"F7.wireOp",EDGE,"E12.13.1.3"),sQuery(id+"F7.wireOp",EDGE,"E12.13.2.0"),sQuery(id+"F7.wireOp",EDGE,"E12.13.2.1"),sQuery(id+"F7.wireOp",EDGE,"E12.13.2.2"),sQuery(id+"F7.wireOp",EDGE,"E12.13.2.3"),sQuery(id+"F7.wireOp",EDGE,"E12.13.3.0"),sQuery(id+"F7.wireOp",EDGE,"E12.13.3.1"),sQuery(id+"F7.wireOp",EDGE,"E12.13.3.2"),sQuery(id+"F7.wireOp",EDGE,"E12.13.3.3"),sQuery(id+"F7.wireOp",EDGE,"E12.13.4.0"),sQuery(id+"F7.wireOp",EDGE,"E12.13.4.1"),sQuery(id+"F7.wireOp",EDGE,"E12.13.4.2"),sQuery(id+"F7.wireOp",EDGE,"E12.13.4.3"),sQuery(id+"F7.wireOp",EDGE,"E12.13.5.0"),sQuery(id+"F7.wireOp",EDGE,"E12.13.5.1"),sQuery(id+"F7.wireOp",EDGE,"E12.13.5.2"),sQuery(id+"F7.wireOp",EDGE,"E12.13.5.3"),sQuery(id+"F7.wireOp",EDGE,"E12.13.6.0"),sQuery(id+"F7.wireOp",EDGE,"E12.13.6.1"),sQuery(id+"F7.wireOp",EDGE,"E12.13.6.2"),sQuery(id+"F7.wireOp",EDGE,"E12.13.6.3"),sQuery(id+"F7.wireOp",EDGE,"E12.13.7.0"),sQuery(id+"F7.wireOp",EDGE,"E12.13.7.1"),sQuery(id+"F7.wireOp",EDGE,"E12.13.7.2"),sQuery(id+"F7.wireOp",EDGE,"E12.13.7.3"),sQuery(id+"F7.wireOp",EDGE,"E12.13.8.0"),sQuery(id+"F7.wireOp",EDGE,"E12.13.8.1"),sQuery(id+"F7.wireOp",EDGE,"E12.13.8.2"),sQuery(id+"F7.wireOp",EDGE,"E12.13.8.3"),sQuery(id+"F7.wireOp",EDGE,"E12.13.9.0"),sQuery(id+"F7.wireOp",EDGE,"E12.13.9.1"),sQuery(id+"F7.wireOp",EDGE,"E12.13.9.2"),sQuery(id+"F7.wireOp",EDGE,"E12.13.9.3"),sQuery(id+"F7.wireOp",EDGE,"E12.13.10.0"),sQuery(id+"F7.wireOp",EDGE,"E12.13.10.1"),sQuery(id+"F7.wireOp",EDGE,"E12.13.10.2"),sQuery(id+"F7.wireOp",EDGE,"E12.13.10.3"),sQuery(id+"F7.wireOp",EDGE,"E12.13.11.0"),sQuery(id+"F7.wireOp",EDGE,"E12.13.11.1"),sQuery(id+"F7.wireOp",EDGE,"E12.13.11.2"),sQuery(id+"F7.wireOp",EDGE,"E12.13.11.3"),sQuery(id+"F7.wireOp",EDGE,"E12.13.12.0"),sQuery(id+"F7.wireOp",EDGE,"E12.13.12.1"),sQuery(id+"F7.wireOp",EDGE,"E12.13.12.2"),sQuery(id+"F7.wireOp",EDGE,"E12.13.12.3"),sQuery(id+"F7.wireOp",EDGE,"E12.13.13.0"),sQuery(id+"F7.wireOp",EDGE,"E12.13.13.1"),sQuery(id+"F7.wireOp",EDGE,"E12.13.13.2"),sQuery(id+"F7.wireOp",EDGE,"E12.13.13.3"),sQuery(id+"F7.wireOp",EDGE,"E12.13.14.0"),sQuery(id+"F7.wireOp",EDGE,"E12.13.14.1"),sQuery(id+"F7.wireOp",EDGE,"E12.13.14.2"),sQuery(id+"F7.wireOp",EDGE,"E12.13.14.3"),sQuery(id+"F7.wireOp",EDGE,"E12.13.15.0"),sQuery(id+"F7.wireOp",EDGE,"E12.13.15.1"),sQuery(id+"F7.wireOp",EDGE,"E12.13.15.2"),sQuery(id+"F7.wireOp",EDGE,"E12.13.15.3"),sQuery(id+"F7.wireOp",EDGE,"E12.14.0.0"),sQuery(id+"F7.wireOp",EDGE,"E12.14.0.1"),sQuery(id+"F7.wireOp",EDGE,"E12.14.0.2"),sQuery(id+"F7.wireOp",EDGE,"E12.14.0.3"),sQuery(id+"F7.wireOp",EDGE,"E12.14.1.0"),sQuery(id+"F7.wireOp",EDGE,"E12.14.1.1"),sQuery(id+"F7.wireOp",EDGE,"E12.14.1.2"),sQuery(id+"F7.wireOp",EDGE,"E12.14.1.3"),sQuery(id+"F7.wireOp",EDGE,"E12.14.2.0"),sQuery(id+"F7.wireOp",EDGE,"E12.14.2.1"),sQuery(id+"F7.wireOp",EDGE,"E12.14.2.2"),sQuery(id+"F7.wireOp",EDGE,"E12.14.2.3"),sQuery(id+"F7.wireOp",EDGE,"E12.14.3.0"),sQuery(id+"F7.wireOp",EDGE,"E12.14.3.1"),sQuery(id+"F7.wireOp",EDGE,"E12.14.3.2"),sQuery(id+"F7.wireOp",EDGE,"E12.14.3.3"),sQuery(id+"F7.wireOp",EDGE,"E12.14.4.0"),sQuery(id+"F7.wireOp",EDGE,"E12.14.4.1"),sQuery(id+"F7.wireOp",EDGE,"E12.14.4.2"),sQuery(id+"F7.wireOp",EDGE,"E12.14.4.3"),sQuery(id+"F7.wireOp",EDGE,"E12.14.5.0"),sQuery(id+"F7.wireOp",EDGE,"E12.14.5.1"),sQuery(id+"F7.wireOp",EDGE,"E12.14.5.2"),sQuery(id+"F7.wireOp",EDGE,"E12.14.5.3"),sQuery(id+"F7.wireOp",EDGE,"E12.14.6.0"),sQuery(id+"F7.wireOp",EDGE,"E12.14.6.1"),sQuery(id+"F7.wireOp",EDGE,"E12.14.6.2"),sQuery(id+"F7.wireOp",EDGE,"E12.14.6.3"),sQuery(id+"F7.wireOp",EDGE,"E12.14.7.0"),sQuery(id+"F7.wireOp",EDGE,"E12.14.7.1"),sQuery(id+"F7.wireOp",EDGE,"E12.14.7.2"),sQuery(id+"F7.wireOp",EDGE,"E12.14.7.3"),sQuery(id+"F7.wireOp",EDGE,"E12.14.8.0"),sQuery(id+"F7.wireOp",EDGE,"E12.14.8.1"),sQuery(id+"F7.wireOp",EDGE,"E12.14.8.2"),sQuery(id+"F7.wireOp",EDGE,"E12.14.8.3"),sQuery(id+"F7.wireOp",EDGE,"E12.14.9.0"),sQuery(id+"F7.wireOp",EDGE,"E12.14.9.1"),sQuery(id+"F7.wireOp",EDGE,"E12.14.9.2"),sQuery(id+"F7.wireOp",EDGE,"E12.14.9.3"),sQuery(id+"F7.wireOp",EDGE,"E12.14.10.0"),sQuery(id+"F7.wireOp",EDGE,"E12.14.10.1"),sQuery(id+"F7.wireOp",EDGE,"E12.14.10.2"),sQuery(id+"F7.wireOp",EDGE,"E12.14.10.3"),sQuery(id+"F7.wireOp",EDGE,"E12.14.11.0"),sQuery(id+"F7.wireOp",EDGE,"E12.14.11.1"),sQuery(id+"F7.wireOp",EDGE,"E12.14.11.2"),sQuery(id+"F7.wireOp",EDGE,"E12.14.11.3"),sQuery(id+"F7.wireOp",EDGE,"E12.14.12.0"),sQuery(id+"F7.wireOp",EDGE,"E12.14.12.1"),sQuery(id+"F7.wireOp",EDGE,"E12.14.12.2"),sQuery(id+"F7.wireOp",EDGE,"E12.14.12.3"),sQuery(id+"F7.wireOp",EDGE,"E12.14.13.0"),sQuery(id+"F7.wireOp",EDGE,"E12.14.13.1"),sQuery(id+"F7.wireOp",EDGE,"E12.14.13.2"),sQuery(id+"F7.wireOp",EDGE,"E12.14.13.3"),sQuery(id+"F7.wireOp",EDGE,"E12.14.14.0"),sQuery(id+"F7.wireOp",EDGE,"E12.14.14.1"),sQuery(id+"F7.wireOp",EDGE,"E12.14.14.2"),sQuery(id+"F7.wireOp",EDGE,"E12.14.14.3"),sQuery(id+"F7.wireOp",EDGE,"E12.14.15.0"),sQuery(id+"F7.wireOp",EDGE,"E12.14.15.1"),sQuery(id+"F7.wireOp",EDGE,"E12.14.15.2"),sQuery(id+"F7.wireOp",EDGE,"E12.14.15.3"),sQuery(id+"F7.wireOp",EDGE,"E12.15.0.0"),sQuery(id+"F7.wireOp",EDGE,"E12.15.0.1"),sQuery(id+"F7.wireOp",EDGE,"E12.15.0.2"),sQuery(id+"F7.wireOp",EDGE,"E12.15.0.3"),sQuery(id+"F7.wireOp",EDGE,"E12.15.1.0"),sQuery(id+"F7.wireOp",EDGE,"E12.15.1.1"),sQuery(id+"F7.wireOp",EDGE,"E12.15.1.2"),sQuery(id+"F7.wireOp",EDGE,"E12.15.1.3"),sQuery(id+"F7.wireOp",EDGE,"E12.15.2.0"),sQuery(id+"F7.wireOp",EDGE,"E12.15.2.1"),sQuery(id+"F7.wireOp",EDGE,"E12.15.2.2"),sQuery(id+"F7.wireOp",EDGE,"E12.15.2.3"),sQuery(id+"F7.wireOp",EDGE,"E12.15.3.0"),sQuery(id+"F7.wireOp",EDGE,"E12.15.3.1"),sQuery(id+"F7.wireOp",EDGE,"E12.15.3.2"),sQuery(id+"F7.wireOp",EDGE,"E12.15.3.3"),sQuery(id+"F7.wireOp",EDGE,"E12.15.4.0"),sQuery(id+"F7.wireOp",EDGE,"E12.15.4.1"),sQuery(id+"F7.wireOp",EDGE,"E12.15.4.2"),sQuery(id+"F7.wireOp",EDGE,"E12.15.4.3"),sQuery(id+"F7.wireOp",EDGE,"E12.15.5.0"),sQuery(id+"F7.wireOp",EDGE,"E12.15.5.1"),sQuery(id+"F7.wireOp",EDGE,"E12.15.5.2"),sQuery(id+"F7.wireOp",EDGE,"E12.15.5.3"),sQuery(id+"F7.wireOp",EDGE,"E12.15.6.0"),sQuery(id+"F7.wireOp",EDGE,"E12.15.6.1"),sQuery(id+"F7.wireOp",EDGE,"E12.15.6.2"),sQuery(id+"F7.wireOp",EDGE,"E12.15.6.3"),sQuery(id+"F7.wireOp",EDGE,"E12.15.7.0"),sQuery(id+"F7.wireOp",EDGE,"E12.15.7.1"),sQuery(id+"F7.wireOp",EDGE,"E12.15.7.2"),sQuery(id+"F7.wireOp",EDGE,"E12.15.7.3"),sQuery(id+"F7.wireOp",EDGE,"E12.15.8.0"),sQuery(id+"F7.wireOp",EDGE,"E12.15.8.1"),sQuery(id+"F7.wireOp",EDGE,"E12.15.8.2"),sQuery(id+"F7.wireOp",EDGE,"E12.15.8.3"),sQuery(id+"F7.wireOp",EDGE,"E12.15.9.0"),sQuery(id+"F7.wireOp",EDGE,"E12.15.9.1"),sQuery(id+"F7.wireOp",EDGE,"E12.15.9.2"),sQuery(id+"F7.wireOp",EDGE,"E12.15.9.3"),sQuery(id+"F7.wireOp",EDGE,"E12.15.10.0"),sQuery(id+"F7.wireOp",EDGE,"E12.15.10.1"),sQuery(id+"F7.wireOp",EDGE,"E12.15.10.2"),sQuery(id+"F7.wireOp",EDGE,"E12.15.10.3"),sQuery(id+"F7.wireOp",EDGE,"E12.15.11.0"),sQuery(id+"F7.wireOp",EDGE,"E12.15.11.1"),sQuery(id+"F7.wireOp",EDGE,"E12.15.11.2"),sQuery(id+"F7.wireOp",EDGE,"E12.15.11.3"),sQuery(id+"F7.wireOp",EDGE,"E12.15.12.0"),sQuery(id+"F7.wireOp",EDGE,"E12.15.12.1"),sQuery(id+"F7.wireOp",EDGE,"E12.15.12.2"),sQuery(id+"F7.wireOp",EDGE,"E12.15.12.3"),sQuery(id+"F7.wireOp",EDGE,"E12.15.13.0"),sQuery(id+"F7.wireOp",EDGE,"E12.15.13.1"),sQuery(id+"F7.wireOp",EDGE,"E12.15.13.2"),sQuery(id+"F7.wireOp",EDGE,"E12.15.13.3"),sQuery(id+"F7.wireOp",EDGE,"E12.15.14.0"),sQuery(id+"F7.wireOp",EDGE,"E12.15.14.1"),sQuery(id+"F7.wireOp",EDGE,"E12.15.14.2"),sQuery(id+"F7.wireOp",EDGE,"E12.15.14.3"),sQuery(id+"F7.wireOp",EDGE,"E12.15.15.0"),sQuery(id+"F7.wireOp",EDGE,"E12.15.15.1"),sQuery(id+"F7.wireOp",EDGE,"E12.15.15.2"),sQuery(id+"F7.wireOp",EDGE,"E12.15.15.3")])]});
            var Q3;
            Q3=makeQuery(id+"F4.opExtrude","SWEPT_BODY",BODY,{"disambiguationData":[OSD([sQuery(id+"F0.wireOp",EDGE,"E0.bottom"),sQuery(id+"F0.wireOp",EDGE,"E0.top"),sQuery(id+"F0.wireOp",EDGE,"E0.left"),sQuery(id+"F0.wireOp",EDGE,"E0.right"),sQuery(id+"F0.wireOp",EDGE,"E2.bottom"),sQuery(id+"F0.wireOp",EDGE,"E2.top"),sQuery(id+"F0.wireOp",EDGE,"E2.left"),sQuery(id+"F0.wireOp",EDGE,"E2.right"),sQuery(id+"F0.wireOp",EDGE,"E3.0.1.0"),sQuery(id+"F0.wireOp",EDGE,"E3.0.1.1"),sQuery(id+"F0.wireOp",EDGE,"E3.0.1.2"),sQuery(id+"F0.wireOp",EDGE,"E3.0.1.3"),sQuery(id+"F0.wireOp",EDGE,"E4.0.0.2"),sQuery(id+"F0.wireOp",EDGE,"E4.3.0.2"),sQuery(id+"F0.wireOp",EDGE,"E4.6.0.2"),sQuery(id+"F0.wireOp",EDGE,"E4.9.0.2"),sQuery(id+"F0.wireOp",EDGE,"E4.0.0.3"),sQuery(id+"F0.wireOp",EDGE,"E4.3.0.3"),sQuery(id+"F0.wireOp",EDGE,"E4.6.0.3"),sQuery(id+"F0.wireOp",EDGE,"E4.9.0.3"),sQuery(id+"F0.wireOp",EDGE,"E4.0.0.4"),sQuery(id+"F0.wireOp",EDGE,"E4.3.0.4"),sQuery(id+"F0.wireOp",EDGE,"E4.6.0.4"),sQuery(id+"F0.wireOp",EDGE,"E4.9.0.4"),sQuery(id+"F0.wireOp",EDGE,"E4.0.0.5"),sQuery(id+"F0.wireOp",EDGE,"E4.3.0.5"),sQuery(id+"F0.wireOp",EDGE,"E4.6.0.5"),sQuery(id+"F0.wireOp",EDGE,"E4.9.0.5"),sQuery(id+"F0.wireOp",EDGE,"E4.0.0.6"),sQuery(id+"F0.wireOp",EDGE,"E4.3.0.6"),sQuery(id+"F0.wireOp",EDGE,"E4.6.0.6"),sQuery(id+"F0.wireOp",EDGE,"E4.9.0.6"),sQuery(id+"F0.wireOp",EDGE,"E4.0.0.7"),sQuery(id+"F0.wireOp",EDGE,"E4.3.0.7"),sQuery(id+"F0.wireOp",EDGE,"E4.6.0.7"),sQuery(id+"F0.wireOp",EDGE,"E4.9.0.7"),sQuery(id+"F0.wireOp",EDGE,"E4.0.0.8"),sQuery(id+"F0.wireOp",EDGE,"E4.3.0.8"),sQuery(id+"F0.wireOp",EDGE,"E4.6.0.8"),sQuery(id+"F0.wireOp",EDGE,"E4.9.0.8"),sQuery(id+"F0.wireOp",EDGE,"E4.0.0.9"),sQuery(id+"F0.wireOp",EDGE,"E4.3.0.9"),sQuery(id+"F0.wireOp",EDGE,"E4.6.0.9"),sQuery(id+"F0.wireOp",EDGE,"E4.9.0.9"),sQuery(id+"F0.wireOp",EDGE,"E4.0.0.10"),sQuery(id+"F0.wireOp",EDGE,"E4.3.0.10"),sQuery(id+"F0.wireOp",EDGE,"E4.6.0.10"),sQuery(id+"F0.wireOp",EDGE,"E4.9.0.10"),sQuery(id+"F0.wireOp",EDGE,"E4.0.0.11"),sQuery(id+"F0.wireOp",EDGE,"E4.3.0.11"),sQuery(id+"F0.wireOp",EDGE,"E4.6.0.11"),sQuery(id+"F0.wireOp",EDGE,"E4.9.0.11"),sQuery(id+"F0.wireOp",EDGE,"E4.0.0.12"),sQuery(id+"F0.wireOp",EDGE,"E4.3.0.12"),sQuery(id+"F0.wireOp",EDGE,"E4.6.0.12"),sQuery(id+"F0.wireOp",EDGE,"E4.9.0.12"),sQuery(id+"F0.wireOp",EDGE,"E4.0.0.13"),sQuery(id+"F0.wireOp",EDGE,"E4.3.0.13"),sQuery(id+"F0.wireOp",EDGE,"E4.6.0.13"),sQuery(id+"F0.wireOp",EDGE,"E4.9.0.13"),sQuery(id+"F0.wireOp",EDGE,"E4.0.0.14"),sQuery(id+"F0.wireOp",EDGE,"E4.3.0.14"),sQuery(id+"F0.wireOp",EDGE,"E4.6.0.14"),sQuery(id+"F0.wireOp",EDGE,"E4.9.0.14"),sQuery(id+"F0.wireOp",EDGE,"E4.0.0.15"),sQuery(id+"F0.wireOp",EDGE,"E4.3.0.15"),sQuery(id+"F0.wireOp",EDGE,"E4.6.0.15"),sQuery(id+"F0.wireOp",EDGE,"E4.9.0.15")])]});
            booleanBodies(context, id + "F21", {"operationType" : BooleanOperationType.SUBTRACTION, "tools" : qUnion([Q0, Q1]), "targets" : qUnion([Q2, Q3])});
        }
        {
            var Q0;
            Q0=makeQuery(id+"F8.opExtrude","CAP_FACE",FACE,{"disambiguationData":[OSD([sQuery(id+"F7.wireOp",EDGE,"E9.bottom"),sQuery(id+"F7.wireOp",EDGE,"E9.top"),sQuery(id+"F7.wireOp",EDGE,"E9.left"),sQuery(id+"F7.wireOp",EDGE,"E9.right"),sQuery(id+"F7.wireOp",EDGE,"E11.bottom"),sQuery(id+"F7.wireOp",EDGE,"E11.top"),sQuery(id+"F7.wireOp",EDGE,"E11.left"),sQuery(id+"F7.wireOp",EDGE,"E11.right"),sQuery(id+"F7.wireOp",EDGE,"E12.0.1.0"),sQuery(id+"F7.wireOp",EDGE,"E12.0.1.1"),sQuery(id+"F7.wireOp",EDGE,"E12.0.1.2"),sQuery(id+"F7.wireOp",EDGE,"E12.0.1.3"),sQuery(id+"F7.wireOp",EDGE,"E12.0.2.0"),sQuery(id+"F7.wireOp",EDGE,"E12.0.2.1"),sQuery(id+"F7.wireOp",EDGE,"E12.0.2.2"),sQuery(id+"F7.wireOp",EDGE,"E12.0.2.3"),sQuery(id+"F7.wireOp",EDGE,"E12.0.3.0"),sQuery(id+"F7.wireOp",EDGE,"E12.0.3.1"),sQuery(id+"F7.wireOp",EDGE,"E12.0.3.2"),sQuery(id+"F7.wireOp",EDGE,"E12.0.3.3"),sQuery(id+"F7.wireOp",EDGE,"E12.0.4.0"),sQuery(id+"F7.wireOp",EDGE,"E12.0.4.1"),sQuery(id+"F7.wireOp",EDGE,"E12.0.4.2"),sQuery(id+"F7.wireOp",EDGE,"E12.0.4.3"),sQuery(id+"F7.wireOp",EDGE,"E12.0.5.0"),sQuery(id+"F7.wireOp",EDGE,"E12.0.5.1"),sQuery(id+"F7.wireOp",EDGE,"E12.0.5.2"),sQuery(id+"F7.wireOp",EDGE,"E12.0.5.3"),sQuery(id+"F7.wireOp",EDGE,"E12.0.6.0"),sQuery(id+"F7.wireOp",EDGE,"E12.0.6.1"),sQuery(id+"F7.wireOp",EDGE,"E12.0.6.2"),sQuery(id+"F7.wireOp",EDGE,"E12.0.6.3"),sQuery(id+"F7.wireOp",EDGE,"E12.0.7.0"),sQuery(id+"F7.wireOp",EDGE,"E12.0.7.1"),sQuery(id+"F7.wireOp",EDGE,"E12.0.7.2"),sQuery(id+"F7.wireOp",EDGE,"E12.0.7.3"),sQuery(id+"F7.wireOp",EDGE,"E12.0.8.0"),sQuery(id+"F7.wireOp",EDGE,"E12.0.8.1"),sQuery(id+"F7.wireOp",EDGE,"E12.0.8.2"),sQuery(id+"F7.wireOp",EDGE,"E12.0.8.3"),sQuery(id+"F7.wireOp",EDGE,"E12.0.9.0"),sQuery(id+"F7.wireOp",EDGE,"E12.0.9.1"),sQuery(id+"F7.wireOp",EDGE,"E12.0.9.2"),sQuery(id+"F7.wireOp",EDGE,"E12.0.9.3"),sQuery(id+"F7.wireOp",EDGE,"E12.0.10.0"),sQuery(id+"F7.wireOp",EDGE,"E12.0.10.1"),sQuery(id+"F7.wireOp",EDGE,"E12.0.10.2"),sQuery(id+"F7.wireOp",EDGE,"E12.0.10.3"),sQuery(id+"F7.wireOp",EDGE,"E12.0.11.0"),sQuery(id+"F7.wireOp",EDGE,"E12.0.11.1"),sQuery(id+"F7.wireOp",EDGE,"E12.0.11.2"),sQuery(id+"F7.wireOp",EDGE,"E12.0.11.3"),sQuery(id+"F7.wireOp",EDGE,"E12.0.12.0"),sQuery(id+"F7.wireOp",EDGE,"E12.0.12.1"),sQuery(id+"F7.wireOp",EDGE,"E12.0.12.2"),sQuery(id+"F7.wireOp",EDGE,"E12.0.12.3"),sQuery(id+"F7.wireOp",EDGE,"E12.0.13.0"),sQuery(id+"F7.wireOp",EDGE,"E12.0.13.1"),sQuery(id+"F7.wireOp",EDGE,"E12.0.13.2"),sQuery(id+"F7.wireOp",EDGE,"E12.0.13.3"),sQuery(id+"F7.wireOp",EDGE,"E12.0.14.0"),sQuery(id+"F7.wireOp",EDGE,"E12.0.14.1"),sQuery(id+"F7.wireOp",EDGE,"E12.0.14.2"),sQuery(id+"F7.wireOp",EDGE,"E12.0.14.3"),sQuery(id+"F7.wireOp",EDGE,"E12.0.15.0"),sQuery(id+"F7.wireOp",EDGE,"E12.0.15.1"),sQuery(id+"F7.wireOp",EDGE,"E12.0.15.2"),sQuery(id+"F7.wireOp",EDGE,"E12.0.15.3"),sQuery(id+"F7.wireOp",EDGE,"E12.1.0.0"),sQuery(id+"F7.wireOp",EDGE,"E12.1.0.1"),sQuery(id+"F7.wireOp",EDGE,"E12.1.0.2"),sQuery(id+"F7.wireOp",EDGE,"E12.1.0.3"),sQuery(id+"F7.wireOp",EDGE,"E12.1.1.0"),sQuery(id+"F7.wireOp",EDGE,"E12.1.1.1"),sQuery(id+"F7.wireOp",EDGE,"E12.1.1.2"),sQuery(id+"F7.wireOp",EDGE,"E12.1.1.3"),sQuery(id+"F7.wireOp",EDGE,"E12.1.2.0"),sQuery(id+"F7.wireOp",EDGE,"E12.1.2.1"),sQuery(id+"F7.wireOp",EDGE,"E12.1.2.2"),sQuery(id+"F7.wireOp",EDGE,"E12.1.2.3"),sQuery(id+"F7.wireOp",EDGE,"E12.1.3.0"),sQuery(id+"F7.wireOp",EDGE,"E12.1.3.1"),sQuery(id+"F7.wireOp",EDGE,"E12.1.3.2"),sQuery(id+"F7.wireOp",EDGE,"E12.1.3.3"),sQuery(id+"F7.wireOp",EDGE,"E12.1.4.0"),sQuery(id+"F7.wireOp",EDGE,"E12.1.4.1"),sQuery(id+"F7.wireOp",EDGE,"E12.1.4.2"),sQuery(id+"F7.wireOp",EDGE,"E12.1.4.3"),sQuery(id+"F7.wireOp",EDGE,"E12.1.5.0"),sQuery(id+"F7.wireOp",EDGE,"E12.1.5.1"),sQuery(id+"F7.wireOp",EDGE,"E12.1.5.2"),sQuery(id+"F7.wireOp",EDGE,"E12.1.5.3"),sQuery(id+"F7.wireOp",EDGE,"E12.1.6.0"),sQuery(id+"F7.wireOp",EDGE,"E12.1.6.1"),sQuery(id+"F7.wireOp",EDGE,"E12.1.6.2"),sQuery(id+"F7.wireOp",EDGE,"E12.1.6.3"),sQuery(id+"F7.wireOp",EDGE,"E12.1.7.0"),sQuery(id+"F7.wireOp",EDGE,"E12.1.7.1"),sQuery(id+"F7.wireOp",EDGE,"E12.1.7.2"),sQuery(id+"F7.wireOp",EDGE,"E12.1.7.3"),sQuery(id+"F7.wireOp",EDGE,"E12.1.8.0"),sQuery(id+"F7.wireOp",EDGE,"E12.1.8.1"),sQuery(id+"F7.wireOp",EDGE,"E12.1.8.2"),sQuery(id+"F7.wireOp",EDGE,"E12.1.8.3"),sQuery(id+"F7.wireOp",EDGE,"E12.1.9.0"),sQuery(id+"F7.wireOp",EDGE,"E12.1.9.1"),sQuery(id+"F7.wireOp",EDGE,"E12.1.9.2"),sQuery(id+"F7.wireOp",EDGE,"E12.1.9.3"),sQuery(id+"F7.wireOp",EDGE,"E12.1.10.0"),sQuery(id+"F7.wireOp",EDGE,"E12.1.10.1"),sQuery(id+"F7.wireOp",EDGE,"E12.1.10.2"),sQuery(id+"F7.wireOp",EDGE,"E12.1.10.3"),sQuery(id+"F7.wireOp",EDGE,"E12.1.11.0"),sQuery(id+"F7.wireOp",EDGE,"E12.1.11.1"),sQuery(id+"F7.wireOp",EDGE,"E12.1.11.2"),sQuery(id+"F7.wireOp",EDGE,"E12.1.11.3"),sQuery(id+"F7.wireOp",EDGE,"E12.1.12.0"),sQuery(id+"F7.wireOp",EDGE,"E12.1.12.1"),sQuery(id+"F7.wireOp",EDGE,"E12.1.12.2"),sQuery(id+"F7.wireOp",EDGE,"E12.1.12.3"),sQuery(id+"F7.wireOp",EDGE,"E12.1.13.0"),sQuery(id+"F7.wireOp",EDGE,"E12.1.13.1"),sQuery(id+"F7.wireOp",EDGE,"E12.1.13.2"),sQuery(id+"F7.wireOp",EDGE,"E12.1.13.3"),sQuery(id+"F7.wireOp",EDGE,"E12.1.14.0"),sQuery(id+"F7.wireOp",EDGE,"E12.1.14.1"),sQuery(id+"F7.wireOp",EDGE,"E12.1.14.2"),sQuery(id+"F7.wireOp",EDGE,"E12.1.14.3"),sQuery(id+"F7.wireOp",EDGE,"E12.1.15.0"),sQuery(id+"F7.wireOp",EDGE,"E12.1.15.1"),sQuery(id+"F7.wireOp",EDGE,"E12.1.15.2"),sQuery(id+"F7.wireOp",EDGE,"E12.1.15.3"),sQuery(id+"F7.wireOp",EDGE,"E12.2.0.0"),sQuery(id+"F7.wireOp",EDGE,"E12.2.0.1"),sQuery(id+"F7.wireOp",EDGE,"E12.2.0.2"),sQuery(id+"F7.wireOp",EDGE,"E12.2.0.3"),sQuery(id+"F7.wireOp",EDGE,"E12.2.1.0"),sQuery(id+"F7.wireOp",EDGE,"E12.2.1.1"),sQuery(id+"F7.wireOp",EDGE,"E12.2.1.2"),sQuery(id+"F7.wireOp",EDGE,"E12.2.1.3"),sQuery(id+"F7.wireOp",EDGE,"E12.2.2.0"),sQuery(id+"F7.wireOp",EDGE,"E12.2.2.1"),sQuery(id+"F7.wireOp",EDGE,"E12.2.2.2"),sQuery(id+"F7.wireOp",EDGE,"E12.2.2.3"),sQuery(id+"F7.wireOp",EDGE,"E12.2.3.0"),sQuery(id+"F7.wireOp",EDGE,"E12.2.3.1"),sQuery(id+"F7.wireOp",EDGE,"E12.2.3.2"),sQuery(id+"F7.wireOp",EDGE,"E12.2.3.3"),sQuery(id+"F7.wireOp",EDGE,"E12.2.4.0"),sQuery(id+"F7.wireOp",EDGE,"E12.2.4.1"),sQuery(id+"F7.wireOp",EDGE,"E12.2.4.2"),sQuery(id+"F7.wireOp",EDGE,"E12.2.4.3"),sQuery(id+"F7.wireOp",EDGE,"E12.2.5.0"),sQuery(id+"F7.wireOp",EDGE,"E12.2.5.1"),sQuery(id+"F7.wireOp",EDGE,"E12.2.5.2"),sQuery(id+"F7.wireOp",EDGE,"E12.2.5.3"),sQuery(id+"F7.wireOp",EDGE,"E12.2.6.0"),sQuery(id+"F7.wireOp",EDGE,"E12.2.6.1"),sQuery(id+"F7.wireOp",EDGE,"E12.2.6.2"),sQuery(id+"F7.wireOp",EDGE,"E12.2.6.3"),sQuery(id+"F7.wireOp",EDGE,"E12.2.7.0"),sQuery(id+"F7.wireOp",EDGE,"E12.2.7.1"),sQuery(id+"F7.wireOp",EDGE,"E12.2.7.2"),sQuery(id+"F7.wireOp",EDGE,"E12.2.7.3"),sQuery(id+"F7.wireOp",EDGE,"E12.2.8.0"),sQuery(id+"F7.wireOp",EDGE,"E12.2.8.1"),sQuery(id+"F7.wireOp",EDGE,"E12.2.8.2"),sQuery(id+"F7.wireOp",EDGE,"E12.2.8.3"),sQuery(id+"F7.wireOp",EDGE,"E12.2.9.0"),sQuery(id+"F7.wireOp",EDGE,"E12.2.9.1"),sQuery(id+"F7.wireOp",EDGE,"E12.2.9.2"),sQuery(id+"F7.wireOp",EDGE,"E12.2.9.3"),sQuery(id+"F7.wireOp",EDGE,"E12.2.10.0"),sQuery(id+"F7.wireOp",EDGE,"E12.2.10.1"),sQuery(id+"F7.wireOp",EDGE,"E12.2.10.2"),sQuery(id+"F7.wireOp",EDGE,"E12.2.10.3"),sQuery(id+"F7.wireOp",EDGE,"E12.2.11.0"),sQuery(id+"F7.wireOp",EDGE,"E12.2.11.1"),sQuery(id+"F7.wireOp",EDGE,"E12.2.11.2"),sQuery(id+"F7.wireOp",EDGE,"E12.2.11.3"),sQuery(id+"F7.wireOp",EDGE,"E12.2.12.0"),sQuery(id+"F7.wireOp",EDGE,"E12.2.12.1"),sQuery(id+"F7.wireOp",EDGE,"E12.2.12.2"),sQuery(id+"F7.wireOp",EDGE,"E12.2.12.3"),sQuery(id+"F7.wireOp",EDGE,"E12.2.13.0"),sQuery(id+"F7.wireOp",EDGE,"E12.2.13.1"),sQuery(id+"F7.wireOp",EDGE,"E12.2.13.2"),sQuery(id+"F7.wireOp",EDGE,"E12.2.13.3"),sQuery(id+"F7.wireOp",EDGE,"E12.2.14.0"),sQuery(id+"F7.wireOp",EDGE,"E12.2.14.1"),sQuery(id+"F7.wireOp",EDGE,"E12.2.14.2"),sQuery(id+"F7.wireOp",EDGE,"E12.2.14.3"),sQuery(id+"F7.wireOp",EDGE,"E12.2.15.0"),sQuery(id+"F7.wireOp",EDGE,"E12.2.15.1"),sQuery(id+"F7.wireOp",EDGE,"E12.2.15.2"),sQuery(id+"F7.wireOp",EDGE,"E12.2.15.3"),sQuery(id+"F7.wireOp",EDGE,"E12.3.0.0"),sQuery(id+"F7.wireOp",EDGE,"E12.3.0.1"),sQuery(id+"F7.wireOp",EDGE,"E12.3.0.2"),sQuery(id+"F7.wireOp",EDGE,"E12.3.0.3"),sQuery(id+"F7.wireOp",EDGE,"E12.3.1.0"),sQuery(id+"F7.wireOp",EDGE,"E12.3.1.1"),sQuery(id+"F7.wireOp",EDGE,"E12.3.1.2"),sQuery(id+"F7.wireOp",EDGE,"E12.3.1.3"),sQuery(id+"F7.wireOp",EDGE,"E12.3.2.0"),sQuery(id+"F7.wireOp",EDGE,"E12.3.2.1"),sQuery(id+"F7.wireOp",EDGE,"E12.3.2.2"),sQuery(id+"F7.wireOp",EDGE,"E12.3.2.3"),sQuery(id+"F7.wireOp",EDGE,"E12.3.3.0"),sQuery(id+"F7.wireOp",EDGE,"E12.3.3.1"),sQuery(id+"F7.wireOp",EDGE,"E12.3.3.2"),sQuery(id+"F7.wireOp",EDGE,"E12.3.3.3"),sQuery(id+"F7.wireOp",EDGE,"E12.3.4.0"),sQuery(id+"F7.wireOp",EDGE,"E12.3.4.1"),sQuery(id+"F7.wireOp",EDGE,"E12.3.4.2"),sQuery(id+"F7.wireOp",EDGE,"E12.3.4.3"),sQuery(id+"F7.wireOp",EDGE,"E12.3.5.0"),sQuery(id+"F7.wireOp",EDGE,"E12.3.5.1"),sQuery(id+"F7.wireOp",EDGE,"E12.3.5.2"),sQuery(id+"F7.wireOp",EDGE,"E12.3.5.3"),sQuery(id+"F7.wireOp",EDGE,"E12.3.6.0"),sQuery(id+"F7.wireOp",EDGE,"E12.3.6.1"),sQuery(id+"F7.wireOp",EDGE,"E12.3.6.2"),sQuery(id+"F7.wireOp",EDGE,"E12.3.6.3"),sQuery(id+"F7.wireOp",EDGE,"E12.3.7.0"),sQuery(id+"F7.wireOp",EDGE,"E12.3.7.1"),sQuery(id+"F7.wireOp",EDGE,"E12.3.7.2"),sQuery(id+"F7.wireOp",EDGE,"E12.3.7.3"),sQuery(id+"F7.wireOp",EDGE,"E12.3.8.0"),sQuery(id+"F7.wireOp",EDGE,"E12.3.8.1"),sQuery(id+"F7.wireOp",EDGE,"E12.3.8.2"),sQuery(id+"F7.wireOp",EDGE,"E12.3.8.3"),sQuery(id+"F7.wireOp",EDGE,"E12.3.9.0"),sQuery(id+"F7.wireOp",EDGE,"E12.3.9.1"),sQuery(id+"F7.wireOp",EDGE,"E12.3.9.2"),sQuery(id+"F7.wireOp",EDGE,"E12.3.9.3"),sQuery(id+"F7.wireOp",EDGE,"E12.3.10.0"),sQuery(id+"F7.wireOp",EDGE,"E12.3.10.1"),sQuery(id+"F7.wireOp",EDGE,"E12.3.10.2"),sQuery(id+"F7.wireOp",EDGE,"E12.3.10.3"),sQuery(id+"F7.wireOp",EDGE,"E12.3.11.0"),sQuery(id+"F7.wireOp",EDGE,"E12.3.11.1"),sQuery(id+"F7.wireOp",EDGE,"E12.3.11.2"),sQuery(id+"F7.wireOp",EDGE,"E12.3.11.3"),sQuery(id+"F7.wireOp",EDGE,"E12.3.12.0"),sQuery(id+"F7.wireOp",EDGE,"E12.3.12.1"),sQuery(id+"F7.wireOp",EDGE,"E12.3.12.2"),sQuery(id+"F7.wireOp",EDGE,"E12.3.12.3"),sQuery(id+"F7.wireOp",EDGE,"E12.3.13.0"),sQuery(id+"F7.wireOp",EDGE,"E12.3.13.1"),sQuery(id+"F7.wireOp",EDGE,"E12.3.13.2"),sQuery(id+"F7.wireOp",EDGE,"E12.3.13.3"),sQuery(id+"F7.wireOp",EDGE,"E12.3.14.0"),sQuery(id+"F7.wireOp",EDGE,"E12.3.14.1"),sQuery(id+"F7.wireOp",EDGE,"E12.3.14.2"),sQuery(id+"F7.wireOp",EDGE,"E12.3.14.3"),sQuery(id+"F7.wireOp",EDGE,"E12.3.15.0"),sQuery(id+"F7.wireOp",EDGE,"E12.3.15.1"),sQuery(id+"F7.wireOp",EDGE,"E12.3.15.2"),sQuery(id+"F7.wireOp",EDGE,"E12.3.15.3"),sQuery(id+"F7.wireOp",EDGE,"E12.4.0.0"),sQuery(id+"F7.wireOp",EDGE,"E12.4.0.1"),sQuery(id+"F7.wireOp",EDGE,"E12.4.0.2"),sQuery(id+"F7.wireOp",EDGE,"E12.4.0.3"),sQuery(id+"F7.wireOp",EDGE,"E12.4.1.0"),sQuery(id+"F7.wireOp",EDGE,"E12.4.1.1"),sQuery(id+"F7.wireOp",EDGE,"E12.4.1.2"),sQuery(id+"F7.wireOp",EDGE,"E12.4.1.3"),sQuery(id+"F7.wireOp",EDGE,"E12.4.2.0"),sQuery(id+"F7.wireOp",EDGE,"E12.4.2.1"),sQuery(id+"F7.wireOp",EDGE,"E12.4.2.2"),sQuery(id+"F7.wireOp",EDGE,"E12.4.2.3"),sQuery(id+"F7.wireOp",EDGE,"E12.4.3.0"),sQuery(id+"F7.wireOp",EDGE,"E12.4.3.1"),sQuery(id+"F7.wireOp",EDGE,"E12.4.3.2"),sQuery(id+"F7.wireOp",EDGE,"E12.4.3.3"),sQuery(id+"F7.wireOp",EDGE,"E12.4.4.0"),sQuery(id+"F7.wireOp",EDGE,"E12.4.4.1"),sQuery(id+"F7.wireOp",EDGE,"E12.4.4.2"),sQuery(id+"F7.wireOp",EDGE,"E12.4.4.3"),sQuery(id+"F7.wireOp",EDGE,"E12.4.5.0"),sQuery(id+"F7.wireOp",EDGE,"E12.4.5.1"),sQuery(id+"F7.wireOp",EDGE,"E12.4.5.2"),sQuery(id+"F7.wireOp",EDGE,"E12.4.5.3"),sQuery(id+"F7.wireOp",EDGE,"E12.4.6.0"),sQuery(id+"F7.wireOp",EDGE,"E12.4.6.1"),sQuery(id+"F7.wireOp",EDGE,"E12.4.6.2"),sQuery(id+"F7.wireOp",EDGE,"E12.4.6.3"),sQuery(id+"F7.wireOp",EDGE,"E12.4.7.0"),sQuery(id+"F7.wireOp",EDGE,"E12.4.7.1"),sQuery(id+"F7.wireOp",EDGE,"E12.4.7.2"),sQuery(id+"F7.wireOp",EDGE,"E12.4.7.3"),sQuery(id+"F7.wireOp",EDGE,"E12.4.8.0"),sQuery(id+"F7.wireOp",EDGE,"E12.4.8.1"),sQuery(id+"F7.wireOp",EDGE,"E12.4.8.2"),sQuery(id+"F7.wireOp",EDGE,"E12.4.8.3"),sQuery(id+"F7.wireOp",EDGE,"E12.4.9.0"),sQuery(id+"F7.wireOp",EDGE,"E12.4.9.1"),sQuery(id+"F7.wireOp",EDGE,"E12.4.9.2"),sQuery(id+"F7.wireOp",EDGE,"E12.4.9.3"),sQuery(id+"F7.wireOp",EDGE,"E12.4.10.0"),sQuery(id+"F7.wireOp",EDGE,"E12.4.10.1"),sQuery(id+"F7.wireOp",EDGE,"E12.4.10.2"),sQuery(id+"F7.wireOp",EDGE,"E12.4.10.3"),sQuery(id+"F7.wireOp",EDGE,"E12.4.11.0"),sQuery(id+"F7.wireOp",EDGE,"E12.4.11.1"),sQuery(id+"F7.wireOp",EDGE,"E12.4.11.2"),sQuery(id+"F7.wireOp",EDGE,"E12.4.11.3"),sQuery(id+"F7.wireOp",EDGE,"E12.4.12.0"),sQuery(id+"F7.wireOp",EDGE,"E12.4.12.1"),sQuery(id+"F7.wireOp",EDGE,"E12.4.12.2"),sQuery(id+"F7.wireOp",EDGE,"E12.4.12.3"),sQuery(id+"F7.wireOp",EDGE,"E12.4.13.0"),sQuery(id+"F7.wireOp",EDGE,"E12.4.13.1"),sQuery(id+"F7.wireOp",EDGE,"E12.4.13.2"),sQuery(id+"F7.wireOp",EDGE,"E12.4.13.3"),sQuery(id+"F7.wireOp",EDGE,"E12.4.14.0"),sQuery(id+"F7.wireOp",EDGE,"E12.4.14.1"),sQuery(id+"F7.wireOp",EDGE,"E12.4.14.2"),sQuery(id+"F7.wireOp",EDGE,"E12.4.14.3"),sQuery(id+"F7.wireOp",EDGE,"E12.4.15.0"),sQuery(id+"F7.wireOp",EDGE,"E12.4.15.1"),sQuery(id+"F7.wireOp",EDGE,"E12.4.15.2"),sQuery(id+"F7.wireOp",EDGE,"E12.4.15.3"),sQuery(id+"F7.wireOp",EDGE,"E12.5.0.0"),sQuery(id+"F7.wireOp",EDGE,"E12.5.0.1"),sQuery(id+"F7.wireOp",EDGE,"E12.5.0.2"),sQuery(id+"F7.wireOp",EDGE,"E12.5.0.3"),sQuery(id+"F7.wireOp",EDGE,"E12.5.1.0"),sQuery(id+"F7.wireOp",EDGE,"E12.5.1.1"),sQuery(id+"F7.wireOp",EDGE,"E12.5.1.2"),sQuery(id+"F7.wireOp",EDGE,"E12.5.1.3"),sQuery(id+"F7.wireOp",EDGE,"E12.5.2.0"),sQuery(id+"F7.wireOp",EDGE,"E12.5.2.1"),sQuery(id+"F7.wireOp",EDGE,"E12.5.2.2"),sQuery(id+"F7.wireOp",EDGE,"E12.5.2.3"),sQuery(id+"F7.wireOp",EDGE,"E12.5.3.0"),sQuery(id+"F7.wireOp",EDGE,"E12.5.3.1"),sQuery(id+"F7.wireOp",EDGE,"E12.5.3.2"),sQuery(id+"F7.wireOp",EDGE,"E12.5.3.3"),sQuery(id+"F7.wireOp",EDGE,"E12.5.4.0"),sQuery(id+"F7.wireOp",EDGE,"E12.5.4.1"),sQuery(id+"F7.wireOp",EDGE,"E12.5.4.2"),sQuery(id+"F7.wireOp",EDGE,"E12.5.4.3"),sQuery(id+"F7.wireOp",EDGE,"E12.5.5.0"),sQuery(id+"F7.wireOp",EDGE,"E12.5.5.1"),sQuery(id+"F7.wireOp",EDGE,"E12.5.5.2"),sQuery(id+"F7.wireOp",EDGE,"E12.5.5.3"),sQuery(id+"F7.wireOp",EDGE,"E12.5.6.0"),sQuery(id+"F7.wireOp",EDGE,"E12.5.6.1"),sQuery(id+"F7.wireOp",EDGE,"E12.5.6.2"),sQuery(id+"F7.wireOp",EDGE,"E12.5.6.3"),sQuery(id+"F7.wireOp",EDGE,"E12.5.7.0"),sQuery(id+"F7.wireOp",EDGE,"E12.5.7.1"),sQuery(id+"F7.wireOp",EDGE,"E12.5.7.2"),sQuery(id+"F7.wireOp",EDGE,"E12.5.7.3"),sQuery(id+"F7.wireOp",EDGE,"E12.5.8.0"),sQuery(id+"F7.wireOp",EDGE,"E12.5.8.1"),sQuery(id+"F7.wireOp",EDGE,"E12.5.8.2"),sQuery(id+"F7.wireOp",EDGE,"E12.5.8.3"),sQuery(id+"F7.wireOp",EDGE,"E12.5.9.0"),sQuery(id+"F7.wireOp",EDGE,"E12.5.9.1"),sQuery(id+"F7.wireOp",EDGE,"E12.5.9.2"),sQuery(id+"F7.wireOp",EDGE,"E12.5.9.3"),sQuery(id+"F7.wireOp",EDGE,"E12.5.10.0"),sQuery(id+"F7.wireOp",EDGE,"E12.5.10.1"),sQuery(id+"F7.wireOp",EDGE,"E12.5.10.2"),sQuery(id+"F7.wireOp",EDGE,"E12.5.10.3"),sQuery(id+"F7.wireOp",EDGE,"E12.5.11.0"),sQuery(id+"F7.wireOp",EDGE,"E12.5.11.1"),sQuery(id+"F7.wireOp",EDGE,"E12.5.11.2"),sQuery(id+"F7.wireOp",EDGE,"E12.5.11.3"),sQuery(id+"F7.wireOp",EDGE,"E12.5.12.0"),sQuery(id+"F7.wireOp",EDGE,"E12.5.12.1"),sQuery(id+"F7.wireOp",EDGE,"E12.5.12.2"),sQuery(id+"F7.wireOp",EDGE,"E12.5.12.3"),sQuery(id+"F7.wireOp",EDGE,"E12.5.13.0"),sQuery(id+"F7.wireOp",EDGE,"E12.5.13.1"),sQuery(id+"F7.wireOp",EDGE,"E12.5.13.2"),sQuery(id+"F7.wireOp",EDGE,"E12.5.13.3"),sQuery(id+"F7.wireOp",EDGE,"E12.5.14.0"),sQuery(id+"F7.wireOp",EDGE,"E12.5.14.1"),sQuery(id+"F7.wireOp",EDGE,"E12.5.14.2"),sQuery(id+"F7.wireOp",EDGE,"E12.5.14.3"),sQuery(id+"F7.wireOp",EDGE,"E12.5.15.0"),sQuery(id+"F7.wireOp",EDGE,"E12.5.15.1"),sQuery(id+"F7.wireOp",EDGE,"E12.5.15.2"),sQuery(id+"F7.wireOp",EDGE,"E12.5.15.3"),sQuery(id+"F7.wireOp",EDGE,"E12.6.0.0"),sQuery(id+"F7.wireOp",EDGE,"E12.6.0.1"),sQuery(id+"F7.wireOp",EDGE,"E12.6.0.2"),sQuery(id+"F7.wireOp",EDGE,"E12.6.0.3"),sQuery(id+"F7.wireOp",EDGE,"E12.6.1.0"),sQuery(id+"F7.wireOp",EDGE,"E12.6.1.1"),sQuery(id+"F7.wireOp",EDGE,"E12.6.1.2"),sQuery(id+"F7.wireOp",EDGE,"E12.6.1.3"),sQuery(id+"F7.wireOp",EDGE,"E12.6.2.0"),sQuery(id+"F7.wireOp",EDGE,"E12.6.2.1"),sQuery(id+"F7.wireOp",EDGE,"E12.6.2.2"),sQuery(id+"F7.wireOp",EDGE,"E12.6.2.3"),sQuery(id+"F7.wireOp",EDGE,"E12.6.3.0"),sQuery(id+"F7.wireOp",EDGE,"E12.6.3.1"),sQuery(id+"F7.wireOp",EDGE,"E12.6.3.2"),sQuery(id+"F7.wireOp",EDGE,"E12.6.3.3"),sQuery(id+"F7.wireOp",EDGE,"E12.6.4.0"),sQuery(id+"F7.wireOp",EDGE,"E12.6.4.1"),sQuery(id+"F7.wireOp",EDGE,"E12.6.4.2"),sQuery(id+"F7.wireOp",EDGE,"E12.6.4.3"),sQuery(id+"F7.wireOp",EDGE,"E12.6.5.0"),sQuery(id+"F7.wireOp",EDGE,"E12.6.5.1"),sQuery(id+"F7.wireOp",EDGE,"E12.6.5.2"),sQuery(id+"F7.wireOp",EDGE,"E12.6.5.3"),sQuery(id+"F7.wireOp",EDGE,"E12.6.6.0"),sQuery(id+"F7.wireOp",EDGE,"E12.6.6.1"),sQuery(id+"F7.wireOp",EDGE,"E12.6.6.2"),sQuery(id+"F7.wireOp",EDGE,"E12.6.6.3"),sQuery(id+"F7.wireOp",EDGE,"E12.6.7.0"),sQuery(id+"F7.wireOp",EDGE,"E12.6.7.1"),sQuery(id+"F7.wireOp",EDGE,"E12.6.7.2"),sQuery(id+"F7.wireOp",EDGE,"E12.6.7.3"),sQuery(id+"F7.wireOp",EDGE,"E12.6.8.0"),sQuery(id+"F7.wireOp",EDGE,"E12.6.8.1"),sQuery(id+"F7.wireOp",EDGE,"E12.6.8.2"),sQuery(id+"F7.wireOp",EDGE,"E12.6.8.3"),sQuery(id+"F7.wireOp",EDGE,"E12.6.9.0"),sQuery(id+"F7.wireOp",EDGE,"E12.6.9.1"),sQuery(id+"F7.wireOp",EDGE,"E12.6.9.2"),sQuery(id+"F7.wireOp",EDGE,"E12.6.9.3"),sQuery(id+"F7.wireOp",EDGE,"E12.6.10.0"),sQuery(id+"F7.wireOp",EDGE,"E12.6.10.1"),sQuery(id+"F7.wireOp",EDGE,"E12.6.10.2"),sQuery(id+"F7.wireOp",EDGE,"E12.6.10.3"),sQuery(id+"F7.wireOp",EDGE,"E12.6.11.0"),sQuery(id+"F7.wireOp",EDGE,"E12.6.11.1"),sQuery(id+"F7.wireOp",EDGE,"E12.6.11.2"),sQuery(id+"F7.wireOp",EDGE,"E12.6.11.3"),sQuery(id+"F7.wireOp",EDGE,"E12.6.12.0"),sQuery(id+"F7.wireOp",EDGE,"E12.6.12.1"),sQuery(id+"F7.wireOp",EDGE,"E12.6.12.2"),sQuery(id+"F7.wireOp",EDGE,"E12.6.12.3"),sQuery(id+"F7.wireOp",EDGE,"E12.6.13.0"),sQuery(id+"F7.wireOp",EDGE,"E12.6.13.1"),sQuery(id+"F7.wireOp",EDGE,"E12.6.13.2"),sQuery(id+"F7.wireOp",EDGE,"E12.6.13.3"),sQuery(id+"F7.wireOp",EDGE,"E12.6.14.0"),sQuery(id+"F7.wireOp",EDGE,"E12.6.14.1"),sQuery(id+"F7.wireOp",EDGE,"E12.6.14.2"),sQuery(id+"F7.wireOp",EDGE,"E12.6.14.3"),sQuery(id+"F7.wireOp",EDGE,"E12.6.15.0"),sQuery(id+"F7.wireOp",EDGE,"E12.6.15.1"),sQuery(id+"F7.wireOp",EDGE,"E12.6.15.2"),sQuery(id+"F7.wireOp",EDGE,"E12.6.15.3"),sQuery(id+"F7.wireOp",EDGE,"E12.7.0.0"),sQuery(id+"F7.wireOp",EDGE,"E12.7.0.1"),sQuery(id+"F7.wireOp",EDGE,"E12.7.0.2"),sQuery(id+"F7.wireOp",EDGE,"E12.7.0.3"),sQuery(id+"F7.wireOp",EDGE,"E12.7.1.0"),sQuery(id+"F7.wireOp",EDGE,"E12.7.1.1"),sQuery(id+"F7.wireOp",EDGE,"E12.7.1.2"),sQuery(id+"F7.wireOp",EDGE,"E12.7.1.3"),sQuery(id+"F7.wireOp",EDGE,"E12.7.2.0"),sQuery(id+"F7.wireOp",EDGE,"E12.7.2.1"),sQuery(id+"F7.wireOp",EDGE,"E12.7.2.2"),sQuery(id+"F7.wireOp",EDGE,"E12.7.2.3"),sQuery(id+"F7.wireOp",EDGE,"E12.7.3.0"),sQuery(id+"F7.wireOp",EDGE,"E12.7.3.1"),sQuery(id+"F7.wireOp",EDGE,"E12.7.3.2"),sQuery(id+"F7.wireOp",EDGE,"E12.7.3.3"),sQuery(id+"F7.wireOp",EDGE,"E12.7.4.0"),sQuery(id+"F7.wireOp",EDGE,"E12.7.4.1"),sQuery(id+"F7.wireOp",EDGE,"E12.7.4.2"),sQuery(id+"F7.wireOp",EDGE,"E12.7.4.3"),sQuery(id+"F7.wireOp",EDGE,"E12.7.5.0"),sQuery(id+"F7.wireOp",EDGE,"E12.7.5.1"),sQuery(id+"F7.wireOp",EDGE,"E12.7.5.2"),sQuery(id+"F7.wireOp",EDGE,"E12.7.5.3"),sQuery(id+"F7.wireOp",EDGE,"E12.7.6.0"),sQuery(id+"F7.wireOp",EDGE,"E12.7.6.1"),sQuery(id+"F7.wireOp",EDGE,"E12.7.6.2"),sQuery(id+"F7.wireOp",EDGE,"E12.7.6.3"),sQuery(id+"F7.wireOp",EDGE,"E12.7.7.0"),sQuery(id+"F7.wireOp",EDGE,"E12.7.7.1"),sQuery(id+"F7.wireOp",EDGE,"E12.7.7.2"),sQuery(id+"F7.wireOp",EDGE,"E12.7.7.3"),sQuery(id+"F7.wireOp",EDGE,"E12.7.8.0"),sQuery(id+"F7.wireOp",EDGE,"E12.7.8.1"),sQuery(id+"F7.wireOp",EDGE,"E12.7.8.2"),sQuery(id+"F7.wireOp",EDGE,"E12.7.8.3"),sQuery(id+"F7.wireOp",EDGE,"E12.7.9.0"),sQuery(id+"F7.wireOp",EDGE,"E12.7.9.1"),sQuery(id+"F7.wireOp",EDGE,"E12.7.9.2"),sQuery(id+"F7.wireOp",EDGE,"E12.7.9.3"),sQuery(id+"F7.wireOp",EDGE,"E12.7.10.0"),sQuery(id+"F7.wireOp",EDGE,"E12.7.10.1"),sQuery(id+"F7.wireOp",EDGE,"E12.7.10.2"),sQuery(id+"F7.wireOp",EDGE,"E12.7.10.3"),sQuery(id+"F7.wireOp",EDGE,"E12.7.11.0"),sQuery(id+"F7.wireOp",EDGE,"E12.7.11.1"),sQuery(id+"F7.wireOp",EDGE,"E12.7.11.2"),sQuery(id+"F7.wireOp",EDGE,"E12.7.11.3"),sQuery(id+"F7.wireOp",EDGE,"E12.7.12.0"),sQuery(id+"F7.wireOp",EDGE,"E12.7.12.1"),sQuery(id+"F7.wireOp",EDGE,"E12.7.12.2"),sQuery(id+"F7.wireOp",EDGE,"E12.7.12.3"),sQuery(id+"F7.wireOp",EDGE,"E12.7.13.0"),sQuery(id+"F7.wireOp",EDGE,"E12.7.13.1"),sQuery(id+"F7.wireOp",EDGE,"E12.7.13.2"),sQuery(id+"F7.wireOp",EDGE,"E12.7.13.3"),sQuery(id+"F7.wireOp",EDGE,"E12.7.14.0"),sQuery(id+"F7.wireOp",EDGE,"E12.7.14.1"),sQuery(id+"F7.wireOp",EDGE,"E12.7.14.2"),sQuery(id+"F7.wireOp",EDGE,"E12.7.14.3"),sQuery(id+"F7.wireOp",EDGE,"E12.7.15.0"),sQuery(id+"F7.wireOp",EDGE,"E12.7.15.1"),sQuery(id+"F7.wireOp",EDGE,"E12.7.15.2"),sQuery(id+"F7.wireOp",EDGE,"E12.7.15.3"),sQuery(id+"F7.wireOp",EDGE,"E12.8.0.0"),sQuery(id+"F7.wireOp",EDGE,"E12.8.0.1"),sQuery(id+"F7.wireOp",EDGE,"E12.8.0.2"),sQuery(id+"F7.wireOp",EDGE,"E12.8.0.3"),sQuery(id+"F7.wireOp",EDGE,"E12.8.1.0"),sQuery(id+"F7.wireOp",EDGE,"E12.8.1.1"),sQuery(id+"F7.wireOp",EDGE,"E12.8.1.2"),sQuery(id+"F7.wireOp",EDGE,"E12.8.1.3"),sQuery(id+"F7.wireOp",EDGE,"E12.8.2.0"),sQuery(id+"F7.wireOp",EDGE,"E12.8.2.1"),sQuery(id+"F7.wireOp",EDGE,"E12.8.2.2"),sQuery(id+"F7.wireOp",EDGE,"E12.8.2.3"),sQuery(id+"F7.wireOp",EDGE,"E12.8.3.0"),sQuery(id+"F7.wireOp",EDGE,"E12.8.3.1"),sQuery(id+"F7.wireOp",EDGE,"E12.8.3.2"),sQuery(id+"F7.wireOp",EDGE,"E12.8.3.3"),sQuery(id+"F7.wireOp",EDGE,"E12.8.4.0"),sQuery(id+"F7.wireOp",EDGE,"E12.8.4.1"),sQuery(id+"F7.wireOp",EDGE,"E12.8.4.2"),sQuery(id+"F7.wireOp",EDGE,"E12.8.4.3"),sQuery(id+"F7.wireOp",EDGE,"E12.8.5.0"),sQuery(id+"F7.wireOp",EDGE,"E12.8.5.1"),sQuery(id+"F7.wireOp",EDGE,"E12.8.5.2"),sQuery(id+"F7.wireOp",EDGE,"E12.8.5.3"),sQuery(id+"F7.wireOp",EDGE,"E12.8.6.0"),sQuery(id+"F7.wireOp",EDGE,"E12.8.6.1"),sQuery(id+"F7.wireOp",EDGE,"E12.8.6.2"),sQuery(id+"F7.wireOp",EDGE,"E12.8.6.3"),sQuery(id+"F7.wireOp",EDGE,"E12.8.7.0"),sQuery(id+"F7.wireOp",EDGE,"E12.8.7.1"),sQuery(id+"F7.wireOp",EDGE,"E12.8.7.2"),sQuery(id+"F7.wireOp",EDGE,"E12.8.7.3"),sQuery(id+"F7.wireOp",EDGE,"E12.8.8.0"),sQuery(id+"F7.wireOp",EDGE,"E12.8.8.1"),sQuery(id+"F7.wireOp",EDGE,"E12.8.8.2"),sQuery(id+"F7.wireOp",EDGE,"E12.8.8.3"),sQuery(id+"F7.wireOp",EDGE,"E12.8.9.0"),sQuery(id+"F7.wireOp",EDGE,"E12.8.9.1"),sQuery(id+"F7.wireOp",EDGE,"E12.8.9.2"),sQuery(id+"F7.wireOp",EDGE,"E12.8.9.3"),sQuery(id+"F7.wireOp",EDGE,"E12.8.10.0"),sQuery(id+"F7.wireOp",EDGE,"E12.8.10.1"),sQuery(id+"F7.wireOp",EDGE,"E12.8.10.2"),sQuery(id+"F7.wireOp",EDGE,"E12.8.10.3"),sQuery(id+"F7.wireOp",EDGE,"E12.8.11.0"),sQuery(id+"F7.wireOp",EDGE,"E12.8.11.1"),sQuery(id+"F7.wireOp",EDGE,"E12.8.11.2"),sQuery(id+"F7.wireOp",EDGE,"E12.8.11.3"),sQuery(id+"F7.wireOp",EDGE,"E12.8.12.0"),sQuery(id+"F7.wireOp",EDGE,"E12.8.12.1"),sQuery(id+"F7.wireOp",EDGE,"E12.8.12.2"),sQuery(id+"F7.wireOp",EDGE,"E12.8.12.3"),sQuery(id+"F7.wireOp",EDGE,"E12.8.13.0"),sQuery(id+"F7.wireOp",EDGE,"E12.8.13.1"),sQuery(id+"F7.wireOp",EDGE,"E12.8.13.2"),sQuery(id+"F7.wireOp",EDGE,"E12.8.13.3"),sQuery(id+"F7.wireOp",EDGE,"E12.8.14.0"),sQuery(id+"F7.wireOp",EDGE,"E12.8.14.1"),sQuery(id+"F7.wireOp",EDGE,"E12.8.14.2"),sQuery(id+"F7.wireOp",EDGE,"E12.8.14.3"),sQuery(id+"F7.wireOp",EDGE,"E12.8.15.0"),sQuery(id+"F7.wireOp",EDGE,"E12.8.15.1"),sQuery(id+"F7.wireOp",EDGE,"E12.8.15.2"),sQuery(id+"F7.wireOp",EDGE,"E12.8.15.3"),sQuery(id+"F7.wireOp",EDGE,"E12.9.0.0"),sQuery(id+"F7.wireOp",EDGE,"E12.9.0.1"),sQuery(id+"F7.wireOp",EDGE,"E12.9.0.2"),sQuery(id+"F7.wireOp",EDGE,"E12.9.0.3"),sQuery(id+"F7.wireOp",EDGE,"E12.9.1.0"),sQuery(id+"F7.wireOp",EDGE,"E12.9.1.1"),sQuery(id+"F7.wireOp",EDGE,"E12.9.1.2"),sQuery(id+"F7.wireOp",EDGE,"E12.9.1.3"),sQuery(id+"F7.wireOp",EDGE,"E12.9.2.0"),sQuery(id+"F7.wireOp",EDGE,"E12.9.2.1"),sQuery(id+"F7.wireOp",EDGE,"E12.9.2.2"),sQuery(id+"F7.wireOp",EDGE,"E12.9.2.3"),sQuery(id+"F7.wireOp",EDGE,"E12.9.3.0"),sQuery(id+"F7.wireOp",EDGE,"E12.9.3.1"),sQuery(id+"F7.wireOp",EDGE,"E12.9.3.2"),sQuery(id+"F7.wireOp",EDGE,"E12.9.3.3"),sQuery(id+"F7.wireOp",EDGE,"E12.9.4.0"),sQuery(id+"F7.wireOp",EDGE,"E12.9.4.1"),sQuery(id+"F7.wireOp",EDGE,"E12.9.4.2"),sQuery(id+"F7.wireOp",EDGE,"E12.9.4.3"),sQuery(id+"F7.wireOp",EDGE,"E12.9.5.0"),sQuery(id+"F7.wireOp",EDGE,"E12.9.5.1"),sQuery(id+"F7.wireOp",EDGE,"E12.9.5.2"),sQuery(id+"F7.wireOp",EDGE,"E12.9.5.3"),sQuery(id+"F7.wireOp",EDGE,"E12.9.6.0"),sQuery(id+"F7.wireOp",EDGE,"E12.9.6.1"),sQuery(id+"F7.wireOp",EDGE,"E12.9.6.2"),sQuery(id+"F7.wireOp",EDGE,"E12.9.6.3"),sQuery(id+"F7.wireOp",EDGE,"E12.9.7.0"),sQuery(id+"F7.wireOp",EDGE,"E12.9.7.1"),sQuery(id+"F7.wireOp",EDGE,"E12.9.7.2"),sQuery(id+"F7.wireOp",EDGE,"E12.9.7.3"),sQuery(id+"F7.wireOp",EDGE,"E12.9.8.0"),sQuery(id+"F7.wireOp",EDGE,"E12.9.8.1"),sQuery(id+"F7.wireOp",EDGE,"E12.9.8.2"),sQuery(id+"F7.wireOp",EDGE,"E12.9.8.3"),sQuery(id+"F7.wireOp",EDGE,"E12.9.9.0"),sQuery(id+"F7.wireOp",EDGE,"E12.9.9.1"),sQuery(id+"F7.wireOp",EDGE,"E12.9.9.2"),sQuery(id+"F7.wireOp",EDGE,"E12.9.9.3"),sQuery(id+"F7.wireOp",EDGE,"E12.9.10.0"),sQuery(id+"F7.wireOp",EDGE,"E12.9.10.1"),sQuery(id+"F7.wireOp",EDGE,"E12.9.10.2"),sQuery(id+"F7.wireOp",EDGE,"E12.9.10.3"),sQuery(id+"F7.wireOp",EDGE,"E12.9.11.0"),sQuery(id+"F7.wireOp",EDGE,"E12.9.11.1"),sQuery(id+"F7.wireOp",EDGE,"E12.9.11.2"),sQuery(id+"F7.wireOp",EDGE,"E12.9.11.3"),sQuery(id+"F7.wireOp",EDGE,"E12.9.12.0"),sQuery(id+"F7.wireOp",EDGE,"E12.9.12.1"),sQuery(id+"F7.wireOp",EDGE,"E12.9.12.2"),sQuery(id+"F7.wireOp",EDGE,"E12.9.12.3"),sQuery(id+"F7.wireOp",EDGE,"E12.9.13.0"),sQuery(id+"F7.wireOp",EDGE,"E12.9.13.1"),sQuery(id+"F7.wireOp",EDGE,"E12.9.13.2"),sQuery(id+"F7.wireOp",EDGE,"E12.9.13.3"),sQuery(id+"F7.wireOp",EDGE,"E12.9.14.0"),sQuery(id+"F7.wireOp",EDGE,"E12.9.14.1"),sQuery(id+"F7.wireOp",EDGE,"E12.9.14.2"),sQuery(id+"F7.wireOp",EDGE,"E12.9.14.3"),sQuery(id+"F7.wireOp",EDGE,"E12.9.15.0"),sQuery(id+"F7.wireOp",EDGE,"E12.9.15.1"),sQuery(id+"F7.wireOp",EDGE,"E12.9.15.2"),sQuery(id+"F7.wireOp",EDGE,"E12.9.15.3"),sQuery(id+"F7.wireOp",EDGE,"E12.10.0.0"),sQuery(id+"F7.wireOp",EDGE,"E12.10.0.1"),sQuery(id+"F7.wireOp",EDGE,"E12.10.0.2"),sQuery(id+"F7.wireOp",EDGE,"E12.10.0.3"),sQuery(id+"F7.wireOp",EDGE,"E12.10.1.0"),sQuery(id+"F7.wireOp",EDGE,"E12.10.1.1"),sQuery(id+"F7.wireOp",EDGE,"E12.10.1.2"),sQuery(id+"F7.wireOp",EDGE,"E12.10.1.3"),sQuery(id+"F7.wireOp",EDGE,"E12.10.2.0"),sQuery(id+"F7.wireOp",EDGE,"E12.10.2.1"),sQuery(id+"F7.wireOp",EDGE,"E12.10.2.2"),sQuery(id+"F7.wireOp",EDGE,"E12.10.2.3"),sQuery(id+"F7.wireOp",EDGE,"E12.10.3.0"),sQuery(id+"F7.wireOp",EDGE,"E12.10.3.1"),sQuery(id+"F7.wireOp",EDGE,"E12.10.3.2"),sQuery(id+"F7.wireOp",EDGE,"E12.10.3.3"),sQuery(id+"F7.wireOp",EDGE,"E12.10.4.0"),sQuery(id+"F7.wireOp",EDGE,"E12.10.4.1"),sQuery(id+"F7.wireOp",EDGE,"E12.10.4.2"),sQuery(id+"F7.wireOp",EDGE,"E12.10.4.3"),sQuery(id+"F7.wireOp",EDGE,"E12.10.5.0"),sQuery(id+"F7.wireOp",EDGE,"E12.10.5.1"),sQuery(id+"F7.wireOp",EDGE,"E12.10.5.2"),sQuery(id+"F7.wireOp",EDGE,"E12.10.5.3"),sQuery(id+"F7.wireOp",EDGE,"E12.10.6.0"),sQuery(id+"F7.wireOp",EDGE,"E12.10.6.1"),sQuery(id+"F7.wireOp",EDGE,"E12.10.6.2"),sQuery(id+"F7.wireOp",EDGE,"E12.10.6.3"),sQuery(id+"F7.wireOp",EDGE,"E12.10.7.0"),sQuery(id+"F7.wireOp",EDGE,"E12.10.7.1"),sQuery(id+"F7.wireOp",EDGE,"E12.10.7.2"),sQuery(id+"F7.wireOp",EDGE,"E12.10.7.3"),sQuery(id+"F7.wireOp",EDGE,"E12.10.8.0"),sQuery(id+"F7.wireOp",EDGE,"E12.10.8.1"),sQuery(id+"F7.wireOp",EDGE,"E12.10.8.2"),sQuery(id+"F7.wireOp",EDGE,"E12.10.8.3"),sQuery(id+"F7.wireOp",EDGE,"E12.10.9.0"),sQuery(id+"F7.wireOp",EDGE,"E12.10.9.1"),sQuery(id+"F7.wireOp",EDGE,"E12.10.9.2"),sQuery(id+"F7.wireOp",EDGE,"E12.10.9.3"),sQuery(id+"F7.wireOp",EDGE,"E12.10.10.0"),sQuery(id+"F7.wireOp",EDGE,"E12.10.10.1"),sQuery(id+"F7.wireOp",EDGE,"E12.10.10.2"),sQuery(id+"F7.wireOp",EDGE,"E12.10.10.3"),sQuery(id+"F7.wireOp",EDGE,"E12.10.11.0"),sQuery(id+"F7.wireOp",EDGE,"E12.10.11.1"),sQuery(id+"F7.wireOp",EDGE,"E12.10.11.2"),sQuery(id+"F7.wireOp",EDGE,"E12.10.11.3"),sQuery(id+"F7.wireOp",EDGE,"E12.10.12.0"),sQuery(id+"F7.wireOp",EDGE,"E12.10.12.1"),sQuery(id+"F7.wireOp",EDGE,"E12.10.12.2"),sQuery(id+"F7.wireOp",EDGE,"E12.10.12.3"),sQuery(id+"F7.wireOp",EDGE,"E12.10.13.0"),sQuery(id+"F7.wireOp",EDGE,"E12.10.13.1"),sQuery(id+"F7.wireOp",EDGE,"E12.10.13.2"),sQuery(id+"F7.wireOp",EDGE,"E12.10.13.3"),sQuery(id+"F7.wireOp",EDGE,"E12.10.14.0"),sQuery(id+"F7.wireOp",EDGE,"E12.10.14.1"),sQuery(id+"F7.wireOp",EDGE,"E12.10.14.2"),sQuery(id+"F7.wireOp",EDGE,"E12.10.14.3"),sQuery(id+"F7.wireOp",EDGE,"E12.10.15.0"),sQuery(id+"F7.wireOp",EDGE,"E12.10.15.1"),sQuery(id+"F7.wireOp",EDGE,"E12.10.15.2"),sQuery(id+"F7.wireOp",EDGE,"E12.10.15.3"),sQuery(id+"F7.wireOp",EDGE,"E12.11.0.0"),sQuery(id+"F7.wireOp",EDGE,"E12.11.0.1"),sQuery(id+"F7.wireOp",EDGE,"E12.11.0.2"),sQuery(id+"F7.wireOp",EDGE,"E12.11.0.3"),sQuery(id+"F7.wireOp",EDGE,"E12.11.1.0"),sQuery(id+"F7.wireOp",EDGE,"E12.11.1.1"),sQuery(id+"F7.wireOp",EDGE,"E12.11.1.2"),sQuery(id+"F7.wireOp",EDGE,"E12.11.1.3"),sQuery(id+"F7.wireOp",EDGE,"E12.11.2.0"),sQuery(id+"F7.wireOp",EDGE,"E12.11.2.1"),sQuery(id+"F7.wireOp",EDGE,"E12.11.2.2"),sQuery(id+"F7.wireOp",EDGE,"E12.11.2.3"),sQuery(id+"F7.wireOp",EDGE,"E12.11.3.0"),sQuery(id+"F7.wireOp",EDGE,"E12.11.3.1"),sQuery(id+"F7.wireOp",EDGE,"E12.11.3.2"),sQuery(id+"F7.wireOp",EDGE,"E12.11.3.3"),sQuery(id+"F7.wireOp",EDGE,"E12.11.4.0"),sQuery(id+"F7.wireOp",EDGE,"E12.11.4.1"),sQuery(id+"F7.wireOp",EDGE,"E12.11.4.2"),sQuery(id+"F7.wireOp",EDGE,"E12.11.4.3"),sQuery(id+"F7.wireOp",EDGE,"E12.11.5.0"),sQuery(id+"F7.wireOp",EDGE,"E12.11.5.1"),sQuery(id+"F7.wireOp",EDGE,"E12.11.5.2"),sQuery(id+"F7.wireOp",EDGE,"E12.11.5.3"),sQuery(id+"F7.wireOp",EDGE,"E12.11.6.0"),sQuery(id+"F7.wireOp",EDGE,"E12.11.6.1"),sQuery(id+"F7.wireOp",EDGE,"E12.11.6.2"),sQuery(id+"F7.wireOp",EDGE,"E12.11.6.3"),sQuery(id+"F7.wireOp",EDGE,"E12.11.7.0"),sQuery(id+"F7.wireOp",EDGE,"E12.11.7.1"),sQuery(id+"F7.wireOp",EDGE,"E12.11.7.2"),sQuery(id+"F7.wireOp",EDGE,"E12.11.7.3"),sQuery(id+"F7.wireOp",EDGE,"E12.11.8.0"),sQuery(id+"F7.wireOp",EDGE,"E12.11.8.1"),sQuery(id+"F7.wireOp",EDGE,"E12.11.8.2"),sQuery(id+"F7.wireOp",EDGE,"E12.11.8.3"),sQuery(id+"F7.wireOp",EDGE,"E12.11.9.0"),sQuery(id+"F7.wireOp",EDGE,"E12.11.9.1"),sQuery(id+"F7.wireOp",EDGE,"E12.11.9.2"),sQuery(id+"F7.wireOp",EDGE,"E12.11.9.3"),sQuery(id+"F7.wireOp",EDGE,"E12.11.10.0"),sQuery(id+"F7.wireOp",EDGE,"E12.11.10.1"),sQuery(id+"F7.wireOp",EDGE,"E12.11.10.2"),sQuery(id+"F7.wireOp",EDGE,"E12.11.10.3"),sQuery(id+"F7.wireOp",EDGE,"E12.11.11.0"),sQuery(id+"F7.wireOp",EDGE,"E12.11.11.1"),sQuery(id+"F7.wireOp",EDGE,"E12.11.11.2"),sQuery(id+"F7.wireOp",EDGE,"E12.11.11.3"),sQuery(id+"F7.wireOp",EDGE,"E12.11.12.0"),sQuery(id+"F7.wireOp",EDGE,"E12.11.12.1"),sQuery(id+"F7.wireOp",EDGE,"E12.11.12.2"),sQuery(id+"F7.wireOp",EDGE,"E12.11.12.3"),sQuery(id+"F7.wireOp",EDGE,"E12.11.13.0"),sQuery(id+"F7.wireOp",EDGE,"E12.11.13.1"),sQuery(id+"F7.wireOp",EDGE,"E12.11.13.2"),sQuery(id+"F7.wireOp",EDGE,"E12.11.13.3"),sQuery(id+"F7.wireOp",EDGE,"E12.11.14.0"),sQuery(id+"F7.wireOp",EDGE,"E12.11.14.1"),sQuery(id+"F7.wireOp",EDGE,"E12.11.14.2"),sQuery(id+"F7.wireOp",EDGE,"E12.11.14.3"),sQuery(id+"F7.wireOp",EDGE,"E12.11.15.0"),sQuery(id+"F7.wireOp",EDGE,"E12.11.15.1"),sQuery(id+"F7.wireOp",EDGE,"E12.11.15.2"),sQuery(id+"F7.wireOp",EDGE,"E12.11.15.3"),sQuery(id+"F7.wireOp",EDGE,"E12.12.0.0"),sQuery(id+"F7.wireOp",EDGE,"E12.12.0.1"),sQuery(id+"F7.wireOp",EDGE,"E12.12.0.2"),sQuery(id+"F7.wireOp",EDGE,"E12.12.0.3"),sQuery(id+"F7.wireOp",EDGE,"E12.12.1.0"),sQuery(id+"F7.wireOp",EDGE,"E12.12.1.1"),sQuery(id+"F7.wireOp",EDGE,"E12.12.1.2"),sQuery(id+"F7.wireOp",EDGE,"E12.12.1.3"),sQuery(id+"F7.wireOp",EDGE,"E12.12.2.0"),sQuery(id+"F7.wireOp",EDGE,"E12.12.2.1"),sQuery(id+"F7.wireOp",EDGE,"E12.12.2.2"),sQuery(id+"F7.wireOp",EDGE,"E12.12.2.3"),sQuery(id+"F7.wireOp",EDGE,"E12.12.3.0"),sQuery(id+"F7.wireOp",EDGE,"E12.12.3.1"),sQuery(id+"F7.wireOp",EDGE,"E12.12.3.2"),sQuery(id+"F7.wireOp",EDGE,"E12.12.3.3"),sQuery(id+"F7.wireOp",EDGE,"E12.12.4.0"),sQuery(id+"F7.wireOp",EDGE,"E12.12.4.1"),sQuery(id+"F7.wireOp",EDGE,"E12.12.4.2"),sQuery(id+"F7.wireOp",EDGE,"E12.12.4.3"),sQuery(id+"F7.wireOp",EDGE,"E12.12.5.0"),sQuery(id+"F7.wireOp",EDGE,"E12.12.5.1"),sQuery(id+"F7.wireOp",EDGE,"E12.12.5.2"),sQuery(id+"F7.wireOp",EDGE,"E12.12.5.3"),sQuery(id+"F7.wireOp",EDGE,"E12.12.6.0"),sQuery(id+"F7.wireOp",EDGE,"E12.12.6.1"),sQuery(id+"F7.wireOp",EDGE,"E12.12.6.2"),sQuery(id+"F7.wireOp",EDGE,"E12.12.6.3"),sQuery(id+"F7.wireOp",EDGE,"E12.12.7.0"),sQuery(id+"F7.wireOp",EDGE,"E12.12.7.1"),sQuery(id+"F7.wireOp",EDGE,"E12.12.7.2"),sQuery(id+"F7.wireOp",EDGE,"E12.12.7.3"),sQuery(id+"F7.wireOp",EDGE,"E12.12.8.0"),sQuery(id+"F7.wireOp",EDGE,"E12.12.8.1"),sQuery(id+"F7.wireOp",EDGE,"E12.12.8.2"),sQuery(id+"F7.wireOp",EDGE,"E12.12.8.3"),sQuery(id+"F7.wireOp",EDGE,"E12.12.9.0"),sQuery(id+"F7.wireOp",EDGE,"E12.12.9.1"),sQuery(id+"F7.wireOp",EDGE,"E12.12.9.2"),sQuery(id+"F7.wireOp",EDGE,"E12.12.9.3"),sQuery(id+"F7.wireOp",EDGE,"E12.12.10.0"),sQuery(id+"F7.wireOp",EDGE,"E12.12.10.1"),sQuery(id+"F7.wireOp",EDGE,"E12.12.10.2"),sQuery(id+"F7.wireOp",EDGE,"E12.12.10.3"),sQuery(id+"F7.wireOp",EDGE,"E12.12.11.0"),sQuery(id+"F7.wireOp",EDGE,"E12.12.11.1"),sQuery(id+"F7.wireOp",EDGE,"E12.12.11.2"),sQuery(id+"F7.wireOp",EDGE,"E12.12.11.3"),sQuery(id+"F7.wireOp",EDGE,"E12.12.12.0"),sQuery(id+"F7.wireOp",EDGE,"E12.12.12.1"),sQuery(id+"F7.wireOp",EDGE,"E12.12.12.2"),sQuery(id+"F7.wireOp",EDGE,"E12.12.12.3"),sQuery(id+"F7.wireOp",EDGE,"E12.12.13.0"),sQuery(id+"F7.wireOp",EDGE,"E12.12.13.1"),sQuery(id+"F7.wireOp",EDGE,"E12.12.13.2"),sQuery(id+"F7.wireOp",EDGE,"E12.12.13.3"),sQuery(id+"F7.wireOp",EDGE,"E12.12.14.0"),sQuery(id+"F7.wireOp",EDGE,"E12.12.14.1"),sQuery(id+"F7.wireOp",EDGE,"E12.12.14.2"),sQuery(id+"F7.wireOp",EDGE,"E12.12.14.3"),sQuery(id+"F7.wireOp",EDGE,"E12.12.15.0"),sQuery(id+"F7.wireOp",EDGE,"E12.12.15.1"),sQuery(id+"F7.wireOp",EDGE,"E12.12.15.2"),sQuery(id+"F7.wireOp",EDGE,"E12.12.15.3"),sQuery(id+"F7.wireOp",EDGE,"E12.13.0.0"),sQuery(id+"F7.wireOp",EDGE,"E12.13.0.1"),sQuery(id+"F7.wireOp",EDGE,"E12.13.0.2"),sQuery(id+"F7.wireOp",EDGE,"E12.13.0.3"),sQuery(id+"F7.wireOp",EDGE,"E12.13.1.0"),sQuery(id+"F7.wireOp",EDGE,"E12.13.1.1"),sQuery(id+"F7.wireOp",EDGE,"E12.13.1.2"),sQuery(id+"F7.wireOp",EDGE,"E12.13.1.3"),sQuery(id+"F7.wireOp",EDGE,"E12.13.2.0"),sQuery(id+"F7.wireOp",EDGE,"E12.13.2.1"),sQuery(id+"F7.wireOp",EDGE,"E12.13.2.2"),sQuery(id+"F7.wireOp",EDGE,"E12.13.2.3"),sQuery(id+"F7.wireOp",EDGE,"E12.13.3.0"),sQuery(id+"F7.wireOp",EDGE,"E12.13.3.1"),sQuery(id+"F7.wireOp",EDGE,"E12.13.3.2"),sQuery(id+"F7.wireOp",EDGE,"E12.13.3.3"),sQuery(id+"F7.wireOp",EDGE,"E12.13.4.0"),sQuery(id+"F7.wireOp",EDGE,"E12.13.4.1"),sQuery(id+"F7.wireOp",EDGE,"E12.13.4.2"),sQuery(id+"F7.wireOp",EDGE,"E12.13.4.3"),sQuery(id+"F7.wireOp",EDGE,"E12.13.5.0"),sQuery(id+"F7.wireOp",EDGE,"E12.13.5.1"),sQuery(id+"F7.wireOp",EDGE,"E12.13.5.2"),sQuery(id+"F7.wireOp",EDGE,"E12.13.5.3"),sQuery(id+"F7.wireOp",EDGE,"E12.13.6.0"),sQuery(id+"F7.wireOp",EDGE,"E12.13.6.1"),sQuery(id+"F7.wireOp",EDGE,"E12.13.6.2"),sQuery(id+"F7.wireOp",EDGE,"E12.13.6.3"),sQuery(id+"F7.wireOp",EDGE,"E12.13.7.0"),sQuery(id+"F7.wireOp",EDGE,"E12.13.7.1"),sQuery(id+"F7.wireOp",EDGE,"E12.13.7.2"),sQuery(id+"F7.wireOp",EDGE,"E12.13.7.3"),sQuery(id+"F7.wireOp",EDGE,"E12.13.8.0"),sQuery(id+"F7.wireOp",EDGE,"E12.13.8.1"),sQuery(id+"F7.wireOp",EDGE,"E12.13.8.2"),sQuery(id+"F7.wireOp",EDGE,"E12.13.8.3"),sQuery(id+"F7.wireOp",EDGE,"E12.13.9.0"),sQuery(id+"F7.wireOp",EDGE,"E12.13.9.1"),sQuery(id+"F7.wireOp",EDGE,"E12.13.9.2"),sQuery(id+"F7.wireOp",EDGE,"E12.13.9.3"),sQuery(id+"F7.wireOp",EDGE,"E12.13.10.0"),sQuery(id+"F7.wireOp",EDGE,"E12.13.10.1"),sQuery(id+"F7.wireOp",EDGE,"E12.13.10.2"),sQuery(id+"F7.wireOp",EDGE,"E12.13.10.3"),sQuery(id+"F7.wireOp",EDGE,"E12.13.11.0"),sQuery(id+"F7.wireOp",EDGE,"E12.13.11.1"),sQuery(id+"F7.wireOp",EDGE,"E12.13.11.2"),sQuery(id+"F7.wireOp",EDGE,"E12.13.11.3"),sQuery(id+"F7.wireOp",EDGE,"E12.13.12.0"),sQuery(id+"F7.wireOp",EDGE,"E12.13.12.1"),sQuery(id+"F7.wireOp",EDGE,"E12.13.12.2"),sQuery(id+"F7.wireOp",EDGE,"E12.13.12.3"),sQuery(id+"F7.wireOp",EDGE,"E12.13.13.0"),sQuery(id+"F7.wireOp",EDGE,"E12.13.13.1"),sQuery(id+"F7.wireOp",EDGE,"E12.13.13.2"),sQuery(id+"F7.wireOp",EDGE,"E12.13.13.3"),sQuery(id+"F7.wireOp",EDGE,"E12.13.14.0"),sQuery(id+"F7.wireOp",EDGE,"E12.13.14.1"),sQuery(id+"F7.wireOp",EDGE,"E12.13.14.2"),sQuery(id+"F7.wireOp",EDGE,"E12.13.14.3"),sQuery(id+"F7.wireOp",EDGE,"E12.13.15.0"),sQuery(id+"F7.wireOp",EDGE,"E12.13.15.1"),sQuery(id+"F7.wireOp",EDGE,"E12.13.15.2"),sQuery(id+"F7.wireOp",EDGE,"E12.13.15.3"),sQuery(id+"F7.wireOp",EDGE,"E12.14.0.0"),sQuery(id+"F7.wireOp",EDGE,"E12.14.0.1"),sQuery(id+"F7.wireOp",EDGE,"E12.14.0.2"),sQuery(id+"F7.wireOp",EDGE,"E12.14.0.3"),sQuery(id+"F7.wireOp",EDGE,"E12.14.1.0"),sQuery(id+"F7.wireOp",EDGE,"E12.14.1.1"),sQuery(id+"F7.wireOp",EDGE,"E12.14.1.2"),sQuery(id+"F7.wireOp",EDGE,"E12.14.1.3"),sQuery(id+"F7.wireOp",EDGE,"E12.14.2.0"),sQuery(id+"F7.wireOp",EDGE,"E12.14.2.1"),sQuery(id+"F7.wireOp",EDGE,"E12.14.2.2"),sQuery(id+"F7.wireOp",EDGE,"E12.14.2.3"),sQuery(id+"F7.wireOp",EDGE,"E12.14.3.0"),sQuery(id+"F7.wireOp",EDGE,"E12.14.3.1"),sQuery(id+"F7.wireOp",EDGE,"E12.14.3.2"),sQuery(id+"F7.wireOp",EDGE,"E12.14.3.3"),sQuery(id+"F7.wireOp",EDGE,"E12.14.4.0"),sQuery(id+"F7.wireOp",EDGE,"E12.14.4.1"),sQuery(id+"F7.wireOp",EDGE,"E12.14.4.2"),sQuery(id+"F7.wireOp",EDGE,"E12.14.4.3"),sQuery(id+"F7.wireOp",EDGE,"E12.14.5.0"),sQuery(id+"F7.wireOp",EDGE,"E12.14.5.1"),sQuery(id+"F7.wireOp",EDGE,"E12.14.5.2"),sQuery(id+"F7.wireOp",EDGE,"E12.14.5.3"),sQuery(id+"F7.wireOp",EDGE,"E12.14.6.0"),sQuery(id+"F7.wireOp",EDGE,"E12.14.6.1"),sQuery(id+"F7.wireOp",EDGE,"E12.14.6.2"),sQuery(id+"F7.wireOp",EDGE,"E12.14.6.3"),sQuery(id+"F7.wireOp",EDGE,"E12.14.7.0"),sQuery(id+"F7.wireOp",EDGE,"E12.14.7.1"),sQuery(id+"F7.wireOp",EDGE,"E12.14.7.2"),sQuery(id+"F7.wireOp",EDGE,"E12.14.7.3"),sQuery(id+"F7.wireOp",EDGE,"E12.14.8.0"),sQuery(id+"F7.wireOp",EDGE,"E12.14.8.1"),sQuery(id+"F7.wireOp",EDGE,"E12.14.8.2"),sQuery(id+"F7.wireOp",EDGE,"E12.14.8.3"),sQuery(id+"F7.wireOp",EDGE,"E12.14.9.0"),sQuery(id+"F7.wireOp",EDGE,"E12.14.9.1"),sQuery(id+"F7.wireOp",EDGE,"E12.14.9.2"),sQuery(id+"F7.wireOp",EDGE,"E12.14.9.3"),sQuery(id+"F7.wireOp",EDGE,"E12.14.10.0"),sQuery(id+"F7.wireOp",EDGE,"E12.14.10.1"),sQuery(id+"F7.wireOp",EDGE,"E12.14.10.2"),sQuery(id+"F7.wireOp",EDGE,"E12.14.10.3"),sQuery(id+"F7.wireOp",EDGE,"E12.14.11.0"),sQuery(id+"F7.wireOp",EDGE,"E12.14.11.1"),sQuery(id+"F7.wireOp",EDGE,"E12.14.11.2"),sQuery(id+"F7.wireOp",EDGE,"E12.14.11.3"),sQuery(id+"F7.wireOp",EDGE,"E12.14.12.0"),sQuery(id+"F7.wireOp",EDGE,"E12.14.12.1"),sQuery(id+"F7.wireOp",EDGE,"E12.14.12.2"),sQuery(id+"F7.wireOp",EDGE,"E12.14.12.3"),sQuery(id+"F7.wireOp",EDGE,"E12.14.13.0"),sQuery(id+"F7.wireOp",EDGE,"E12.14.13.1"),sQuery(id+"F7.wireOp",EDGE,"E12.14.13.2"),sQuery(id+"F7.wireOp",EDGE,"E12.14.13.3"),sQuery(id+"F7.wireOp",EDGE,"E12.14.14.0"),sQuery(id+"F7.wireOp",EDGE,"E12.14.14.1"),sQuery(id+"F7.wireOp",EDGE,"E12.14.14.2"),sQuery(id+"F7.wireOp",EDGE,"E12.14.14.3"),sQuery(id+"F7.wireOp",EDGE,"E12.14.15.0"),sQuery(id+"F7.wireOp",EDGE,"E12.14.15.1"),sQuery(id+"F7.wireOp",EDGE,"E12.14.15.2"),sQuery(id+"F7.wireOp",EDGE,"E12.14.15.3"),sQuery(id+"F7.wireOp",EDGE,"E12.15.0.0"),sQuery(id+"F7.wireOp",EDGE,"E12.15.0.1"),sQuery(id+"F7.wireOp",EDGE,"E12.15.0.2"),sQuery(id+"F7.wireOp",EDGE,"E12.15.0.3"),sQuery(id+"F7.wireOp",EDGE,"E12.15.1.0"),sQuery(id+"F7.wireOp",EDGE,"E12.15.1.1"),sQuery(id+"F7.wireOp",EDGE,"E12.15.1.2"),sQuery(id+"F7.wireOp",EDGE,"E12.15.1.3"),sQuery(id+"F7.wireOp",EDGE,"E12.15.2.0"),sQuery(id+"F7.wireOp",EDGE,"E12.15.2.1"),sQuery(id+"F7.wireOp",EDGE,"E12.15.2.2"),sQuery(id+"F7.wireOp",EDGE,"E12.15.2.3"),sQuery(id+"F7.wireOp",EDGE,"E12.15.3.0"),sQuery(id+"F7.wireOp",EDGE,"E12.15.3.1"),sQuery(id+"F7.wireOp",EDGE,"E12.15.3.2"),sQuery(id+"F7.wireOp",EDGE,"E12.15.3.3"),sQuery(id+"F7.wireOp",EDGE,"E12.15.4.0"),sQuery(id+"F7.wireOp",EDGE,"E12.15.4.1"),sQuery(id+"F7.wireOp",EDGE,"E12.15.4.2"),sQuery(id+"F7.wireOp",EDGE,"E12.15.4.3"),sQuery(id+"F7.wireOp",EDGE,"E12.15.5.0"),sQuery(id+"F7.wireOp",EDGE,"E12.15.5.1"),sQuery(id+"F7.wireOp",EDGE,"E12.15.5.2"),sQuery(id+"F7.wireOp",EDGE,"E12.15.5.3"),sQuery(id+"F7.wireOp",EDGE,"E12.15.6.0"),sQuery(id+"F7.wireOp",EDGE,"E12.15.6.1"),sQuery(id+"F7.wireOp",EDGE,"E12.15.6.2"),sQuery(id+"F7.wireOp",EDGE,"E12.15.6.3"),sQuery(id+"F7.wireOp",EDGE,"E12.15.7.0"),sQuery(id+"F7.wireOp",EDGE,"E12.15.7.1"),sQuery(id+"F7.wireOp",EDGE,"E12.15.7.2"),sQuery(id+"F7.wireOp",EDGE,"E12.15.7.3"),sQuery(id+"F7.wireOp",EDGE,"E12.15.8.0"),sQuery(id+"F7.wireOp",EDGE,"E12.15.8.1"),sQuery(id+"F7.wireOp",EDGE,"E12.15.8.2"),sQuery(id+"F7.wireOp",EDGE,"E12.15.8.3"),sQuery(id+"F7.wireOp",EDGE,"E12.15.9.0"),sQuery(id+"F7.wireOp",EDGE,"E12.15.9.1"),sQuery(id+"F7.wireOp",EDGE,"E12.15.9.2"),sQuery(id+"F7.wireOp",EDGE,"E12.15.9.3"),sQuery(id+"F7.wireOp",EDGE,"E12.15.10.0"),sQuery(id+"F7.wireOp",EDGE,"E12.15.10.1"),sQuery(id+"F7.wireOp",EDGE,"E12.15.10.2"),sQuery(id+"F7.wireOp",EDGE,"E12.15.10.3"),sQuery(id+"F7.wireOp",EDGE,"E12.15.11.0"),sQuery(id+"F7.wireOp",EDGE,"E12.15.11.1"),sQuery(id+"F7.wireOp",EDGE,"E12.15.11.2"),sQuery(id+"F7.wireOp",EDGE,"E12.15.11.3"),sQuery(id+"F7.wireOp",EDGE,"E12.15.12.0"),sQuery(id+"F7.wireOp",EDGE,"E12.15.12.1"),sQuery(id+"F7.wireOp",EDGE,"E12.15.12.2"),sQuery(id+"F7.wireOp",EDGE,"E12.15.12.3"),sQuery(id+"F7.wireOp",EDGE,"E12.15.13.0"),sQuery(id+"F7.wireOp",EDGE,"E12.15.13.1"),sQuery(id+"F7.wireOp",EDGE,"E12.15.13.2"),sQuery(id+"F7.wireOp",EDGE,"E12.15.13.3"),sQuery(id+"F7.wireOp",EDGE,"E12.15.14.0"),sQuery(id+"F7.wireOp",EDGE,"E12.15.14.1"),sQuery(id+"F7.wireOp",EDGE,"E12.15.14.2"),sQuery(id+"F7.wireOp",EDGE,"E12.15.14.3"),sQuery(id+"F7.wireOp",EDGE,"E12.15.15.0"),sQuery(id+"F7.wireOp",EDGE,"E12.15.15.1"),sQuery(id+"F7.wireOp",EDGE,"E12.15.15.2"),sQuery(id+"F7.wireOp",EDGE,"E12.15.15.3")])],"isStart":false});
            var sketch = newSketch(context, id + "F22", { "sketchPlane" : qUnion([Q0])});
            skCircle(sketch, "E35", {"center": v(-345, -345) * mm, "radius": 2.5 * mm});
            skCircle(sketch, "E36.0.1.0", {"center": v(-345, 345) * mm, "radius": 2.5 * mm});
            skCircle(sketch, "E36.1.0.0", {"center": v(345, -345) * mm, "radius": 2.5 * mm});
            skCircle(sketch, "E36.1.1.0", {"center": v(345, 345) * mm, "radius": 2.5 * mm});
            skLineSegment(sketch, "E36.direction1", {"start": v(-345, -345) * mm, "end": v(345, -345) * mm, "construction": true});
            skLineSegment(sketch, "E36.direction2", {"start": v(-345, -345) * mm, "end": v(-345, 345) * mm, "construction": true});
            skSolve(sketch);
        }
        {
            var Q0;
            Q0 = qSketchRegion(id + "F22", true);
            extrude(context, id + "F23", {"entities" : qUnion([Q0]), "depth" : -50 * mm, "offsetDistance" : 25 * mm});
        }
        {
            var Q0;
            Q0=makeQuery(id+"F23.opExtrude","SWEPT_BODY",BODY,{"disambiguationData":[OSD([sQuery(id+"F22.wireOp",EDGE,"E36.1.0.0")])]});
            var Q1;
            Q1=makeQuery(id+"F23.opExtrude","SWEPT_BODY",BODY,{"disambiguationData":[OSD([sQuery(id+"F22.wireOp",EDGE,"E36.1.1.0")])]});
            var Q2;
            Q2=makeQuery(id+"F23.opExtrude","SWEPT_BODY",BODY,{"disambiguationData":[OSD([sQuery(id+"F22.wireOp",EDGE,"E35")])]});
            var Q3;
            Q3=makeQuery(id+"F23.opExtrude","SWEPT_BODY",BODY,{"disambiguationData":[OSD([sQuery(id+"F22.wireOp",EDGE,"E36.0.1.0")])]});
            var Q4;
            Q4=makeQuery(id+"F4.opExtrude","SWEPT_BODY",BODY,{"disambiguationData":[OSD([sQuery(id+"F0.wireOp",EDGE,"E0.bottom"),sQuery(id+"F0.wireOp",EDGE,"E0.top"),sQuery(id+"F0.wireOp",EDGE,"E0.left"),sQuery(id+"F0.wireOp",EDGE,"E0.right"),sQuery(id+"F0.wireOp",EDGE,"E2.bottom"),sQuery(id+"F0.wireOp",EDGE,"E2.top"),sQuery(id+"F0.wireOp",EDGE,"E2.left"),sQuery(id+"F0.wireOp",EDGE,"E2.right"),sQuery(id+"F0.wireOp",EDGE,"E3.0.1.0"),sQuery(id+"F0.wireOp",EDGE,"E3.0.1.1"),sQuery(id+"F0.wireOp",EDGE,"E3.0.1.2"),sQuery(id+"F0.wireOp",EDGE,"E3.0.1.3"),sQuery(id+"F0.wireOp",EDGE,"E4.0.0.2"),sQuery(id+"F0.wireOp",EDGE,"E4.3.0.2"),sQuery(id+"F0.wireOp",EDGE,"E4.6.0.2"),sQuery(id+"F0.wireOp",EDGE,"E4.9.0.2"),sQuery(id+"F0.wireOp",EDGE,"E4.0.0.3"),sQuery(id+"F0.wireOp",EDGE,"E4.3.0.3"),sQuery(id+"F0.wireOp",EDGE,"E4.6.0.3"),sQuery(id+"F0.wireOp",EDGE,"E4.9.0.3"),sQuery(id+"F0.wireOp",EDGE,"E4.0.0.4"),sQuery(id+"F0.wireOp",EDGE,"E4.3.0.4"),sQuery(id+"F0.wireOp",EDGE,"E4.6.0.4"),sQuery(id+"F0.wireOp",EDGE,"E4.9.0.4"),sQuery(id+"F0.wireOp",EDGE,"E4.0.0.5"),sQuery(id+"F0.wireOp",EDGE,"E4.3.0.5"),sQuery(id+"F0.wireOp",EDGE,"E4.6.0.5"),sQuery(id+"F0.wireOp",EDGE,"E4.9.0.5"),sQuery(id+"F0.wireOp",EDGE,"E4.0.0.6"),sQuery(id+"F0.wireOp",EDGE,"E4.3.0.6"),sQuery(id+"F0.wireOp",EDGE,"E4.6.0.6"),sQuery(id+"F0.wireOp",EDGE,"E4.9.0.6"),sQuery(id+"F0.wireOp",EDGE,"E4.0.0.7"),sQuery(id+"F0.wireOp",EDGE,"E4.3.0.7"),sQuery(id+"F0.wireOp",EDGE,"E4.6.0.7"),sQuery(id+"F0.wireOp",EDGE,"E4.9.0.7"),sQuery(id+"F0.wireOp",EDGE,"E4.0.0.8"),sQuery(id+"F0.wireOp",EDGE,"E4.3.0.8"),sQuery(id+"F0.wireOp",EDGE,"E4.6.0.8"),sQuery(id+"F0.wireOp",EDGE,"E4.9.0.8"),sQuery(id+"F0.wireOp",EDGE,"E4.0.0.9"),sQuery(id+"F0.wireOp",EDGE,"E4.3.0.9"),sQuery(id+"F0.wireOp",EDGE,"E4.6.0.9"),sQuery(id+"F0.wireOp",EDGE,"E4.9.0.9"),sQuery(id+"F0.wireOp",EDGE,"E4.0.0.10"),sQuery(id+"F0.wireOp",EDGE,"E4.3.0.10"),sQuery(id+"F0.wireOp",EDGE,"E4.6.0.10"),sQuery(id+"F0.wireOp",EDGE,"E4.9.0.10"),sQuery(id+"F0.wireOp",EDGE,"E4.0.0.11"),sQuery(id+"F0.wireOp",EDGE,"E4.3.0.11"),sQuery(id+"F0.wireOp",EDGE,"E4.6.0.11"),sQuery(id+"F0.wireOp",EDGE,"E4.9.0.11"),sQuery(id+"F0.wireOp",EDGE,"E4.0.0.12"),sQuery(id+"F0.wireOp",EDGE,"E4.3.0.12"),sQuery(id+"F0.wireOp",EDGE,"E4.6.0.12"),sQuery(id+"F0.wireOp",EDGE,"E4.9.0.12"),sQuery(id+"F0.wireOp",EDGE,"E4.0.0.13"),sQuery(id+"F0.wireOp",EDGE,"E4.3.0.13"),sQuery(id+"F0.wireOp",EDGE,"E4.6.0.13"),sQuery(id+"F0.wireOp",EDGE,"E4.9.0.13"),sQuery(id+"F0.wireOp",EDGE,"E4.0.0.14"),sQuery(id+"F0.wireOp",EDGE,"E4.3.0.14"),sQuery(id+"F0.wireOp",EDGE,"E4.6.0.14"),sQuery(id+"F0.wireOp",EDGE,"E4.9.0.14"),sQuery(id+"F0.wireOp",EDGE,"E4.0.0.15"),sQuery(id+"F0.wireOp",EDGE,"E4.3.0.15"),sQuery(id+"F0.wireOp",EDGE,"E4.6.0.15"),sQuery(id+"F0.wireOp",EDGE,"E4.9.0.15")])]});
            var Q5;
            Q5=makeQuery(id+"F6.opExtrude","SWEPT_BODY",BODY,{"disambiguationData":[OSD([sQuery(id+"F5.wireOp",EDGE,"E5.bottom"),sQuery(id+"F5.wireOp",EDGE,"E5.top"),sQuery(id+"F5.wireOp",EDGE,"E5.left"),sQuery(id+"F5.wireOp",EDGE,"E5.right")])]});
            var Q6;
            Q6=makeQuery(id+"F8.opExtrude","SWEPT_BODY",BODY,{"disambiguationData":[OSD([sQuery(id+"F7.wireOp",EDGE,"E9.bottom"),sQuery(id+"F7.wireOp",EDGE,"E9.top"),sQuery(id+"F7.wireOp",EDGE,"E9.left"),sQuery(id+"F7.wireOp",EDGE,"E9.right"),sQuery(id+"F7.wireOp",EDGE,"E11.bottom"),sQuery(id+"F7.wireOp",EDGE,"E11.top"),sQuery(id+"F7.wireOp",EDGE,"E11.left"),sQuery(id+"F7.wireOp",EDGE,"E11.right"),sQuery(id+"F7.wireOp",EDGE,"E12.0.1.0"),sQuery(id+"F7.wireOp",EDGE,"E12.0.1.1"),sQuery(id+"F7.wireOp",EDGE,"E12.0.1.2"),sQuery(id+"F7.wireOp",EDGE,"E12.0.1.3"),sQuery(id+"F7.wireOp",EDGE,"E12.0.2.0"),sQuery(id+"F7.wireOp",EDGE,"E12.0.2.1"),sQuery(id+"F7.wireOp",EDGE,"E12.0.2.2"),sQuery(id+"F7.wireOp",EDGE,"E12.0.2.3"),sQuery(id+"F7.wireOp",EDGE,"E12.0.3.0"),sQuery(id+"F7.wireOp",EDGE,"E12.0.3.1"),sQuery(id+"F7.wireOp",EDGE,"E12.0.3.2"),sQuery(id+"F7.wireOp",EDGE,"E12.0.3.3"),sQuery(id+"F7.wireOp",EDGE,"E12.0.4.0"),sQuery(id+"F7.wireOp",EDGE,"E12.0.4.1"),sQuery(id+"F7.wireOp",EDGE,"E12.0.4.2"),sQuery(id+"F7.wireOp",EDGE,"E12.0.4.3"),sQuery(id+"F7.wireOp",EDGE,"E12.0.5.0"),sQuery(id+"F7.wireOp",EDGE,"E12.0.5.1"),sQuery(id+"F7.wireOp",EDGE,"E12.0.5.2"),sQuery(id+"F7.wireOp",EDGE,"E12.0.5.3"),sQuery(id+"F7.wireOp",EDGE,"E12.0.6.0"),sQuery(id+"F7.wireOp",EDGE,"E12.0.6.1"),sQuery(id+"F7.wireOp",EDGE,"E12.0.6.2"),sQuery(id+"F7.wireOp",EDGE,"E12.0.6.3"),sQuery(id+"F7.wireOp",EDGE,"E12.0.7.0"),sQuery(id+"F7.wireOp",EDGE,"E12.0.7.1"),sQuery(id+"F7.wireOp",EDGE,"E12.0.7.2"),sQuery(id+"F7.wireOp",EDGE,"E12.0.7.3"),sQuery(id+"F7.wireOp",EDGE,"E12.0.8.0"),sQuery(id+"F7.wireOp",EDGE,"E12.0.8.1"),sQuery(id+"F7.wireOp",EDGE,"E12.0.8.2"),sQuery(id+"F7.wireOp",EDGE,"E12.0.8.3"),sQuery(id+"F7.wireOp",EDGE,"E12.0.9.0"),sQuery(id+"F7.wireOp",EDGE,"E12.0.9.1"),sQuery(id+"F7.wireOp",EDGE,"E12.0.9.2"),sQuery(id+"F7.wireOp",EDGE,"E12.0.9.3"),sQuery(id+"F7.wireOp",EDGE,"E12.0.10.0"),sQuery(id+"F7.wireOp",EDGE,"E12.0.10.1"),sQuery(id+"F7.wireOp",EDGE,"E12.0.10.2"),sQuery(id+"F7.wireOp",EDGE,"E12.0.10.3"),sQuery(id+"F7.wireOp",EDGE,"E12.0.11.0"),sQuery(id+"F7.wireOp",EDGE,"E12.0.11.1"),sQuery(id+"F7.wireOp",EDGE,"E12.0.11.2"),sQuery(id+"F7.wireOp",EDGE,"E12.0.11.3"),sQuery(id+"F7.wireOp",EDGE,"E12.0.12.0"),sQuery(id+"F7.wireOp",EDGE,"E12.0.12.1"),sQuery(id+"F7.wireOp",EDGE,"E12.0.12.2"),sQuery(id+"F7.wireOp",EDGE,"E12.0.12.3"),sQuery(id+"F7.wireOp",EDGE,"E12.0.13.0"),sQuery(id+"F7.wireOp",EDGE,"E12.0.13.1"),sQuery(id+"F7.wireOp",EDGE,"E12.0.13.2"),sQuery(id+"F7.wireOp",EDGE,"E12.0.13.3"),sQuery(id+"F7.wireOp",EDGE,"E12.0.14.0"),sQuery(id+"F7.wireOp",EDGE,"E12.0.14.1"),sQuery(id+"F7.wireOp",EDGE,"E12.0.14.2"),sQuery(id+"F7.wireOp",EDGE,"E12.0.14.3"),sQuery(id+"F7.wireOp",EDGE,"E12.0.15.0"),sQuery(id+"F7.wireOp",EDGE,"E12.0.15.1"),sQuery(id+"F7.wireOp",EDGE,"E12.0.15.2"),sQuery(id+"F7.wireOp",EDGE,"E12.0.15.3"),sQuery(id+"F7.wireOp",EDGE,"E12.1.0.0"),sQuery(id+"F7.wireOp",EDGE,"E12.1.0.1"),sQuery(id+"F7.wireOp",EDGE,"E12.1.0.2"),sQuery(id+"F7.wireOp",EDGE,"E12.1.0.3"),sQuery(id+"F7.wireOp",EDGE,"E12.1.1.0"),sQuery(id+"F7.wireOp",EDGE,"E12.1.1.1"),sQuery(id+"F7.wireOp",EDGE,"E12.1.1.2"),sQuery(id+"F7.wireOp",EDGE,"E12.1.1.3"),sQuery(id+"F7.wireOp",EDGE,"E12.1.2.0"),sQuery(id+"F7.wireOp",EDGE,"E12.1.2.1"),sQuery(id+"F7.wireOp",EDGE,"E12.1.2.2"),sQuery(id+"F7.wireOp",EDGE,"E12.1.2.3"),sQuery(id+"F7.wireOp",EDGE,"E12.1.3.0"),sQuery(id+"F7.wireOp",EDGE,"E12.1.3.1"),sQuery(id+"F7.wireOp",EDGE,"E12.1.3.2"),sQuery(id+"F7.wireOp",EDGE,"E12.1.3.3"),sQuery(id+"F7.wireOp",EDGE,"E12.1.4.0"),sQuery(id+"F7.wireOp",EDGE,"E12.1.4.1"),sQuery(id+"F7.wireOp",EDGE,"E12.1.4.2"),sQuery(id+"F7.wireOp",EDGE,"E12.1.4.3"),sQuery(id+"F7.wireOp",EDGE,"E12.1.5.0"),sQuery(id+"F7.wireOp",EDGE,"E12.1.5.1"),sQuery(id+"F7.wireOp",EDGE,"E12.1.5.2"),sQuery(id+"F7.wireOp",EDGE,"E12.1.5.3"),sQuery(id+"F7.wireOp",EDGE,"E12.1.6.0"),sQuery(id+"F7.wireOp",EDGE,"E12.1.6.1"),sQuery(id+"F7.wireOp",EDGE,"E12.1.6.2"),sQuery(id+"F7.wireOp",EDGE,"E12.1.6.3"),sQuery(id+"F7.wireOp",EDGE,"E12.1.7.0"),sQuery(id+"F7.wireOp",EDGE,"E12.1.7.1"),sQuery(id+"F7.wireOp",EDGE,"E12.1.7.2"),sQuery(id+"F7.wireOp",EDGE,"E12.1.7.3"),sQuery(id+"F7.wireOp",EDGE,"E12.1.8.0"),sQuery(id+"F7.wireOp",EDGE,"E12.1.8.1"),sQuery(id+"F7.wireOp",EDGE,"E12.1.8.2"),sQuery(id+"F7.wireOp",EDGE,"E12.1.8.3"),sQuery(id+"F7.wireOp",EDGE,"E12.1.9.0"),sQuery(id+"F7.wireOp",EDGE,"E12.1.9.1"),sQuery(id+"F7.wireOp",EDGE,"E12.1.9.2"),sQuery(id+"F7.wireOp",EDGE,"E12.1.9.3"),sQuery(id+"F7.wireOp",EDGE,"E12.1.10.0"),sQuery(id+"F7.wireOp",EDGE,"E12.1.10.1"),sQuery(id+"F7.wireOp",EDGE,"E12.1.10.2"),sQuery(id+"F7.wireOp",EDGE,"E12.1.10.3"),sQuery(id+"F7.wireOp",EDGE,"E12.1.11.0"),sQuery(id+"F7.wireOp",EDGE,"E12.1.11.1"),sQuery(id+"F7.wireOp",EDGE,"E12.1.11.2"),sQuery(id+"F7.wireOp",EDGE,"E12.1.11.3"),sQuery(id+"F7.wireOp",EDGE,"E12.1.12.0"),sQuery(id+"F7.wireOp",EDGE,"E12.1.12.1"),sQuery(id+"F7.wireOp",EDGE,"E12.1.12.2"),sQuery(id+"F7.wireOp",EDGE,"E12.1.12.3"),sQuery(id+"F7.wireOp",EDGE,"E12.1.13.0"),sQuery(id+"F7.wireOp",EDGE,"E12.1.13.1"),sQuery(id+"F7.wireOp",EDGE,"E12.1.13.2"),sQuery(id+"F7.wireOp",EDGE,"E12.1.13.3"),sQuery(id+"F7.wireOp",EDGE,"E12.1.14.0"),sQuery(id+"F7.wireOp",EDGE,"E12.1.14.1"),sQuery(id+"F7.wireOp",EDGE,"E12.1.14.2"),sQuery(id+"F7.wireOp",EDGE,"E12.1.14.3"),sQuery(id+"F7.wireOp",EDGE,"E12.1.15.0"),sQuery(id+"F7.wireOp",EDGE,"E12.1.15.1"),sQuery(id+"F7.wireOp",EDGE,"E12.1.15.2"),sQuery(id+"F7.wireOp",EDGE,"E12.1.15.3"),sQuery(id+"F7.wireOp",EDGE,"E12.2.0.0"),sQuery(id+"F7.wireOp",EDGE,"E12.2.0.1"),sQuery(id+"F7.wireOp",EDGE,"E12.2.0.2"),sQuery(id+"F7.wireOp",EDGE,"E12.2.0.3"),sQuery(id+"F7.wireOp",EDGE,"E12.2.1.0"),sQuery(id+"F7.wireOp",EDGE,"E12.2.1.1"),sQuery(id+"F7.wireOp",EDGE,"E12.2.1.2"),sQuery(id+"F7.wireOp",EDGE,"E12.2.1.3"),sQuery(id+"F7.wireOp",EDGE,"E12.2.2.0"),sQuery(id+"F7.wireOp",EDGE,"E12.2.2.1"),sQuery(id+"F7.wireOp",EDGE,"E12.2.2.2"),sQuery(id+"F7.wireOp",EDGE,"E12.2.2.3"),sQuery(id+"F7.wireOp",EDGE,"E12.2.3.0"),sQuery(id+"F7.wireOp",EDGE,"E12.2.3.1"),sQuery(id+"F7.wireOp",EDGE,"E12.2.3.2"),sQuery(id+"F7.wireOp",EDGE,"E12.2.3.3"),sQuery(id+"F7.wireOp",EDGE,"E12.2.4.0"),sQuery(id+"F7.wireOp",EDGE,"E12.2.4.1"),sQuery(id+"F7.wireOp",EDGE,"E12.2.4.2"),sQuery(id+"F7.wireOp",EDGE,"E12.2.4.3"),sQuery(id+"F7.wireOp",EDGE,"E12.2.5.0"),sQuery(id+"F7.wireOp",EDGE,"E12.2.5.1"),sQuery(id+"F7.wireOp",EDGE,"E12.2.5.2"),sQuery(id+"F7.wireOp",EDGE,"E12.2.5.3"),sQuery(id+"F7.wireOp",EDGE,"E12.2.6.0"),sQuery(id+"F7.wireOp",EDGE,"E12.2.6.1"),sQuery(id+"F7.wireOp",EDGE,"E12.2.6.2"),sQuery(id+"F7.wireOp",EDGE,"E12.2.6.3"),sQuery(id+"F7.wireOp",EDGE,"E12.2.7.0"),sQuery(id+"F7.wireOp",EDGE,"E12.2.7.1"),sQuery(id+"F7.wireOp",EDGE,"E12.2.7.2"),sQuery(id+"F7.wireOp",EDGE,"E12.2.7.3"),sQuery(id+"F7.wireOp",EDGE,"E12.2.8.0"),sQuery(id+"F7.wireOp",EDGE,"E12.2.8.1"),sQuery(id+"F7.wireOp",EDGE,"E12.2.8.2"),sQuery(id+"F7.wireOp",EDGE,"E12.2.8.3"),sQuery(id+"F7.wireOp",EDGE,"E12.2.9.0"),sQuery(id+"F7.wireOp",EDGE,"E12.2.9.1"),sQuery(id+"F7.wireOp",EDGE,"E12.2.9.2"),sQuery(id+"F7.wireOp",EDGE,"E12.2.9.3"),sQuery(id+"F7.wireOp",EDGE,"E12.2.10.0"),sQuery(id+"F7.wireOp",EDGE,"E12.2.10.1"),sQuery(id+"F7.wireOp",EDGE,"E12.2.10.2"),sQuery(id+"F7.wireOp",EDGE,"E12.2.10.3"),sQuery(id+"F7.wireOp",EDGE,"E12.2.11.0"),sQuery(id+"F7.wireOp",EDGE,"E12.2.11.1"),sQuery(id+"F7.wireOp",EDGE,"E12.2.11.2"),sQuery(id+"F7.wireOp",EDGE,"E12.2.11.3"),sQuery(id+"F7.wireOp",EDGE,"E12.2.12.0"),sQuery(id+"F7.wireOp",EDGE,"E12.2.12.1"),sQuery(id+"F7.wireOp",EDGE,"E12.2.12.2"),sQuery(id+"F7.wireOp",EDGE,"E12.2.12.3"),sQuery(id+"F7.wireOp",EDGE,"E12.2.13.0"),sQuery(id+"F7.wireOp",EDGE,"E12.2.13.1"),sQuery(id+"F7.wireOp",EDGE,"E12.2.13.2"),sQuery(id+"F7.wireOp",EDGE,"E12.2.13.3"),sQuery(id+"F7.wireOp",EDGE,"E12.2.14.0"),sQuery(id+"F7.wireOp",EDGE,"E12.2.14.1"),sQuery(id+"F7.wireOp",EDGE,"E12.2.14.2"),sQuery(id+"F7.wireOp",EDGE,"E12.2.14.3"),sQuery(id+"F7.wireOp",EDGE,"E12.2.15.0"),sQuery(id+"F7.wireOp",EDGE,"E12.2.15.1"),sQuery(id+"F7.wireOp",EDGE,"E12.2.15.2"),sQuery(id+"F7.wireOp",EDGE,"E12.2.15.3"),sQuery(id+"F7.wireOp",EDGE,"E12.3.0.0"),sQuery(id+"F7.wireOp",EDGE,"E12.3.0.1"),sQuery(id+"F7.wireOp",EDGE,"E12.3.0.2"),sQuery(id+"F7.wireOp",EDGE,"E12.3.0.3"),sQuery(id+"F7.wireOp",EDGE,"E12.3.1.0"),sQuery(id+"F7.wireOp",EDGE,"E12.3.1.1"),sQuery(id+"F7.wireOp",EDGE,"E12.3.1.2"),sQuery(id+"F7.wireOp",EDGE,"E12.3.1.3"),sQuery(id+"F7.wireOp",EDGE,"E12.3.2.0"),sQuery(id+"F7.wireOp",EDGE,"E12.3.2.1"),sQuery(id+"F7.wireOp",EDGE,"E12.3.2.2"),sQuery(id+"F7.wireOp",EDGE,"E12.3.2.3"),sQuery(id+"F7.wireOp",EDGE,"E12.3.3.0"),sQuery(id+"F7.wireOp",EDGE,"E12.3.3.1"),sQuery(id+"F7.wireOp",EDGE,"E12.3.3.2"),sQuery(id+"F7.wireOp",EDGE,"E12.3.3.3"),sQuery(id+"F7.wireOp",EDGE,"E12.3.4.0"),sQuery(id+"F7.wireOp",EDGE,"E12.3.4.1"),sQuery(id+"F7.wireOp",EDGE,"E12.3.4.2"),sQuery(id+"F7.wireOp",EDGE,"E12.3.4.3"),sQuery(id+"F7.wireOp",EDGE,"E12.3.5.0"),sQuery(id+"F7.wireOp",EDGE,"E12.3.5.1"),sQuery(id+"F7.wireOp",EDGE,"E12.3.5.2"),sQuery(id+"F7.wireOp",EDGE,"E12.3.5.3"),sQuery(id+"F7.wireOp",EDGE,"E12.3.6.0"),sQuery(id+"F7.wireOp",EDGE,"E12.3.6.1"),sQuery(id+"F7.wireOp",EDGE,"E12.3.6.2"),sQuery(id+"F7.wireOp",EDGE,"E12.3.6.3"),sQuery(id+"F7.wireOp",EDGE,"E12.3.7.0"),sQuery(id+"F7.wireOp",EDGE,"E12.3.7.1"),sQuery(id+"F7.wireOp",EDGE,"E12.3.7.2"),sQuery(id+"F7.wireOp",EDGE,"E12.3.7.3"),sQuery(id+"F7.wireOp",EDGE,"E12.3.8.0"),sQuery(id+"F7.wireOp",EDGE,"E12.3.8.1"),sQuery(id+"F7.wireOp",EDGE,"E12.3.8.2"),sQuery(id+"F7.wireOp",EDGE,"E12.3.8.3"),sQuery(id+"F7.wireOp",EDGE,"E12.3.9.0"),sQuery(id+"F7.wireOp",EDGE,"E12.3.9.1"),sQuery(id+"F7.wireOp",EDGE,"E12.3.9.2"),sQuery(id+"F7.wireOp",EDGE,"E12.3.9.3"),sQuery(id+"F7.wireOp",EDGE,"E12.3.10.0"),sQuery(id+"F7.wireOp",EDGE,"E12.3.10.1"),sQuery(id+"F7.wireOp",EDGE,"E12.3.10.2"),sQuery(id+"F7.wireOp",EDGE,"E12.3.10.3"),sQuery(id+"F7.wireOp",EDGE,"E12.3.11.0"),sQuery(id+"F7.wireOp",EDGE,"E12.3.11.1"),sQuery(id+"F7.wireOp",EDGE,"E12.3.11.2"),sQuery(id+"F7.wireOp",EDGE,"E12.3.11.3"),sQuery(id+"F7.wireOp",EDGE,"E12.3.12.0"),sQuery(id+"F7.wireOp",EDGE,"E12.3.12.1"),sQuery(id+"F7.wireOp",EDGE,"E12.3.12.2"),sQuery(id+"F7.wireOp",EDGE,"E12.3.12.3"),sQuery(id+"F7.wireOp",EDGE,"E12.3.13.0"),sQuery(id+"F7.wireOp",EDGE,"E12.3.13.1"),sQuery(id+"F7.wireOp",EDGE,"E12.3.13.2"),sQuery(id+"F7.wireOp",EDGE,"E12.3.13.3"),sQuery(id+"F7.wireOp",EDGE,"E12.3.14.0"),sQuery(id+"F7.wireOp",EDGE,"E12.3.14.1"),sQuery(id+"F7.wireOp",EDGE,"E12.3.14.2"),sQuery(id+"F7.wireOp",EDGE,"E12.3.14.3"),sQuery(id+"F7.wireOp",EDGE,"E12.3.15.0"),sQuery(id+"F7.wireOp",EDGE,"E12.3.15.1"),sQuery(id+"F7.wireOp",EDGE,"E12.3.15.2"),sQuery(id+"F7.wireOp",EDGE,"E12.3.15.3"),sQuery(id+"F7.wireOp",EDGE,"E12.4.0.0"),sQuery(id+"F7.wireOp",EDGE,"E12.4.0.1"),sQuery(id+"F7.wireOp",EDGE,"E12.4.0.2"),sQuery(id+"F7.wireOp",EDGE,"E12.4.0.3"),sQuery(id+"F7.wireOp",EDGE,"E12.4.1.0"),sQuery(id+"F7.wireOp",EDGE,"E12.4.1.1"),sQuery(id+"F7.wireOp",EDGE,"E12.4.1.2"),sQuery(id+"F7.wireOp",EDGE,"E12.4.1.3"),sQuery(id+"F7.wireOp",EDGE,"E12.4.2.0"),sQuery(id+"F7.wireOp",EDGE,"E12.4.2.1"),sQuery(id+"F7.wireOp",EDGE,"E12.4.2.2"),sQuery(id+"F7.wireOp",EDGE,"E12.4.2.3"),sQuery(id+"F7.wireOp",EDGE,"E12.4.3.0"),sQuery(id+"F7.wireOp",EDGE,"E12.4.3.1"),sQuery(id+"F7.wireOp",EDGE,"E12.4.3.2"),sQuery(id+"F7.wireOp",EDGE,"E12.4.3.3"),sQuery(id+"F7.wireOp",EDGE,"E12.4.4.0"),sQuery(id+"F7.wireOp",EDGE,"E12.4.4.1"),sQuery(id+"F7.wireOp",EDGE,"E12.4.4.2"),sQuery(id+"F7.wireOp",EDGE,"E12.4.4.3"),sQuery(id+"F7.wireOp",EDGE,"E12.4.5.0"),sQuery(id+"F7.wireOp",EDGE,"E12.4.5.1"),sQuery(id+"F7.wireOp",EDGE,"E12.4.5.2"),sQuery(id+"F7.wireOp",EDGE,"E12.4.5.3"),sQuery(id+"F7.wireOp",EDGE,"E12.4.6.0"),sQuery(id+"F7.wireOp",EDGE,"E12.4.6.1"),sQuery(id+"F7.wireOp",EDGE,"E12.4.6.2"),sQuery(id+"F7.wireOp",EDGE,"E12.4.6.3"),sQuery(id+"F7.wireOp",EDGE,"E12.4.7.0"),sQuery(id+"F7.wireOp",EDGE,"E12.4.7.1"),sQuery(id+"F7.wireOp",EDGE,"E12.4.7.2"),sQuery(id+"F7.wireOp",EDGE,"E12.4.7.3"),sQuery(id+"F7.wireOp",EDGE,"E12.4.8.0"),sQuery(id+"F7.wireOp",EDGE,"E12.4.8.1"),sQuery(id+"F7.wireOp",EDGE,"E12.4.8.2"),sQuery(id+"F7.wireOp",EDGE,"E12.4.8.3"),sQuery(id+"F7.wireOp",EDGE,"E12.4.9.0"),sQuery(id+"F7.wireOp",EDGE,"E12.4.9.1"),sQuery(id+"F7.wireOp",EDGE,"E12.4.9.2"),sQuery(id+"F7.wireOp",EDGE,"E12.4.9.3"),sQuery(id+"F7.wireOp",EDGE,"E12.4.10.0"),sQuery(id+"F7.wireOp",EDGE,"E12.4.10.1"),sQuery(id+"F7.wireOp",EDGE,"E12.4.10.2"),sQuery(id+"F7.wireOp",EDGE,"E12.4.10.3"),sQuery(id+"F7.wireOp",EDGE,"E12.4.11.0"),sQuery(id+"F7.wireOp",EDGE,"E12.4.11.1"),sQuery(id+"F7.wireOp",EDGE,"E12.4.11.2"),sQuery(id+"F7.wireOp",EDGE,"E12.4.11.3"),sQuery(id+"F7.wireOp",EDGE,"E12.4.12.0"),sQuery(id+"F7.wireOp",EDGE,"E12.4.12.1"),sQuery(id+"F7.wireOp",EDGE,"E12.4.12.2"),sQuery(id+"F7.wireOp",EDGE,"E12.4.12.3"),sQuery(id+"F7.wireOp",EDGE,"E12.4.13.0"),sQuery(id+"F7.wireOp",EDGE,"E12.4.13.1"),sQuery(id+"F7.wireOp",EDGE,"E12.4.13.2"),sQuery(id+"F7.wireOp",EDGE,"E12.4.13.3"),sQuery(id+"F7.wireOp",EDGE,"E12.4.14.0"),sQuery(id+"F7.wireOp",EDGE,"E12.4.14.1"),sQuery(id+"F7.wireOp",EDGE,"E12.4.14.2"),sQuery(id+"F7.wireOp",EDGE,"E12.4.14.3"),sQuery(id+"F7.wireOp",EDGE,"E12.4.15.0"),sQuery(id+"F7.wireOp",EDGE,"E12.4.15.1"),sQuery(id+"F7.wireOp",EDGE,"E12.4.15.2"),sQuery(id+"F7.wireOp",EDGE,"E12.4.15.3"),sQuery(id+"F7.wireOp",EDGE,"E12.5.0.0"),sQuery(id+"F7.wireOp",EDGE,"E12.5.0.1"),sQuery(id+"F7.wireOp",EDGE,"E12.5.0.2"),sQuery(id+"F7.wireOp",EDGE,"E12.5.0.3"),sQuery(id+"F7.wireOp",EDGE,"E12.5.1.0"),sQuery(id+"F7.wireOp",EDGE,"E12.5.1.1"),sQuery(id+"F7.wireOp",EDGE,"E12.5.1.2"),sQuery(id+"F7.wireOp",EDGE,"E12.5.1.3"),sQuery(id+"F7.wireOp",EDGE,"E12.5.2.0"),sQuery(id+"F7.wireOp",EDGE,"E12.5.2.1"),sQuery(id+"F7.wireOp",EDGE,"E12.5.2.2"),sQuery(id+"F7.wireOp",EDGE,"E12.5.2.3"),sQuery(id+"F7.wireOp",EDGE,"E12.5.3.0"),sQuery(id+"F7.wireOp",EDGE,"E12.5.3.1"),sQuery(id+"F7.wireOp",EDGE,"E12.5.3.2"),sQuery(id+"F7.wireOp",EDGE,"E12.5.3.3"),sQuery(id+"F7.wireOp",EDGE,"E12.5.4.0"),sQuery(id+"F7.wireOp",EDGE,"E12.5.4.1"),sQuery(id+"F7.wireOp",EDGE,"E12.5.4.2"),sQuery(id+"F7.wireOp",EDGE,"E12.5.4.3"),sQuery(id+"F7.wireOp",EDGE,"E12.5.5.0"),sQuery(id+"F7.wireOp",EDGE,"E12.5.5.1"),sQuery(id+"F7.wireOp",EDGE,"E12.5.5.2"),sQuery(id+"F7.wireOp",EDGE,"E12.5.5.3"),sQuery(id+"F7.wireOp",EDGE,"E12.5.6.0"),sQuery(id+"F7.wireOp",EDGE,"E12.5.6.1"),sQuery(id+"F7.wireOp",EDGE,"E12.5.6.2"),sQuery(id+"F7.wireOp",EDGE,"E12.5.6.3"),sQuery(id+"F7.wireOp",EDGE,"E12.5.7.0"),sQuery(id+"F7.wireOp",EDGE,"E12.5.7.1"),sQuery(id+"F7.wireOp",EDGE,"E12.5.7.2"),sQuery(id+"F7.wireOp",EDGE,"E12.5.7.3"),sQuery(id+"F7.wireOp",EDGE,"E12.5.8.0"),sQuery(id+"F7.wireOp",EDGE,"E12.5.8.1"),sQuery(id+"F7.wireOp",EDGE,"E12.5.8.2"),sQuery(id+"F7.wireOp",EDGE,"E12.5.8.3"),sQuery(id+"F7.wireOp",EDGE,"E12.5.9.0"),sQuery(id+"F7.wireOp",EDGE,"E12.5.9.1"),sQuery(id+"F7.wireOp",EDGE,"E12.5.9.2"),sQuery(id+"F7.wireOp",EDGE,"E12.5.9.3"),sQuery(id+"F7.wireOp",EDGE,"E12.5.10.0"),sQuery(id+"F7.wireOp",EDGE,"E12.5.10.1"),sQuery(id+"F7.wireOp",EDGE,"E12.5.10.2"),sQuery(id+"F7.wireOp",EDGE,"E12.5.10.3"),sQuery(id+"F7.wireOp",EDGE,"E12.5.11.0"),sQuery(id+"F7.wireOp",EDGE,"E12.5.11.1"),sQuery(id+"F7.wireOp",EDGE,"E12.5.11.2"),sQuery(id+"F7.wireOp",EDGE,"E12.5.11.3"),sQuery(id+"F7.wireOp",EDGE,"E12.5.12.0"),sQuery(id+"F7.wireOp",EDGE,"E12.5.12.1"),sQuery(id+"F7.wireOp",EDGE,"E12.5.12.2"),sQuery(id+"F7.wireOp",EDGE,"E12.5.12.3"),sQuery(id+"F7.wireOp",EDGE,"E12.5.13.0"),sQuery(id+"F7.wireOp",EDGE,"E12.5.13.1"),sQuery(id+"F7.wireOp",EDGE,"E12.5.13.2"),sQuery(id+"F7.wireOp",EDGE,"E12.5.13.3"),sQuery(id+"F7.wireOp",EDGE,"E12.5.14.0"),sQuery(id+"F7.wireOp",EDGE,"E12.5.14.1"),sQuery(id+"F7.wireOp",EDGE,"E12.5.14.2"),sQuery(id+"F7.wireOp",EDGE,"E12.5.14.3"),sQuery(id+"F7.wireOp",EDGE,"E12.5.15.0"),sQuery(id+"F7.wireOp",EDGE,"E12.5.15.1"),sQuery(id+"F7.wireOp",EDGE,"E12.5.15.2"),sQuery(id+"F7.wireOp",EDGE,"E12.5.15.3"),sQuery(id+"F7.wireOp",EDGE,"E12.6.0.0"),sQuery(id+"F7.wireOp",EDGE,"E12.6.0.1"),sQuery(id+"F7.wireOp",EDGE,"E12.6.0.2"),sQuery(id+"F7.wireOp",EDGE,"E12.6.0.3"),sQuery(id+"F7.wireOp",EDGE,"E12.6.1.0"),sQuery(id+"F7.wireOp",EDGE,"E12.6.1.1"),sQuery(id+"F7.wireOp",EDGE,"E12.6.1.2"),sQuery(id+"F7.wireOp",EDGE,"E12.6.1.3"),sQuery(id+"F7.wireOp",EDGE,"E12.6.2.0"),sQuery(id+"F7.wireOp",EDGE,"E12.6.2.1"),sQuery(id+"F7.wireOp",EDGE,"E12.6.2.2"),sQuery(id+"F7.wireOp",EDGE,"E12.6.2.3"),sQuery(id+"F7.wireOp",EDGE,"E12.6.3.0"),sQuery(id+"F7.wireOp",EDGE,"E12.6.3.1"),sQuery(id+"F7.wireOp",EDGE,"E12.6.3.2"),sQuery(id+"F7.wireOp",EDGE,"E12.6.3.3"),sQuery(id+"F7.wireOp",EDGE,"E12.6.4.0"),sQuery(id+"F7.wireOp",EDGE,"E12.6.4.1"),sQuery(id+"F7.wireOp",EDGE,"E12.6.4.2"),sQuery(id+"F7.wireOp",EDGE,"E12.6.4.3"),sQuery(id+"F7.wireOp",EDGE,"E12.6.5.0"),sQuery(id+"F7.wireOp",EDGE,"E12.6.5.1"),sQuery(id+"F7.wireOp",EDGE,"E12.6.5.2"),sQuery(id+"F7.wireOp",EDGE,"E12.6.5.3"),sQuery(id+"F7.wireOp",EDGE,"E12.6.6.0"),sQuery(id+"F7.wireOp",EDGE,"E12.6.6.1"),sQuery(id+"F7.wireOp",EDGE,"E12.6.6.2"),sQuery(id+"F7.wireOp",EDGE,"E12.6.6.3"),sQuery(id+"F7.wireOp",EDGE,"E12.6.7.0"),sQuery(id+"F7.wireOp",EDGE,"E12.6.7.1"),sQuery(id+"F7.wireOp",EDGE,"E12.6.7.2"),sQuery(id+"F7.wireOp",EDGE,"E12.6.7.3"),sQuery(id+"F7.wireOp",EDGE,"E12.6.8.0"),sQuery(id+"F7.wireOp",EDGE,"E12.6.8.1"),sQuery(id+"F7.wireOp",EDGE,"E12.6.8.2"),sQuery(id+"F7.wireOp",EDGE,"E12.6.8.3"),sQuery(id+"F7.wireOp",EDGE,"E12.6.9.0"),sQuery(id+"F7.wireOp",EDGE,"E12.6.9.1"),sQuery(id+"F7.wireOp",EDGE,"E12.6.9.2"),sQuery(id+"F7.wireOp",EDGE,"E12.6.9.3"),sQuery(id+"F7.wireOp",EDGE,"E12.6.10.0"),sQuery(id+"F7.wireOp",EDGE,"E12.6.10.1"),sQuery(id+"F7.wireOp",EDGE,"E12.6.10.2"),sQuery(id+"F7.wireOp",EDGE,"E12.6.10.3"),sQuery(id+"F7.wireOp",EDGE,"E12.6.11.0"),sQuery(id+"F7.wireOp",EDGE,"E12.6.11.1"),sQuery(id+"F7.wireOp",EDGE,"E12.6.11.2"),sQuery(id+"F7.wireOp",EDGE,"E12.6.11.3"),sQuery(id+"F7.wireOp",EDGE,"E12.6.12.0"),sQuery(id+"F7.wireOp",EDGE,"E12.6.12.1"),sQuery(id+"F7.wireOp",EDGE,"E12.6.12.2"),sQuery(id+"F7.wireOp",EDGE,"E12.6.12.3"),sQuery(id+"F7.wireOp",EDGE,"E12.6.13.0"),sQuery(id+"F7.wireOp",EDGE,"E12.6.13.1"),sQuery(id+"F7.wireOp",EDGE,"E12.6.13.2"),sQuery(id+"F7.wireOp",EDGE,"E12.6.13.3"),sQuery(id+"F7.wireOp",EDGE,"E12.6.14.0"),sQuery(id+"F7.wireOp",EDGE,"E12.6.14.1"),sQuery(id+"F7.wireOp",EDGE,"E12.6.14.2"),sQuery(id+"F7.wireOp",EDGE,"E12.6.14.3"),sQuery(id+"F7.wireOp",EDGE,"E12.6.15.0"),sQuery(id+"F7.wireOp",EDGE,"E12.6.15.1"),sQuery(id+"F7.wireOp",EDGE,"E12.6.15.2"),sQuery(id+"F7.wireOp",EDGE,"E12.6.15.3"),sQuery(id+"F7.wireOp",EDGE,"E12.7.0.0"),sQuery(id+"F7.wireOp",EDGE,"E12.7.0.1"),sQuery(id+"F7.wireOp",EDGE,"E12.7.0.2"),sQuery(id+"F7.wireOp",EDGE,"E12.7.0.3"),sQuery(id+"F7.wireOp",EDGE,"E12.7.1.0"),sQuery(id+"F7.wireOp",EDGE,"E12.7.1.1"),sQuery(id+"F7.wireOp",EDGE,"E12.7.1.2"),sQuery(id+"F7.wireOp",EDGE,"E12.7.1.3"),sQuery(id+"F7.wireOp",EDGE,"E12.7.2.0"),sQuery(id+"F7.wireOp",EDGE,"E12.7.2.1"),sQuery(id+"F7.wireOp",EDGE,"E12.7.2.2"),sQuery(id+"F7.wireOp",EDGE,"E12.7.2.3"),sQuery(id+"F7.wireOp",EDGE,"E12.7.3.0"),sQuery(id+"F7.wireOp",EDGE,"E12.7.3.1"),sQuery(id+"F7.wireOp",EDGE,"E12.7.3.2"),sQuery(id+"F7.wireOp",EDGE,"E12.7.3.3"),sQuery(id+"F7.wireOp",EDGE,"E12.7.4.0"),sQuery(id+"F7.wireOp",EDGE,"E12.7.4.1"),sQuery(id+"F7.wireOp",EDGE,"E12.7.4.2"),sQuery(id+"F7.wireOp",EDGE,"E12.7.4.3"),sQuery(id+"F7.wireOp",EDGE,"E12.7.5.0"),sQuery(id+"F7.wireOp",EDGE,"E12.7.5.1"),sQuery(id+"F7.wireOp",EDGE,"E12.7.5.2"),sQuery(id+"F7.wireOp",EDGE,"E12.7.5.3"),sQuery(id+"F7.wireOp",EDGE,"E12.7.6.0"),sQuery(id+"F7.wireOp",EDGE,"E12.7.6.1"),sQuery(id+"F7.wireOp",EDGE,"E12.7.6.2"),sQuery(id+"F7.wireOp",EDGE,"E12.7.6.3"),sQuery(id+"F7.wireOp",EDGE,"E12.7.7.0"),sQuery(id+"F7.wireOp",EDGE,"E12.7.7.1"),sQuery(id+"F7.wireOp",EDGE,"E12.7.7.2"),sQuery(id+"F7.wireOp",EDGE,"E12.7.7.3"),sQuery(id+"F7.wireOp",EDGE,"E12.7.8.0"),sQuery(id+"F7.wireOp",EDGE,"E12.7.8.1"),sQuery(id+"F7.wireOp",EDGE,"E12.7.8.2"),sQuery(id+"F7.wireOp",EDGE,"E12.7.8.3"),sQuery(id+"F7.wireOp",EDGE,"E12.7.9.0"),sQuery(id+"F7.wireOp",EDGE,"E12.7.9.1"),sQuery(id+"F7.wireOp",EDGE,"E12.7.9.2"),sQuery(id+"F7.wireOp",EDGE,"E12.7.9.3"),sQuery(id+"F7.wireOp",EDGE,"E12.7.10.0"),sQuery(id+"F7.wireOp",EDGE,"E12.7.10.1"),sQuery(id+"F7.wireOp",EDGE,"E12.7.10.2"),sQuery(id+"F7.wireOp",EDGE,"E12.7.10.3"),sQuery(id+"F7.wireOp",EDGE,"E12.7.11.0"),sQuery(id+"F7.wireOp",EDGE,"E12.7.11.1"),sQuery(id+"F7.wireOp",EDGE,"E12.7.11.2"),sQuery(id+"F7.wireOp",EDGE,"E12.7.11.3"),sQuery(id+"F7.wireOp",EDGE,"E12.7.12.0"),sQuery(id+"F7.wireOp",EDGE,"E12.7.12.1"),sQuery(id+"F7.wireOp",EDGE,"E12.7.12.2"),sQuery(id+"F7.wireOp",EDGE,"E12.7.12.3"),sQuery(id+"F7.wireOp",EDGE,"E12.7.13.0"),sQuery(id+"F7.wireOp",EDGE,"E12.7.13.1"),sQuery(id+"F7.wireOp",EDGE,"E12.7.13.2"),sQuery(id+"F7.wireOp",EDGE,"E12.7.13.3"),sQuery(id+"F7.wireOp",EDGE,"E12.7.14.0"),sQuery(id+"F7.wireOp",EDGE,"E12.7.14.1"),sQuery(id+"F7.wireOp",EDGE,"E12.7.14.2"),sQuery(id+"F7.wireOp",EDGE,"E12.7.14.3"),sQuery(id+"F7.wireOp",EDGE,"E12.7.15.0"),sQuery(id+"F7.wireOp",EDGE,"E12.7.15.1"),sQuery(id+"F7.wireOp",EDGE,"E12.7.15.2"),sQuery(id+"F7.wireOp",EDGE,"E12.7.15.3"),sQuery(id+"F7.wireOp",EDGE,"E12.8.0.0"),sQuery(id+"F7.wireOp",EDGE,"E12.8.0.1"),sQuery(id+"F7.wireOp",EDGE,"E12.8.0.2"),sQuery(id+"F7.wireOp",EDGE,"E12.8.0.3"),sQuery(id+"F7.wireOp",EDGE,"E12.8.1.0"),sQuery(id+"F7.wireOp",EDGE,"E12.8.1.1"),sQuery(id+"F7.wireOp",EDGE,"E12.8.1.2"),sQuery(id+"F7.wireOp",EDGE,"E12.8.1.3"),sQuery(id+"F7.wireOp",EDGE,"E12.8.2.0"),sQuery(id+"F7.wireOp",EDGE,"E12.8.2.1"),sQuery(id+"F7.wireOp",EDGE,"E12.8.2.2"),sQuery(id+"F7.wireOp",EDGE,"E12.8.2.3"),sQuery(id+"F7.wireOp",EDGE,"E12.8.3.0"),sQuery(id+"F7.wireOp",EDGE,"E12.8.3.1"),sQuery(id+"F7.wireOp",EDGE,"E12.8.3.2"),sQuery(id+"F7.wireOp",EDGE,"E12.8.3.3"),sQuery(id+"F7.wireOp",EDGE,"E12.8.4.0"),sQuery(id+"F7.wireOp",EDGE,"E12.8.4.1"),sQuery(id+"F7.wireOp",EDGE,"E12.8.4.2"),sQuery(id+"F7.wireOp",EDGE,"E12.8.4.3"),sQuery(id+"F7.wireOp",EDGE,"E12.8.5.0"),sQuery(id+"F7.wireOp",EDGE,"E12.8.5.1"),sQuery(id+"F7.wireOp",EDGE,"E12.8.5.2"),sQuery(id+"F7.wireOp",EDGE,"E12.8.5.3"),sQuery(id+"F7.wireOp",EDGE,"E12.8.6.0"),sQuery(id+"F7.wireOp",EDGE,"E12.8.6.1"),sQuery(id+"F7.wireOp",EDGE,"E12.8.6.2"),sQuery(id+"F7.wireOp",EDGE,"E12.8.6.3"),sQuery(id+"F7.wireOp",EDGE,"E12.8.7.0"),sQuery(id+"F7.wireOp",EDGE,"E12.8.7.1"),sQuery(id+"F7.wireOp",EDGE,"E12.8.7.2"),sQuery(id+"F7.wireOp",EDGE,"E12.8.7.3"),sQuery(id+"F7.wireOp",EDGE,"E12.8.8.0"),sQuery(id+"F7.wireOp",EDGE,"E12.8.8.1"),sQuery(id+"F7.wireOp",EDGE,"E12.8.8.2"),sQuery(id+"F7.wireOp",EDGE,"E12.8.8.3"),sQuery(id+"F7.wireOp",EDGE,"E12.8.9.0"),sQuery(id+"F7.wireOp",EDGE,"E12.8.9.1"),sQuery(id+"F7.wireOp",EDGE,"E12.8.9.2"),sQuery(id+"F7.wireOp",EDGE,"E12.8.9.3"),sQuery(id+"F7.wireOp",EDGE,"E12.8.10.0"),sQuery(id+"F7.wireOp",EDGE,"E12.8.10.1"),sQuery(id+"F7.wireOp",EDGE,"E12.8.10.2"),sQuery(id+"F7.wireOp",EDGE,"E12.8.10.3"),sQuery(id+"F7.wireOp",EDGE,"E12.8.11.0"),sQuery(id+"F7.wireOp",EDGE,"E12.8.11.1"),sQuery(id+"F7.wireOp",EDGE,"E12.8.11.2"),sQuery(id+"F7.wireOp",EDGE,"E12.8.11.3"),sQuery(id+"F7.wireOp",EDGE,"E12.8.12.0"),sQuery(id+"F7.wireOp",EDGE,"E12.8.12.1"),sQuery(id+"F7.wireOp",EDGE,"E12.8.12.2"),sQuery(id+"F7.wireOp",EDGE,"E12.8.12.3"),sQuery(id+"F7.wireOp",EDGE,"E12.8.13.0"),sQuery(id+"F7.wireOp",EDGE,"E12.8.13.1"),sQuery(id+"F7.wireOp",EDGE,"E12.8.13.2"),sQuery(id+"F7.wireOp",EDGE,"E12.8.13.3"),sQuery(id+"F7.wireOp",EDGE,"E12.8.14.0"),sQuery(id+"F7.wireOp",EDGE,"E12.8.14.1"),sQuery(id+"F7.wireOp",EDGE,"E12.8.14.2"),sQuery(id+"F7.wireOp",EDGE,"E12.8.14.3"),sQuery(id+"F7.wireOp",EDGE,"E12.8.15.0"),sQuery(id+"F7.wireOp",EDGE,"E12.8.15.1"),sQuery(id+"F7.wireOp",EDGE,"E12.8.15.2"),sQuery(id+"F7.wireOp",EDGE,"E12.8.15.3"),sQuery(id+"F7.wireOp",EDGE,"E12.9.0.0"),sQuery(id+"F7.wireOp",EDGE,"E12.9.0.1"),sQuery(id+"F7.wireOp",EDGE,"E12.9.0.2"),sQuery(id+"F7.wireOp",EDGE,"E12.9.0.3"),sQuery(id+"F7.wireOp",EDGE,"E12.9.1.0"),sQuery(id+"F7.wireOp",EDGE,"E12.9.1.1"),sQuery(id+"F7.wireOp",EDGE,"E12.9.1.2"),sQuery(id+"F7.wireOp",EDGE,"E12.9.1.3"),sQuery(id+"F7.wireOp",EDGE,"E12.9.2.0"),sQuery(id+"F7.wireOp",EDGE,"E12.9.2.1"),sQuery(id+"F7.wireOp",EDGE,"E12.9.2.2"),sQuery(id+"F7.wireOp",EDGE,"E12.9.2.3"),sQuery(id+"F7.wireOp",EDGE,"E12.9.3.0"),sQuery(id+"F7.wireOp",EDGE,"E12.9.3.1"),sQuery(id+"F7.wireOp",EDGE,"E12.9.3.2"),sQuery(id+"F7.wireOp",EDGE,"E12.9.3.3"),sQuery(id+"F7.wireOp",EDGE,"E12.9.4.0"),sQuery(id+"F7.wireOp",EDGE,"E12.9.4.1"),sQuery(id+"F7.wireOp",EDGE,"E12.9.4.2"),sQuery(id+"F7.wireOp",EDGE,"E12.9.4.3"),sQuery(id+"F7.wireOp",EDGE,"E12.9.5.0"),sQuery(id+"F7.wireOp",EDGE,"E12.9.5.1"),sQuery(id+"F7.wireOp",EDGE,"E12.9.5.2"),sQuery(id+"F7.wireOp",EDGE,"E12.9.5.3"),sQuery(id+"F7.wireOp",EDGE,"E12.9.6.0"),sQuery(id+"F7.wireOp",EDGE,"E12.9.6.1"),sQuery(id+"F7.wireOp",EDGE,"E12.9.6.2"),sQuery(id+"F7.wireOp",EDGE,"E12.9.6.3"),sQuery(id+"F7.wireOp",EDGE,"E12.9.7.0"),sQuery(id+"F7.wireOp",EDGE,"E12.9.7.1"),sQuery(id+"F7.wireOp",EDGE,"E12.9.7.2"),sQuery(id+"F7.wireOp",EDGE,"E12.9.7.3"),sQuery(id+"F7.wireOp",EDGE,"E12.9.8.0"),sQuery(id+"F7.wireOp",EDGE,"E12.9.8.1"),sQuery(id+"F7.wireOp",EDGE,"E12.9.8.2"),sQuery(id+"F7.wireOp",EDGE,"E12.9.8.3"),sQuery(id+"F7.wireOp",EDGE,"E12.9.9.0"),sQuery(id+"F7.wireOp",EDGE,"E12.9.9.1"),sQuery(id+"F7.wireOp",EDGE,"E12.9.9.2"),sQuery(id+"F7.wireOp",EDGE,"E12.9.9.3"),sQuery(id+"F7.wireOp",EDGE,"E12.9.10.0"),sQuery(id+"F7.wireOp",EDGE,"E12.9.10.1"),sQuery(id+"F7.wireOp",EDGE,"E12.9.10.2"),sQuery(id+"F7.wireOp",EDGE,"E12.9.10.3"),sQuery(id+"F7.wireOp",EDGE,"E12.9.11.0"),sQuery(id+"F7.wireOp",EDGE,"E12.9.11.1"),sQuery(id+"F7.wireOp",EDGE,"E12.9.11.2"),sQuery(id+"F7.wireOp",EDGE,"E12.9.11.3"),sQuery(id+"F7.wireOp",EDGE,"E12.9.12.0"),sQuery(id+"F7.wireOp",EDGE,"E12.9.12.1"),sQuery(id+"F7.wireOp",EDGE,"E12.9.12.2"),sQuery(id+"F7.wireOp",EDGE,"E12.9.12.3"),sQuery(id+"F7.wireOp",EDGE,"E12.9.13.0"),sQuery(id+"F7.wireOp",EDGE,"E12.9.13.1"),sQuery(id+"F7.wireOp",EDGE,"E12.9.13.2"),sQuery(id+"F7.wireOp",EDGE,"E12.9.13.3"),sQuery(id+"F7.wireOp",EDGE,"E12.9.14.0"),sQuery(id+"F7.wireOp",EDGE,"E12.9.14.1"),sQuery(id+"F7.wireOp",EDGE,"E12.9.14.2"),sQuery(id+"F7.wireOp",EDGE,"E12.9.14.3"),sQuery(id+"F7.wireOp",EDGE,"E12.9.15.0"),sQuery(id+"F7.wireOp",EDGE,"E12.9.15.1"),sQuery(id+"F7.wireOp",EDGE,"E12.9.15.2"),sQuery(id+"F7.wireOp",EDGE,"E12.9.15.3"),sQuery(id+"F7.wireOp",EDGE,"E12.10.0.0"),sQuery(id+"F7.wireOp",EDGE,"E12.10.0.1"),sQuery(id+"F7.wireOp",EDGE,"E12.10.0.2"),sQuery(id+"F7.wireOp",EDGE,"E12.10.0.3"),sQuery(id+"F7.wireOp",EDGE,"E12.10.1.0"),sQuery(id+"F7.wireOp",EDGE,"E12.10.1.1"),sQuery(id+"F7.wireOp",EDGE,"E12.10.1.2"),sQuery(id+"F7.wireOp",EDGE,"E12.10.1.3"),sQuery(id+"F7.wireOp",EDGE,"E12.10.2.0"),sQuery(id+"F7.wireOp",EDGE,"E12.10.2.1"),sQuery(id+"F7.wireOp",EDGE,"E12.10.2.2"),sQuery(id+"F7.wireOp",EDGE,"E12.10.2.3"),sQuery(id+"F7.wireOp",EDGE,"E12.10.3.0"),sQuery(id+"F7.wireOp",EDGE,"E12.10.3.1"),sQuery(id+"F7.wireOp",EDGE,"E12.10.3.2"),sQuery(id+"F7.wireOp",EDGE,"E12.10.3.3"),sQuery(id+"F7.wireOp",EDGE,"E12.10.4.0"),sQuery(id+"F7.wireOp",EDGE,"E12.10.4.1"),sQuery(id+"F7.wireOp",EDGE,"E12.10.4.2"),sQuery(id+"F7.wireOp",EDGE,"E12.10.4.3"),sQuery(id+"F7.wireOp",EDGE,"E12.10.5.0"),sQuery(id+"F7.wireOp",EDGE,"E12.10.5.1"),sQuery(id+"F7.wireOp",EDGE,"E12.10.5.2"),sQuery(id+"F7.wireOp",EDGE,"E12.10.5.3"),sQuery(id+"F7.wireOp",EDGE,"E12.10.6.0"),sQuery(id+"F7.wireOp",EDGE,"E12.10.6.1"),sQuery(id+"F7.wireOp",EDGE,"E12.10.6.2"),sQuery(id+"F7.wireOp",EDGE,"E12.10.6.3"),sQuery(id+"F7.wireOp",EDGE,"E12.10.7.0"),sQuery(id+"F7.wireOp",EDGE,"E12.10.7.1"),sQuery(id+"F7.wireOp",EDGE,"E12.10.7.2"),sQuery(id+"F7.wireOp",EDGE,"E12.10.7.3"),sQuery(id+"F7.wireOp",EDGE,"E12.10.8.0"),sQuery(id+"F7.wireOp",EDGE,"E12.10.8.1"),sQuery(id+"F7.wireOp",EDGE,"E12.10.8.2"),sQuery(id+"F7.wireOp",EDGE,"E12.10.8.3"),sQuery(id+"F7.wireOp",EDGE,"E12.10.9.0"),sQuery(id+"F7.wireOp",EDGE,"E12.10.9.1"),sQuery(id+"F7.wireOp",EDGE,"E12.10.9.2"),sQuery(id+"F7.wireOp",EDGE,"E12.10.9.3"),sQuery(id+"F7.wireOp",EDGE,"E12.10.10.0"),sQuery(id+"F7.wireOp",EDGE,"E12.10.10.1"),sQuery(id+"F7.wireOp",EDGE,"E12.10.10.2"),sQuery(id+"F7.wireOp",EDGE,"E12.10.10.3"),sQuery(id+"F7.wireOp",EDGE,"E12.10.11.0"),sQuery(id+"F7.wireOp",EDGE,"E12.10.11.1"),sQuery(id+"F7.wireOp",EDGE,"E12.10.11.2"),sQuery(id+"F7.wireOp",EDGE,"E12.10.11.3"),sQuery(id+"F7.wireOp",EDGE,"E12.10.12.0"),sQuery(id+"F7.wireOp",EDGE,"E12.10.12.1"),sQuery(id+"F7.wireOp",EDGE,"E12.10.12.2"),sQuery(id+"F7.wireOp",EDGE,"E12.10.12.3"),sQuery(id+"F7.wireOp",EDGE,"E12.10.13.0"),sQuery(id+"F7.wireOp",EDGE,"E12.10.13.1"),sQuery(id+"F7.wireOp",EDGE,"E12.10.13.2"),sQuery(id+"F7.wireOp",EDGE,"E12.10.13.3"),sQuery(id+"F7.wireOp",EDGE,"E12.10.14.0"),sQuery(id+"F7.wireOp",EDGE,"E12.10.14.1"),sQuery(id+"F7.wireOp",EDGE,"E12.10.14.2"),sQuery(id+"F7.wireOp",EDGE,"E12.10.14.3"),sQuery(id+"F7.wireOp",EDGE,"E12.10.15.0"),sQuery(id+"F7.wireOp",EDGE,"E12.10.15.1"),sQuery(id+"F7.wireOp",EDGE,"E12.10.15.2"),sQuery(id+"F7.wireOp",EDGE,"E12.10.15.3"),sQuery(id+"F7.wireOp",EDGE,"E12.11.0.0"),sQuery(id+"F7.wireOp",EDGE,"E12.11.0.1"),sQuery(id+"F7.wireOp",EDGE,"E12.11.0.2"),sQuery(id+"F7.wireOp",EDGE,"E12.11.0.3"),sQuery(id+"F7.wireOp",EDGE,"E12.11.1.0"),sQuery(id+"F7.wireOp",EDGE,"E12.11.1.1"),sQuery(id+"F7.wireOp",EDGE,"E12.11.1.2"),sQuery(id+"F7.wireOp",EDGE,"E12.11.1.3"),sQuery(id+"F7.wireOp",EDGE,"E12.11.2.0"),sQuery(id+"F7.wireOp",EDGE,"E12.11.2.1"),sQuery(id+"F7.wireOp",EDGE,"E12.11.2.2"),sQuery(id+"F7.wireOp",EDGE,"E12.11.2.3"),sQuery(id+"F7.wireOp",EDGE,"E12.11.3.0"),sQuery(id+"F7.wireOp",EDGE,"E12.11.3.1"),sQuery(id+"F7.wireOp",EDGE,"E12.11.3.2"),sQuery(id+"F7.wireOp",EDGE,"E12.11.3.3"),sQuery(id+"F7.wireOp",EDGE,"E12.11.4.0"),sQuery(id+"F7.wireOp",EDGE,"E12.11.4.1"),sQuery(id+"F7.wireOp",EDGE,"E12.11.4.2"),sQuery(id+"F7.wireOp",EDGE,"E12.11.4.3"),sQuery(id+"F7.wireOp",EDGE,"E12.11.5.0"),sQuery(id+"F7.wireOp",EDGE,"E12.11.5.1"),sQuery(id+"F7.wireOp",EDGE,"E12.11.5.2"),sQuery(id+"F7.wireOp",EDGE,"E12.11.5.3"),sQuery(id+"F7.wireOp",EDGE,"E12.11.6.0"),sQuery(id+"F7.wireOp",EDGE,"E12.11.6.1"),sQuery(id+"F7.wireOp",EDGE,"E12.11.6.2"),sQuery(id+"F7.wireOp",EDGE,"E12.11.6.3"),sQuery(id+"F7.wireOp",EDGE,"E12.11.7.0"),sQuery(id+"F7.wireOp",EDGE,"E12.11.7.1"),sQuery(id+"F7.wireOp",EDGE,"E12.11.7.2"),sQuery(id+"F7.wireOp",EDGE,"E12.11.7.3"),sQuery(id+"F7.wireOp",EDGE,"E12.11.8.0"),sQuery(id+"F7.wireOp",EDGE,"E12.11.8.1"),sQuery(id+"F7.wireOp",EDGE,"E12.11.8.2"),sQuery(id+"F7.wireOp",EDGE,"E12.11.8.3"),sQuery(id+"F7.wireOp",EDGE,"E12.11.9.0"),sQuery(id+"F7.wireOp",EDGE,"E12.11.9.1"),sQuery(id+"F7.wireOp",EDGE,"E12.11.9.2"),sQuery(id+"F7.wireOp",EDGE,"E12.11.9.3"),sQuery(id+"F7.wireOp",EDGE,"E12.11.10.0"),sQuery(id+"F7.wireOp",EDGE,"E12.11.10.1"),sQuery(id+"F7.wireOp",EDGE,"E12.11.10.2"),sQuery(id+"F7.wireOp",EDGE,"E12.11.10.3"),sQuery(id+"F7.wireOp",EDGE,"E12.11.11.0"),sQuery(id+"F7.wireOp",EDGE,"E12.11.11.1"),sQuery(id+"F7.wireOp",EDGE,"E12.11.11.2"),sQuery(id+"F7.wireOp",EDGE,"E12.11.11.3"),sQuery(id+"F7.wireOp",EDGE,"E12.11.12.0"),sQuery(id+"F7.wireOp",EDGE,"E12.11.12.1"),sQuery(id+"F7.wireOp",EDGE,"E12.11.12.2"),sQuery(id+"F7.wireOp",EDGE,"E12.11.12.3"),sQuery(id+"F7.wireOp",EDGE,"E12.11.13.0"),sQuery(id+"F7.wireOp",EDGE,"E12.11.13.1"),sQuery(id+"F7.wireOp",EDGE,"E12.11.13.2"),sQuery(id+"F7.wireOp",EDGE,"E12.11.13.3"),sQuery(id+"F7.wireOp",EDGE,"E12.11.14.0"),sQuery(id+"F7.wireOp",EDGE,"E12.11.14.1"),sQuery(id+"F7.wireOp",EDGE,"E12.11.14.2"),sQuery(id+"F7.wireOp",EDGE,"E12.11.14.3"),sQuery(id+"F7.wireOp",EDGE,"E12.11.15.0"),sQuery(id+"F7.wireOp",EDGE,"E12.11.15.1"),sQuery(id+"F7.wireOp",EDGE,"E12.11.15.2"),sQuery(id+"F7.wireOp",EDGE,"E12.11.15.3"),sQuery(id+"F7.wireOp",EDGE,"E12.12.0.0"),sQuery(id+"F7.wireOp",EDGE,"E12.12.0.1"),sQuery(id+"F7.wireOp",EDGE,"E12.12.0.2"),sQuery(id+"F7.wireOp",EDGE,"E12.12.0.3"),sQuery(id+"F7.wireOp",EDGE,"E12.12.1.0"),sQuery(id+"F7.wireOp",EDGE,"E12.12.1.1"),sQuery(id+"F7.wireOp",EDGE,"E12.12.1.2"),sQuery(id+"F7.wireOp",EDGE,"E12.12.1.3"),sQuery(id+"F7.wireOp",EDGE,"E12.12.2.0"),sQuery(id+"F7.wireOp",EDGE,"E12.12.2.1"),sQuery(id+"F7.wireOp",EDGE,"E12.12.2.2"),sQuery(id+"F7.wireOp",EDGE,"E12.12.2.3"),sQuery(id+"F7.wireOp",EDGE,"E12.12.3.0"),sQuery(id+"F7.wireOp",EDGE,"E12.12.3.1"),sQuery(id+"F7.wireOp",EDGE,"E12.12.3.2"),sQuery(id+"F7.wireOp",EDGE,"E12.12.3.3"),sQuery(id+"F7.wireOp",EDGE,"E12.12.4.0"),sQuery(id+"F7.wireOp",EDGE,"E12.12.4.1"),sQuery(id+"F7.wireOp",EDGE,"E12.12.4.2"),sQuery(id+"F7.wireOp",EDGE,"E12.12.4.3"),sQuery(id+"F7.wireOp",EDGE,"E12.12.5.0"),sQuery(id+"F7.wireOp",EDGE,"E12.12.5.1"),sQuery(id+"F7.wireOp",EDGE,"E12.12.5.2"),sQuery(id+"F7.wireOp",EDGE,"E12.12.5.3"),sQuery(id+"F7.wireOp",EDGE,"E12.12.6.0"),sQuery(id+"F7.wireOp",EDGE,"E12.12.6.1"),sQuery(id+"F7.wireOp",EDGE,"E12.12.6.2"),sQuery(id+"F7.wireOp",EDGE,"E12.12.6.3"),sQuery(id+"F7.wireOp",EDGE,"E12.12.7.0"),sQuery(id+"F7.wireOp",EDGE,"E12.12.7.1"),sQuery(id+"F7.wireOp",EDGE,"E12.12.7.2"),sQuery(id+"F7.wireOp",EDGE,"E12.12.7.3"),sQuery(id+"F7.wireOp",EDGE,"E12.12.8.0"),sQuery(id+"F7.wireOp",EDGE,"E12.12.8.1"),sQuery(id+"F7.wireOp",EDGE,"E12.12.8.2"),sQuery(id+"F7.wireOp",EDGE,"E12.12.8.3"),sQuery(id+"F7.wireOp",EDGE,"E12.12.9.0"),sQuery(id+"F7.wireOp",EDGE,"E12.12.9.1"),sQuery(id+"F7.wireOp",EDGE,"E12.12.9.2"),sQuery(id+"F7.wireOp",EDGE,"E12.12.9.3"),sQuery(id+"F7.wireOp",EDGE,"E12.12.10.0"),sQuery(id+"F7.wireOp",EDGE,"E12.12.10.1"),sQuery(id+"F7.wireOp",EDGE,"E12.12.10.2"),sQuery(id+"F7.wireOp",EDGE,"E12.12.10.3"),sQuery(id+"F7.wireOp",EDGE,"E12.12.11.0"),sQuery(id+"F7.wireOp",EDGE,"E12.12.11.1"),sQuery(id+"F7.wireOp",EDGE,"E12.12.11.2"),sQuery(id+"F7.wireOp",EDGE,"E12.12.11.3"),sQuery(id+"F7.wireOp",EDGE,"E12.12.12.0"),sQuery(id+"F7.wireOp",EDGE,"E12.12.12.1"),sQuery(id+"F7.wireOp",EDGE,"E12.12.12.2"),sQuery(id+"F7.wireOp",EDGE,"E12.12.12.3"),sQuery(id+"F7.wireOp",EDGE,"E12.12.13.0"),sQuery(id+"F7.wireOp",EDGE,"E12.12.13.1"),sQuery(id+"F7.wireOp",EDGE,"E12.12.13.2"),sQuery(id+"F7.wireOp",EDGE,"E12.12.13.3"),sQuery(id+"F7.wireOp",EDGE,"E12.12.14.0"),sQuery(id+"F7.wireOp",EDGE,"E12.12.14.1"),sQuery(id+"F7.wireOp",EDGE,"E12.12.14.2"),sQuery(id+"F7.wireOp",EDGE,"E12.12.14.3"),sQuery(id+"F7.wireOp",EDGE,"E12.12.15.0"),sQuery(id+"F7.wireOp",EDGE,"E12.12.15.1"),sQuery(id+"F7.wireOp",EDGE,"E12.12.15.2"),sQuery(id+"F7.wireOp",EDGE,"E12.12.15.3"),sQuery(id+"F7.wireOp",EDGE,"E12.13.0.0"),sQuery(id+"F7.wireOp",EDGE,"E12.13.0.1"),sQuery(id+"F7.wireOp",EDGE,"E12.13.0.2"),sQuery(id+"F7.wireOp",EDGE,"E12.13.0.3"),sQuery(id+"F7.wireOp",EDGE,"E12.13.1.0"),sQuery(id+"F7.wireOp",EDGE,"E12.13.1.1"),sQuery(id+"F7.wireOp",EDGE,"E12.13.1.2"),sQuery(id+"F7.wireOp",EDGE,"E12.13.1.3"),sQuery(id+"F7.wireOp",EDGE,"E12.13.2.0"),sQuery(id+"F7.wireOp",EDGE,"E12.13.2.1"),sQuery(id+"F7.wireOp",EDGE,"E12.13.2.2"),sQuery(id+"F7.wireOp",EDGE,"E12.13.2.3"),sQuery(id+"F7.wireOp",EDGE,"E12.13.3.0"),sQuery(id+"F7.wireOp",EDGE,"E12.13.3.1"),sQuery(id+"F7.wireOp",EDGE,"E12.13.3.2"),sQuery(id+"F7.wireOp",EDGE,"E12.13.3.3"),sQuery(id+"F7.wireOp",EDGE,"E12.13.4.0"),sQuery(id+"F7.wireOp",EDGE,"E12.13.4.1"),sQuery(id+"F7.wireOp",EDGE,"E12.13.4.2"),sQuery(id+"F7.wireOp",EDGE,"E12.13.4.3"),sQuery(id+"F7.wireOp",EDGE,"E12.13.5.0"),sQuery(id+"F7.wireOp",EDGE,"E12.13.5.1"),sQuery(id+"F7.wireOp",EDGE,"E12.13.5.2"),sQuery(id+"F7.wireOp",EDGE,"E12.13.5.3"),sQuery(id+"F7.wireOp",EDGE,"E12.13.6.0"),sQuery(id+"F7.wireOp",EDGE,"E12.13.6.1"),sQuery(id+"F7.wireOp",EDGE,"E12.13.6.2"),sQuery(id+"F7.wireOp",EDGE,"E12.13.6.3"),sQuery(id+"F7.wireOp",EDGE,"E12.13.7.0"),sQuery(id+"F7.wireOp",EDGE,"E12.13.7.1"),sQuery(id+"F7.wireOp",EDGE,"E12.13.7.2"),sQuery(id+"F7.wireOp",EDGE,"E12.13.7.3"),sQuery(id+"F7.wireOp",EDGE,"E12.13.8.0"),sQuery(id+"F7.wireOp",EDGE,"E12.13.8.1"),sQuery(id+"F7.wireOp",EDGE,"E12.13.8.2"),sQuery(id+"F7.wireOp",EDGE,"E12.13.8.3"),sQuery(id+"F7.wireOp",EDGE,"E12.13.9.0"),sQuery(id+"F7.wireOp",EDGE,"E12.13.9.1"),sQuery(id+"F7.wireOp",EDGE,"E12.13.9.2"),sQuery(id+"F7.wireOp",EDGE,"E12.13.9.3"),sQuery(id+"F7.wireOp",EDGE,"E12.13.10.0"),sQuery(id+"F7.wireOp",EDGE,"E12.13.10.1"),sQuery(id+"F7.wireOp",EDGE,"E12.13.10.2"),sQuery(id+"F7.wireOp",EDGE,"E12.13.10.3"),sQuery(id+"F7.wireOp",EDGE,"E12.13.11.0"),sQuery(id+"F7.wireOp",EDGE,"E12.13.11.1"),sQuery(id+"F7.wireOp",EDGE,"E12.13.11.2"),sQuery(id+"F7.wireOp",EDGE,"E12.13.11.3"),sQuery(id+"F7.wireOp",EDGE,"E12.13.12.0"),sQuery(id+"F7.wireOp",EDGE,"E12.13.12.1"),sQuery(id+"F7.wireOp",EDGE,"E12.13.12.2"),sQuery(id+"F7.wireOp",EDGE,"E12.13.12.3"),sQuery(id+"F7.wireOp",EDGE,"E12.13.13.0"),sQuery(id+"F7.wireOp",EDGE,"E12.13.13.1"),sQuery(id+"F7.wireOp",EDGE,"E12.13.13.2"),sQuery(id+"F7.wireOp",EDGE,"E12.13.13.3"),sQuery(id+"F7.wireOp",EDGE,"E12.13.14.0"),sQuery(id+"F7.wireOp",EDGE,"E12.13.14.1"),sQuery(id+"F7.wireOp",EDGE,"E12.13.14.2"),sQuery(id+"F7.wireOp",EDGE,"E12.13.14.3"),sQuery(id+"F7.wireOp",EDGE,"E12.13.15.0"),sQuery(id+"F7.wireOp",EDGE,"E12.13.15.1"),sQuery(id+"F7.wireOp",EDGE,"E12.13.15.2"),sQuery(id+"F7.wireOp",EDGE,"E12.13.15.3"),sQuery(id+"F7.wireOp",EDGE,"E12.14.0.0"),sQuery(id+"F7.wireOp",EDGE,"E12.14.0.1"),sQuery(id+"F7.wireOp",EDGE,"E12.14.0.2"),sQuery(id+"F7.wireOp",EDGE,"E12.14.0.3"),sQuery(id+"F7.wireOp",EDGE,"E12.14.1.0"),sQuery(id+"F7.wireOp",EDGE,"E12.14.1.1"),sQuery(id+"F7.wireOp",EDGE,"E12.14.1.2"),sQuery(id+"F7.wireOp",EDGE,"E12.14.1.3"),sQuery(id+"F7.wireOp",EDGE,"E12.14.2.0"),sQuery(id+"F7.wireOp",EDGE,"E12.14.2.1"),sQuery(id+"F7.wireOp",EDGE,"E12.14.2.2"),sQuery(id+"F7.wireOp",EDGE,"E12.14.2.3"),sQuery(id+"F7.wireOp",EDGE,"E12.14.3.0"),sQuery(id+"F7.wireOp",EDGE,"E12.14.3.1"),sQuery(id+"F7.wireOp",EDGE,"E12.14.3.2"),sQuery(id+"F7.wireOp",EDGE,"E12.14.3.3"),sQuery(id+"F7.wireOp",EDGE,"E12.14.4.0"),sQuery(id+"F7.wireOp",EDGE,"E12.14.4.1"),sQuery(id+"F7.wireOp",EDGE,"E12.14.4.2"),sQuery(id+"F7.wireOp",EDGE,"E12.14.4.3"),sQuery(id+"F7.wireOp",EDGE,"E12.14.5.0"),sQuery(id+"F7.wireOp",EDGE,"E12.14.5.1"),sQuery(id+"F7.wireOp",EDGE,"E12.14.5.2"),sQuery(id+"F7.wireOp",EDGE,"E12.14.5.3"),sQuery(id+"F7.wireOp",EDGE,"E12.14.6.0"),sQuery(id+"F7.wireOp",EDGE,"E12.14.6.1"),sQuery(id+"F7.wireOp",EDGE,"E12.14.6.2"),sQuery(id+"F7.wireOp",EDGE,"E12.14.6.3"),sQuery(id+"F7.wireOp",EDGE,"E12.14.7.0"),sQuery(id+"F7.wireOp",EDGE,"E12.14.7.1"),sQuery(id+"F7.wireOp",EDGE,"E12.14.7.2"),sQuery(id+"F7.wireOp",EDGE,"E12.14.7.3"),sQuery(id+"F7.wireOp",EDGE,"E12.14.8.0"),sQuery(id+"F7.wireOp",EDGE,"E12.14.8.1"),sQuery(id+"F7.wireOp",EDGE,"E12.14.8.2"),sQuery(id+"F7.wireOp",EDGE,"E12.14.8.3"),sQuery(id+"F7.wireOp",EDGE,"E12.14.9.0"),sQuery(id+"F7.wireOp",EDGE,"E12.14.9.1"),sQuery(id+"F7.wireOp",EDGE,"E12.14.9.2"),sQuery(id+"F7.wireOp",EDGE,"E12.14.9.3"),sQuery(id+"F7.wireOp",EDGE,"E12.14.10.0"),sQuery(id+"F7.wireOp",EDGE,"E12.14.10.1"),sQuery(id+"F7.wireOp",EDGE,"E12.14.10.2"),sQuery(id+"F7.wireOp",EDGE,"E12.14.10.3"),sQuery(id+"F7.wireOp",EDGE,"E12.14.11.0"),sQuery(id+"F7.wireOp",EDGE,"E12.14.11.1"),sQuery(id+"F7.wireOp",EDGE,"E12.14.11.2"),sQuery(id+"F7.wireOp",EDGE,"E12.14.11.3"),sQuery(id+"F7.wireOp",EDGE,"E12.14.12.0"),sQuery(id+"F7.wireOp",EDGE,"E12.14.12.1"),sQuery(id+"F7.wireOp",EDGE,"E12.14.12.2"),sQuery(id+"F7.wireOp",EDGE,"E12.14.12.3"),sQuery(id+"F7.wireOp",EDGE,"E12.14.13.0"),sQuery(id+"F7.wireOp",EDGE,"E12.14.13.1"),sQuery(id+"F7.wireOp",EDGE,"E12.14.13.2"),sQuery(id+"F7.wireOp",EDGE,"E12.14.13.3"),sQuery(id+"F7.wireOp",EDGE,"E12.14.14.0"),sQuery(id+"F7.wireOp",EDGE,"E12.14.14.1"),sQuery(id+"F7.wireOp",EDGE,"E12.14.14.2"),sQuery(id+"F7.wireOp",EDGE,"E12.14.14.3"),sQuery(id+"F7.wireOp",EDGE,"E12.14.15.0"),sQuery(id+"F7.wireOp",EDGE,"E12.14.15.1"),sQuery(id+"F7.wireOp",EDGE,"E12.14.15.2"),sQuery(id+"F7.wireOp",EDGE,"E12.14.15.3"),sQuery(id+"F7.wireOp",EDGE,"E12.15.0.0"),sQuery(id+"F7.wireOp",EDGE,"E12.15.0.1"),sQuery(id+"F7.wireOp",EDGE,"E12.15.0.2"),sQuery(id+"F7.wireOp",EDGE,"E12.15.0.3"),sQuery(id+"F7.wireOp",EDGE,"E12.15.1.0"),sQuery(id+"F7.wireOp",EDGE,"E12.15.1.1"),sQuery(id+"F7.wireOp",EDGE,"E12.15.1.2"),sQuery(id+"F7.wireOp",EDGE,"E12.15.1.3"),sQuery(id+"F7.wireOp",EDGE,"E12.15.2.0"),sQuery(id+"F7.wireOp",EDGE,"E12.15.2.1"),sQuery(id+"F7.wireOp",EDGE,"E12.15.2.2"),sQuery(id+"F7.wireOp",EDGE,"E12.15.2.3"),sQuery(id+"F7.wireOp",EDGE,"E12.15.3.0"),sQuery(id+"F7.wireOp",EDGE,"E12.15.3.1"),sQuery(id+"F7.wireOp",EDGE,"E12.15.3.2"),sQuery(id+"F7.wireOp",EDGE,"E12.15.3.3"),sQuery(id+"F7.wireOp",EDGE,"E12.15.4.0"),sQuery(id+"F7.wireOp",EDGE,"E12.15.4.1"),sQuery(id+"F7.wireOp",EDGE,"E12.15.4.2"),sQuery(id+"F7.wireOp",EDGE,"E12.15.4.3"),sQuery(id+"F7.wireOp",EDGE,"E12.15.5.0"),sQuery(id+"F7.wireOp",EDGE,"E12.15.5.1"),sQuery(id+"F7.wireOp",EDGE,"E12.15.5.2"),sQuery(id+"F7.wireOp",EDGE,"E12.15.5.3"),sQuery(id+"F7.wireOp",EDGE,"E12.15.6.0"),sQuery(id+"F7.wireOp",EDGE,"E12.15.6.1"),sQuery(id+"F7.wireOp",EDGE,"E12.15.6.2"),sQuery(id+"F7.wireOp",EDGE,"E12.15.6.3"),sQuery(id+"F7.wireOp",EDGE,"E12.15.7.0"),sQuery(id+"F7.wireOp",EDGE,"E12.15.7.1"),sQuery(id+"F7.wireOp",EDGE,"E12.15.7.2"),sQuery(id+"F7.wireOp",EDGE,"E12.15.7.3"),sQuery(id+"F7.wireOp",EDGE,"E12.15.8.0"),sQuery(id+"F7.wireOp",EDGE,"E12.15.8.1"),sQuery(id+"F7.wireOp",EDGE,"E12.15.8.2"),sQuery(id+"F7.wireOp",EDGE,"E12.15.8.3"),sQuery(id+"F7.wireOp",EDGE,"E12.15.9.0"),sQuery(id+"F7.wireOp",EDGE,"E12.15.9.1"),sQuery(id+"F7.wireOp",EDGE,"E12.15.9.2"),sQuery(id+"F7.wireOp",EDGE,"E12.15.9.3"),sQuery(id+"F7.wireOp",EDGE,"E12.15.10.0"),sQuery(id+"F7.wireOp",EDGE,"E12.15.10.1"),sQuery(id+"F7.wireOp",EDGE,"E12.15.10.2"),sQuery(id+"F7.wireOp",EDGE,"E12.15.10.3"),sQuery(id+"F7.wireOp",EDGE,"E12.15.11.0"),sQuery(id+"F7.wireOp",EDGE,"E12.15.11.1"),sQuery(id+"F7.wireOp",EDGE,"E12.15.11.2"),sQuery(id+"F7.wireOp",EDGE,"E12.15.11.3"),sQuery(id+"F7.wireOp",EDGE,"E12.15.12.0"),sQuery(id+"F7.wireOp",EDGE,"E12.15.12.1"),sQuery(id+"F7.wireOp",EDGE,"E12.15.12.2"),sQuery(id+"F7.wireOp",EDGE,"E12.15.12.3"),sQuery(id+"F7.wireOp",EDGE,"E12.15.13.0"),sQuery(id+"F7.wireOp",EDGE,"E12.15.13.1"),sQuery(id+"F7.wireOp",EDGE,"E12.15.13.2"),sQuery(id+"F7.wireOp",EDGE,"E12.15.13.3"),sQuery(id+"F7.wireOp",EDGE,"E12.15.14.0"),sQuery(id+"F7.wireOp",EDGE,"E12.15.14.1"),sQuery(id+"F7.wireOp",EDGE,"E12.15.14.2"),sQuery(id+"F7.wireOp",EDGE,"E12.15.14.3"),sQuery(id+"F7.wireOp",EDGE,"E12.15.15.0"),sQuery(id+"F7.wireOp",EDGE,"E12.15.15.1"),sQuery(id+"F7.wireOp",EDGE,"E12.15.15.2"),sQuery(id+"F7.wireOp",EDGE,"E12.15.15.3")])]});
            booleanBodies(context, id + "F24", {"operationType" : BooleanOperationType.SUBTRACTION, "tools" : qUnion([Q0, Q1, Q2, Q3]), "targets" : qUnion([Q4, Q5, Q6])});
        }
    });
